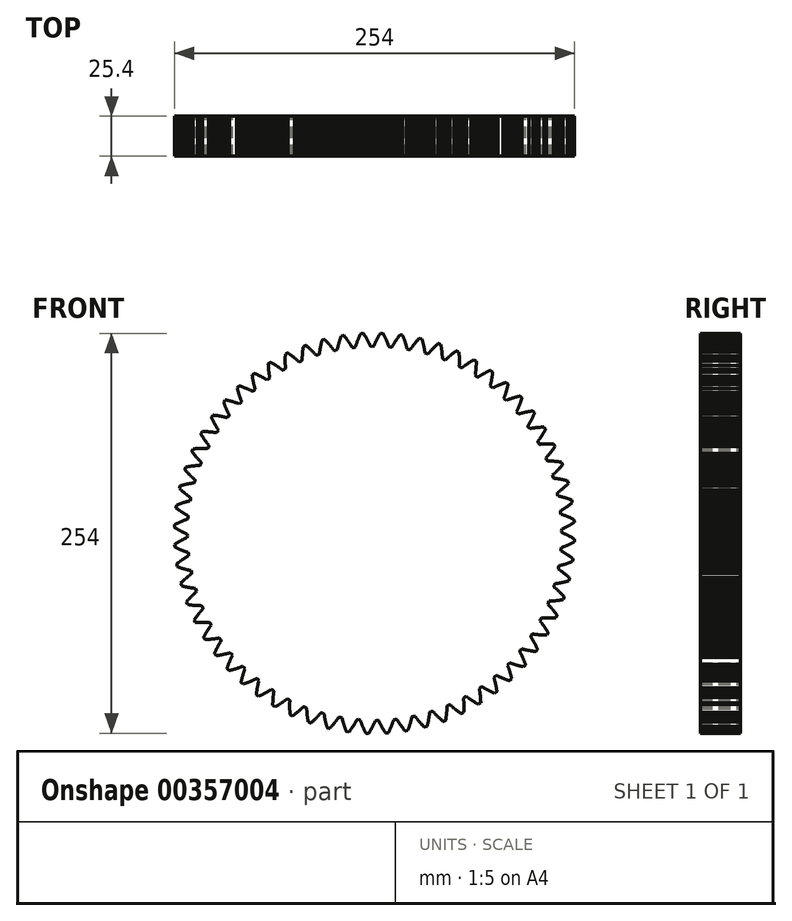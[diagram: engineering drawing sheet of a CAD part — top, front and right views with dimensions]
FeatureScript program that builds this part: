
annotation { "Feature Type Name" : "Feature", "Feature Type Description" : "" }
export const myFeature = defineFeature(function(context is Context, id is Id, definition is map)
    precondition{}
    {
        {
            var Q0;
            Q0=qCreatedBy(makeId("Front.planeOp"),FACE);
            var sketch = newSketch(context, id + "F0", { "sketchPlane" : qUnion([Q0])});
            skLineSegment(sketch, "E0", {"start": v(118.77, 2.66) * mm, "end": v(119, 3.75) * mm});
            skLineSegment(sketch, "E1", {"start": v(119, 3.75) * mm, "end": v(119.22, 3.85) * mm});
            skLineSegment(sketch, "E2", {"start": v(119.22, 3.85) * mm, "end": v(119.46, 3.96) * mm});
            skLineSegment(sketch, "E3", {"start": v(119.46, 3.96) * mm, "end": v(119.7, 4.07) * mm});
            skLineSegment(sketch, "E4", {"start": v(119.7, 4.07) * mm, "end": v(119.93, 4.18) * mm});
            skLineSegment(sketch, "E5", {"start": v(119.93, 4.18) * mm, "end": v(120.17, 4.3) * mm});
            skLineSegment(sketch, "E6", {"start": v(120.17, 4.3) * mm, "end": v(120.41, 4.4) * mm});
            skLineSegment(sketch, "E7", {"start": v(120.41, 4.4) * mm, "end": v(120.65, 4.53) * mm});
            skLineSegment(sketch, "E8", {"start": v(120.65, 4.53) * mm, "end": v(120.9, 4.65) * mm});
            skLineSegment(sketch, "E9", {"start": v(120.9, 4.65) * mm, "end": v(121.15, 4.78) * mm});
            skLineSegment(sketch, "E10", {"start": v(121.15, 4.78) * mm, "end": v(121.4, 4.9) * mm});
            skLineSegment(sketch, "E11", {"start": v(121.4, 4.9) * mm, "end": v(121.65, 5.03) * mm});
            skLineSegment(sketch, "E12", {"start": v(121.65, 5.03) * mm, "end": v(121.91, 5.17) * mm});
            skLineSegment(sketch, "E13", {"start": v(121.91, 5.17) * mm, "end": v(122.17, 5.3) * mm});
            skLineSegment(sketch, "E14", {"start": v(122.17, 5.3) * mm, "end": v(122.43, 5.44) * mm});
            skLineSegment(sketch, "E15", {"start": v(122.43, 5.44) * mm, "end": v(122.69, 5.59) * mm});
            skLineSegment(sketch, "E16", {"start": v(122.69, 5.59) * mm, "end": v(122.96, 5.73) * mm});
            skLineSegment(sketch, "E17", {"start": v(122.96, 5.73) * mm, "end": v(123.22, 5.88) * mm});
            skLineSegment(sketch, "E18", {"start": v(123.22, 5.88) * mm, "end": v(123.49, 6.03) * mm});
            skLineSegment(sketch, "E19", {"start": v(123.49, 6.03) * mm, "end": v(123.76, 6.19) * mm});
            skLineSegment(sketch, "E20", {"start": v(123.76, 6.19) * mm, "end": v(124.03, 6.34) * mm});
            skLineSegment(sketch, "E21", {"start": v(124.03, 6.34) * mm, "end": v(124.3, 6.5) * mm});
            skLineSegment(sketch, "E22", {"start": v(124.3, 6.5) * mm, "end": v(124.58, 6.67) * mm});
            skLineSegment(sketch, "E23", {"start": v(124.58, 6.67) * mm, "end": v(124.86, 6.84) * mm});
            skLineSegment(sketch, "E24", {"start": v(124.86, 6.84) * mm, "end": v(125.14, 7) * mm});
            skLineSegment(sketch, "E25", {"start": v(125.14, 7) * mm, "end": v(125.42, 7.18) * mm});
            skLineSegment(sketch, "E26", {"start": v(125.42, 7.18) * mm, "end": v(125.7, 7.36) * mm});
            skLineSegment(sketch, "E27", {"start": v(125.7, 7.36) * mm, "end": v(125.99, 7.54) * mm});
            skLineSegment(sketch, "E28", {"start": v(125.99, 7.54) * mm, "end": v(126.27, 7.72) * mm});
            skLineSegment(sketch, "E29", {"start": v(126.27, 7.72) * mm, "end": v(126.56, 7.9) * mm});
            skLineSegment(sketch, "E30", {"start": v(126.56, 7.9) * mm, "end": v(126.85, 8.1) * mm});
            skLineSegment(sketch, "E31", {"start": v(126.85, 8.1) * mm, "end": v(126.86, 8.27) * mm});
            skLineSegment(sketch, "E32", {"start": v(126.86, 8.27) * mm, "end": v(126.77, 9.72) * mm});
            skLineSegment(sketch, "E33", {"start": v(126.77, 9.72) * mm, "end": v(126.74, 9.9) * mm});
            skLineSegment(sketch, "E34", {"start": v(126.74, 9.9) * mm, "end": v(126.43, 10.05) * mm});
            skLineSegment(sketch, "E35", {"start": v(126.43, 10.05) * mm, "end": v(126.12, 10.2) * mm});
            skLineSegment(sketch, "E36", {"start": v(126.12, 10.2) * mm, "end": v(125.81, 10.34) * mm});
            skLineSegment(sketch, "E37", {"start": v(125.81, 10.34) * mm, "end": v(125.5, 10.49) * mm});
            skLineSegment(sketch, "E38", {"start": v(125.5, 10.49) * mm, "end": v(125.2, 10.63) * mm});
            skLineSegment(sketch, "E39", {"start": v(125.2, 10.63) * mm, "end": v(124.9, 10.76) * mm});
            skLineSegment(sketch, "E40", {"start": v(124.9, 10.76) * mm, "end": v(124.6, 10.9) * mm});
            skLineSegment(sketch, "E41", {"start": v(124.6, 10.9) * mm, "end": v(124.3, 11.03) * mm});
            skLineSegment(sketch, "E42", {"start": v(124.3, 11.03) * mm, "end": v(124.02, 11.16) * mm});
            skLineSegment(sketch, "E43", {"start": v(124.02, 11.16) * mm, "end": v(123.72, 11.28) * mm});
            skLineSegment(sketch, "E44", {"start": v(123.72, 11.28) * mm, "end": v(123.43, 11.4) * mm});
            skLineSegment(sketch, "E45", {"start": v(123.43, 11.4) * mm, "end": v(123.15, 11.53) * mm});
            skLineSegment(sketch, "E46", {"start": v(123.15, 11.53) * mm, "end": v(122.86, 11.64) * mm});
            skLineSegment(sketch, "E47", {"start": v(122.86, 11.64) * mm, "end": v(122.58, 11.76) * mm});
            skLineSegment(sketch, "E48", {"start": v(122.58, 11.76) * mm, "end": v(122.3, 11.87) * mm});
            skLineSegment(sketch, "E49", {"start": v(122.3, 11.87) * mm, "end": v(122.02, 11.98) * mm});
            skLineSegment(sketch, "E50", {"start": v(122.02, 11.98) * mm, "end": v(121.75, 12.09) * mm});
            skLineSegment(sketch, "E51", {"start": v(121.75, 12.09) * mm, "end": v(121.47, 12.19) * mm});
            skLineSegment(sketch, "E52", {"start": v(121.47, 12.19) * mm, "end": v(121.2, 12.29) * mm});
            skLineSegment(sketch, "E53", {"start": v(121.2, 12.29) * mm, "end": v(120.94, 12.39) * mm});
            skLineSegment(sketch, "E54", {"start": v(120.94, 12.39) * mm, "end": v(120.67, 12.48) * mm});
            skLineSegment(sketch, "E55", {"start": v(120.67, 12.48) * mm, "end": v(120.4, 12.58) * mm});
            skLineSegment(sketch, "E56", {"start": v(120.4, 12.58) * mm, "end": v(120.15, 12.67) * mm});
            skLineSegment(sketch, "E57", {"start": v(120.15, 12.67) * mm, "end": v(119.9, 12.75) * mm});
            skLineSegment(sketch, "E58", {"start": v(119.9, 12.75) * mm, "end": v(119.64, 12.84) * mm});
            skLineSegment(sketch, "E59", {"start": v(119.64, 12.84) * mm, "end": v(119.39, 12.92) * mm});
            skLineSegment(sketch, "E60", {"start": v(119.39, 12.92) * mm, "end": v(119.13, 13) * mm});
            skLineSegment(sketch, "E61", {"start": v(119.13, 13) * mm, "end": v(118.89, 13.08) * mm});
            skLineSegment(sketch, "E62", {"start": v(118.89, 13.08) * mm, "end": v(118.64, 13.16) * mm});
            skLineSegment(sketch, "E63", {"start": v(118.64, 13.16) * mm, "end": v(118.4, 13.23) * mm});
            skLineSegment(sketch, "E64", {"start": v(118.4, 13.23) * mm, "end": v(118.05, 14.3) * mm});
            skLineSegment(sketch, "E65", {"start": v(118.05, 14.3) * mm, "end": v(118.16, 15.4) * mm});
            skLineSegment(sketch, "E66", {"start": v(118.16, 15.4) * mm, "end": v(118.38, 15.52) * mm});
            skLineSegment(sketch, "E67", {"start": v(118.38, 15.52) * mm, "end": v(118.6, 15.65) * mm});
            skLineSegment(sketch, "E68", {"start": v(118.6, 15.65) * mm, "end": v(118.83, 15.78) * mm});
            skLineSegment(sketch, "E69", {"start": v(118.83, 15.78) * mm, "end": v(119.05, 15.92) * mm});
            skLineSegment(sketch, "E70", {"start": v(119.05, 15.92) * mm, "end": v(119.28, 16.05) * mm});
            skLineSegment(sketch, "E71", {"start": v(119.28, 16.05) * mm, "end": v(119.5, 16.2) * mm});
            skLineSegment(sketch, "E72", {"start": v(119.5, 16.2) * mm, "end": v(119.74, 16.34) * mm});
            skLineSegment(sketch, "E73", {"start": v(119.74, 16.34) * mm, "end": v(119.97, 16.48) * mm});
            skLineSegment(sketch, "E74", {"start": v(119.97, 16.48) * mm, "end": v(120.2, 16.63) * mm});
            skLineSegment(sketch, "E75", {"start": v(120.2, 16.63) * mm, "end": v(120.44, 16.78) * mm});
            skLineSegment(sketch, "E76", {"start": v(120.44, 16.78) * mm, "end": v(120.68, 16.94) * mm});
            skLineSegment(sketch, "E77", {"start": v(120.68, 16.94) * mm, "end": v(120.93, 17.1) * mm});
            skLineSegment(sketch, "E78", {"start": v(120.93, 17.1) * mm, "end": v(121.17, 17.26) * mm});
            skLineSegment(sketch, "E79", {"start": v(121.17, 17.26) * mm, "end": v(121.41, 17.42) * mm});
            skLineSegment(sketch, "E80", {"start": v(121.41, 17.42) * mm, "end": v(121.66, 17.59) * mm});
            skLineSegment(sketch, "E81", {"start": v(121.66, 17.59) * mm, "end": v(121.9, 17.76) * mm});
            skLineSegment(sketch, "E82", {"start": v(121.9, 17.76) * mm, "end": v(122.16, 17.93) * mm});
            skLineSegment(sketch, "E83", {"start": v(122.16, 17.93) * mm, "end": v(122.41, 18.11) * mm});
            skLineSegment(sketch, "E84", {"start": v(122.41, 18.11) * mm, "end": v(122.67, 18.3) * mm});
            skLineSegment(sketch, "E85", {"start": v(122.67, 18.3) * mm, "end": v(122.92, 18.47) * mm});
            skLineSegment(sketch, "E86", {"start": v(122.92, 18.47) * mm, "end": v(123.18, 18.66) * mm});
            skLineSegment(sketch, "E87", {"start": v(123.18, 18.66) * mm, "end": v(123.44, 18.85) * mm});
            skLineSegment(sketch, "E88", {"start": v(123.44, 18.85) * mm, "end": v(123.7, 19.05) * mm});
            skLineSegment(sketch, "E89", {"start": v(123.7, 19.05) * mm, "end": v(123.96, 19.24) * mm});
            skLineSegment(sketch, "E90", {"start": v(123.96, 19.24) * mm, "end": v(124.22, 19.44) * mm});
            skLineSegment(sketch, "E91", {"start": v(124.22, 19.44) * mm, "end": v(124.48, 19.65) * mm});
            skLineSegment(sketch, "E92", {"start": v(124.48, 19.65) * mm, "end": v(124.75, 19.85) * mm});
            skLineSegment(sketch, "E93", {"start": v(124.75, 19.85) * mm, "end": v(125.02, 20.06) * mm});
            skLineSegment(sketch, "E94", {"start": v(125.02, 20.06) * mm, "end": v(125.29, 20.28) * mm});
            skLineSegment(sketch, "E95", {"start": v(125.29, 20.28) * mm, "end": v(125.56, 20.5) * mm});
            skLineSegment(sketch, "E96", {"start": v(125.56, 20.5) * mm, "end": v(125.54, 20.67) * mm});
            skLineSegment(sketch, "E97", {"start": v(125.54, 20.67) * mm, "end": v(125.31, 22.1) * mm});
            skLineSegment(sketch, "E98", {"start": v(125.31, 22.1) * mm, "end": v(125.27, 22.27) * mm});
            skLineSegment(sketch, "E99", {"start": v(125.27, 22.27) * mm, "end": v(124.95, 22.4) * mm});
            skLineSegment(sketch, "E100", {"start": v(124.95, 22.4) * mm, "end": v(124.62, 22.51) * mm});
            skLineSegment(sketch, "E101", {"start": v(124.62, 22.51) * mm, "end": v(124.3, 22.63) * mm});
            skLineSegment(sketch, "E102", {"start": v(124.3, 22.63) * mm, "end": v(123.99, 22.74) * mm});
            skLineSegment(sketch, "E103", {"start": v(123.99, 22.74) * mm, "end": v(123.67, 22.85) * mm});
            skLineSegment(sketch, "E104", {"start": v(123.67, 22.85) * mm, "end": v(123.35, 22.96) * mm});
            skLineSegment(sketch, "E105", {"start": v(123.35, 22.96) * mm, "end": v(123.05, 23.06) * mm});
            skLineSegment(sketch, "E106", {"start": v(123.05, 23.06) * mm, "end": v(122.74, 23.17) * mm});
            skLineSegment(sketch, "E107", {"start": v(122.74, 23.17) * mm, "end": v(122.43, 23.27) * mm});
            skLineSegment(sketch, "E108", {"start": v(122.43, 23.27) * mm, "end": v(122.13, 23.36) * mm});
            skLineSegment(sketch, "E109", {"start": v(122.13, 23.36) * mm, "end": v(121.83, 23.46) * mm});
            skLineSegment(sketch, "E110", {"start": v(121.83, 23.46) * mm, "end": v(121.53, 23.55) * mm});
            skLineSegment(sketch, "E111", {"start": v(121.53, 23.55) * mm, "end": v(121.24, 23.64) * mm});
            skLineSegment(sketch, "E112", {"start": v(121.24, 23.64) * mm, "end": v(120.94, 23.72) * mm});
            skLineSegment(sketch, "E113", {"start": v(120.94, 23.72) * mm, "end": v(120.65, 23.8) * mm});
            skLineSegment(sketch, "E114", {"start": v(120.65, 23.8) * mm, "end": v(120.37, 23.89) * mm});
            skLineSegment(sketch, "E115", {"start": v(120.37, 23.89) * mm, "end": v(120.08, 23.96) * mm});
            skLineSegment(sketch, "E116", {"start": v(120.08, 23.96) * mm, "end": v(119.8, 24.04) * mm});
            skLineSegment(sketch, "E117", {"start": v(119.8, 24.04) * mm, "end": v(119.52, 24.12) * mm});
            skLineSegment(sketch, "E118", {"start": v(119.52, 24.12) * mm, "end": v(119.25, 24.19) * mm});
            skLineSegment(sketch, "E119", {"start": v(119.25, 24.19) * mm, "end": v(118.97, 24.26) * mm});
            skLineSegment(sketch, "E120", {"start": v(118.97, 24.26) * mm, "end": v(118.7, 24.32) * mm});
            skLineSegment(sketch, "E121", {"start": v(118.7, 24.32) * mm, "end": v(118.44, 24.39) * mm});
            skLineSegment(sketch, "E122", {"start": v(118.44, 24.39) * mm, "end": v(118.17, 24.45) * mm});
            skLineSegment(sketch, "E123", {"start": v(118.17, 24.45) * mm, "end": v(117.91, 24.51) * mm});
            skLineSegment(sketch, "E124", {"start": v(117.91, 24.51) * mm, "end": v(117.65, 24.57) * mm});
            skLineSegment(sketch, "E125", {"start": v(117.65, 24.57) * mm, "end": v(117.4, 24.63) * mm});
            skLineSegment(sketch, "E126", {"start": v(117.4, 24.63) * mm, "end": v(117.14, 24.68) * mm});
            skLineSegment(sketch, "E127", {"start": v(117.14, 24.68) * mm, "end": v(116.9, 24.73) * mm});
            skLineSegment(sketch, "E128", {"start": v(116.9, 24.73) * mm, "end": v(116.64, 24.78) * mm});
            skLineSegment(sketch, "E129", {"start": v(116.64, 24.78) * mm, "end": v(116.19, 25.8) * mm});
            skLineSegment(sketch, "E130", {"start": v(116.19, 25.8) * mm, "end": v(116.2, 26.91) * mm});
            skLineSegment(sketch, "E131", {"start": v(116.2, 26.91) * mm, "end": v(116.4, 27.06) * mm});
            skLineSegment(sketch, "E132", {"start": v(116.4, 27.06) * mm, "end": v(116.6, 27.2) * mm});
            skLineSegment(sketch, "E133", {"start": v(116.6, 27.2) * mm, "end": v(116.81, 27.36) * mm});
            skLineSegment(sketch, "E134", {"start": v(116.81, 27.36) * mm, "end": v(117.02, 27.52) * mm});
            skLineSegment(sketch, "E135", {"start": v(117.02, 27.52) * mm, "end": v(117.24, 27.67) * mm});
            skLineSegment(sketch, "E136", {"start": v(117.24, 27.67) * mm, "end": v(117.45, 27.84) * mm});
            skLineSegment(sketch, "E137", {"start": v(117.45, 27.84) * mm, "end": v(117.67, 28) * mm});
            skLineSegment(sketch, "E138", {"start": v(117.67, 28) * mm, "end": v(117.89, 28.17) * mm});
            skLineSegment(sketch, "E139", {"start": v(117.89, 28.17) * mm, "end": v(118.1, 28.34) * mm});
            skLineSegment(sketch, "E140", {"start": v(118.1, 28.34) * mm, "end": v(118.33, 28.51) * mm});
            skLineSegment(sketch, "E141", {"start": v(118.33, 28.51) * mm, "end": v(118.55, 28.7) * mm});
            skLineSegment(sketch, "E142", {"start": v(118.55, 28.7) * mm, "end": v(118.78, 28.87) * mm});
            skLineSegment(sketch, "E143", {"start": v(118.78, 28.87) * mm, "end": v(119, 29.06) * mm});
            skLineSegment(sketch, "E144", {"start": v(119, 29.06) * mm, "end": v(119.23, 29.24) * mm});
            skLineSegment(sketch, "E145", {"start": v(119.23, 29.24) * mm, "end": v(119.46, 29.44) * mm});
            skLineSegment(sketch, "E146", {"start": v(119.46, 29.44) * mm, "end": v(119.69, 29.63) * mm});
            skLineSegment(sketch, "E147", {"start": v(119.69, 29.63) * mm, "end": v(119.92, 29.83) * mm});
            skLineSegment(sketch, "E148", {"start": v(119.92, 29.83) * mm, "end": v(120.16, 30.03) * mm});
            skLineSegment(sketch, "E149", {"start": v(120.16, 30.03) * mm, "end": v(120.39, 30.23) * mm});
            skLineSegment(sketch, "E150", {"start": v(120.39, 30.23) * mm, "end": v(120.63, 30.44) * mm});
            skLineSegment(sketch, "E151", {"start": v(120.63, 30.44) * mm, "end": v(120.86, 30.65) * mm});
            skLineSegment(sketch, "E152", {"start": v(120.86, 30.65) * mm, "end": v(121.1, 30.87) * mm});
            skLineSegment(sketch, "E153", {"start": v(121.1, 30.87) * mm, "end": v(121.34, 31.08) * mm});
            skLineSegment(sketch, "E154", {"start": v(121.34, 31.08) * mm, "end": v(121.58, 31.3) * mm});
            skLineSegment(sketch, "E155", {"start": v(121.58, 31.3) * mm, "end": v(121.83, 31.53) * mm});
            skLineSegment(sketch, "E156", {"start": v(121.83, 31.53) * mm, "end": v(122.07, 31.76) * mm});
            skLineSegment(sketch, "E157", {"start": v(122.07, 31.76) * mm, "end": v(122.31, 32) * mm});
            skLineSegment(sketch, "E158", {"start": v(122.31, 32) * mm, "end": v(122.56, 32.23) * mm});
            skLineSegment(sketch, "E159", {"start": v(122.56, 32.23) * mm, "end": v(122.8, 32.47) * mm});
            skLineSegment(sketch, "E160", {"start": v(122.8, 32.47) * mm, "end": v(123.05, 32.71) * mm});
            skLineSegment(sketch, "E161", {"start": v(123.05, 32.71) * mm, "end": v(123.02, 32.88) * mm});
            skLineSegment(sketch, "E162", {"start": v(123.02, 32.88) * mm, "end": v(122.65, 34.28) * mm});
            skLineSegment(sketch, "E163", {"start": v(122.65, 34.28) * mm, "end": v(122.6, 34.45) * mm});
            skLineSegment(sketch, "E164", {"start": v(122.6, 34.45) * mm, "end": v(122.26, 34.54) * mm});
            skLineSegment(sketch, "E165", {"start": v(122.26, 34.54) * mm, "end": v(121.93, 34.63) * mm});
            skLineSegment(sketch, "E166", {"start": v(121.93, 34.63) * mm, "end": v(121.6, 34.71) * mm});
            skLineSegment(sketch, "E167", {"start": v(121.6, 34.71) * mm, "end": v(121.27, 34.8) * mm});
            skLineSegment(sketch, "E168", {"start": v(121.27, 34.8) * mm, "end": v(120.94, 34.87) * mm});
            skLineSegment(sketch, "E169", {"start": v(120.94, 34.87) * mm, "end": v(120.62, 34.95) * mm});
            skLineSegment(sketch, "E170", {"start": v(120.62, 34.95) * mm, "end": v(120.3, 35.02) * mm});
            skLineSegment(sketch, "E171", {"start": v(120.3, 35.02) * mm, "end": v(119.98, 35.1) * mm});
            skLineSegment(sketch, "E172", {"start": v(119.98, 35.1) * mm, "end": v(119.67, 35.16) * mm});
            skLineSegment(sketch, "E173", {"start": v(119.67, 35.16) * mm, "end": v(119.36, 35.22) * mm});
            skLineSegment(sketch, "E174", {"start": v(119.36, 35.22) * mm, "end": v(119.05, 35.29) * mm});
            skLineSegment(sketch, "E175", {"start": v(119.05, 35.29) * mm, "end": v(118.75, 35.35) * mm});
            skLineSegment(sketch, "E176", {"start": v(118.75, 35.35) * mm, "end": v(118.45, 35.41) * mm});
            skLineSegment(sketch, "E177", {"start": v(118.45, 35.41) * mm, "end": v(118.15, 35.47) * mm});
            skLineSegment(sketch, "E178", {"start": v(118.15, 35.47) * mm, "end": v(117.85, 35.52) * mm});
            skLineSegment(sketch, "E179", {"start": v(117.85, 35.52) * mm, "end": v(117.56, 35.58) * mm});
            skLineSegment(sketch, "E180", {"start": v(117.56, 35.58) * mm, "end": v(117.26, 35.63) * mm});
            skLineSegment(sketch, "E181", {"start": v(117.26, 35.63) * mm, "end": v(116.98, 35.67) * mm});
            skLineSegment(sketch, "E182", {"start": v(116.98, 35.67) * mm, "end": v(116.7, 35.72) * mm});
            skLineSegment(sketch, "E183", {"start": v(116.7, 35.72) * mm, "end": v(116.41, 35.76) * mm});
            skLineSegment(sketch, "E184", {"start": v(116.41, 35.76) * mm, "end": v(116.13, 35.8) * mm});
            skLineSegment(sketch, "E185", {"start": v(116.13, 35.8) * mm, "end": v(115.86, 35.85) * mm});
            skLineSegment(sketch, "E186", {"start": v(115.86, 35.85) * mm, "end": v(115.58, 35.88) * mm});
            skLineSegment(sketch, "E187", {"start": v(115.58, 35.88) * mm, "end": v(115.32, 35.92) * mm});
            skLineSegment(sketch, "E188", {"start": v(115.32, 35.92) * mm, "end": v(115.05, 35.96) * mm});
            skLineSegment(sketch, "E189", {"start": v(115.05, 35.96) * mm, "end": v(114.79, 35.99) * mm});
            skLineSegment(sketch, "E190", {"start": v(114.79, 35.99) * mm, "end": v(114.52, 36.02) * mm});
            skLineSegment(sketch, "E191", {"start": v(114.52, 36.02) * mm, "end": v(114.27, 36.05) * mm});
            skLineSegment(sketch, "E192", {"start": v(114.27, 36.05) * mm, "end": v(114.01, 36.08) * mm});
            skLineSegment(sketch, "E193", {"start": v(114.01, 36.08) * mm, "end": v(113.76, 36.1) * mm});
            skLineSegment(sketch, "E194", {"start": v(113.76, 36.1) * mm, "end": v(113.2, 37.07) * mm});
            skLineSegment(sketch, "E195", {"start": v(113.2, 37.07) * mm, "end": v(113.1, 38.18) * mm});
            skLineSegment(sketch, "E196", {"start": v(113.1, 38.18) * mm, "end": v(113.3, 38.34) * mm});
            skLineSegment(sketch, "E197", {"start": v(113.3, 38.34) * mm, "end": v(113.48, 38.51) * mm});
            skLineSegment(sketch, "E198", {"start": v(113.48, 38.51) * mm, "end": v(113.68, 38.68) * mm});
            skLineSegment(sketch, "E199", {"start": v(113.68, 38.68) * mm, "end": v(113.87, 38.86) * mm});
            skLineSegment(sketch, "E200", {"start": v(113.87, 38.86) * mm, "end": v(114.07, 39.04) * mm});
            skLineSegment(sketch, "E201", {"start": v(114.07, 39.04) * mm, "end": v(114.27, 39.22) * mm});
            skLineSegment(sketch, "E202", {"start": v(114.27, 39.22) * mm, "end": v(114.47, 39.4) * mm});
            skLineSegment(sketch, "E203", {"start": v(114.47, 39.4) * mm, "end": v(114.67, 39.6) * mm});
            skLineSegment(sketch, "E204", {"start": v(114.67, 39.6) * mm, "end": v(114.87, 39.78) * mm});
            skLineSegment(sketch, "E205", {"start": v(114.87, 39.78) * mm, "end": v(115.07, 39.98) * mm});
            skLineSegment(sketch, "E206", {"start": v(115.07, 39.98) * mm, "end": v(115.28, 40.18) * mm});
            skLineSegment(sketch, "E207", {"start": v(115.28, 40.18) * mm, "end": v(115.48, 40.38) * mm});
            skLineSegment(sketch, "E208", {"start": v(115.48, 40.38) * mm, "end": v(115.69, 40.59) * mm});
            skLineSegment(sketch, "E209", {"start": v(115.69, 40.59) * mm, "end": v(115.9, 40.8) * mm});
            skLineSegment(sketch, "E210", {"start": v(115.9, 40.8) * mm, "end": v(116.1, 41) * mm});
            skLineSegment(sketch, "E211", {"start": v(116.1, 41) * mm, "end": v(116.32, 41.22) * mm});
            skLineSegment(sketch, "E212", {"start": v(116.32, 41.22) * mm, "end": v(116.53, 41.44) * mm});
            skLineSegment(sketch, "E213", {"start": v(116.53, 41.44) * mm, "end": v(116.74, 41.67) * mm});
            skLineSegment(sketch, "E214", {"start": v(116.74, 41.67) * mm, "end": v(116.95, 41.9) * mm});
            skLineSegment(sketch, "E215", {"start": v(116.95, 41.9) * mm, "end": v(117.17, 42.12) * mm});
            skLineSegment(sketch, "E216", {"start": v(117.17, 42.12) * mm, "end": v(117.39, 42.35) * mm});
            skLineSegment(sketch, "E217", {"start": v(117.39, 42.35) * mm, "end": v(117.6, 42.6) * mm});
            skLineSegment(sketch, "E218", {"start": v(117.6, 42.6) * mm, "end": v(117.82, 42.83) * mm});
            skLineSegment(sketch, "E219", {"start": v(117.82, 42.83) * mm, "end": v(118.04, 43.08) * mm});
            skLineSegment(sketch, "E220", {"start": v(118.04, 43.08) * mm, "end": v(118.26, 43.32) * mm});
            skLineSegment(sketch, "E221", {"start": v(118.26, 43.32) * mm, "end": v(118.48, 43.58) * mm});
            skLineSegment(sketch, "E222", {"start": v(118.48, 43.58) * mm, "end": v(118.7, 43.83) * mm});
            skLineSegment(sketch, "E223", {"start": v(118.7, 43.83) * mm, "end": v(118.92, 44.1) * mm});
            skLineSegment(sketch, "E224", {"start": v(118.92, 44.1) * mm, "end": v(119.14, 44.35) * mm});
            skLineSegment(sketch, "E225", {"start": v(119.14, 44.35) * mm, "end": v(119.36, 44.62) * mm});
            skLineSegment(sketch, "E226", {"start": v(119.36, 44.62) * mm, "end": v(119.31, 44.79) * mm});
            skLineSegment(sketch, "E227", {"start": v(119.31, 44.79) * mm, "end": v(118.8, 46.15) * mm});
            skLineSegment(sketch, "E228", {"start": v(118.8, 46.15) * mm, "end": v(118.73, 46.3) * mm});
            skLineSegment(sketch, "E229", {"start": v(118.73, 46.3) * mm, "end": v(118.4, 46.36) * mm});
            skLineSegment(sketch, "E230", {"start": v(118.4, 46.36) * mm, "end": v(118.05, 46.42) * mm});
            skLineSegment(sketch, "E231", {"start": v(118.05, 46.42) * mm, "end": v(117.72, 46.47) * mm});
            skLineSegment(sketch, "E232", {"start": v(117.72, 46.47) * mm, "end": v(117.38, 46.51) * mm});
            skLineSegment(sketch, "E233", {"start": v(117.38, 46.51) * mm, "end": v(117.05, 46.56) * mm});
            skLineSegment(sketch, "E234", {"start": v(117.05, 46.56) * mm, "end": v(116.72, 46.6) * mm});
            skLineSegment(sketch, "E235", {"start": v(116.72, 46.6) * mm, "end": v(116.4, 46.65) * mm});
            skLineSegment(sketch, "E236", {"start": v(116.4, 46.65) * mm, "end": v(116.08, 46.69) * mm});
            skLineSegment(sketch, "E237", {"start": v(116.08, 46.69) * mm, "end": v(115.76, 46.73) * mm});
            skLineSegment(sketch, "E238", {"start": v(115.76, 46.73) * mm, "end": v(115.44, 46.76) * mm});
            skLineSegment(sketch, "E239", {"start": v(115.44, 46.76) * mm, "end": v(115.13, 46.8) * mm});
            skLineSegment(sketch, "E240", {"start": v(115.13, 46.8) * mm, "end": v(114.82, 46.83) * mm});
            skLineSegment(sketch, "E241", {"start": v(114.82, 46.83) * mm, "end": v(114.51, 46.85) * mm});
            skLineSegment(sketch, "E242", {"start": v(114.51, 46.85) * mm, "end": v(114.2, 46.88) * mm});
            skLineSegment(sketch, "E243", {"start": v(114.2, 46.88) * mm, "end": v(113.9, 46.9) * mm});
            skLineSegment(sketch, "E244", {"start": v(113.9, 46.9) * mm, "end": v(113.61, 46.93) * mm});
            skLineSegment(sketch, "E245", {"start": v(113.61, 46.93) * mm, "end": v(113.32, 46.95) * mm});
            skLineSegment(sketch, "E246", {"start": v(113.32, 46.95) * mm, "end": v(113.03, 46.97) * mm});
            skLineSegment(sketch, "E247", {"start": v(113.03, 46.97) * mm, "end": v(112.74, 47) * mm});
            skLineSegment(sketch, "E248", {"start": v(112.74, 47) * mm, "end": v(112.45, 47) * mm});
            skLineSegment(sketch, "E249", {"start": v(112.45, 47) * mm, "end": v(112.17, 47.02) * mm});
            skLineSegment(sketch, "E250", {"start": v(112.17, 47.02) * mm, "end": v(111.9, 47.04) * mm});
            skLineSegment(sketch, "E251", {"start": v(111.9, 47.04) * mm, "end": v(111.62, 47.05) * mm});
            skLineSegment(sketch, "E252", {"start": v(111.62, 47.05) * mm, "end": v(111.35, 47.06) * mm});
            skLineSegment(sketch, "E253", {"start": v(111.35, 47.06) * mm, "end": v(111.08, 47.06) * mm});
            skLineSegment(sketch, "E254", {"start": v(111.08, 47.06) * mm, "end": v(110.81, 47.07) * mm});
            skLineSegment(sketch, "E255", {"start": v(110.81, 47.07) * mm, "end": v(110.55, 47.08) * mm});
            skLineSegment(sketch, "E256", {"start": v(110.55, 47.08) * mm, "end": v(110.3, 47.08) * mm});
            skLineSegment(sketch, "E257", {"start": v(110.3, 47.08) * mm, "end": v(110.04, 47.08) * mm});
            skLineSegment(sketch, "E258", {"start": v(110.04, 47.08) * mm, "end": v(109.78, 47.08) * mm});
            skLineSegment(sketch, "E259", {"start": v(109.78, 47.08) * mm, "end": v(109.14, 48) * mm});
            skLineSegment(sketch, "E260", {"start": v(109.14, 48) * mm, "end": v(108.92, 49.08) * mm});
            skLineSegment(sketch, "E261", {"start": v(108.92, 49.08) * mm, "end": v(109.1, 49.27) * mm});
            skLineSegment(sketch, "E262", {"start": v(109.1, 49.27) * mm, "end": v(109.27, 49.45) * mm});
            skLineSegment(sketch, "E263", {"start": v(109.27, 49.45) * mm, "end": v(109.45, 49.64) * mm});
            skLineSegment(sketch, "E264", {"start": v(109.45, 49.64) * mm, "end": v(109.62, 49.84) * mm});
            skLineSegment(sketch, "E265", {"start": v(109.62, 49.84) * mm, "end": v(109.8, 50.04) * mm});
            skLineSegment(sketch, "E266", {"start": v(109.8, 50.04) * mm, "end": v(109.98, 50.24) * mm});
            skLineSegment(sketch, "E267", {"start": v(109.98, 50.24) * mm, "end": v(110.16, 50.44) * mm});
            skLineSegment(sketch, "E268", {"start": v(110.16, 50.44) * mm, "end": v(110.34, 50.65) * mm});
            skLineSegment(sketch, "E269", {"start": v(110.34, 50.65) * mm, "end": v(110.53, 50.86) * mm});
            skLineSegment(sketch, "E270", {"start": v(110.53, 50.86) * mm, "end": v(110.7, 51.07) * mm});
            skLineSegment(sketch, "E271", {"start": v(110.7, 51.07) * mm, "end": v(110.9, 51.3) * mm});
            skLineSegment(sketch, "E272", {"start": v(110.9, 51.3) * mm, "end": v(111.08, 51.51) * mm});
            skLineSegment(sketch, "E273", {"start": v(111.08, 51.51) * mm, "end": v(111.26, 51.74) * mm});
            skLineSegment(sketch, "E274", {"start": v(111.26, 51.74) * mm, "end": v(111.45, 51.96) * mm});
            skLineSegment(sketch, "E275", {"start": v(111.45, 51.96) * mm, "end": v(111.64, 52.2) * mm});
            skLineSegment(sketch, "E276", {"start": v(111.64, 52.2) * mm, "end": v(111.82, 52.43) * mm});
            skLineSegment(sketch, "E277", {"start": v(111.82, 52.43) * mm, "end": v(112.01, 52.67) * mm});
            skLineSegment(sketch, "E278", {"start": v(112.01, 52.67) * mm, "end": v(112.2, 52.91) * mm});
            skLineSegment(sketch, "E279", {"start": v(112.2, 52.91) * mm, "end": v(112.4, 53.16) * mm});
            skLineSegment(sketch, "E280", {"start": v(112.4, 53.16) * mm, "end": v(112.59, 53.4) * mm});
            skLineSegment(sketch, "E281", {"start": v(112.59, 53.4) * mm, "end": v(112.78, 53.66) * mm});
            skLineSegment(sketch, "E282", {"start": v(112.78, 53.66) * mm, "end": v(112.97, 53.92) * mm});
            skLineSegment(sketch, "E283", {"start": v(112.97, 53.92) * mm, "end": v(113.16, 54.18) * mm});
            skLineSegment(sketch, "E284", {"start": v(113.16, 54.18) * mm, "end": v(113.36, 54.44) * mm});
            skLineSegment(sketch, "E285", {"start": v(113.36, 54.44) * mm, "end": v(113.55, 54.71) * mm});
            skLineSegment(sketch, "E286", {"start": v(113.55, 54.71) * mm, "end": v(113.74, 54.98) * mm});
            skLineSegment(sketch, "E287", {"start": v(113.74, 54.98) * mm, "end": v(113.94, 55.26) * mm});
            skLineSegment(sketch, "E288", {"start": v(113.94, 55.26) * mm, "end": v(114.13, 55.54) * mm});
            skLineSegment(sketch, "E289", {"start": v(114.13, 55.54) * mm, "end": v(114.33, 55.82) * mm});
            skLineSegment(sketch, "E290", {"start": v(114.33, 55.82) * mm, "end": v(114.52, 56.1) * mm});
            skLineSegment(sketch, "E291", {"start": v(114.52, 56.1) * mm, "end": v(114.46, 56.27) * mm});
            skLineSegment(sketch, "E292", {"start": v(114.46, 56.27) * mm, "end": v(113.82, 57.57) * mm});
            skLineSegment(sketch, "E293", {"start": v(113.82, 57.57) * mm, "end": v(113.73, 57.73) * mm});
            skLineSegment(sketch, "E294", {"start": v(113.73, 57.73) * mm, "end": v(113.38, 57.75) * mm});
            skLineSegment(sketch, "E295", {"start": v(113.38, 57.75) * mm, "end": v(113.04, 57.77) * mm});
            skLineSegment(sketch, "E296", {"start": v(113.04, 57.77) * mm, "end": v(112.7, 57.79) * mm});
            skLineSegment(sketch, "E297", {"start": v(112.7, 57.79) * mm, "end": v(112.36, 57.8) * mm});
            skLineSegment(sketch, "E298", {"start": v(112.36, 57.8) * mm, "end": v(112.03, 57.82) * mm});
            skLineSegment(sketch, "E299", {"start": v(112.03, 57.82) * mm, "end": v(111.7, 57.83) * mm});
            skLineSegment(sketch, "E300", {"start": v(111.7, 57.83) * mm, "end": v(111.37, 57.84) * mm});
            skLineSegment(sketch, "E301", {"start": v(111.37, 57.84) * mm, "end": v(111.05, 57.85) * mm});
            skLineSegment(sketch, "E302", {"start": v(111.05, 57.85) * mm, "end": v(110.73, 57.85) * mm});
            skLineSegment(sketch, "E303", {"start": v(110.73, 57.85) * mm, "end": v(110.4, 57.86) * mm});
            skLineSegment(sketch, "E304", {"start": v(110.4, 57.86) * mm, "end": v(110.1, 57.86) * mm});
            skLineSegment(sketch, "E305", {"start": v(110.1, 57.86) * mm, "end": v(109.79, 57.86) * mm});
            skLineSegment(sketch, "E306", {"start": v(109.79, 57.86) * mm, "end": v(109.48, 57.86) * mm});
            skLineSegment(sketch, "E307", {"start": v(109.48, 57.86) * mm, "end": v(109.17, 57.86) * mm});
            skLineSegment(sketch, "E308", {"start": v(109.17, 57.86) * mm, "end": v(108.87, 57.85) * mm});
            skLineSegment(sketch, "E309", {"start": v(108.87, 57.85) * mm, "end": v(108.57, 57.85) * mm});
            skLineSegment(sketch, "E310", {"start": v(108.57, 57.85) * mm, "end": v(108.28, 57.84) * mm});
            skLineSegment(sketch, "E311", {"start": v(108.28, 57.84) * mm, "end": v(107.99, 57.83) * mm});
            skLineSegment(sketch, "E312", {"start": v(107.99, 57.83) * mm, "end": v(107.7, 57.82) * mm});
            skLineSegment(sketch, "E313", {"start": v(107.7, 57.82) * mm, "end": v(107.41, 57.8) * mm});
            skLineSegment(sketch, "E314", {"start": v(107.41, 57.8) * mm, "end": v(107.13, 57.8) * mm});
            skLineSegment(sketch, "E315", {"start": v(107.13, 57.8) * mm, "end": v(106.85, 57.78) * mm});
            skLineSegment(sketch, "E316", {"start": v(106.85, 57.78) * mm, "end": v(106.58, 57.76) * mm});
            skLineSegment(sketch, "E317", {"start": v(106.58, 57.76) * mm, "end": v(106.3, 57.75) * mm});
            skLineSegment(sketch, "E318", {"start": v(106.3, 57.75) * mm, "end": v(106.04, 57.73) * mm});
            skLineSegment(sketch, "E319", {"start": v(106.04, 57.73) * mm, "end": v(105.77, 57.71) * mm});
            skLineSegment(sketch, "E320", {"start": v(105.77, 57.71) * mm, "end": v(105.51, 57.69) * mm});
            skLineSegment(sketch, "E321", {"start": v(105.51, 57.69) * mm, "end": v(105.26, 57.67) * mm});
            skLineSegment(sketch, "E322", {"start": v(105.26, 57.67) * mm, "end": v(105, 57.64) * mm});
            skLineSegment(sketch, "E323", {"start": v(105, 57.64) * mm, "end": v(104.75, 57.62) * mm});
            skLineSegment(sketch, "E324", {"start": v(104.75, 57.62) * mm, "end": v(104.02, 58.46) * mm});
            skLineSegment(sketch, "E325", {"start": v(104.02, 58.46) * mm, "end": v(103.7, 59.53) * mm});
            skLineSegment(sketch, "E326", {"start": v(103.7, 59.53) * mm, "end": v(103.85, 59.73) * mm});
            skLineSegment(sketch, "E327", {"start": v(103.85, 59.73) * mm, "end": v(104, 59.93) * mm});
            skLineSegment(sketch, "E328", {"start": v(104, 59.93) * mm, "end": v(104.16, 60.14) * mm});
            skLineSegment(sketch, "E329", {"start": v(104.16, 60.14) * mm, "end": v(104.32, 60.35) * mm});
            skLineSegment(sketch, "E330", {"start": v(104.32, 60.35) * mm, "end": v(104.48, 60.56) * mm});
            skLineSegment(sketch, "E331", {"start": v(104.48, 60.56) * mm, "end": v(104.63, 60.78) * mm});
            skLineSegment(sketch, "E332", {"start": v(104.63, 60.78) * mm, "end": v(104.8, 61) * mm});
            skLineSegment(sketch, "E333", {"start": v(104.8, 61) * mm, "end": v(104.96, 61.22) * mm});
            skLineSegment(sketch, "E334", {"start": v(104.96, 61.22) * mm, "end": v(105.12, 61.45) * mm});
            skLineSegment(sketch, "E335", {"start": v(105.12, 61.45) * mm, "end": v(105.28, 61.68) * mm});
            skLineSegment(sketch, "E336", {"start": v(105.28, 61.68) * mm, "end": v(105.44, 61.92) * mm});
            skLineSegment(sketch, "E337", {"start": v(105.44, 61.92) * mm, "end": v(105.6, 62.16) * mm});
            skLineSegment(sketch, "E338", {"start": v(105.6, 62.16) * mm, "end": v(105.76, 62.4) * mm});
            skLineSegment(sketch, "E339", {"start": v(105.76, 62.4) * mm, "end": v(105.93, 62.64) * mm});
            skLineSegment(sketch, "E340", {"start": v(105.93, 62.64) * mm, "end": v(106.1, 62.9) * mm});
            skLineSegment(sketch, "E341", {"start": v(106.1, 62.9) * mm, "end": v(106.26, 63.14) * mm});
            skLineSegment(sketch, "E342", {"start": v(106.26, 63.14) * mm, "end": v(106.42, 63.4) * mm});
            skLineSegment(sketch, "E343", {"start": v(106.42, 63.4) * mm, "end": v(106.59, 63.66) * mm});
            skLineSegment(sketch, "E344", {"start": v(106.59, 63.66) * mm, "end": v(106.75, 63.93) * mm});
            skLineSegment(sketch, "E345", {"start": v(106.75, 63.93) * mm, "end": v(106.92, 64.2) * mm});
            skLineSegment(sketch, "E346", {"start": v(106.92, 64.2) * mm, "end": v(107.08, 64.46) * mm});
            skLineSegment(sketch, "E347", {"start": v(107.08, 64.46) * mm, "end": v(107.25, 64.74) * mm});
            skLineSegment(sketch, "E348", {"start": v(107.25, 64.74) * mm, "end": v(107.42, 65.02) * mm});
            skLineSegment(sketch, "E349", {"start": v(107.42, 65.02) * mm, "end": v(107.58, 65.3) * mm});
            skLineSegment(sketch, "E350", {"start": v(107.58, 65.3) * mm, "end": v(107.75, 65.58) * mm});
            skLineSegment(sketch, "E351", {"start": v(107.75, 65.58) * mm, "end": v(107.91, 65.87) * mm});
            skLineSegment(sketch, "E352", {"start": v(107.91, 65.87) * mm, "end": v(108.08, 66.17) * mm});
            skLineSegment(sketch, "E353", {"start": v(108.08, 66.17) * mm, "end": v(108.25, 66.46) * mm});
            skLineSegment(sketch, "E354", {"start": v(108.25, 66.46) * mm, "end": v(108.41, 66.77) * mm});
            skLineSegment(sketch, "E355", {"start": v(108.41, 66.77) * mm, "end": v(108.58, 67.07) * mm});
            skLineSegment(sketch, "E356", {"start": v(108.58, 67.07) * mm, "end": v(108.5, 67.23) * mm});
            skLineSegment(sketch, "E357", {"start": v(108.5, 67.23) * mm, "end": v(107.74, 68.46) * mm});
            skLineSegment(sketch, "E358", {"start": v(107.74, 68.46) * mm, "end": v(107.64, 68.6) * mm});
            skLineSegment(sketch, "E359", {"start": v(107.64, 68.6) * mm, "end": v(107.29, 68.6) * mm});
            skLineSegment(sketch, "E360", {"start": v(107.29, 68.6) * mm, "end": v(106.94, 68.58) * mm});
            skLineSegment(sketch, "E361", {"start": v(106.94, 68.58) * mm, "end": v(106.6, 68.56) * mm});
            skLineSegment(sketch, "E362", {"start": v(106.6, 68.56) * mm, "end": v(106.27, 68.54) * mm});
            skLineSegment(sketch, "E363", {"start": v(106.27, 68.54) * mm, "end": v(105.93, 68.52) * mm});
            skLineSegment(sketch, "E364", {"start": v(105.93, 68.52) * mm, "end": v(105.6, 68.5) * mm});
            skLineSegment(sketch, "E365", {"start": v(105.6, 68.5) * mm, "end": v(105.28, 68.48) * mm});
            skLineSegment(sketch, "E366", {"start": v(105.28, 68.48) * mm, "end": v(104.95, 68.46) * mm});
            skLineSegment(sketch, "E367", {"start": v(104.95, 68.46) * mm, "end": v(104.63, 68.43) * mm});
            skLineSegment(sketch, "E368", {"start": v(104.63, 68.43) * mm, "end": v(104.32, 68.4) * mm});
            skLineSegment(sketch, "E369", {"start": v(104.32, 68.4) * mm, "end": v(104, 68.38) * mm});
            skLineSegment(sketch, "E370", {"start": v(104, 68.38) * mm, "end": v(103.7, 68.35) * mm});
            skLineSegment(sketch, "E371", {"start": v(103.7, 68.35) * mm, "end": v(103.39, 68.32) * mm});
            skLineSegment(sketch, "E372", {"start": v(103.39, 68.32) * mm, "end": v(103.09, 68.28) * mm});
            skLineSegment(sketch, "E373", {"start": v(103.09, 68.28) * mm, "end": v(102.79, 68.25) * mm});
            skLineSegment(sketch, "E374", {"start": v(102.79, 68.25) * mm, "end": v(102.49, 68.21) * mm});
            skLineSegment(sketch, "E375", {"start": v(102.49, 68.21) * mm, "end": v(102.2, 68.18) * mm});
            skLineSegment(sketch, "E376", {"start": v(102.2, 68.18) * mm, "end": v(101.9, 68.14) * mm});
            skLineSegment(sketch, "E377", {"start": v(101.9, 68.14) * mm, "end": v(101.62, 68.1) * mm});
            skLineSegment(sketch, "E378", {"start": v(101.62, 68.1) * mm, "end": v(101.34, 68.06) * mm});
            skLineSegment(sketch, "E379", {"start": v(101.34, 68.06) * mm, "end": v(101.06, 68.02) * mm});
            skLineSegment(sketch, "E380", {"start": v(101.06, 68.02) * mm, "end": v(100.78, 67.98) * mm});
            skLineSegment(sketch, "E381", {"start": v(100.78, 67.98) * mm, "end": v(100.51, 67.94) * mm});
            skLineSegment(sketch, "E382", {"start": v(100.51, 67.94) * mm, "end": v(100.24, 67.9) * mm});
            skLineSegment(sketch, "E383", {"start": v(100.24, 67.9) * mm, "end": v(99.98, 67.85) * mm});
            skLineSegment(sketch, "E384", {"start": v(99.98, 67.85) * mm, "end": v(99.72, 67.8) * mm});
            skLineSegment(sketch, "E385", {"start": v(99.72, 67.8) * mm, "end": v(99.46, 67.76) * mm});
            skLineSegment(sketch, "E386", {"start": v(99.46, 67.76) * mm, "end": v(99.2, 67.71) * mm});
            skLineSegment(sketch, "E387", {"start": v(99.2, 67.71) * mm, "end": v(98.95, 67.66) * mm});
            skLineSegment(sketch, "E388", {"start": v(98.95, 67.66) * mm, "end": v(98.7, 67.62) * mm});
            skLineSegment(sketch, "E389", {"start": v(98.7, 67.62) * mm, "end": v(97.9, 68.38) * mm});
            skLineSegment(sketch, "E390", {"start": v(97.9, 68.38) * mm, "end": v(97.47, 69.41) * mm});
            skLineSegment(sketch, "E391", {"start": v(97.47, 69.41) * mm, "end": v(97.6, 69.63) * mm});
            skLineSegment(sketch, "E392", {"start": v(97.6, 69.63) * mm, "end": v(97.74, 69.84) * mm});
            skLineSegment(sketch, "E393", {"start": v(97.74, 69.84) * mm, "end": v(97.88, 70.06) * mm});
            skLineSegment(sketch, "E394", {"start": v(97.88, 70.06) * mm, "end": v(98.01, 70.29) * mm});
            skLineSegment(sketch, "E395", {"start": v(98.01, 70.29) * mm, "end": v(98.15, 70.52) * mm});
            skLineSegment(sketch, "E396", {"start": v(98.15, 70.52) * mm, "end": v(98.28, 70.75) * mm});
            skLineSegment(sketch, "E397", {"start": v(98.28, 70.75) * mm, "end": v(98.42, 70.98) * mm});
            skLineSegment(sketch, "E398", {"start": v(98.42, 70.98) * mm, "end": v(98.56, 71.22) * mm});
            skLineSegment(sketch, "E399", {"start": v(98.56, 71.22) * mm, "end": v(98.7, 71.46) * mm});
            skLineSegment(sketch, "E400", {"start": v(98.7, 71.46) * mm, "end": v(98.83, 71.7) * mm});
            skLineSegment(sketch, "E401", {"start": v(98.83, 71.7) * mm, "end": v(98.97, 71.96) * mm});
            skLineSegment(sketch, "E402", {"start": v(98.97, 71.96) * mm, "end": v(99.1, 72.21) * mm});
            skLineSegment(sketch, "E403", {"start": v(99.1, 72.21) * mm, "end": v(99.25, 72.47) * mm});
            skLineSegment(sketch, "E404", {"start": v(99.25, 72.47) * mm, "end": v(99.39, 72.73) * mm});
            skLineSegment(sketch, "E405", {"start": v(99.39, 72.73) * mm, "end": v(99.52, 73) * mm});
            skLineSegment(sketch, "E406", {"start": v(99.52, 73) * mm, "end": v(99.66, 73.26) * mm});
            skLineSegment(sketch, "E407", {"start": v(99.66, 73.26) * mm, "end": v(99.8, 73.53) * mm});
            skLineSegment(sketch, "E408", {"start": v(99.8, 73.53) * mm, "end": v(99.94, 73.8) * mm});
            skLineSegment(sketch, "E409", {"start": v(99.94, 73.8) * mm, "end": v(100.08, 74.09) * mm});
            skLineSegment(sketch, "E410", {"start": v(100.08, 74.09) * mm, "end": v(100.22, 74.37) * mm});
            skLineSegment(sketch, "E411", {"start": v(100.22, 74.37) * mm, "end": v(100.36, 74.65) * mm});
            skLineSegment(sketch, "E412", {"start": v(100.36, 74.65) * mm, "end": v(100.5, 74.94) * mm});
            skLineSegment(sketch, "E413", {"start": v(100.5, 74.94) * mm, "end": v(100.63, 75.24) * mm});
            skLineSegment(sketch, "E414", {"start": v(100.63, 75.24) * mm, "end": v(100.77, 75.53) * mm});
            skLineSegment(sketch, "E415", {"start": v(100.77, 75.53) * mm, "end": v(100.9, 75.83) * mm});
            skLineSegment(sketch, "E416", {"start": v(100.9, 75.83) * mm, "end": v(101.05, 76.14) * mm});
            skLineSegment(sketch, "E417", {"start": v(101.05, 76.14) * mm, "end": v(101.18, 76.45) * mm});
            skLineSegment(sketch, "E418", {"start": v(101.18, 76.45) * mm, "end": v(101.32, 76.76) * mm});
            skLineSegment(sketch, "E419", {"start": v(101.32, 76.76) * mm, "end": v(101.46, 77.08) * mm});
            skLineSegment(sketch, "E420", {"start": v(101.46, 77.08) * mm, "end": v(101.6, 77.4) * mm});
            skLineSegment(sketch, "E421", {"start": v(101.6, 77.4) * mm, "end": v(101.5, 77.54) * mm});
            skLineSegment(sketch, "E422", {"start": v(101.5, 77.54) * mm, "end": v(100.62, 78.7) * mm});
            skLineSegment(sketch, "E423", {"start": v(100.62, 78.7) * mm, "end": v(100.5, 78.83) * mm});
            skLineSegment(sketch, "E424", {"start": v(100.5, 78.83) * mm, "end": v(100.16, 78.78) * mm});
            skLineSegment(sketch, "E425", {"start": v(100.16, 78.78) * mm, "end": v(99.82, 78.73) * mm});
            skLineSegment(sketch, "E426", {"start": v(99.82, 78.73) * mm, "end": v(99.48, 78.68) * mm});
            skLineSegment(sketch, "E427", {"start": v(99.48, 78.68) * mm, "end": v(99.14, 78.63) * mm});
            skLineSegment(sketch, "E428", {"start": v(99.14, 78.63) * mm, "end": v(98.82, 78.58) * mm});
            skLineSegment(sketch, "E429", {"start": v(98.82, 78.58) * mm, "end": v(98.49, 78.53) * mm});
            skLineSegment(sketch, "E430", {"start": v(98.49, 78.53) * mm, "end": v(98.16, 78.48) * mm});
            skLineSegment(sketch, "E431", {"start": v(98.16, 78.48) * mm, "end": v(97.85, 78.42) * mm});
            skLineSegment(sketch, "E432", {"start": v(97.85, 78.42) * mm, "end": v(97.53, 78.36) * mm});
            skLineSegment(sketch, "E433", {"start": v(97.53, 78.36) * mm, "end": v(97.22, 78.3) * mm});
            skLineSegment(sketch, "E434", {"start": v(97.22, 78.3) * mm, "end": v(96.9, 78.25) * mm});
            skLineSegment(sketch, "E435", {"start": v(96.9, 78.25) * mm, "end": v(96.6, 78.19) * mm});
            skLineSegment(sketch, "E436", {"start": v(96.6, 78.19) * mm, "end": v(96.3, 78.13) * mm});
            skLineSegment(sketch, "E437", {"start": v(96.3, 78.13) * mm, "end": v(96, 78.06) * mm});
            skLineSegment(sketch, "E438", {"start": v(96, 78.06) * mm, "end": v(95.7, 78) * mm});
            skLineSegment(sketch, "E439", {"start": v(95.7, 78) * mm, "end": v(95.42, 77.94) * mm});
            skLineSegment(sketch, "E440", {"start": v(95.42, 77.94) * mm, "end": v(95.13, 77.87) * mm});
            skLineSegment(sketch, "E441", {"start": v(95.13, 77.87) * mm, "end": v(94.84, 77.8) * mm});
            skLineSegment(sketch, "E442", {"start": v(94.84, 77.8) * mm, "end": v(94.56, 77.74) * mm});
            skLineSegment(sketch, "E443", {"start": v(94.56, 77.74) * mm, "end": v(94.29, 77.67) * mm});
            skLineSegment(sketch, "E444", {"start": v(94.29, 77.67) * mm, "end": v(94.01, 77.6) * mm});
            skLineSegment(sketch, "E445", {"start": v(94.01, 77.6) * mm, "end": v(93.74, 77.54) * mm});
            skLineSegment(sketch, "E446", {"start": v(93.74, 77.54) * mm, "end": v(93.48, 77.47) * mm});
            skLineSegment(sketch, "E447", {"start": v(93.48, 77.47) * mm, "end": v(93.21, 77.4) * mm});
            skLineSegment(sketch, "E448", {"start": v(93.21, 77.4) * mm, "end": v(92.95, 77.33) * mm});
            skLineSegment(sketch, "E449", {"start": v(92.95, 77.33) * mm, "end": v(92.7, 77.26) * mm});
            skLineSegment(sketch, "E450", {"start": v(92.7, 77.26) * mm, "end": v(92.45, 77.19) * mm});
            skLineSegment(sketch, "E451", {"start": v(92.45, 77.19) * mm, "end": v(92.2, 77.12) * mm});
            skLineSegment(sketch, "E452", {"start": v(92.2, 77.12) * mm, "end": v(91.95, 77.04) * mm});
            skLineSegment(sketch, "E453", {"start": v(91.95, 77.04) * mm, "end": v(91.71, 76.97) * mm});
            skLineSegment(sketch, "E454", {"start": v(91.71, 76.97) * mm, "end": v(90.83, 77.65) * mm});
            skLineSegment(sketch, "E455", {"start": v(90.83, 77.65) * mm, "end": v(90.3, 78.64) * mm});
            skLineSegment(sketch, "E456", {"start": v(90.3, 78.64) * mm, "end": v(90.42, 78.86) * mm});
            skLineSegment(sketch, "E457", {"start": v(90.42, 78.86) * mm, "end": v(90.53, 79.1) * mm});
            skLineSegment(sketch, "E458", {"start": v(90.53, 79.1) * mm, "end": v(90.65, 79.33) * mm});
            skLineSegment(sketch, "E459", {"start": v(90.65, 79.33) * mm, "end": v(90.76, 79.56) * mm});
            skLineSegment(sketch, "E460", {"start": v(90.76, 79.56) * mm, "end": v(90.87, 79.8) * mm});
            skLineSegment(sketch, "E461", {"start": v(90.87, 79.8) * mm, "end": v(90.98, 80.05) * mm});
            skLineSegment(sketch, "E462", {"start": v(90.98, 80.05) * mm, "end": v(91.1, 80.3) * mm});
            skLineSegment(sketch, "E463", {"start": v(91.1, 80.3) * mm, "end": v(91.21, 80.55) * mm});
            skLineSegment(sketch, "E464", {"start": v(91.21, 80.55) * mm, "end": v(91.32, 80.8) * mm});
            skLineSegment(sketch, "E465", {"start": v(91.32, 80.8) * mm, "end": v(91.44, 81.06) * mm});
            skLineSegment(sketch, "E466", {"start": v(91.44, 81.06) * mm, "end": v(91.55, 81.32) * mm});
            skLineSegment(sketch, "E467", {"start": v(91.55, 81.32) * mm, "end": v(91.66, 81.58) * mm});
            skLineSegment(sketch, "E468", {"start": v(91.66, 81.58) * mm, "end": v(91.77, 81.85) * mm});
            skLineSegment(sketch, "E469", {"start": v(91.77, 81.85) * mm, "end": v(91.89, 82.13) * mm});
            skLineSegment(sketch, "E470", {"start": v(91.89, 82.13) * mm, "end": v(92, 82.4) * mm});
            skLineSegment(sketch, "E471", {"start": v(92, 82.4) * mm, "end": v(92.11, 82.68) * mm});
            skLineSegment(sketch, "E472", {"start": v(92.11, 82.68) * mm, "end": v(92.22, 82.97) * mm});
            skLineSegment(sketch, "E473", {"start": v(92.22, 82.97) * mm, "end": v(92.33, 83.25) * mm});
            skLineSegment(sketch, "E474", {"start": v(92.33, 83.25) * mm, "end": v(92.44, 83.54) * mm});
            skLineSegment(sketch, "E475", {"start": v(92.44, 83.54) * mm, "end": v(92.55, 83.84) * mm});
            skLineSegment(sketch, "E476", {"start": v(92.55, 83.84) * mm, "end": v(92.66, 84.14) * mm});
            skLineSegment(sketch, "E477", {"start": v(92.66, 84.14) * mm, "end": v(92.77, 84.44) * mm});
            skLineSegment(sketch, "E478", {"start": v(92.77, 84.44) * mm, "end": v(92.88, 84.74) * mm});
            skLineSegment(sketch, "E479", {"start": v(92.88, 84.74) * mm, "end": v(93, 85.05) * mm});
            skLineSegment(sketch, "E480", {"start": v(93, 85.05) * mm, "end": v(93.1, 85.36) * mm});
            skLineSegment(sketch, "E481", {"start": v(93.1, 85.36) * mm, "end": v(93.2, 85.68) * mm});
            skLineSegment(sketch, "E482", {"start": v(93.2, 85.68) * mm, "end": v(93.31, 86) * mm});
            skLineSegment(sketch, "E483", {"start": v(93.31, 86) * mm, "end": v(93.42, 86.32) * mm});
            skLineSegment(sketch, "E484", {"start": v(93.42, 86.32) * mm, "end": v(93.52, 86.65) * mm});
            skLineSegment(sketch, "E485", {"start": v(93.52, 86.65) * mm, "end": v(93.62, 86.98) * mm});
            skLineSegment(sketch, "E486", {"start": v(93.62, 86.98) * mm, "end": v(93.51, 87.12) * mm});
            skLineSegment(sketch, "E487", {"start": v(93.51, 87.12) * mm, "end": v(92.53, 88.18) * mm});
            skLineSegment(sketch, "E488", {"start": v(92.53, 88.18) * mm, "end": v(92.4, 88.3) * mm});
            skLineSegment(sketch, "E489", {"start": v(92.4, 88.3) * mm, "end": v(92.06, 88.22) * mm});
            skLineSegment(sketch, "E490", {"start": v(92.06, 88.22) * mm, "end": v(91.73, 88.14) * mm});
            skLineSegment(sketch, "E491", {"start": v(91.73, 88.14) * mm, "end": v(91.4, 88.06) * mm});
            skLineSegment(sketch, "E492", {"start": v(91.4, 88.06) * mm, "end": v(91.07, 87.98) * mm});
            skLineSegment(sketch, "E493", {"start": v(91.07, 87.98) * mm, "end": v(90.75, 87.9) * mm});
            skLineSegment(sketch, "E494", {"start": v(90.75, 87.9) * mm, "end": v(90.43, 87.81) * mm});
            skLineSegment(sketch, "E495", {"start": v(90.43, 87.81) * mm, "end": v(90.1, 87.72) * mm});
            skLineSegment(sketch, "E496", {"start": v(90.1, 87.72) * mm, "end": v(89.8, 87.64) * mm});
            skLineSegment(sketch, "E497", {"start": v(89.8, 87.64) * mm, "end": v(89.49, 87.55) * mm});
            skLineSegment(sketch, "E498", {"start": v(89.49, 87.55) * mm, "end": v(89.18, 87.46) * mm});
            skLineSegment(sketch, "E499", {"start": v(89.18, 87.46) * mm, "end": v(88.88, 87.37) * mm});
            skLineSegment(sketch, "E500", {"start": v(88.88, 87.37) * mm, "end": v(88.58, 87.28) * mm});
            skLineSegment(sketch, "E501", {"start": v(88.58, 87.28) * mm, "end": v(88.3, 87.2) * mm});
            skLineSegment(sketch, "E502", {"start": v(88.3, 87.2) * mm, "end": v(88, 87.1) * mm});
            skLineSegment(sketch, "E503", {"start": v(88, 87.1) * mm, "end": v(87.71, 87.01) * mm});
            skLineSegment(sketch, "E504", {"start": v(87.71, 87.01) * mm, "end": v(87.43, 86.92) * mm});
            skLineSegment(sketch, "E505", {"start": v(87.43, 86.92) * mm, "end": v(87.15, 86.83) * mm});
            skLineSegment(sketch, "E506", {"start": v(87.15, 86.83) * mm, "end": v(86.87, 86.73) * mm});
            skLineSegment(sketch, "E507", {"start": v(86.87, 86.73) * mm, "end": v(86.6, 86.64) * mm});
            skLineSegment(sketch, "E508", {"start": v(86.6, 86.64) * mm, "end": v(86.33, 86.55) * mm});
            skLineSegment(sketch, "E509", {"start": v(86.33, 86.55) * mm, "end": v(86.06, 86.45) * mm});
            skLineSegment(sketch, "E510", {"start": v(86.06, 86.45) * mm, "end": v(85.8, 86.36) * mm});
            skLineSegment(sketch, "E511", {"start": v(85.8, 86.36) * mm, "end": v(85.54, 86.26) * mm});
            skLineSegment(sketch, "E512", {"start": v(85.54, 86.26) * mm, "end": v(85.29, 86.17) * mm});
            skLineSegment(sketch, "E513", {"start": v(85.29, 86.17) * mm, "end": v(85.04, 86.07) * mm});
            skLineSegment(sketch, "E514", {"start": v(85.04, 86.07) * mm, "end": v(84.79, 85.98) * mm});
            skLineSegment(sketch, "E515", {"start": v(84.79, 85.98) * mm, "end": v(84.54, 85.88) * mm});
            skLineSegment(sketch, "E516", {"start": v(84.54, 85.88) * mm, "end": v(84.3, 85.79) * mm});
            skLineSegment(sketch, "E517", {"start": v(84.3, 85.79) * mm, "end": v(84.07, 85.7) * mm});
            skLineSegment(sketch, "E518", {"start": v(84.07, 85.7) * mm, "end": v(83.83, 85.6) * mm});
            skLineSegment(sketch, "E519", {"start": v(83.83, 85.6) * mm, "end": v(82.89, 86.19) * mm});
            skLineSegment(sketch, "E520", {"start": v(82.89, 86.19) * mm, "end": v(82.27, 87.11) * mm});
            skLineSegment(sketch, "E521", {"start": v(82.27, 87.11) * mm, "end": v(82.36, 87.35) * mm});
            skLineSegment(sketch, "E522", {"start": v(82.36, 87.35) * mm, "end": v(82.45, 87.6) * mm});
            skLineSegment(sketch, "E523", {"start": v(82.45, 87.6) * mm, "end": v(82.54, 87.83) * mm});
            skLineSegment(sketch, "E524", {"start": v(82.54, 87.83) * mm, "end": v(82.63, 88.08) * mm});
            skLineSegment(sketch, "E525", {"start": v(82.63, 88.08) * mm, "end": v(82.72, 88.33) * mm});
            skLineSegment(sketch, "E526", {"start": v(82.72, 88.33) * mm, "end": v(82.8, 88.58) * mm});
            skLineSegment(sketch, "E527", {"start": v(82.8, 88.58) * mm, "end": v(82.9, 88.84) * mm});
            skLineSegment(sketch, "E528", {"start": v(82.9, 88.84) * mm, "end": v(82.99, 89.1) * mm});
            skLineSegment(sketch, "E529", {"start": v(82.99, 89.1) * mm, "end": v(83.07, 89.37) * mm});
            skLineSegment(sketch, "E530", {"start": v(83.07, 89.37) * mm, "end": v(83.16, 89.63) * mm});
            skLineSegment(sketch, "E531", {"start": v(83.16, 89.63) * mm, "end": v(83.25, 89.9) * mm});
            skLineSegment(sketch, "E532", {"start": v(83.25, 89.9) * mm, "end": v(83.33, 90.18) * mm});
            skLineSegment(sketch, "E533", {"start": v(83.33, 90.18) * mm, "end": v(83.42, 90.46) * mm});
            skLineSegment(sketch, "E534", {"start": v(83.42, 90.46) * mm, "end": v(83.5, 90.74) * mm});
            skLineSegment(sketch, "E535", {"start": v(83.5, 90.74) * mm, "end": v(83.59, 91.03) * mm});
            skLineSegment(sketch, "E536", {"start": v(83.59, 91.03) * mm, "end": v(83.67, 91.32) * mm});
            skLineSegment(sketch, "E537", {"start": v(83.67, 91.32) * mm, "end": v(83.76, 91.61) * mm});
            skLineSegment(sketch, "E538", {"start": v(83.76, 91.61) * mm, "end": v(83.84, 91.9) * mm});
            skLineSegment(sketch, "E539", {"start": v(83.84, 91.9) * mm, "end": v(83.92, 92.2) * mm});
            skLineSegment(sketch, "E540", {"start": v(83.92, 92.2) * mm, "end": v(84, 92.51) * mm});
            skLineSegment(sketch, "E541", {"start": v(84, 92.51) * mm, "end": v(84.08, 92.82) * mm});
            skLineSegment(sketch, "E542", {"start": v(84.08, 92.82) * mm, "end": v(84.16, 93.13) * mm});
            skLineSegment(sketch, "E543", {"start": v(84.16, 93.13) * mm, "end": v(84.24, 93.45) * mm});
            skLineSegment(sketch, "E544", {"start": v(84.24, 93.45) * mm, "end": v(84.31, 93.76) * mm});
            skLineSegment(sketch, "E545", {"start": v(84.31, 93.76) * mm, "end": v(84.39, 94.09) * mm});
            skLineSegment(sketch, "E546", {"start": v(84.39, 94.09) * mm, "end": v(84.47, 94.4) * mm});
            skLineSegment(sketch, "E547", {"start": v(84.47, 94.4) * mm, "end": v(84.54, 94.74) * mm});
            skLineSegment(sketch, "E548", {"start": v(84.54, 94.74) * mm, "end": v(84.61, 95.07) * mm});
            skLineSegment(sketch, "E549", {"start": v(84.61, 95.07) * mm, "end": v(84.69, 95.4) * mm});
            skLineSegment(sketch, "E550", {"start": v(84.69, 95.4) * mm, "end": v(84.76, 95.75) * mm});
            skLineSegment(sketch, "E551", {"start": v(84.76, 95.75) * mm, "end": v(84.63, 95.88) * mm});
            skLineSegment(sketch, "E552", {"start": v(84.63, 95.88) * mm, "end": v(83.55, 96.83) * mm});
            skLineSegment(sketch, "E553", {"start": v(83.55, 96.83) * mm, "end": v(83.4, 96.94) * mm});
            skLineSegment(sketch, "E554", {"start": v(83.4, 96.94) * mm, "end": v(83.08, 96.83) * mm});
            skLineSegment(sketch, "E555", {"start": v(83.08, 96.83) * mm, "end": v(82.75, 96.71) * mm});
            skLineSegment(sketch, "E556", {"start": v(82.75, 96.71) * mm, "end": v(82.43, 96.6) * mm});
            skLineSegment(sketch, "E557", {"start": v(82.43, 96.6) * mm, "end": v(82.11, 96.49) * mm});
            skLineSegment(sketch, "E558", {"start": v(82.11, 96.49) * mm, "end": v(81.8, 96.37) * mm});
            skLineSegment(sketch, "E559", {"start": v(81.8, 96.37) * mm, "end": v(81.5, 96.26) * mm});
            skLineSegment(sketch, "E560", {"start": v(81.5, 96.26) * mm, "end": v(81.19, 96.14) * mm});
            skLineSegment(sketch, "E561", {"start": v(81.19, 96.14) * mm, "end": v(80.88, 96.02) * mm});
            skLineSegment(sketch, "E562", {"start": v(80.88, 96.02) * mm, "end": v(80.59, 95.9) * mm});
            skLineSegment(sketch, "E563", {"start": v(80.59, 95.9) * mm, "end": v(80.29, 95.79) * mm});
            skLineSegment(sketch, "E564", {"start": v(80.29, 95.79) * mm, "end": v(80, 95.67) * mm});
            skLineSegment(sketch, "E565", {"start": v(80, 95.67) * mm, "end": v(79.7, 95.55) * mm});
            skLineSegment(sketch, "E566", {"start": v(79.7, 95.55) * mm, "end": v(79.42, 95.43) * mm});
            skLineSegment(sketch, "E567", {"start": v(79.42, 95.43) * mm, "end": v(79.14, 95.31) * mm});
            skLineSegment(sketch, "E568", {"start": v(79.14, 95.31) * mm, "end": v(78.87, 95.2) * mm});
            skLineSegment(sketch, "E569", {"start": v(78.87, 95.2) * mm, "end": v(78.6, 95.07) * mm});
            skLineSegment(sketch, "E570", {"start": v(78.6, 95.07) * mm, "end": v(78.32, 94.96) * mm});
            skLineSegment(sketch, "E571", {"start": v(78.32, 94.96) * mm, "end": v(78.06, 94.84) * mm});
            skLineSegment(sketch, "E572", {"start": v(78.06, 94.84) * mm, "end": v(77.8, 94.72) * mm});
            skLineSegment(sketch, "E573", {"start": v(77.8, 94.72) * mm, "end": v(77.54, 94.6) * mm});
            skLineSegment(sketch, "E574", {"start": v(77.54, 94.6) * mm, "end": v(77.28, 94.48) * mm});
            skLineSegment(sketch, "E575", {"start": v(77.28, 94.48) * mm, "end": v(77.03, 94.36) * mm});
            skLineSegment(sketch, "E576", {"start": v(77.03, 94.36) * mm, "end": v(76.78, 94.24) * mm});
            skLineSegment(sketch, "E577", {"start": v(76.78, 94.24) * mm, "end": v(76.54, 94.12) * mm});
            skLineSegment(sketch, "E578", {"start": v(76.54, 94.12) * mm, "end": v(76.3, 94) * mm});
            skLineSegment(sketch, "E579", {"start": v(76.3, 94) * mm, "end": v(76.06, 93.88) * mm});
            skLineSegment(sketch, "E580", {"start": v(76.06, 93.88) * mm, "end": v(75.83, 93.76) * mm});
            skLineSegment(sketch, "E581", {"start": v(75.83, 93.76) * mm, "end": v(75.6, 93.64) * mm});
            skLineSegment(sketch, "E582", {"start": v(75.6, 93.64) * mm, "end": v(75.37, 93.52) * mm});
            skLineSegment(sketch, "E583", {"start": v(75.37, 93.52) * mm, "end": v(75.15, 93.4) * mm});
            skLineSegment(sketch, "E584", {"start": v(75.15, 93.4) * mm, "end": v(74.15, 93.9) * mm});
            skLineSegment(sketch, "E585", {"start": v(74.15, 93.9) * mm, "end": v(73.45, 94.77) * mm});
            skLineSegment(sketch, "E586", {"start": v(73.45, 94.77) * mm, "end": v(73.51, 95) * mm});
            skLineSegment(sketch, "E587", {"start": v(73.51, 95) * mm, "end": v(73.58, 95.26) * mm});
            skLineSegment(sketch, "E588", {"start": v(73.58, 95.26) * mm, "end": v(73.64, 95.5) * mm});
            skLineSegment(sketch, "E589", {"start": v(73.64, 95.5) * mm, "end": v(73.7, 95.76) * mm});
            skLineSegment(sketch, "E590", {"start": v(73.7, 95.76) * mm, "end": v(73.77, 96.02) * mm});
            skLineSegment(sketch, "E591", {"start": v(73.77, 96.02) * mm, "end": v(73.83, 96.28) * mm});
            skLineSegment(sketch, "E592", {"start": v(73.83, 96.28) * mm, "end": v(73.9, 96.54) * mm});
            skLineSegment(sketch, "E593", {"start": v(73.9, 96.54) * mm, "end": v(73.96, 96.81) * mm});
            skLineSegment(sketch, "E594", {"start": v(73.96, 96.81) * mm, "end": v(74.02, 97.08) * mm});
            skLineSegment(sketch, "E595", {"start": v(74.02, 97.08) * mm, "end": v(74.08, 97.36) * mm});
            skLineSegment(sketch, "E596", {"start": v(74.08, 97.36) * mm, "end": v(74.14, 97.64) * mm});
            skLineSegment(sketch, "E597", {"start": v(74.14, 97.64) * mm, "end": v(74.2, 97.92) * mm});
            skLineSegment(sketch, "E598", {"start": v(74.2, 97.92) * mm, "end": v(74.26, 98.2) * mm});
            skLineSegment(sketch, "E599", {"start": v(74.26, 98.2) * mm, "end": v(74.32, 98.5) * mm});
            skLineSegment(sketch, "E600", {"start": v(74.32, 98.5) * mm, "end": v(74.37, 98.79) * mm});
            skLineSegment(sketch, "E601", {"start": v(74.37, 98.79) * mm, "end": v(74.43, 99.08) * mm});
            skLineSegment(sketch, "E602", {"start": v(74.43, 99.08) * mm, "end": v(74.48, 99.38) * mm});
            skLineSegment(sketch, "E603", {"start": v(74.48, 99.38) * mm, "end": v(74.53, 99.69) * mm});
            skLineSegment(sketch, "E604", {"start": v(74.53, 99.69) * mm, "end": v(74.59, 100) * mm});
            skLineSegment(sketch, "E605", {"start": v(74.59, 100) * mm, "end": v(74.64, 100.3) * mm});
            skLineSegment(sketch, "E606", {"start": v(74.64, 100.3) * mm, "end": v(74.69, 100.62) * mm});
            skLineSegment(sketch, "E607", {"start": v(74.69, 100.62) * mm, "end": v(74.73, 100.94) * mm});
            skLineSegment(sketch, "E608", {"start": v(74.73, 100.94) * mm, "end": v(74.78, 101.26) * mm});
            skLineSegment(sketch, "E609", {"start": v(74.78, 101.26) * mm, "end": v(74.83, 101.58) * mm});
            skLineSegment(sketch, "E610", {"start": v(74.83, 101.58) * mm, "end": v(74.87, 101.9) * mm});
            skLineSegment(sketch, "E611", {"start": v(74.87, 101.9) * mm, "end": v(74.91, 102.24) * mm});
            skLineSegment(sketch, "E612", {"start": v(74.91, 102.24) * mm, "end": v(74.96, 102.58) * mm});
            skLineSegment(sketch, "E613", {"start": v(74.96, 102.58) * mm, "end": v(75, 102.91) * mm});
            skLineSegment(sketch, "E614", {"start": v(75, 102.91) * mm, "end": v(75.04, 103.26) * mm});
            skLineSegment(sketch, "E615", {"start": v(75.04, 103.26) * mm, "end": v(75.07, 103.6) * mm});
            skLineSegment(sketch, "E616", {"start": v(75.07, 103.6) * mm, "end": v(74.94, 103.72) * mm});
            skLineSegment(sketch, "E617", {"start": v(74.94, 103.72) * mm, "end": v(73.76, 104.56) * mm});
            skLineSegment(sketch, "E618", {"start": v(73.76, 104.56) * mm, "end": v(73.61, 104.66) * mm});
            skLineSegment(sketch, "E619", {"start": v(73.61, 104.66) * mm, "end": v(73.3, 104.5) * mm});
            skLineSegment(sketch, "E620", {"start": v(73.3, 104.5) * mm, "end": v(72.98, 104.37) * mm});
            skLineSegment(sketch, "E621", {"start": v(72.98, 104.37) * mm, "end": v(72.68, 104.22) * mm});
            skLineSegment(sketch, "E622", {"start": v(72.68, 104.22) * mm, "end": v(72.37, 104.08) * mm});
            skLineSegment(sketch, "E623", {"start": v(72.37, 104.08) * mm, "end": v(72.07, 103.93) * mm});
            skLineSegment(sketch, "E624", {"start": v(72.07, 103.93) * mm, "end": v(71.77, 103.78) * mm});
            skLineSegment(sketch, "E625", {"start": v(71.77, 103.78) * mm, "end": v(71.48, 103.64) * mm});
            skLineSegment(sketch, "E626", {"start": v(71.48, 103.64) * mm, "end": v(71.19, 103.5) * mm});
            skLineSegment(sketch, "E627", {"start": v(71.19, 103.5) * mm, "end": v(70.9, 103.35) * mm});
            skLineSegment(sketch, "E628", {"start": v(70.9, 103.35) * mm, "end": v(70.62, 103.2) * mm});
            skLineSegment(sketch, "E629", {"start": v(70.62, 103.2) * mm, "end": v(70.34, 103.06) * mm});
            skLineSegment(sketch, "E630", {"start": v(70.34, 103.06) * mm, "end": v(70.07, 102.9) * mm});
            skLineSegment(sketch, "E631", {"start": v(70.07, 102.9) * mm, "end": v(69.8, 102.76) * mm});
            skLineSegment(sketch, "E632", {"start": v(69.8, 102.76) * mm, "end": v(69.53, 102.62) * mm});
            skLineSegment(sketch, "E633", {"start": v(69.53, 102.62) * mm, "end": v(69.27, 102.47) * mm});
            skLineSegment(sketch, "E634", {"start": v(69.27, 102.47) * mm, "end": v(69, 102.33) * mm});
            skLineSegment(sketch, "E635", {"start": v(69, 102.33) * mm, "end": v(68.75, 102.18) * mm});
            skLineSegment(sketch, "E636", {"start": v(68.75, 102.18) * mm, "end": v(68.5, 102.04) * mm});
            skLineSegment(sketch, "E637", {"start": v(68.5, 102.04) * mm, "end": v(68.25, 101.9) * mm});
            skLineSegment(sketch, "E638", {"start": v(68.25, 101.9) * mm, "end": v(68, 101.75) * mm});
            skLineSegment(sketch, "E639", {"start": v(68, 101.75) * mm, "end": v(67.76, 101.6) * mm});
            skLineSegment(sketch, "E640", {"start": v(67.76, 101.6) * mm, "end": v(67.52, 101.46) * mm});
            skLineSegment(sketch, "E641", {"start": v(67.52, 101.46) * mm, "end": v(67.28, 101.32) * mm});
            skLineSegment(sketch, "E642", {"start": v(67.28, 101.32) * mm, "end": v(67.05, 101.17) * mm});
            skLineSegment(sketch, "E643", {"start": v(67.05, 101.17) * mm, "end": v(66.83, 101.03) * mm});
            skLineSegment(sketch, "E644", {"start": v(66.83, 101.03) * mm, "end": v(66.6, 100.89) * mm});
            skLineSegment(sketch, "E645", {"start": v(66.6, 100.89) * mm, "end": v(66.38, 100.75) * mm});
            skLineSegment(sketch, "E646", {"start": v(66.38, 100.75) * mm, "end": v(66.16, 100.6) * mm});
            skLineSegment(sketch, "E647", {"start": v(66.16, 100.6) * mm, "end": v(65.95, 100.47) * mm});
            skLineSegment(sketch, "E648", {"start": v(65.95, 100.47) * mm, "end": v(65.74, 100.33) * mm});
            skLineSegment(sketch, "E649", {"start": v(65.74, 100.33) * mm, "end": v(64.7, 100.72) * mm});
            skLineSegment(sketch, "E650", {"start": v(64.7, 100.72) * mm, "end": v(63.91, 101.51) * mm});
            skLineSegment(sketch, "E651", {"start": v(63.91, 101.51) * mm, "end": v(63.95, 101.76) * mm});
            skLineSegment(sketch, "E652", {"start": v(63.95, 101.76) * mm, "end": v(64, 102.01) * mm});
            skLineSegment(sketch, "E653", {"start": v(64, 102.01) * mm, "end": v(64.04, 102.27) * mm});
            skLineSegment(sketch, "E654", {"start": v(64.04, 102.27) * mm, "end": v(64.08, 102.53) * mm});
            skLineSegment(sketch, "E655", {"start": v(64.08, 102.53) * mm, "end": v(64.11, 102.8) * mm});
            skLineSegment(sketch, "E656", {"start": v(64.11, 102.8) * mm, "end": v(64.15, 103.06) * mm});
            skLineSegment(sketch, "E657", {"start": v(64.15, 103.06) * mm, "end": v(64.19, 103.33) * mm});
            skLineSegment(sketch, "E658", {"start": v(64.19, 103.33) * mm, "end": v(64.22, 103.6) * mm});
            skLineSegment(sketch, "E659", {"start": v(64.22, 103.6) * mm, "end": v(64.26, 103.88) * mm});
            skLineSegment(sketch, "E660", {"start": v(64.26, 103.88) * mm, "end": v(64.3, 104.16) * mm});
            skLineSegment(sketch, "E661", {"start": v(64.3, 104.16) * mm, "end": v(64.32, 104.44) * mm});
            skLineSegment(sketch, "E662", {"start": v(64.32, 104.44) * mm, "end": v(64.35, 104.73) * mm});
            skLineSegment(sketch, "E663", {"start": v(64.35, 104.73) * mm, "end": v(64.38, 105.02) * mm});
            skLineSegment(sketch, "E664", {"start": v(64.38, 105.02) * mm, "end": v(64.41, 105.31) * mm});
            skLineSegment(sketch, "E665", {"start": v(64.41, 105.31) * mm, "end": v(64.44, 105.6) * mm});
            skLineSegment(sketch, "E666", {"start": v(64.44, 105.6) * mm, "end": v(64.46, 105.9) * mm});
            skLineSegment(sketch, "E667", {"start": v(64.46, 105.9) * mm, "end": v(64.49, 106.21) * mm});
            skLineSegment(sketch, "E668", {"start": v(64.49, 106.21) * mm, "end": v(64.51, 106.52) * mm});
            skLineSegment(sketch, "E669", {"start": v(64.51, 106.52) * mm, "end": v(64.53, 106.83) * mm});
            skLineSegment(sketch, "E670", {"start": v(64.53, 106.83) * mm, "end": v(64.55, 107.14) * mm});
            skLineSegment(sketch, "E671", {"start": v(64.55, 107.14) * mm, "end": v(64.57, 107.46) * mm});
            skLineSegment(sketch, "E672", {"start": v(64.57, 107.46) * mm, "end": v(64.59, 107.78) * mm});
            skLineSegment(sketch, "E673", {"start": v(64.59, 107.78) * mm, "end": v(64.6, 108.1) * mm});
            skLineSegment(sketch, "E674", {"start": v(64.6, 108.1) * mm, "end": v(64.62, 108.43) * mm});
            skLineSegment(sketch, "E675", {"start": v(64.62, 108.43) * mm, "end": v(64.63, 108.76) * mm});
            skLineSegment(sketch, "E676", {"start": v(64.63, 108.76) * mm, "end": v(64.64, 109.1) * mm});
            skLineSegment(sketch, "E677", {"start": v(64.64, 109.1) * mm, "end": v(64.65, 109.43) * mm});
            skLineSegment(sketch, "E678", {"start": v(64.65, 109.43) * mm, "end": v(64.66, 109.77) * mm});
            skLineSegment(sketch, "E679", {"start": v(64.66, 109.77) * mm, "end": v(64.66, 110.12) * mm});
            skLineSegment(sketch, "E680", {"start": v(64.66, 110.12) * mm, "end": v(64.67, 110.46) * mm});
            skLineSegment(sketch, "E681", {"start": v(64.67, 110.46) * mm, "end": v(64.52, 110.57) * mm});
            skLineSegment(sketch, "E682", {"start": v(64.52, 110.57) * mm, "end": v(63.27, 111.3) * mm});
            skLineSegment(sketch, "E683", {"start": v(63.27, 111.3) * mm, "end": v(63.1, 111.37) * mm});
            skLineSegment(sketch, "E684", {"start": v(63.1, 111.37) * mm, "end": v(62.8, 111.2) * mm});
            skLineSegment(sketch, "E685", {"start": v(62.8, 111.2) * mm, "end": v(62.51, 111.02) * mm});
            skLineSegment(sketch, "E686", {"start": v(62.51, 111.02) * mm, "end": v(62.22, 110.85) * mm});
            skLineSegment(sketch, "E687", {"start": v(62.22, 110.85) * mm, "end": v(61.93, 110.67) * mm});
            skLineSegment(sketch, "E688", {"start": v(61.93, 110.67) * mm, "end": v(61.64, 110.5) * mm});
            skLineSegment(sketch, "E689", {"start": v(61.64, 110.5) * mm, "end": v(61.36, 110.33) * mm});
            skLineSegment(sketch, "E690", {"start": v(61.36, 110.33) * mm, "end": v(61.09, 110.15) * mm});
            skLineSegment(sketch, "E691", {"start": v(61.09, 110.15) * mm, "end": v(60.81, 109.98) * mm});
            skLineSegment(sketch, "E692", {"start": v(60.81, 109.98) * mm, "end": v(60.54, 109.8) * mm});
            skLineSegment(sketch, "E693", {"start": v(60.54, 109.8) * mm, "end": v(60.28, 109.63) * mm});
            skLineSegment(sketch, "E694", {"start": v(60.28, 109.63) * mm, "end": v(60.01, 109.46) * mm});
            skLineSegment(sketch, "E695", {"start": v(60.01, 109.46) * mm, "end": v(59.75, 109.29) * mm});
            skLineSegment(sketch, "E696", {"start": v(59.75, 109.29) * mm, "end": v(59.5, 109.11) * mm});
            skLineSegment(sketch, "E697", {"start": v(59.5, 109.11) * mm, "end": v(59.24, 108.94) * mm});
            skLineSegment(sketch, "E698", {"start": v(59.24, 108.94) * mm, "end": v(59, 108.77) * mm});
            skLineSegment(sketch, "E699", {"start": v(59, 108.77) * mm, "end": v(58.75, 108.6) * mm});
            skLineSegment(sketch, "E700", {"start": v(58.75, 108.6) * mm, "end": v(58.51, 108.43) * mm});
            skLineSegment(sketch, "E701", {"start": v(58.51, 108.43) * mm, "end": v(58.27, 108.26) * mm});
            skLineSegment(sketch, "E702", {"start": v(58.27, 108.26) * mm, "end": v(58.04, 108.1) * mm});
            skLineSegment(sketch, "E703", {"start": v(58.04, 108.1) * mm, "end": v(57.8, 107.93) * mm});
            skLineSegment(sketch, "E704", {"start": v(57.8, 107.93) * mm, "end": v(57.58, 107.76) * mm});
            skLineSegment(sketch, "E705", {"start": v(57.58, 107.76) * mm, "end": v(57.36, 107.6) * mm});
            skLineSegment(sketch, "E706", {"start": v(57.36, 107.6) * mm, "end": v(57.14, 107.43) * mm});
            skLineSegment(sketch, "E707", {"start": v(57.14, 107.43) * mm, "end": v(56.92, 107.26) * mm});
            skLineSegment(sketch, "E708", {"start": v(56.92, 107.26) * mm, "end": v(56.71, 107.1) * mm});
            skLineSegment(sketch, "E709", {"start": v(56.71, 107.1) * mm, "end": v(56.5, 106.94) * mm});
            skLineSegment(sketch, "E710", {"start": v(56.5, 106.94) * mm, "end": v(56.3, 106.77) * mm});
            skLineSegment(sketch, "E711", {"start": v(56.3, 106.77) * mm, "end": v(56.1, 106.61) * mm});
            skLineSegment(sketch, "E712", {"start": v(56.1, 106.61) * mm, "end": v(55.9, 106.45) * mm});
            skLineSegment(sketch, "E713", {"start": v(55.9, 106.45) * mm, "end": v(55.7, 106.3) * mm});
            skLineSegment(sketch, "E714", {"start": v(55.7, 106.3) * mm, "end": v(54.62, 106.58) * mm});
            skLineSegment(sketch, "E715", {"start": v(54.62, 106.58) * mm, "end": v(53.76, 107.3) * mm});
            skLineSegment(sketch, "E716", {"start": v(53.76, 107.3) * mm, "end": v(53.78, 107.55) * mm});
            skLineSegment(sketch, "E717", {"start": v(53.78, 107.55) * mm, "end": v(53.8, 107.8) * mm});
            skLineSegment(sketch, "E718", {"start": v(53.8, 107.8) * mm, "end": v(53.81, 108.06) * mm});
            skLineSegment(sketch, "E719", {"start": v(53.81, 108.06) * mm, "end": v(53.83, 108.32) * mm});
            skLineSegment(sketch, "E720", {"start": v(53.83, 108.32) * mm, "end": v(53.84, 108.59) * mm});
            skLineSegment(sketch, "E721", {"start": v(53.84, 108.59) * mm, "end": v(53.85, 108.85) * mm});
            skLineSegment(sketch, "E722", {"start": v(53.85, 108.85) * mm, "end": v(53.86, 109.13) * mm});
            skLineSegment(sketch, "E723", {"start": v(53.86, 109.13) * mm, "end": v(53.87, 109.4) * mm});
            skLineSegment(sketch, "E724", {"start": v(53.87, 109.4) * mm, "end": v(53.87, 109.68) * mm});
            skLineSegment(sketch, "E725", {"start": v(53.87, 109.68) * mm, "end": v(53.88, 109.96) * mm});
            skLineSegment(sketch, "E726", {"start": v(53.88, 109.96) * mm, "end": v(53.89, 110.25) * mm});
            skLineSegment(sketch, "E727", {"start": v(53.89, 110.25) * mm, "end": v(53.89, 110.54) * mm});
            skLineSegment(sketch, "E728", {"start": v(53.89, 110.54) * mm, "end": v(53.89, 110.83) * mm});
            skLineSegment(sketch, "E729", {"start": v(53.89, 110.83) * mm, "end": v(53.89, 111.12) * mm});
            skLineSegment(sketch, "E730", {"start": v(53.89, 111.12) * mm, "end": v(53.89, 111.42) * mm});
            skLineSegment(sketch, "E731", {"start": v(53.89, 111.42) * mm, "end": v(53.88, 111.72) * mm});
            skLineSegment(sketch, "E732", {"start": v(53.88, 111.72) * mm, "end": v(53.88, 112.03) * mm});
            skLineSegment(sketch, "E733", {"start": v(53.88, 112.03) * mm, "end": v(53.87, 112.33) * mm});
            skLineSegment(sketch, "E734", {"start": v(53.87, 112.33) * mm, "end": v(53.86, 112.65) * mm});
            skLineSegment(sketch, "E735", {"start": v(53.86, 112.65) * mm, "end": v(53.85, 112.96) * mm});
            skLineSegment(sketch, "E736", {"start": v(53.85, 112.96) * mm, "end": v(53.84, 113.28) * mm});
            skLineSegment(sketch, "E737", {"start": v(53.84, 113.28) * mm, "end": v(53.82, 113.6) * mm});
            skLineSegment(sketch, "E738", {"start": v(53.82, 113.6) * mm, "end": v(53.8, 113.92) * mm});
            skLineSegment(sketch, "E739", {"start": v(53.8, 113.92) * mm, "end": v(53.79, 114.25) * mm});
            skLineSegment(sketch, "E740", {"start": v(53.79, 114.25) * mm, "end": v(53.77, 114.58) * mm});
            skLineSegment(sketch, "E741", {"start": v(53.77, 114.58) * mm, "end": v(53.74, 114.91) * mm});
            skLineSegment(sketch, "E742", {"start": v(53.74, 114.91) * mm, "end": v(53.72, 115.25) * mm});
            skLineSegment(sketch, "E743", {"start": v(53.72, 115.25) * mm, "end": v(53.7, 115.59) * mm});
            skLineSegment(sketch, "E744", {"start": v(53.7, 115.59) * mm, "end": v(53.66, 115.93) * mm});
            skLineSegment(sketch, "E745", {"start": v(53.66, 115.93) * mm, "end": v(53.63, 116.28) * mm});
            skLineSegment(sketch, "E746", {"start": v(53.63, 116.28) * mm, "end": v(53.48, 116.36) * mm});
            skLineSegment(sketch, "E747", {"start": v(53.48, 116.36) * mm, "end": v(52.16, 116.96) * mm});
            skLineSegment(sketch, "E748", {"start": v(52.16, 116.96) * mm, "end": v(52, 117.02) * mm});
            skLineSegment(sketch, "E749", {"start": v(52, 117.02) * mm, "end": v(51.71, 116.82) * mm});
            skLineSegment(sketch, "E750", {"start": v(51.71, 116.82) * mm, "end": v(51.44, 116.62) * mm});
            skLineSegment(sketch, "E751", {"start": v(51.44, 116.62) * mm, "end": v(51.16, 116.42) * mm});
            skLineSegment(sketch, "E752", {"start": v(51.16, 116.42) * mm, "end": v(50.9, 116.22) * mm});
            skLineSegment(sketch, "E753", {"start": v(50.9, 116.22) * mm, "end": v(50.63, 116.01) * mm});
            skLineSegment(sketch, "E754", {"start": v(50.63, 116.01) * mm, "end": v(50.36, 115.82) * mm});
            skLineSegment(sketch, "E755", {"start": v(50.36, 115.82) * mm, "end": v(50.1, 115.61) * mm});
            skLineSegment(sketch, "E756", {"start": v(50.1, 115.61) * mm, "end": v(49.85, 115.41) * mm});
            skLineSegment(sketch, "E757", {"start": v(49.85, 115.41) * mm, "end": v(49.6, 115.22) * mm});
            skLineSegment(sketch, "E758", {"start": v(49.6, 115.22) * mm, "end": v(49.35, 115.02) * mm});
            skLineSegment(sketch, "E759", {"start": v(49.35, 115.02) * mm, "end": v(49.1, 114.82) * mm});
            skLineSegment(sketch, "E760", {"start": v(49.1, 114.82) * mm, "end": v(48.86, 114.62) * mm});
            skLineSegment(sketch, "E761", {"start": v(48.86, 114.62) * mm, "end": v(48.62, 114.43) * mm});
            skLineSegment(sketch, "E762", {"start": v(48.62, 114.43) * mm, "end": v(48.39, 114.23) * mm});
            skLineSegment(sketch, "E763", {"start": v(48.39, 114.23) * mm, "end": v(48.16, 114.04) * mm});
            skLineSegment(sketch, "E764", {"start": v(48.16, 114.04) * mm, "end": v(47.93, 113.84) * mm});
            skLineSegment(sketch, "E765", {"start": v(47.93, 113.84) * mm, "end": v(47.7, 113.65) * mm});
            skLineSegment(sketch, "E766", {"start": v(47.7, 113.65) * mm, "end": v(47.49, 113.46) * mm});
            skLineSegment(sketch, "E767", {"start": v(47.49, 113.46) * mm, "end": v(47.27, 113.27) * mm});
            skLineSegment(sketch, "E768", {"start": v(47.27, 113.27) * mm, "end": v(47.06, 113.08) * mm});
            skLineSegment(sketch, "E769", {"start": v(47.06, 113.08) * mm, "end": v(46.85, 112.9) * mm});
            skLineSegment(sketch, "E770", {"start": v(46.85, 112.9) * mm, "end": v(46.65, 112.7) * mm});
            skLineSegment(sketch, "E771", {"start": v(46.65, 112.7) * mm, "end": v(46.44, 112.52) * mm});
            skLineSegment(sketch, "E772", {"start": v(46.44, 112.52) * mm, "end": v(46.24, 112.33) * mm});
            skLineSegment(sketch, "E773", {"start": v(46.24, 112.33) * mm, "end": v(46.05, 112.15) * mm});
            skLineSegment(sketch, "E774", {"start": v(46.05, 112.15) * mm, "end": v(45.86, 111.97) * mm});
            skLineSegment(sketch, "E775", {"start": v(45.86, 111.97) * mm, "end": v(45.67, 111.78) * mm});
            skLineSegment(sketch, "E776", {"start": v(45.67, 111.78) * mm, "end": v(45.48, 111.6) * mm});
            skLineSegment(sketch, "E777", {"start": v(45.48, 111.6) * mm, "end": v(45.3, 111.42) * mm});
            skLineSegment(sketch, "E778", {"start": v(45.3, 111.42) * mm, "end": v(45.12, 111.25) * mm});
            skLineSegment(sketch, "E779", {"start": v(45.12, 111.25) * mm, "end": v(44.02, 111.43) * mm});
            skLineSegment(sketch, "E780", {"start": v(44.02, 111.43) * mm, "end": v(43.1, 112.05) * mm});
            skLineSegment(sketch, "E781", {"start": v(43.1, 112.05) * mm, "end": v(43.09, 112.3) * mm});
            skLineSegment(sketch, "E782", {"start": v(43.09, 112.3) * mm, "end": v(43.08, 112.56) * mm});
            skLineSegment(sketch, "E783", {"start": v(43.08, 112.56) * mm, "end": v(43.07, 112.82) * mm});
            skLineSegment(sketch, "E784", {"start": v(43.07, 112.82) * mm, "end": v(43.06, 113.08) * mm});
            skLineSegment(sketch, "E785", {"start": v(43.06, 113.08) * mm, "end": v(43.04, 113.34) * mm});
            skLineSegment(sketch, "E786", {"start": v(43.04, 113.34) * mm, "end": v(43.03, 113.61) * mm});
            skLineSegment(sketch, "E787", {"start": v(43.03, 113.61) * mm, "end": v(43.01, 113.89) * mm});
            skLineSegment(sketch, "E788", {"start": v(43.01, 113.89) * mm, "end": v(43, 114.16) * mm});
            skLineSegment(sketch, "E789", {"start": v(43, 114.16) * mm, "end": v(42.97, 114.44) * mm});
            skLineSegment(sketch, "E790", {"start": v(42.97, 114.44) * mm, "end": v(42.95, 114.72) * mm});
            skLineSegment(sketch, "E791", {"start": v(42.95, 114.72) * mm, "end": v(42.93, 115) * mm});
            skLineSegment(sketch, "E792", {"start": v(42.93, 115) * mm, "end": v(42.9, 115.3) * mm});
            skLineSegment(sketch, "E793", {"start": v(42.9, 115.3) * mm, "end": v(42.87, 115.58) * mm});
            skLineSegment(sketch, "E794", {"start": v(42.87, 115.58) * mm, "end": v(42.85, 115.87) * mm});
            skLineSegment(sketch, "E795", {"start": v(42.85, 115.87) * mm, "end": v(42.81, 116.17) * mm});
            skLineSegment(sketch, "E796", {"start": v(42.81, 116.17) * mm, "end": v(42.78, 116.47) * mm});
            skLineSegment(sketch, "E797", {"start": v(42.78, 116.47) * mm, "end": v(42.74, 116.77) * mm});
            skLineSegment(sketch, "E798", {"start": v(42.74, 116.77) * mm, "end": v(42.7, 117.08) * mm});
            skLineSegment(sketch, "E799", {"start": v(42.7, 117.08) * mm, "end": v(42.67, 117.39) * mm});
            skLineSegment(sketch, "E800", {"start": v(42.67, 117.39) * mm, "end": v(42.63, 117.7) * mm});
            skLineSegment(sketch, "E801", {"start": v(42.63, 117.7) * mm, "end": v(42.58, 118.02) * mm});
            skLineSegment(sketch, "E802", {"start": v(42.58, 118.02) * mm, "end": v(42.54, 118.33) * mm});
            skLineSegment(sketch, "E803", {"start": v(42.54, 118.33) * mm, "end": v(42.49, 118.65) * mm});
            skLineSegment(sketch, "E804", {"start": v(42.49, 118.65) * mm, "end": v(42.44, 118.98) * mm});
            skLineSegment(sketch, "E805", {"start": v(42.44, 118.98) * mm, "end": v(42.39, 119.3) * mm});
            skLineSegment(sketch, "E806", {"start": v(42.39, 119.3) * mm, "end": v(42.33, 119.63) * mm});
            skLineSegment(sketch, "E807", {"start": v(42.33, 119.63) * mm, "end": v(42.27, 119.96) * mm});
            skLineSegment(sketch, "E808", {"start": v(42.27, 119.96) * mm, "end": v(42.21, 120.3) * mm});
            skLineSegment(sketch, "E809", {"start": v(42.21, 120.3) * mm, "end": v(42.15, 120.64) * mm});
            skLineSegment(sketch, "E810", {"start": v(42.15, 120.64) * mm, "end": v(42.09, 120.98) * mm});
            skLineSegment(sketch, "E811", {"start": v(42.09, 120.98) * mm, "end": v(41.92, 121.05) * mm});
            skLineSegment(sketch, "E812", {"start": v(41.92, 121.05) * mm, "end": v(40.56, 121.52) * mm});
            skLineSegment(sketch, "E813", {"start": v(40.56, 121.52) * mm, "end": v(40.38, 121.56) * mm});
            skLineSegment(sketch, "E814", {"start": v(40.38, 121.56) * mm, "end": v(40.12, 121.33) * mm});
            skLineSegment(sketch, "E815", {"start": v(40.12, 121.33) * mm, "end": v(39.87, 121.1) * mm});
            skLineSegment(sketch, "E816", {"start": v(39.87, 121.1) * mm, "end": v(39.61, 120.88) * mm});
            skLineSegment(sketch, "E817", {"start": v(39.61, 120.88) * mm, "end": v(39.36, 120.65) * mm});
            skLineSegment(sketch, "E818", {"start": v(39.36, 120.65) * mm, "end": v(39.12, 120.42) * mm});
            skLineSegment(sketch, "E819", {"start": v(39.12, 120.42) * mm, "end": v(38.88, 120.2) * mm});
            skLineSegment(sketch, "E820", {"start": v(38.88, 120.2) * mm, "end": v(38.64, 119.97) * mm});
            skLineSegment(sketch, "E821", {"start": v(38.64, 119.97) * mm, "end": v(38.4, 119.75) * mm});
            skLineSegment(sketch, "E822", {"start": v(38.4, 119.75) * mm, "end": v(38.17, 119.53) * mm});
            skLineSegment(sketch, "E823", {"start": v(38.17, 119.53) * mm, "end": v(37.94, 119.3) * mm});
            skLineSegment(sketch, "E824", {"start": v(37.94, 119.3) * mm, "end": v(37.72, 119.09) * mm});
            skLineSegment(sketch, "E825", {"start": v(37.72, 119.09) * mm, "end": v(37.5, 118.87) * mm});
            skLineSegment(sketch, "E826", {"start": v(37.5, 118.87) * mm, "end": v(37.28, 118.65) * mm});
            skLineSegment(sketch, "E827", {"start": v(37.28, 118.65) * mm, "end": v(37.07, 118.43) * mm});
            skLineSegment(sketch, "E828", {"start": v(37.07, 118.43) * mm, "end": v(36.86, 118.21) * mm});
            skLineSegment(sketch, "E829", {"start": v(36.86, 118.21) * mm, "end": v(36.65, 118) * mm});
            skLineSegment(sketch, "E830", {"start": v(36.65, 118) * mm, "end": v(36.45, 117.79) * mm});
            skLineSegment(sketch, "E831", {"start": v(36.45, 117.79) * mm, "end": v(36.25, 117.57) * mm});
            skLineSegment(sketch, "E832", {"start": v(36.25, 117.57) * mm, "end": v(36.05, 117.36) * mm});
            skLineSegment(sketch, "E833", {"start": v(36.05, 117.36) * mm, "end": v(35.86, 117.15) * mm});
            skLineSegment(sketch, "E834", {"start": v(35.86, 117.15) * mm, "end": v(35.67, 116.94) * mm});
            skLineSegment(sketch, "E835", {"start": v(35.67, 116.94) * mm, "end": v(35.48, 116.74) * mm});
            skLineSegment(sketch, "E836", {"start": v(35.48, 116.74) * mm, "end": v(35.3, 116.53) * mm});
            skLineSegment(sketch, "E837", {"start": v(35.3, 116.53) * mm, "end": v(35.12, 116.33) * mm});
            skLineSegment(sketch, "E838", {"start": v(35.12, 116.33) * mm, "end": v(34.94, 116.13) * mm});
            skLineSegment(sketch, "E839", {"start": v(34.94, 116.13) * mm, "end": v(34.77, 115.92) * mm});
            skLineSegment(sketch, "E840", {"start": v(34.77, 115.92) * mm, "end": v(34.6, 115.72) * mm});
            skLineSegment(sketch, "E841", {"start": v(34.6, 115.72) * mm, "end": v(34.43, 115.53) * mm});
            skLineSegment(sketch, "E842", {"start": v(34.43, 115.53) * mm, "end": v(34.27, 115.33) * mm});
            skLineSegment(sketch, "E843", {"start": v(34.27, 115.33) * mm, "end": v(34.1, 115.14) * mm});
            skLineSegment(sketch, "E844", {"start": v(34.1, 115.14) * mm, "end": v(33, 115.21) * mm});
            skLineSegment(sketch, "E845", {"start": v(33, 115.21) * mm, "end": v(32.01, 115.74) * mm});
            skLineSegment(sketch, "E846", {"start": v(32.01, 115.74) * mm, "end": v(31.98, 116) * mm});
            skLineSegment(sketch, "E847", {"start": v(31.98, 116) * mm, "end": v(31.95, 116.24) * mm});
            skLineSegment(sketch, "E848", {"start": v(31.95, 116.24) * mm, "end": v(31.91, 116.5) * mm});
            skLineSegment(sketch, "E849", {"start": v(31.91, 116.5) * mm, "end": v(31.87, 116.76) * mm});
            skLineSegment(sketch, "E850", {"start": v(31.87, 116.76) * mm, "end": v(31.83, 117.02) * mm});
            skLineSegment(sketch, "E851", {"start": v(31.83, 117.02) * mm, "end": v(31.8, 117.29) * mm});
            skLineSegment(sketch, "E852", {"start": v(31.8, 117.29) * mm, "end": v(31.75, 117.56) * mm});
            skLineSegment(sketch, "E853", {"start": v(31.75, 117.56) * mm, "end": v(31.7, 117.83) * mm});
            skLineSegment(sketch, "E854", {"start": v(31.7, 117.83) * mm, "end": v(31.66, 118.1) * mm});
            skLineSegment(sketch, "E855", {"start": v(31.66, 118.1) * mm, "end": v(31.6, 118.38) * mm});
            skLineSegment(sketch, "E856", {"start": v(31.6, 118.38) * mm, "end": v(31.56, 118.66) * mm});
            skLineSegment(sketch, "E857", {"start": v(31.56, 118.66) * mm, "end": v(31.5, 118.95) * mm});
            skLineSegment(sketch, "E858", {"start": v(31.5, 118.95) * mm, "end": v(31.45, 119.23) * mm});
            skLineSegment(sketch, "E859", {"start": v(31.45, 119.23) * mm, "end": v(31.39, 119.52) * mm});
            skLineSegment(sketch, "E860", {"start": v(31.39, 119.52) * mm, "end": v(31.33, 119.81) * mm});
            skLineSegment(sketch, "E861", {"start": v(31.33, 119.81) * mm, "end": v(31.27, 120.1) * mm});
            skLineSegment(sketch, "E862", {"start": v(31.27, 120.1) * mm, "end": v(31.2, 120.4) * mm});
            skLineSegment(sketch, "E863", {"start": v(31.2, 120.4) * mm, "end": v(31.13, 120.7) * mm});
            skLineSegment(sketch, "E864", {"start": v(31.13, 120.7) * mm, "end": v(31.06, 121) * mm});
            skLineSegment(sketch, "E865", {"start": v(31.06, 121) * mm, "end": v(31, 121.32) * mm});
            skLineSegment(sketch, "E866", {"start": v(31, 121.32) * mm, "end": v(30.92, 121.62) * mm});
            skLineSegment(sketch, "E867", {"start": v(30.92, 121.62) * mm, "end": v(30.84, 121.94) * mm});
            skLineSegment(sketch, "E868", {"start": v(30.84, 121.94) * mm, "end": v(30.76, 122.25) * mm});
            skLineSegment(sketch, "E869", {"start": v(30.76, 122.25) * mm, "end": v(30.68, 122.57) * mm});
            skLineSegment(sketch, "E870", {"start": v(30.68, 122.57) * mm, "end": v(30.6, 122.89) * mm});
            skLineSegment(sketch, "E871", {"start": v(30.6, 122.89) * mm, "end": v(30.51, 123.21) * mm});
            skLineSegment(sketch, "E872", {"start": v(30.51, 123.21) * mm, "end": v(30.42, 123.54) * mm});
            skLineSegment(sketch, "E873", {"start": v(30.42, 123.54) * mm, "end": v(30.33, 123.86) * mm});
            skLineSegment(sketch, "E874", {"start": v(30.33, 123.86) * mm, "end": v(30.23, 124.2) * mm});
            skLineSegment(sketch, "E875", {"start": v(30.23, 124.2) * mm, "end": v(30.13, 124.53) * mm});
            skLineSegment(sketch, "E876", {"start": v(30.13, 124.53) * mm, "end": v(29.97, 124.58) * mm});
            skLineSegment(sketch, "E877", {"start": v(29.97, 124.58) * mm, "end": v(28.56, 124.91) * mm});
            skLineSegment(sketch, "E878", {"start": v(28.56, 124.91) * mm, "end": v(28.38, 124.94) * mm});
            skLineSegment(sketch, "E879", {"start": v(28.38, 124.94) * mm, "end": v(28.15, 124.69) * mm});
            skLineSegment(sketch, "E880", {"start": v(28.15, 124.69) * mm, "end": v(27.91, 124.44) * mm});
            skLineSegment(sketch, "E881", {"start": v(27.91, 124.44) * mm, "end": v(27.68, 124.18) * mm});
            skLineSegment(sketch, "E882", {"start": v(27.68, 124.18) * mm, "end": v(27.46, 123.93) * mm});
            skLineSegment(sketch, "E883", {"start": v(27.46, 123.93) * mm, "end": v(27.24, 123.68) * mm});
            skLineSegment(sketch, "E884", {"start": v(27.24, 123.68) * mm, "end": v(27.02, 123.44) * mm});
            skLineSegment(sketch, "E885", {"start": v(27.02, 123.44) * mm, "end": v(26.8, 123.19) * mm});
            skLineSegment(sketch, "E886", {"start": v(26.8, 123.19) * mm, "end": v(26.59, 122.94) * mm});
            skLineSegment(sketch, "E887", {"start": v(26.59, 122.94) * mm, "end": v(26.38, 122.7) * mm});
            skLineSegment(sketch, "E888", {"start": v(26.38, 122.7) * mm, "end": v(26.18, 122.46) * mm});
            skLineSegment(sketch, "E889", {"start": v(26.18, 122.46) * mm, "end": v(25.97, 122.21) * mm});
            skLineSegment(sketch, "E890", {"start": v(25.97, 122.21) * mm, "end": v(25.78, 121.97) * mm});
            skLineSegment(sketch, "E891", {"start": v(25.78, 121.97) * mm, "end": v(25.58, 121.74) * mm});
            skLineSegment(sketch, "E892", {"start": v(25.58, 121.74) * mm, "end": v(25.4, 121.5) * mm});
            skLineSegment(sketch, "E893", {"start": v(25.4, 121.5) * mm, "end": v(25.2, 121.26) * mm});
            skLineSegment(sketch, "E894", {"start": v(25.2, 121.26) * mm, "end": v(25.02, 121.03) * mm});
            skLineSegment(sketch, "E895", {"start": v(25.02, 121.03) * mm, "end": v(24.84, 120.8) * mm});
            skLineSegment(sketch, "E896", {"start": v(24.84, 120.8) * mm, "end": v(24.66, 120.57) * mm});
            skLineSegment(sketch, "E897", {"start": v(24.66, 120.57) * mm, "end": v(24.48, 120.34) * mm});
            skLineSegment(sketch, "E898", {"start": v(24.48, 120.34) * mm, "end": v(24.31, 120.1) * mm});
            skLineSegment(sketch, "E899", {"start": v(24.31, 120.1) * mm, "end": v(24.14, 119.88) * mm});
            skLineSegment(sketch, "E900", {"start": v(24.14, 119.88) * mm, "end": v(23.98, 119.66) * mm});
            skLineSegment(sketch, "E901", {"start": v(23.98, 119.66) * mm, "end": v(23.81, 119.44) * mm});
            skLineSegment(sketch, "E902", {"start": v(23.81, 119.44) * mm, "end": v(23.66, 119.22) * mm});
            skLineSegment(sketch, "E903", {"start": v(23.66, 119.22) * mm, "end": v(23.5, 119) * mm});
            skLineSegment(sketch, "E904", {"start": v(23.5, 119) * mm, "end": v(23.35, 118.78) * mm});
            skLineSegment(sketch, "E905", {"start": v(23.35, 118.78) * mm, "end": v(23.2, 118.57) * mm});
            skLineSegment(sketch, "E906", {"start": v(23.2, 118.57) * mm, "end": v(23.05, 118.35) * mm});
            skLineSegment(sketch, "E907", {"start": v(23.05, 118.35) * mm, "end": v(22.9, 118.14) * mm});
            skLineSegment(sketch, "E908", {"start": v(22.9, 118.14) * mm, "end": v(22.77, 117.93) * mm});
            skLineSegment(sketch, "E909", {"start": v(22.77, 117.93) * mm, "end": v(21.65, 117.9) * mm});
            skLineSegment(sketch, "E910", {"start": v(21.65, 117.9) * mm, "end": v(20.62, 118.33) * mm});
            skLineSegment(sketch, "E911", {"start": v(20.62, 118.33) * mm, "end": v(20.57, 118.57) * mm});
            skLineSegment(sketch, "E912", {"start": v(20.57, 118.57) * mm, "end": v(20.5, 118.82) * mm});
            skLineSegment(sketch, "E913", {"start": v(20.5, 118.82) * mm, "end": v(20.45, 119.07) * mm});
            skLineSegment(sketch, "E914", {"start": v(20.45, 119.07) * mm, "end": v(20.38, 119.33) * mm});
            skLineSegment(sketch, "E915", {"start": v(20.38, 119.33) * mm, "end": v(20.32, 119.59) * mm});
            skLineSegment(sketch, "E916", {"start": v(20.32, 119.59) * mm, "end": v(20.25, 119.85) * mm});
            skLineSegment(sketch, "E917", {"start": v(20.25, 119.85) * mm, "end": v(20.18, 120.1) * mm});
            skLineSegment(sketch, "E918", {"start": v(20.18, 120.1) * mm, "end": v(20.11, 120.38) * mm});
            skLineSegment(sketch, "E919", {"start": v(20.11, 120.38) * mm, "end": v(20.04, 120.65) * mm});
            skLineSegment(sketch, "E920", {"start": v(20.04, 120.65) * mm, "end": v(19.96, 120.92) * mm});
            skLineSegment(sketch, "E921", {"start": v(19.96, 120.92) * mm, "end": v(19.88, 121.19) * mm});
            skLineSegment(sketch, "E922", {"start": v(19.88, 121.19) * mm, "end": v(19.8, 121.47) * mm});
            skLineSegment(sketch, "E923", {"start": v(19.8, 121.47) * mm, "end": v(19.72, 121.75) * mm});
            skLineSegment(sketch, "E924", {"start": v(19.72, 121.75) * mm, "end": v(19.63, 122.03) * mm});
            skLineSegment(sketch, "E925", {"start": v(19.63, 122.03) * mm, "end": v(19.54, 122.31) * mm});
            skLineSegment(sketch, "E926", {"start": v(19.54, 122.31) * mm, "end": v(19.45, 122.6) * mm});
            skLineSegment(sketch, "E927", {"start": v(19.45, 122.6) * mm, "end": v(19.36, 122.89) * mm});
            skLineSegment(sketch, "E928", {"start": v(19.36, 122.89) * mm, "end": v(19.26, 123.18) * mm});
            skLineSegment(sketch, "E929", {"start": v(19.26, 123.18) * mm, "end": v(19.16, 123.48) * mm});
            skLineSegment(sketch, "E930", {"start": v(19.16, 123.48) * mm, "end": v(19.06, 123.78) * mm});
            skLineSegment(sketch, "E931", {"start": v(19.06, 123.78) * mm, "end": v(18.96, 124.07) * mm});
            skLineSegment(sketch, "E932", {"start": v(18.96, 124.07) * mm, "end": v(18.85, 124.38) * mm});
            skLineSegment(sketch, "E933", {"start": v(18.85, 124.38) * mm, "end": v(18.74, 124.68) * mm});
            skLineSegment(sketch, "E934", {"start": v(18.74, 124.68) * mm, "end": v(18.63, 125) * mm});
            skLineSegment(sketch, "E935", {"start": v(18.63, 125) * mm, "end": v(18.51, 125.3) * mm});
            skLineSegment(sketch, "E936", {"start": v(18.51, 125.3) * mm, "end": v(18.4, 125.61) * mm});
            skLineSegment(sketch, "E937", {"start": v(18.4, 125.61) * mm, "end": v(18.27, 125.93) * mm});
            skLineSegment(sketch, "E938", {"start": v(18.27, 125.93) * mm, "end": v(18.15, 126.24) * mm});
            skLineSegment(sketch, "E939", {"start": v(18.15, 126.24) * mm, "end": v(18.02, 126.57) * mm});
            skLineSegment(sketch, "E940", {"start": v(18.02, 126.57) * mm, "end": v(17.9, 126.89) * mm});
            skLineSegment(sketch, "E941", {"start": v(17.9, 126.89) * mm, "end": v(17.72, 126.92) * mm});
            skLineSegment(sketch, "E942", {"start": v(17.72, 126.92) * mm, "end": v(16.28, 127.12) * mm});
            skLineSegment(sketch, "E943", {"start": v(16.28, 127.12) * mm, "end": v(16.1, 127.13) * mm});
            skLineSegment(sketch, "E944", {"start": v(16.1, 127.13) * mm, "end": v(15.9, 126.85) * mm});
            skLineSegment(sketch, "E945", {"start": v(15.9, 126.85) * mm, "end": v(15.69, 126.58) * mm});
            skLineSegment(sketch, "E946", {"start": v(15.69, 126.58) * mm, "end": v(15.49, 126.3) * mm});
            skLineSegment(sketch, "E947", {"start": v(15.49, 126.3) * mm, "end": v(15.29, 126.03) * mm});
            skLineSegment(sketch, "E948", {"start": v(15.29, 126.03) * mm, "end": v(15.09, 125.76) * mm});
            skLineSegment(sketch, "E949", {"start": v(15.09, 125.76) * mm, "end": v(14.9, 125.5) * mm});
            skLineSegment(sketch, "E950", {"start": v(14.9, 125.5) * mm, "end": v(14.7, 125.23) * mm});
            skLineSegment(sketch, "E951", {"start": v(14.7, 125.23) * mm, "end": v(14.52, 124.96) * mm});
            skLineSegment(sketch, "E952", {"start": v(14.52, 124.96) * mm, "end": v(14.34, 124.7) * mm});
            skLineSegment(sketch, "E953", {"start": v(14.34, 124.7) * mm, "end": v(14.16, 124.44) * mm});
            skLineSegment(sketch, "E954", {"start": v(14.16, 124.44) * mm, "end": v(13.98, 124.18) * mm});
            skLineSegment(sketch, "E955", {"start": v(13.98, 124.18) * mm, "end": v(13.8, 123.92) * mm});
            skLineSegment(sketch, "E956", {"start": v(13.8, 123.92) * mm, "end": v(13.63, 123.66) * mm});
            skLineSegment(sketch, "E957", {"start": v(13.63, 123.66) * mm, "end": v(13.47, 123.4) * mm});
            skLineSegment(sketch, "E958", {"start": v(13.47, 123.4) * mm, "end": v(13.3, 123.15) * mm});
            skLineSegment(sketch, "E959", {"start": v(13.3, 123.15) * mm, "end": v(13.14, 122.9) * mm});
            skLineSegment(sketch, "E960", {"start": v(13.14, 122.9) * mm, "end": v(12.98, 122.65) * mm});
            skLineSegment(sketch, "E961", {"start": v(12.98, 122.65) * mm, "end": v(12.83, 122.4) * mm});
            skLineSegment(sketch, "E962", {"start": v(12.83, 122.4) * mm, "end": v(12.68, 122.16) * mm});
            skLineSegment(sketch, "E963", {"start": v(12.68, 122.16) * mm, "end": v(12.53, 121.92) * mm});
            skLineSegment(sketch, "E964", {"start": v(12.53, 121.92) * mm, "end": v(12.38, 121.68) * mm});
            skLineSegment(sketch, "E965", {"start": v(12.38, 121.68) * mm, "end": v(12.24, 121.44) * mm});
            skLineSegment(sketch, "E966", {"start": v(12.24, 121.44) * mm, "end": v(12.1, 121.2) * mm});
            skLineSegment(sketch, "E967", {"start": v(12.1, 121.2) * mm, "end": v(11.97, 120.97) * mm});
            skLineSegment(sketch, "E968", {"start": v(11.97, 120.97) * mm, "end": v(11.83, 120.73) * mm});
            skLineSegment(sketch, "E969", {"start": v(11.83, 120.73) * mm, "end": v(11.7, 120.5) * mm});
            skLineSegment(sketch, "E970", {"start": v(11.7, 120.5) * mm, "end": v(11.57, 120.27) * mm});
            skLineSegment(sketch, "E971", {"start": v(11.57, 120.27) * mm, "end": v(11.45, 120.05) * mm});
            skLineSegment(sketch, "E972", {"start": v(11.45, 120.05) * mm, "end": v(11.32, 119.82) * mm});
            skLineSegment(sketch, "E973", {"start": v(11.32, 119.82) * mm, "end": v(11.2, 119.6) * mm});
            skLineSegment(sketch, "E974", {"start": v(11.2, 119.6) * mm, "end": v(10.1, 119.46) * mm});
            skLineSegment(sketch, "E975", {"start": v(10.1, 119.46) * mm, "end": v(9.03, 119.78) * mm});
            skLineSegment(sketch, "E976", {"start": v(9.03, 119.78) * mm, "end": v(8.95, 120.02) * mm});
            skLineSegment(sketch, "E977", {"start": v(8.95, 120.02) * mm, "end": v(8.87, 120.27) * mm});
            skLineSegment(sketch, "E978", {"start": v(8.87, 120.27) * mm, "end": v(8.79, 120.5) * mm});
            skLineSegment(sketch, "E979", {"start": v(8.79, 120.5) * mm, "end": v(8.7, 120.76) * mm});
            skLineSegment(sketch, "E980", {"start": v(8.7, 120.76) * mm, "end": v(8.6, 121) * mm});
            skLineSegment(sketch, "E981", {"start": v(8.6, 121) * mm, "end": v(8.52, 121.26) * mm});
            skLineSegment(sketch, "E982", {"start": v(8.52, 121.26) * mm, "end": v(8.42, 121.51) * mm});
            skLineSegment(sketch, "E983", {"start": v(8.42, 121.51) * mm, "end": v(8.32, 121.77) * mm});
            skLineSegment(sketch, "E984", {"start": v(8.32, 121.77) * mm, "end": v(8.22, 122.03) * mm});
            skLineSegment(sketch, "E985", {"start": v(8.22, 122.03) * mm, "end": v(8.12, 122.3) * mm});
            skLineSegment(sketch, "E986", {"start": v(8.12, 122.3) * mm, "end": v(8.02, 122.56) * mm});
            skLineSegment(sketch, "E987", {"start": v(8.02, 122.56) * mm, "end": v(7.9, 122.83) * mm});
            skLineSegment(sketch, "E988", {"start": v(7.9, 122.83) * mm, "end": v(7.8, 123.1) * mm});
            skLineSegment(sketch, "E989", {"start": v(7.8, 123.1) * mm, "end": v(7.69, 123.37) * mm});
            skLineSegment(sketch, "E990", {"start": v(7.69, 123.37) * mm, "end": v(7.57, 123.64) * mm});
            skLineSegment(sketch, "E991", {"start": v(7.57, 123.64) * mm, "end": v(7.45, 123.92) * mm});
            skLineSegment(sketch, "E992", {"start": v(7.45, 123.92) * mm, "end": v(7.33, 124.2) * mm});
            skLineSegment(sketch, "E993", {"start": v(7.33, 124.2) * mm, "end": v(7.2, 124.48) * mm});
            skLineSegment(sketch, "E994", {"start": v(7.2, 124.48) * mm, "end": v(7.08, 124.77) * mm});
            skLineSegment(sketch, "E995", {"start": v(7.08, 124.77) * mm, "end": v(6.95, 125.05) * mm});
            skLineSegment(sketch, "E996", {"start": v(6.95, 125.05) * mm, "end": v(6.81, 125.34) * mm});
            skLineSegment(sketch, "E997", {"start": v(6.81, 125.34) * mm, "end": v(6.68, 125.63) * mm});
            skLineSegment(sketch, "E998", {"start": v(6.68, 125.63) * mm, "end": v(6.54, 125.93) * mm});
            skLineSegment(sketch, "E999", {"start": v(6.54, 125.93) * mm, "end": v(6.4, 126.22) * mm});
            skLineSegment(sketch, "E1000", {"start": v(6.4, 126.22) * mm, "end": v(6.25, 126.52) * mm});
            skLineSegment(sketch, "E1001", {"start": v(6.25, 126.52) * mm, "end": v(6.1, 126.82) * mm});
            skLineSegment(sketch, "E1002", {"start": v(6.1, 126.82) * mm, "end": v(5.95, 127.12) * mm});
            skLineSegment(sketch, "E1003", {"start": v(5.95, 127.12) * mm, "end": v(5.8, 127.42) * mm});
            skLineSegment(sketch, "E1004", {"start": v(5.8, 127.42) * mm, "end": v(5.64, 127.73) * mm});
            skLineSegment(sketch, "E1005", {"start": v(5.64, 127.73) * mm, "end": v(5.48, 128.03) * mm});
            skLineSegment(sketch, "E1006", {"start": v(5.48, 128.03) * mm, "end": v(5.3, 128.05) * mm});
            skLineSegment(sketch, "E1007", {"start": v(5.3, 128.05) * mm, "end": v(3.85, 128.1) * mm});
            skLineSegment(sketch, "E1008", {"start": v(3.85, 128.1) * mm, "end": v(3.68, 128.1) * mm});
            skLineSegment(sketch, "E1009", {"start": v(3.68, 128.1) * mm, "end": v(3.5, 127.8) * mm});
            skLineSegment(sketch, "E1010", {"start": v(3.5, 127.8) * mm, "end": v(3.32, 127.51) * mm});
            skLineSegment(sketch, "E1011", {"start": v(3.32, 127.51) * mm, "end": v(3.14, 127.22) * mm});
            skLineSegment(sketch, "E1012", {"start": v(3.14, 127.22) * mm, "end": v(2.97, 126.93) * mm});
            skLineSegment(sketch, "E1013", {"start": v(2.97, 126.93) * mm, "end": v(2.8, 126.64) * mm});
            skLineSegment(sketch, "E1014", {"start": v(2.8, 126.64) * mm, "end": v(2.63, 126.36) * mm});
            skLineSegment(sketch, "E1015", {"start": v(2.63, 126.36) * mm, "end": v(2.47, 126.07) * mm});
            skLineSegment(sketch, "E1016", {"start": v(2.47, 126.07) * mm, "end": v(2.3, 125.79) * mm});
            skLineSegment(sketch, "E1017", {"start": v(2.3, 125.79) * mm, "end": v(2.15, 125.5) * mm});
            skLineSegment(sketch, "E1018", {"start": v(2.15, 125.5) * mm, "end": v(2, 125.23) * mm});
            skLineSegment(sketch, "E1019", {"start": v(2, 125.23) * mm, "end": v(1.85, 124.96) * mm});
            skLineSegment(sketch, "E1020", {"start": v(1.85, 124.96) * mm, "end": v(1.7, 124.68) * mm});
            skLineSegment(sketch, "E1021", {"start": v(1.7, 124.68) * mm, "end": v(1.56, 124.4) * mm});
            skLineSegment(sketch, "E1022", {"start": v(1.56, 124.4) * mm, "end": v(1.41, 124.14) * mm});
            skLineSegment(sketch, "E1023", {"start": v(1.41, 124.14) * mm, "end": v(1.28, 123.87) * mm});
            skLineSegment(sketch, "E1024", {"start": v(1.28, 123.87) * mm, "end": v(1.14, 123.6) * mm});
            skLineSegment(sketch, "E1025", {"start": v(1.14, 123.6) * mm, "end": v(1, 123.34) * mm});
            skLineSegment(sketch, "E1026", {"start": v(1, 123.34) * mm, "end": v(0.88, 123.08) * mm});
            skLineSegment(sketch, "E1027", {"start": v(0.88, 123.08) * mm, "end": v(0.75, 122.82) * mm});
            skLineSegment(sketch, "E1028", {"start": v(0.75, 122.82) * mm, "end": v(0.63, 122.56) * mm});
            skLineSegment(sketch, "E1029", {"start": v(0.63, 122.56) * mm, "end": v(0.5, 122.31) * mm});
            skLineSegment(sketch, "E1030", {"start": v(0.5, 122.31) * mm, "end": v(0.39, 122.06) * mm});
            skLineSegment(sketch, "E1031", {"start": v(0.39, 122.06) * mm, "end": v(0.27, 121.8) * mm});
            skLineSegment(sketch, "E1032", {"start": v(0.27, 121.8) * mm, "end": v(0.16, 121.56) * mm});
            skLineSegment(sketch, "E1033", {"start": v(0.16, 121.56) * mm, "end": v(0.05, 121.32) * mm});
            skLineSegment(sketch, "E1034", {"start": v(0.05, 121.32) * mm, "end": v(-0.06, 121.07) * mm});
            skLineSegment(sketch, "E1035", {"start": v(-0.06, 121.07) * mm, "end": v(-0.16, 120.83) * mm});
            skLineSegment(sketch, "E1036", {"start": v(-0.16, 120.83) * mm, "end": v(-0.27, 120.6) * mm});
            skLineSegment(sketch, "E1037", {"start": v(-0.27, 120.6) * mm, "end": v(-0.37, 120.36) * mm});
            skLineSegment(sketch, "E1038", {"start": v(-0.37, 120.36) * mm, "end": v(-0.46, 120.13) * mm});
            skLineSegment(sketch, "E1039", {"start": v(-0.46, 120.13) * mm, "end": v(-1.55, 119.88) * mm});
            skLineSegment(sketch, "E1040", {"start": v(-1.55, 119.88) * mm, "end": v(-2.64, 120.1) * mm});
            skLineSegment(sketch, "E1041", {"start": v(-2.64, 120.1) * mm, "end": v(-2.75, 120.33) * mm});
            skLineSegment(sketch, "E1042", {"start": v(-2.75, 120.33) * mm, "end": v(-2.85, 120.56) * mm});
            skLineSegment(sketch, "E1043", {"start": v(-2.85, 120.56) * mm, "end": v(-2.96, 120.8) * mm});
            skLineSegment(sketch, "E1044", {"start": v(-2.96, 120.8) * mm, "end": v(-3.07, 121.03) * mm});
            skLineSegment(sketch, "E1045", {"start": v(-3.07, 121.03) * mm, "end": v(-3.18, 121.27) * mm});
            skLineSegment(sketch, "E1046", {"start": v(-3.18, 121.27) * mm, "end": v(-3.3, 121.52) * mm});
            skLineSegment(sketch, "E1047", {"start": v(-3.3, 121.52) * mm, "end": v(-3.42, 121.76) * mm});
            skLineSegment(sketch, "E1048", {"start": v(-3.42, 121.76) * mm, "end": v(-3.54, 122) * mm});
            skLineSegment(sketch, "E1049", {"start": v(-3.54, 122) * mm, "end": v(-3.67, 122.26) * mm});
            skLineSegment(sketch, "E1050", {"start": v(-3.67, 122.26) * mm, "end": v(-3.8, 122.5) * mm});
            skLineSegment(sketch, "E1051", {"start": v(-3.8, 122.5) * mm, "end": v(-3.93, 122.76) * mm});
            skLineSegment(sketch, "E1052", {"start": v(-3.93, 122.76) * mm, "end": v(-4.06, 123.02) * mm});
            skLineSegment(sketch, "E1053", {"start": v(-4.06, 123.02) * mm, "end": v(-4.2, 123.27) * mm});
            skLineSegment(sketch, "E1054", {"start": v(-4.2, 123.27) * mm, "end": v(-4.34, 123.53) * mm});
            skLineSegment(sketch, "E1055", {"start": v(-4.34, 123.53) * mm, "end": v(-4.48, 123.8) * mm});
            skLineSegment(sketch, "E1056", {"start": v(-4.48, 123.8) * mm, "end": v(-4.62, 124.06) * mm});
            skLineSegment(sketch, "E1057", {"start": v(-4.62, 124.06) * mm, "end": v(-4.77, 124.33) * mm});
            skLineSegment(sketch, "E1058", {"start": v(-4.77, 124.33) * mm, "end": v(-4.92, 124.6) * mm});
            skLineSegment(sketch, "E1059", {"start": v(-4.92, 124.6) * mm, "end": v(-5.08, 124.87) * mm});
            skLineSegment(sketch, "E1060", {"start": v(-5.08, 124.87) * mm, "end": v(-5.24, 125.14) * mm});
            skLineSegment(sketch, "E1061", {"start": v(-5.24, 125.14) * mm, "end": v(-5.4, 125.41) * mm});
            skLineSegment(sketch, "E1062", {"start": v(-5.4, 125.41) * mm, "end": v(-5.56, 125.69) * mm});
            skLineSegment(sketch, "E1063", {"start": v(-5.56, 125.69) * mm, "end": v(-5.73, 125.96) * mm});
            skLineSegment(sketch, "E1064", {"start": v(-5.73, 125.96) * mm, "end": v(-5.9, 126.24) * mm});
            skLineSegment(sketch, "E1065", {"start": v(-5.9, 126.24) * mm, "end": v(-6.07, 126.53) * mm});
            skLineSegment(sketch, "E1066", {"start": v(-6.07, 126.53) * mm, "end": v(-6.25, 126.8) * mm});
            skLineSegment(sketch, "E1067", {"start": v(-6.25, 126.8) * mm, "end": v(-6.43, 127.1) * mm});
            skLineSegment(sketch, "E1068", {"start": v(-6.43, 127.1) * mm, "end": v(-6.61, 127.38) * mm});
            skLineSegment(sketch, "E1069", {"start": v(-6.61, 127.38) * mm, "end": v(-6.8, 127.67) * mm});
            skLineSegment(sketch, "E1070", {"start": v(-6.8, 127.67) * mm, "end": v(-6.99, 127.96) * mm});
            skLineSegment(sketch, "E1071", {"start": v(-6.99, 127.96) * mm, "end": v(-7.17, 127.96) * mm});
            skLineSegment(sketch, "E1072", {"start": v(-7.17, 127.96) * mm, "end": v(-8.61, 127.87) * mm});
            skLineSegment(sketch, "E1073", {"start": v(-8.61, 127.87) * mm, "end": v(-8.79, 127.85) * mm});
            skLineSegment(sketch, "E1074", {"start": v(-8.79, 127.85) * mm, "end": v(-8.94, 127.54) * mm});
            skLineSegment(sketch, "E1075", {"start": v(-8.94, 127.54) * mm, "end": v(-9.09, 127.23) * mm});
            skLineSegment(sketch, "E1076", {"start": v(-9.09, 127.23) * mm, "end": v(-9.24, 126.92) * mm});
            skLineSegment(sketch, "E1077", {"start": v(-9.24, 126.92) * mm, "end": v(-9.38, 126.61) * mm});
            skLineSegment(sketch, "E1078", {"start": v(-9.38, 126.61) * mm, "end": v(-9.52, 126.31) * mm});
            skLineSegment(sketch, "E1079", {"start": v(-9.52, 126.31) * mm, "end": v(-9.66, 126) * mm});
            skLineSegment(sketch, "E1080", {"start": v(-9.66, 126) * mm, "end": v(-9.8, 125.71) * mm});
            skLineSegment(sketch, "E1081", {"start": v(-9.8, 125.71) * mm, "end": v(-9.92, 125.42) * mm});
            skLineSegment(sketch, "E1082", {"start": v(-9.92, 125.42) * mm, "end": v(-10.05, 125.12) * mm});
            skLineSegment(sketch, "E1083", {"start": v(-10.05, 125.12) * mm, "end": v(-10.18, 124.83) * mm});
            skLineSegment(sketch, "E1084", {"start": v(-10.18, 124.83) * mm, "end": v(-10.3, 124.54) * mm});
            skLineSegment(sketch, "E1085", {"start": v(-10.3, 124.54) * mm, "end": v(-10.42, 124.25) * mm});
            skLineSegment(sketch, "E1086", {"start": v(-10.42, 124.25) * mm, "end": v(-10.54, 123.97) * mm});
            skLineSegment(sketch, "E1087", {"start": v(-10.54, 123.97) * mm, "end": v(-10.65, 123.68) * mm});
            skLineSegment(sketch, "E1088", {"start": v(-10.65, 123.68) * mm, "end": v(-10.76, 123.4) * mm});
            skLineSegment(sketch, "E1089", {"start": v(-10.76, 123.4) * mm, "end": v(-10.87, 123.13) * mm});
            skLineSegment(sketch, "E1090", {"start": v(-10.87, 123.13) * mm, "end": v(-10.98, 122.85) * mm});
            skLineSegment(sketch, "E1091", {"start": v(-10.98, 122.85) * mm, "end": v(-11.08, 122.58) * mm});
            skLineSegment(sketch, "E1092", {"start": v(-11.08, 122.58) * mm, "end": v(-11.18, 122.3) * mm});
            skLineSegment(sketch, "E1093", {"start": v(-11.18, 122.3) * mm, "end": v(-11.28, 122.04) * mm});
            skLineSegment(sketch, "E1094", {"start": v(-11.28, 122.04) * mm, "end": v(-11.38, 121.78) * mm});
            skLineSegment(sketch, "E1095", {"start": v(-11.38, 121.78) * mm, "end": v(-11.47, 121.51) * mm});
            skLineSegment(sketch, "E1096", {"start": v(-11.47, 121.51) * mm, "end": v(-11.56, 121.25) * mm});
            skLineSegment(sketch, "E1097", {"start": v(-11.56, 121.25) * mm, "end": v(-11.65, 121) * mm});
            skLineSegment(sketch, "E1098", {"start": v(-11.65, 121) * mm, "end": v(-11.73, 120.74) * mm});
            skLineSegment(sketch, "E1099", {"start": v(-11.73, 120.74) * mm, "end": v(-11.82, 120.5) * mm});
            skLineSegment(sketch, "E1100", {"start": v(-11.82, 120.5) * mm, "end": v(-11.9, 120.24) * mm});
            skLineSegment(sketch, "E1101", {"start": v(-11.9, 120.24) * mm, "end": v(-11.98, 120) * mm});
            skLineSegment(sketch, "E1102", {"start": v(-11.98, 120) * mm, "end": v(-12.05, 119.75) * mm});
            skLineSegment(sketch, "E1103", {"start": v(-12.05, 119.75) * mm, "end": v(-12.13, 119.5) * mm});
            skLineSegment(sketch, "E1104", {"start": v(-12.13, 119.5) * mm, "end": v(-13.18, 119.15) * mm});
            skLineSegment(sketch, "E1105", {"start": v(-13.18, 119.15) * mm, "end": v(-14.3, 119.27) * mm});
            skLineSegment(sketch, "E1106", {"start": v(-14.3, 119.27) * mm, "end": v(-14.42, 119.48) * mm});
            skLineSegment(sketch, "E1107", {"start": v(-14.42, 119.48) * mm, "end": v(-14.55, 119.7) * mm});
            skLineSegment(sketch, "E1108", {"start": v(-14.55, 119.7) * mm, "end": v(-14.68, 119.93) * mm});
            skLineSegment(sketch, "E1109", {"start": v(-14.68, 119.93) * mm, "end": v(-14.81, 120.16) * mm});
            skLineSegment(sketch, "E1110", {"start": v(-14.81, 120.16) * mm, "end": v(-14.95, 120.38) * mm});
            skLineSegment(sketch, "E1111", {"start": v(-14.95, 120.38) * mm, "end": v(-15.09, 120.61) * mm});
            skLineSegment(sketch, "E1112", {"start": v(-15.09, 120.61) * mm, "end": v(-15.23, 120.85) * mm});
            skLineSegment(sketch, "E1113", {"start": v(-15.23, 120.85) * mm, "end": v(-15.38, 121.08) * mm});
            skLineSegment(sketch, "E1114", {"start": v(-15.38, 121.08) * mm, "end": v(-15.52, 121.31) * mm});
            skLineSegment(sketch, "E1115", {"start": v(-15.52, 121.31) * mm, "end": v(-15.68, 121.55) * mm});
            skLineSegment(sketch, "E1116", {"start": v(-15.68, 121.55) * mm, "end": v(-15.83, 121.79) * mm});
            skLineSegment(sketch, "E1117", {"start": v(-15.83, 121.79) * mm, "end": v(-16, 122.03) * mm});
            skLineSegment(sketch, "E1118", {"start": v(-16, 122.03) * mm, "end": v(-16.15, 122.27) * mm});
            skLineSegment(sketch, "E1119", {"start": v(-16.15, 122.27) * mm, "end": v(-16.31, 122.52) * mm});
            skLineSegment(sketch, "E1120", {"start": v(-16.31, 122.52) * mm, "end": v(-16.48, 122.77) * mm});
            skLineSegment(sketch, "E1121", {"start": v(-16.48, 122.77) * mm, "end": v(-16.65, 123.02) * mm});
            skLineSegment(sketch, "E1122", {"start": v(-16.65, 123.02) * mm, "end": v(-16.83, 123.27) * mm});
            skLineSegment(sketch, "E1123", {"start": v(-16.83, 123.27) * mm, "end": v(-17, 123.52) * mm});
            skLineSegment(sketch, "E1124", {"start": v(-17, 123.52) * mm, "end": v(-17.18, 123.77) * mm});
            skLineSegment(sketch, "E1125", {"start": v(-17.18, 123.77) * mm, "end": v(-17.37, 124.03) * mm});
            skLineSegment(sketch, "E1126", {"start": v(-17.37, 124.03) * mm, "end": v(-17.56, 124.28) * mm});
            skLineSegment(sketch, "E1127", {"start": v(-17.56, 124.28) * mm, "end": v(-17.75, 124.54) * mm});
            skLineSegment(sketch, "E1128", {"start": v(-17.75, 124.54) * mm, "end": v(-17.94, 124.8) * mm});
            skLineSegment(sketch, "E1129", {"start": v(-17.94, 124.8) * mm, "end": v(-18.14, 125.06) * mm});
            skLineSegment(sketch, "E1130", {"start": v(-18.14, 125.06) * mm, "end": v(-18.34, 125.33) * mm});
            skLineSegment(sketch, "E1131", {"start": v(-18.34, 125.33) * mm, "end": v(-18.54, 125.59) * mm});
            skLineSegment(sketch, "E1132", {"start": v(-18.54, 125.59) * mm, "end": v(-18.75, 125.86) * mm});
            skLineSegment(sketch, "E1133", {"start": v(-18.75, 125.86) * mm, "end": v(-18.96, 126.12) * mm});
            skLineSegment(sketch, "E1134", {"start": v(-18.96, 126.12) * mm, "end": v(-19.17, 126.4) * mm});
            skLineSegment(sketch, "E1135", {"start": v(-19.17, 126.4) * mm, "end": v(-19.39, 126.66) * mm});
            skLineSegment(sketch, "E1136", {"start": v(-19.39, 126.66) * mm, "end": v(-19.57, 126.65) * mm});
            skLineSegment(sketch, "E1137", {"start": v(-19.57, 126.65) * mm, "end": v(-21, 126.42) * mm});
            skLineSegment(sketch, "E1138", {"start": v(-21, 126.42) * mm, "end": v(-21.17, 126.38) * mm});
            skLineSegment(sketch, "E1139", {"start": v(-21.17, 126.38) * mm, "end": v(-21.29, 126.05) * mm});
            skLineSegment(sketch, "E1140", {"start": v(-21.29, 126.05) * mm, "end": v(-21.4, 125.73) * mm});
            skLineSegment(sketch, "E1141", {"start": v(-21.4, 125.73) * mm, "end": v(-21.52, 125.4) * mm});
            skLineSegment(sketch, "E1142", {"start": v(-21.52, 125.4) * mm, "end": v(-21.64, 125.1) * mm});
            skLineSegment(sketch, "E1143", {"start": v(-21.64, 125.1) * mm, "end": v(-21.75, 124.77) * mm});
            skLineSegment(sketch, "E1144", {"start": v(-21.75, 124.77) * mm, "end": v(-21.85, 124.46) * mm});
            skLineSegment(sketch, "E1145", {"start": v(-21.85, 124.46) * mm, "end": v(-21.96, 124.15) * mm});
            skLineSegment(sketch, "E1146", {"start": v(-21.96, 124.15) * mm, "end": v(-22.06, 123.84) * mm});
            skLineSegment(sketch, "E1147", {"start": v(-22.06, 123.84) * mm, "end": v(-22.16, 123.54) * mm});
            skLineSegment(sketch, "E1148", {"start": v(-22.16, 123.54) * mm, "end": v(-22.26, 123.23) * mm});
            skLineSegment(sketch, "E1149", {"start": v(-22.26, 123.23) * mm, "end": v(-22.35, 122.94) * mm});
            skLineSegment(sketch, "E1150", {"start": v(-22.35, 122.94) * mm, "end": v(-22.44, 122.64) * mm});
            skLineSegment(sketch, "E1151", {"start": v(-22.44, 122.64) * mm, "end": v(-22.53, 122.34) * mm});
            skLineSegment(sketch, "E1152", {"start": v(-22.53, 122.34) * mm, "end": v(-22.61, 122.05) * mm});
            skLineSegment(sketch, "E1153", {"start": v(-22.61, 122.05) * mm, "end": v(-22.7, 121.76) * mm});
            skLineSegment(sketch, "E1154", {"start": v(-22.7, 121.76) * mm, "end": v(-22.78, 121.47) * mm});
            skLineSegment(sketch, "E1155", {"start": v(-22.78, 121.47) * mm, "end": v(-22.86, 121.19) * mm});
            skLineSegment(sketch, "E1156", {"start": v(-22.86, 121.19) * mm, "end": v(-22.93, 120.9) * mm});
            skLineSegment(sketch, "E1157", {"start": v(-22.93, 120.9) * mm, "end": v(-23, 120.63) * mm});
            skLineSegment(sketch, "E1158", {"start": v(-23, 120.63) * mm, "end": v(-23.08, 120.35) * mm});
            skLineSegment(sketch, "E1159", {"start": v(-23.08, 120.35) * mm, "end": v(-23.15, 120.08) * mm});
            skLineSegment(sketch, "E1160", {"start": v(-23.15, 120.08) * mm, "end": v(-23.22, 119.81) * mm});
            skLineSegment(sketch, "E1161", {"start": v(-23.22, 119.81) * mm, "end": v(-23.28, 119.54) * mm});
            skLineSegment(sketch, "E1162", {"start": v(-23.28, 119.54) * mm, "end": v(-23.34, 119.28) * mm});
            skLineSegment(sketch, "E1163", {"start": v(-23.34, 119.28) * mm, "end": v(-23.4, 119.02) * mm});
            skLineSegment(sketch, "E1164", {"start": v(-23.4, 119.02) * mm, "end": v(-23.46, 118.76) * mm});
            skLineSegment(sketch, "E1165", {"start": v(-23.46, 118.76) * mm, "end": v(-23.52, 118.5) * mm});
            skLineSegment(sketch, "E1166", {"start": v(-23.52, 118.5) * mm, "end": v(-23.57, 118.25) * mm});
            skLineSegment(sketch, "E1167", {"start": v(-23.57, 118.25) * mm, "end": v(-23.62, 118) * mm});
            skLineSegment(sketch, "E1168", {"start": v(-23.62, 118) * mm, "end": v(-23.67, 117.75) * mm});
            skLineSegment(sketch, "E1169", {"start": v(-23.67, 117.75) * mm, "end": v(-24.7, 117.3) * mm});
            skLineSegment(sketch, "E1170", {"start": v(-24.7, 117.3) * mm, "end": v(-25.8, 117.3) * mm});
            skLineSegment(sketch, "E1171", {"start": v(-25.8, 117.3) * mm, "end": v(-25.95, 117.5) * mm});
            skLineSegment(sketch, "E1172", {"start": v(-25.95, 117.5) * mm, "end": v(-26.1, 117.71) * mm});
            skLineSegment(sketch, "E1173", {"start": v(-26.1, 117.71) * mm, "end": v(-26.25, 117.92) * mm});
            skLineSegment(sketch, "E1174", {"start": v(-26.25, 117.92) * mm, "end": v(-26.4, 118.13) * mm});
            skLineSegment(sketch, "E1175", {"start": v(-26.4, 118.13) * mm, "end": v(-26.57, 118.34) * mm});
            skLineSegment(sketch, "E1176", {"start": v(-26.57, 118.34) * mm, "end": v(-26.73, 118.56) * mm});
            skLineSegment(sketch, "E1177", {"start": v(-26.73, 118.56) * mm, "end": v(-26.9, 118.78) * mm});
            skLineSegment(sketch, "E1178", {"start": v(-26.9, 118.78) * mm, "end": v(-27.06, 119) * mm});
            skLineSegment(sketch, "E1179", {"start": v(-27.06, 119) * mm, "end": v(-27.23, 119.21) * mm});
            skLineSegment(sketch, "E1180", {"start": v(-27.23, 119.21) * mm, "end": v(-27.4, 119.43) * mm});
            skLineSegment(sketch, "E1181", {"start": v(-27.4, 119.43) * mm, "end": v(-27.59, 119.66) * mm});
            skLineSegment(sketch, "E1182", {"start": v(-27.59, 119.66) * mm, "end": v(-27.77, 119.88) * mm});
            skLineSegment(sketch, "E1183", {"start": v(-27.77, 119.88) * mm, "end": v(-27.95, 120.1) * mm});
            skLineSegment(sketch, "E1184", {"start": v(-27.95, 120.1) * mm, "end": v(-28.14, 120.33) * mm});
            skLineSegment(sketch, "E1185", {"start": v(-28.14, 120.33) * mm, "end": v(-28.33, 120.57) * mm});
            skLineSegment(sketch, "E1186", {"start": v(-28.33, 120.57) * mm, "end": v(-28.52, 120.8) * mm});
            skLineSegment(sketch, "E1187", {"start": v(-28.52, 120.8) * mm, "end": v(-28.72, 121.03) * mm});
            skLineSegment(sketch, "E1188", {"start": v(-28.72, 121.03) * mm, "end": v(-28.92, 121.26) * mm});
            skLineSegment(sketch, "E1189", {"start": v(-28.92, 121.26) * mm, "end": v(-29.13, 121.5) * mm});
            skLineSegment(sketch, "E1190", {"start": v(-29.13, 121.5) * mm, "end": v(-29.33, 121.73) * mm});
            skLineSegment(sketch, "E1191", {"start": v(-29.33, 121.73) * mm, "end": v(-29.54, 121.97) * mm});
            skLineSegment(sketch, "E1192", {"start": v(-29.54, 121.97) * mm, "end": v(-29.76, 122.2) * mm});
            skLineSegment(sketch, "E1193", {"start": v(-29.76, 122.2) * mm, "end": v(-29.98, 122.45) * mm});
            skLineSegment(sketch, "E1194", {"start": v(-29.98, 122.45) * mm, "end": v(-30.2, 122.69) * mm});
            skLineSegment(sketch, "E1195", {"start": v(-30.2, 122.69) * mm, "end": v(-30.42, 122.93) * mm});
            skLineSegment(sketch, "E1196", {"start": v(-30.42, 122.93) * mm, "end": v(-30.65, 123.18) * mm});
            skLineSegment(sketch, "E1197", {"start": v(-30.65, 123.18) * mm, "end": v(-30.88, 123.42) * mm});
            skLineSegment(sketch, "E1198", {"start": v(-30.88, 123.42) * mm, "end": v(-31.12, 123.66) * mm});
            skLineSegment(sketch, "E1199", {"start": v(-31.12, 123.66) * mm, "end": v(-31.36, 123.91) * mm});
            skLineSegment(sketch, "E1200", {"start": v(-31.36, 123.91) * mm, "end": v(-31.6, 124.16) * mm});
            skLineSegment(sketch, "E1201", {"start": v(-31.6, 124.16) * mm, "end": v(-31.78, 124.13) * mm});
            skLineSegment(sketch, "E1202", {"start": v(-31.78, 124.13) * mm, "end": v(-33.18, 123.76) * mm});
            skLineSegment(sketch, "E1203", {"start": v(-33.18, 123.76) * mm, "end": v(-33.34, 123.7) * mm});
            skLineSegment(sketch, "E1204", {"start": v(-33.34, 123.7) * mm, "end": v(-33.43, 123.36) * mm});
            skLineSegment(sketch, "E1205", {"start": v(-33.43, 123.36) * mm, "end": v(-33.52, 123.03) * mm});
            skLineSegment(sketch, "E1206", {"start": v(-33.52, 123.03) * mm, "end": v(-33.6, 122.7) * mm});
            skLineSegment(sketch, "E1207", {"start": v(-33.6, 122.7) * mm, "end": v(-33.68, 122.37) * mm});
            skLineSegment(sketch, "E1208", {"start": v(-33.68, 122.37) * mm, "end": v(-33.76, 122.05) * mm});
            skLineSegment(sketch, "E1209", {"start": v(-33.76, 122.05) * mm, "end": v(-33.84, 121.72) * mm});
            skLineSegment(sketch, "E1210", {"start": v(-33.84, 121.72) * mm, "end": v(-33.91, 121.4) * mm});
            skLineSegment(sketch, "E1211", {"start": v(-33.91, 121.4) * mm, "end": v(-33.98, 121.1) * mm});
            skLineSegment(sketch, "E1212", {"start": v(-33.98, 121.1) * mm, "end": v(-34.05, 120.78) * mm});
            skLineSegment(sketch, "E1213", {"start": v(-34.05, 120.78) * mm, "end": v(-34.12, 120.47) * mm});
            skLineSegment(sketch, "E1214", {"start": v(-34.12, 120.47) * mm, "end": v(-34.18, 120.16) * mm});
            skLineSegment(sketch, "E1215", {"start": v(-34.18, 120.16) * mm, "end": v(-34.24, 119.85) * mm});
            skLineSegment(sketch, "E1216", {"start": v(-34.24, 119.85) * mm, "end": v(-34.3, 119.55) * mm});
            skLineSegment(sketch, "E1217", {"start": v(-34.3, 119.55) * mm, "end": v(-34.36, 119.25) * mm});
            skLineSegment(sketch, "E1218", {"start": v(-34.36, 119.25) * mm, "end": v(-34.42, 118.96) * mm});
            skLineSegment(sketch, "E1219", {"start": v(-34.42, 118.96) * mm, "end": v(-34.47, 118.66) * mm});
            skLineSegment(sketch, "E1220", {"start": v(-34.47, 118.66) * mm, "end": v(-34.52, 118.37) * mm});
            skLineSegment(sketch, "E1221", {"start": v(-34.52, 118.37) * mm, "end": v(-34.57, 118.08) * mm});
            skLineSegment(sketch, "E1222", {"start": v(-34.57, 118.08) * mm, "end": v(-34.61, 117.8) * mm});
            skLineSegment(sketch, "E1223", {"start": v(-34.61, 117.8) * mm, "end": v(-34.66, 117.52) * mm});
            skLineSegment(sketch, "E1224", {"start": v(-34.66, 117.52) * mm, "end": v(-34.7, 117.24) * mm});
            skLineSegment(sketch, "E1225", {"start": v(-34.7, 117.24) * mm, "end": v(-34.74, 116.96) * mm});
            skLineSegment(sketch, "E1226", {"start": v(-34.74, 116.96) * mm, "end": v(-34.78, 116.7) * mm});
            skLineSegment(sketch, "E1227", {"start": v(-34.78, 116.7) * mm, "end": v(-34.81, 116.42) * mm});
            skLineSegment(sketch, "E1228", {"start": v(-34.81, 116.42) * mm, "end": v(-34.85, 116.15) * mm});
            skLineSegment(sketch, "E1229", {"start": v(-34.85, 116.15) * mm, "end": v(-34.88, 115.9) * mm});
            skLineSegment(sketch, "E1230", {"start": v(-34.88, 115.9) * mm, "end": v(-34.91, 115.63) * mm});
            skLineSegment(sketch, "E1231", {"start": v(-34.91, 115.63) * mm, "end": v(-34.94, 115.37) * mm});
            skLineSegment(sketch, "E1232", {"start": v(-34.94, 115.37) * mm, "end": v(-34.97, 115.12) * mm});
            skLineSegment(sketch, "E1233", {"start": v(-34.97, 115.12) * mm, "end": v(-35, 114.87) * mm});
            skLineSegment(sketch, "E1234", {"start": v(-35, 114.87) * mm, "end": v(-35.96, 114.31) * mm});
            skLineSegment(sketch, "E1235", {"start": v(-35.96, 114.31) * mm, "end": v(-37.07, 114.2) * mm});
            skLineSegment(sketch, "E1236", {"start": v(-37.07, 114.2) * mm, "end": v(-37.24, 114.4) * mm});
            skLineSegment(sketch, "E1237", {"start": v(-37.24, 114.4) * mm, "end": v(-37.4, 114.59) * mm});
            skLineSegment(sketch, "E1238", {"start": v(-37.4, 114.59) * mm, "end": v(-37.58, 114.78) * mm});
            skLineSegment(sketch, "E1239", {"start": v(-37.58, 114.78) * mm, "end": v(-37.75, 114.98) * mm});
            skLineSegment(sketch, "E1240", {"start": v(-37.75, 114.98) * mm, "end": v(-37.93, 115.17) * mm});
            skLineSegment(sketch, "E1241", {"start": v(-37.93, 115.17) * mm, "end": v(-38.11, 115.37) * mm});
            skLineSegment(sketch, "E1242", {"start": v(-38.11, 115.37) * mm, "end": v(-38.3, 115.57) * mm});
            skLineSegment(sketch, "E1243", {"start": v(-38.3, 115.57) * mm, "end": v(-38.49, 115.77) * mm});
            skLineSegment(sketch, "E1244", {"start": v(-38.49, 115.77) * mm, "end": v(-38.68, 115.98) * mm});
            skLineSegment(sketch, "E1245", {"start": v(-38.68, 115.98) * mm, "end": v(-38.87, 116.18) * mm});
            skLineSegment(sketch, "E1246", {"start": v(-38.87, 116.18) * mm, "end": v(-39.07, 116.38) * mm});
            skLineSegment(sketch, "E1247", {"start": v(-39.07, 116.38) * mm, "end": v(-39.27, 116.59) * mm});
            skLineSegment(sketch, "E1248", {"start": v(-39.27, 116.59) * mm, "end": v(-39.48, 116.8) * mm});
            skLineSegment(sketch, "E1249", {"start": v(-39.48, 116.8) * mm, "end": v(-39.69, 117) * mm});
            skLineSegment(sketch, "E1250", {"start": v(-39.69, 117) * mm, "end": v(-39.9, 117.21) * mm});
            skLineSegment(sketch, "E1251", {"start": v(-39.9, 117.21) * mm, "end": v(-40.12, 117.42) * mm});
            skLineSegment(sketch, "E1252", {"start": v(-40.12, 117.42) * mm, "end": v(-40.34, 117.64) * mm});
            skLineSegment(sketch, "E1253", {"start": v(-40.34, 117.64) * mm, "end": v(-40.56, 117.85) * mm});
            skLineSegment(sketch, "E1254", {"start": v(-40.56, 117.85) * mm, "end": v(-40.79, 118.06) * mm});
            skLineSegment(sketch, "E1255", {"start": v(-40.79, 118.06) * mm, "end": v(-41.01, 118.28) * mm});
            skLineSegment(sketch, "E1256", {"start": v(-41.01, 118.28) * mm, "end": v(-41.25, 118.5) * mm});
            skLineSegment(sketch, "E1257", {"start": v(-41.25, 118.5) * mm, "end": v(-41.49, 118.7) * mm});
            skLineSegment(sketch, "E1258", {"start": v(-41.49, 118.7) * mm, "end": v(-41.73, 118.92) * mm});
            skLineSegment(sketch, "E1259", {"start": v(-41.73, 118.92) * mm, "end": v(-41.97, 119.14) * mm});
            skLineSegment(sketch, "E1260", {"start": v(-41.97, 119.14) * mm, "end": v(-42.22, 119.36) * mm});
            skLineSegment(sketch, "E1261", {"start": v(-42.22, 119.36) * mm, "end": v(-42.47, 119.58) * mm});
            skLineSegment(sketch, "E1262", {"start": v(-42.47, 119.58) * mm, "end": v(-42.72, 119.8) * mm});
            skLineSegment(sketch, "E1263", {"start": v(-42.72, 119.8) * mm, "end": v(-42.98, 120.02) * mm});
            skLineSegment(sketch, "E1264", {"start": v(-42.98, 120.02) * mm, "end": v(-43.25, 120.25) * mm});
            skLineSegment(sketch, "E1265", {"start": v(-43.25, 120.25) * mm, "end": v(-43.51, 120.47) * mm});
            skLineSegment(sketch, "E1266", {"start": v(-43.51, 120.47) * mm, "end": v(-43.68, 120.42) * mm});
            skLineSegment(sketch, "E1267", {"start": v(-43.68, 120.42) * mm, "end": v(-45.04, 119.91) * mm});
            skLineSegment(sketch, "E1268", {"start": v(-45.04, 119.91) * mm, "end": v(-45.2, 119.84) * mm});
            skLineSegment(sketch, "E1269", {"start": v(-45.2, 119.84) * mm, "end": v(-45.26, 119.5) * mm});
            skLineSegment(sketch, "E1270", {"start": v(-45.26, 119.5) * mm, "end": v(-45.3, 119.16) * mm});
            skLineSegment(sketch, "E1271", {"start": v(-45.3, 119.16) * mm, "end": v(-45.36, 118.82) * mm});
            skLineSegment(sketch, "E1272", {"start": v(-45.36, 118.82) * mm, "end": v(-45.4, 118.49) * mm});
            skLineSegment(sketch, "E1273", {"start": v(-45.4, 118.49) * mm, "end": v(-45.46, 118.16) * mm});
            skLineSegment(sketch, "E1274", {"start": v(-45.46, 118.16) * mm, "end": v(-45.5, 117.83) * mm});
            skLineSegment(sketch, "E1275", {"start": v(-45.5, 117.83) * mm, "end": v(-45.54, 117.5) * mm});
            skLineSegment(sketch, "E1276", {"start": v(-45.54, 117.5) * mm, "end": v(-45.58, 117.18) * mm});
            skLineSegment(sketch, "E1277", {"start": v(-45.58, 117.18) * mm, "end": v(-45.62, 116.86) * mm});
            skLineSegment(sketch, "E1278", {"start": v(-45.62, 116.86) * mm, "end": v(-45.65, 116.55) * mm});
            skLineSegment(sketch, "E1279", {"start": v(-45.65, 116.55) * mm, "end": v(-45.69, 116.24) * mm});
            skLineSegment(sketch, "E1280", {"start": v(-45.69, 116.24) * mm, "end": v(-45.72, 115.92) * mm});
            skLineSegment(sketch, "E1281", {"start": v(-45.72, 115.92) * mm, "end": v(-45.75, 115.62) * mm});
            skLineSegment(sketch, "E1282", {"start": v(-45.75, 115.62) * mm, "end": v(-45.78, 115.31) * mm});
            skLineSegment(sketch, "E1283", {"start": v(-45.78, 115.31) * mm, "end": v(-45.8, 115.02) * mm});
            skLineSegment(sketch, "E1284", {"start": v(-45.8, 115.02) * mm, "end": v(-45.82, 114.72) * mm});
            skLineSegment(sketch, "E1285", {"start": v(-45.82, 114.72) * mm, "end": v(-45.85, 114.42) * mm});
            skLineSegment(sketch, "E1286", {"start": v(-45.85, 114.42) * mm, "end": v(-45.87, 114.13) * mm});
            skLineSegment(sketch, "E1287", {"start": v(-45.87, 114.13) * mm, "end": v(-45.88, 113.84) * mm});
            skLineSegment(sketch, "E1288", {"start": v(-45.88, 113.84) * mm, "end": v(-45.9, 113.56) * mm});
            skLineSegment(sketch, "E1289", {"start": v(-45.9, 113.56) * mm, "end": v(-45.92, 113.28) * mm});
            skLineSegment(sketch, "E1290", {"start": v(-45.92, 113.28) * mm, "end": v(-45.93, 113) * mm});
            skLineSegment(sketch, "E1291", {"start": v(-45.93, 113) * mm, "end": v(-45.94, 112.73) * mm});
            skLineSegment(sketch, "E1292", {"start": v(-45.94, 112.73) * mm, "end": v(-45.95, 112.45) * mm});
            skLineSegment(sketch, "E1293", {"start": v(-45.95, 112.45) * mm, "end": v(-45.96, 112.19) * mm});
            skLineSegment(sketch, "E1294", {"start": v(-45.96, 112.19) * mm, "end": v(-45.96, 111.92) * mm});
            skLineSegment(sketch, "E1295", {"start": v(-45.96, 111.92) * mm, "end": v(-45.97, 111.66) * mm});
            skLineSegment(sketch, "E1296", {"start": v(-45.97, 111.66) * mm, "end": v(-45.97, 111.4) * mm});
            skLineSegment(sketch, "E1297", {"start": v(-45.97, 111.4) * mm, "end": v(-45.97, 111.14) * mm});
            skLineSegment(sketch, "E1298", {"start": v(-45.97, 111.14) * mm, "end": v(-45.98, 110.89) * mm});
            skLineSegment(sketch, "E1299", {"start": v(-45.98, 110.89) * mm, "end": v(-46.88, 110.24) * mm});
            skLineSegment(sketch, "E1300", {"start": v(-46.88, 110.24) * mm, "end": v(-47.98, 110.03) * mm});
            skLineSegment(sketch, "E1301", {"start": v(-47.98, 110.03) * mm, "end": v(-48.16, 110.2) * mm});
            skLineSegment(sketch, "E1302", {"start": v(-48.16, 110.2) * mm, "end": v(-48.35, 110.38) * mm});
            skLineSegment(sketch, "E1303", {"start": v(-48.35, 110.38) * mm, "end": v(-48.54, 110.55) * mm});
            skLineSegment(sketch, "E1304", {"start": v(-48.54, 110.55) * mm, "end": v(-48.73, 110.73) * mm});
            skLineSegment(sketch, "E1305", {"start": v(-48.73, 110.73) * mm, "end": v(-48.93, 110.9) * mm});
            skLineSegment(sketch, "E1306", {"start": v(-48.93, 110.9) * mm, "end": v(-49.13, 111.09) * mm});
            skLineSegment(sketch, "E1307", {"start": v(-49.13, 111.09) * mm, "end": v(-49.33, 111.27) * mm});
            skLineSegment(sketch, "E1308", {"start": v(-49.33, 111.27) * mm, "end": v(-49.54, 111.45) * mm});
            skLineSegment(sketch, "E1309", {"start": v(-49.54, 111.45) * mm, "end": v(-49.75, 111.63) * mm});
            skLineSegment(sketch, "E1310", {"start": v(-49.75, 111.63) * mm, "end": v(-49.97, 111.81) * mm});
            skLineSegment(sketch, "E1311", {"start": v(-49.97, 111.81) * mm, "end": v(-50.18, 112) * mm});
            skLineSegment(sketch, "E1312", {"start": v(-50.18, 112) * mm, "end": v(-50.4, 112.18) * mm});
            skLineSegment(sketch, "E1313", {"start": v(-50.4, 112.18) * mm, "end": v(-50.63, 112.37) * mm});
            skLineSegment(sketch, "E1314", {"start": v(-50.63, 112.37) * mm, "end": v(-50.86, 112.56) * mm});
            skLineSegment(sketch, "E1315", {"start": v(-50.86, 112.56) * mm, "end": v(-51.09, 112.74) * mm});
            skLineSegment(sketch, "E1316", {"start": v(-51.09, 112.74) * mm, "end": v(-51.32, 112.93) * mm});
            skLineSegment(sketch, "E1317", {"start": v(-51.32, 112.93) * mm, "end": v(-51.56, 113.12) * mm});
            skLineSegment(sketch, "E1318", {"start": v(-51.56, 113.12) * mm, "end": v(-51.8, 113.31) * mm});
            skLineSegment(sketch, "E1319", {"start": v(-51.8, 113.31) * mm, "end": v(-52.05, 113.5) * mm});
            skLineSegment(sketch, "E1320", {"start": v(-52.05, 113.5) * mm, "end": v(-52.3, 113.7) * mm});
            skLineSegment(sketch, "E1321", {"start": v(-52.3, 113.7) * mm, "end": v(-52.55, 113.88) * mm});
            skLineSegment(sketch, "E1322", {"start": v(-52.55, 113.88) * mm, "end": v(-52.81, 114.07) * mm});
            skLineSegment(sketch, "E1323", {"start": v(-52.81, 114.07) * mm, "end": v(-53.07, 114.27) * mm});
            skLineSegment(sketch, "E1324", {"start": v(-53.07, 114.27) * mm, "end": v(-53.34, 114.46) * mm});
            skLineSegment(sketch, "E1325", {"start": v(-53.34, 114.46) * mm, "end": v(-53.6, 114.65) * mm});
            skLineSegment(sketch, "E1326", {"start": v(-53.6, 114.65) * mm, "end": v(-53.88, 114.85) * mm});
            skLineSegment(sketch, "E1327", {"start": v(-53.88, 114.85) * mm, "end": v(-54.15, 115.04) * mm});
            skLineSegment(sketch, "E1328", {"start": v(-54.15, 115.04) * mm, "end": v(-54.43, 115.24) * mm});
            skLineSegment(sketch, "E1329", {"start": v(-54.43, 115.24) * mm, "end": v(-54.72, 115.43) * mm});
            skLineSegment(sketch, "E1330", {"start": v(-54.72, 115.43) * mm, "end": v(-55, 115.63) * mm});
            skLineSegment(sketch, "E1331", {"start": v(-55, 115.63) * mm, "end": v(-55.17, 115.56) * mm});
            skLineSegment(sketch, "E1332", {"start": v(-55.17, 115.56) * mm, "end": v(-56.47, 114.93) * mm});
            skLineSegment(sketch, "E1333", {"start": v(-56.47, 114.93) * mm, "end": v(-56.62, 114.84) * mm});
            skLineSegment(sketch, "E1334", {"start": v(-56.62, 114.84) * mm, "end": v(-56.64, 114.5) * mm});
            skLineSegment(sketch, "E1335", {"start": v(-56.64, 114.5) * mm, "end": v(-56.66, 114.15) * mm});
            skLineSegment(sketch, "E1336", {"start": v(-56.66, 114.15) * mm, "end": v(-56.68, 113.8) * mm});
            skLineSegment(sketch, "E1337", {"start": v(-56.68, 113.8) * mm, "end": v(-56.7, 113.47) * mm});
            skLineSegment(sketch, "E1338", {"start": v(-56.7, 113.47) * mm, "end": v(-56.7, 113.14) * mm});
            skLineSegment(sketch, "E1339", {"start": v(-56.7, 113.14) * mm, "end": v(-56.72, 112.8) * mm});
            skLineSegment(sketch, "E1340", {"start": v(-56.72, 112.8) * mm, "end": v(-56.73, 112.48) * mm});
            skLineSegment(sketch, "E1341", {"start": v(-56.73, 112.48) * mm, "end": v(-56.74, 112.16) * mm});
            skLineSegment(sketch, "E1342", {"start": v(-56.74, 112.16) * mm, "end": v(-56.75, 111.83) * mm});
            skLineSegment(sketch, "E1343", {"start": v(-56.75, 111.83) * mm, "end": v(-56.75, 111.52) * mm});
            skLineSegment(sketch, "E1344", {"start": v(-56.75, 111.52) * mm, "end": v(-56.75, 111.2) * mm});
            skLineSegment(sketch, "E1345", {"start": v(-56.75, 111.2) * mm, "end": v(-56.75, 110.9) * mm});
            skLineSegment(sketch, "E1346", {"start": v(-56.75, 110.9) * mm, "end": v(-56.75, 110.58) * mm});
            skLineSegment(sketch, "E1347", {"start": v(-56.75, 110.58) * mm, "end": v(-56.75, 110.28) * mm});
            skLineSegment(sketch, "E1348", {"start": v(-56.75, 110.28) * mm, "end": v(-56.75, 109.98) * mm});
            skLineSegment(sketch, "E1349", {"start": v(-56.75, 109.98) * mm, "end": v(-56.74, 109.68) * mm});
            skLineSegment(sketch, "E1350", {"start": v(-56.74, 109.68) * mm, "end": v(-56.73, 109.38) * mm});
            skLineSegment(sketch, "E1351", {"start": v(-56.73, 109.38) * mm, "end": v(-56.72, 109.1) * mm});
            skLineSegment(sketch, "E1352", {"start": v(-56.72, 109.1) * mm, "end": v(-56.71, 108.8) * mm});
            skLineSegment(sketch, "E1353", {"start": v(-56.71, 108.8) * mm, "end": v(-56.7, 108.52) * mm});
            skLineSegment(sketch, "E1354", {"start": v(-56.7, 108.52) * mm, "end": v(-56.69, 108.24) * mm});
            skLineSegment(sketch, "E1355", {"start": v(-56.69, 108.24) * mm, "end": v(-56.67, 107.96) * mm});
            skLineSegment(sketch, "E1356", {"start": v(-56.67, 107.96) * mm, "end": v(-56.66, 107.68) * mm});
            skLineSegment(sketch, "E1357", {"start": v(-56.66, 107.68) * mm, "end": v(-56.64, 107.41) * mm});
            skLineSegment(sketch, "E1358", {"start": v(-56.64, 107.41) * mm, "end": v(-56.62, 107.15) * mm});
            skLineSegment(sketch, "E1359", {"start": v(-56.62, 107.15) * mm, "end": v(-56.6, 106.88) * mm});
            skLineSegment(sketch, "E1360", {"start": v(-56.6, 106.88) * mm, "end": v(-56.58, 106.62) * mm});
            skLineSegment(sketch, "E1361", {"start": v(-56.58, 106.62) * mm, "end": v(-56.56, 106.36) * mm});
            skLineSegment(sketch, "E1362", {"start": v(-56.56, 106.36) * mm, "end": v(-56.54, 106.1) * mm});
            skLineSegment(sketch, "E1363", {"start": v(-56.54, 106.1) * mm, "end": v(-56.51, 105.85) * mm});
            skLineSegment(sketch, "E1364", {"start": v(-56.51, 105.85) * mm, "end": v(-57.35, 105.12) * mm});
            skLineSegment(sketch, "E1365", {"start": v(-57.35, 105.12) * mm, "end": v(-58.42, 104.8) * mm});
            skLineSegment(sketch, "E1366", {"start": v(-58.42, 104.8) * mm, "end": v(-58.62, 104.96) * mm});
            skLineSegment(sketch, "E1367", {"start": v(-58.62, 104.96) * mm, "end": v(-58.83, 105.11) * mm});
            skLineSegment(sketch, "E1368", {"start": v(-58.83, 105.11) * mm, "end": v(-59.03, 105.27) * mm});
            skLineSegment(sketch, "E1369", {"start": v(-59.03, 105.27) * mm, "end": v(-59.24, 105.42) * mm});
            skLineSegment(sketch, "E1370", {"start": v(-59.24, 105.42) * mm, "end": v(-59.46, 105.58) * mm});
            skLineSegment(sketch, "E1371", {"start": v(-59.46, 105.58) * mm, "end": v(-59.67, 105.74) * mm});
            skLineSegment(sketch, "E1372", {"start": v(-59.67, 105.74) * mm, "end": v(-59.9, 105.9) * mm});
            skLineSegment(sketch, "E1373", {"start": v(-59.9, 105.9) * mm, "end": v(-60.12, 106.06) * mm});
            skLineSegment(sketch, "E1374", {"start": v(-60.12, 106.06) * mm, "end": v(-60.34, 106.22) * mm});
            skLineSegment(sketch, "E1375", {"start": v(-60.34, 106.22) * mm, "end": v(-60.58, 106.38) * mm});
            skLineSegment(sketch, "E1376", {"start": v(-60.58, 106.38) * mm, "end": v(-60.81, 106.54) * mm});
            skLineSegment(sketch, "E1377", {"start": v(-60.81, 106.54) * mm, "end": v(-61.05, 106.7) * mm});
            skLineSegment(sketch, "E1378", {"start": v(-61.05, 106.7) * mm, "end": v(-61.3, 106.87) * mm});
            skLineSegment(sketch, "E1379", {"start": v(-61.3, 106.87) * mm, "end": v(-61.54, 107.03) * mm});
            skLineSegment(sketch, "E1380", {"start": v(-61.54, 107.03) * mm, "end": v(-61.79, 107.2) * mm});
            skLineSegment(sketch, "E1381", {"start": v(-61.79, 107.2) * mm, "end": v(-62.04, 107.36) * mm});
            skLineSegment(sketch, "E1382", {"start": v(-62.04, 107.36) * mm, "end": v(-62.3, 107.53) * mm});
            skLineSegment(sketch, "E1383", {"start": v(-62.3, 107.53) * mm, "end": v(-62.55, 107.7) * mm});
            skLineSegment(sketch, "E1384", {"start": v(-62.55, 107.7) * mm, "end": v(-62.82, 107.86) * mm});
            skLineSegment(sketch, "E1385", {"start": v(-62.82, 107.86) * mm, "end": v(-63.09, 108.02) * mm});
            skLineSegment(sketch, "E1386", {"start": v(-63.09, 108.02) * mm, "end": v(-63.36, 108.19) * mm});
            skLineSegment(sketch, "E1387", {"start": v(-63.36, 108.19) * mm, "end": v(-63.63, 108.35) * mm});
            skLineSegment(sketch, "E1388", {"start": v(-63.63, 108.35) * mm, "end": v(-63.9, 108.52) * mm});
            skLineSegment(sketch, "E1389", {"start": v(-63.9, 108.52) * mm, "end": v(-64.2, 108.69) * mm});
            skLineSegment(sketch, "E1390", {"start": v(-64.2, 108.69) * mm, "end": v(-64.48, 108.85) * mm});
            skLineSegment(sketch, "E1391", {"start": v(-64.48, 108.85) * mm, "end": v(-64.77, 109.02) * mm});
            skLineSegment(sketch, "E1392", {"start": v(-64.77, 109.02) * mm, "end": v(-65.06, 109.19) * mm});
            skLineSegment(sketch, "E1393", {"start": v(-65.06, 109.19) * mm, "end": v(-65.36, 109.35) * mm});
            skLineSegment(sketch, "E1394", {"start": v(-65.36, 109.35) * mm, "end": v(-65.66, 109.52) * mm});
            skLineSegment(sketch, "E1395", {"start": v(-65.66, 109.52) * mm, "end": v(-65.96, 109.69) * mm});
            skLineSegment(sketch, "E1396", {"start": v(-65.96, 109.69) * mm, "end": v(-66.12, 109.6) * mm});
            skLineSegment(sketch, "E1397", {"start": v(-66.12, 109.6) * mm, "end": v(-67.35, 108.84) * mm});
            skLineSegment(sketch, "E1398", {"start": v(-67.35, 108.84) * mm, "end": v(-67.5, 108.74) * mm});
            skLineSegment(sketch, "E1399", {"start": v(-67.5, 108.74) * mm, "end": v(-67.48, 108.4) * mm});
            skLineSegment(sketch, "E1400", {"start": v(-67.48, 108.4) * mm, "end": v(-67.47, 108.05) * mm});
            skLineSegment(sketch, "E1401", {"start": v(-67.47, 108.05) * mm, "end": v(-67.45, 107.71) * mm});
            skLineSegment(sketch, "E1402", {"start": v(-67.45, 107.71) * mm, "end": v(-67.44, 107.37) * mm});
            skLineSegment(sketch, "E1403", {"start": v(-67.44, 107.37) * mm, "end": v(-67.42, 107.04) * mm});
            skLineSegment(sketch, "E1404", {"start": v(-67.42, 107.04) * mm, "end": v(-67.4, 106.7) * mm});
            skLineSegment(sketch, "E1405", {"start": v(-67.4, 106.7) * mm, "end": v(-67.37, 106.38) * mm});
            skLineSegment(sketch, "E1406", {"start": v(-67.37, 106.38) * mm, "end": v(-67.35, 106.06) * mm});
            skLineSegment(sketch, "E1407", {"start": v(-67.35, 106.06) * mm, "end": v(-67.32, 105.74) * mm});
            skLineSegment(sketch, "E1408", {"start": v(-67.32, 105.74) * mm, "end": v(-67.3, 105.42) * mm});
            skLineSegment(sketch, "E1409", {"start": v(-67.3, 105.42) * mm, "end": v(-67.27, 105.1) * mm});
            skLineSegment(sketch, "E1410", {"start": v(-67.27, 105.1) * mm, "end": v(-67.24, 104.8) * mm});
            skLineSegment(sketch, "E1411", {"start": v(-67.24, 104.8) * mm, "end": v(-67.2, 104.5) * mm});
            skLineSegment(sketch, "E1412", {"start": v(-67.2, 104.5) * mm, "end": v(-67.18, 104.2) * mm});
            skLineSegment(sketch, "E1413", {"start": v(-67.18, 104.2) * mm, "end": v(-67.14, 103.9) * mm});
            skLineSegment(sketch, "E1414", {"start": v(-67.14, 103.9) * mm, "end": v(-67.1, 103.6) * mm});
            skLineSegment(sketch, "E1415", {"start": v(-67.1, 103.6) * mm, "end": v(-67.07, 103.3) * mm});
            skLineSegment(sketch, "E1416", {"start": v(-67.07, 103.3) * mm, "end": v(-67.03, 103.01) * mm});
            skLineSegment(sketch, "E1417", {"start": v(-67.03, 103.01) * mm, "end": v(-67, 102.73) * mm});
            skLineSegment(sketch, "E1418", {"start": v(-67, 102.73) * mm, "end": v(-66.96, 102.44) * mm});
            skLineSegment(sketch, "E1419", {"start": v(-66.96, 102.44) * mm, "end": v(-66.92, 102.17) * mm});
            skLineSegment(sketch, "E1420", {"start": v(-66.92, 102.17) * mm, "end": v(-66.87, 101.89) * mm});
            skLineSegment(sketch, "E1421", {"start": v(-66.87, 101.89) * mm, "end": v(-66.83, 101.62) * mm});
            skLineSegment(sketch, "E1422", {"start": v(-66.83, 101.62) * mm, "end": v(-66.79, 101.35) * mm});
            skLineSegment(sketch, "E1423", {"start": v(-66.79, 101.35) * mm, "end": v(-66.74, 101.08) * mm});
            skLineSegment(sketch, "E1424", {"start": v(-66.74, 101.08) * mm, "end": v(-66.7, 100.82) * mm});
            skLineSegment(sketch, "E1425", {"start": v(-66.7, 100.82) * mm, "end": v(-66.65, 100.56) * mm});
            skLineSegment(sketch, "E1426", {"start": v(-66.65, 100.56) * mm, "end": v(-66.6, 100.31) * mm});
            skLineSegment(sketch, "E1427", {"start": v(-66.6, 100.31) * mm, "end": v(-66.56, 100.06) * mm});
            skLineSegment(sketch, "E1428", {"start": v(-66.56, 100.06) * mm, "end": v(-66.5, 99.81) * mm});
            skLineSegment(sketch, "E1429", {"start": v(-66.5, 99.81) * mm, "end": v(-67.27, 99) * mm});
            skLineSegment(sketch, "E1430", {"start": v(-67.27, 99) * mm, "end": v(-68.3, 98.58) * mm});
            skLineSegment(sketch, "E1431", {"start": v(-68.3, 98.58) * mm, "end": v(-68.52, 98.71) * mm});
            skLineSegment(sketch, "E1432", {"start": v(-68.52, 98.71) * mm, "end": v(-68.74, 98.84) * mm});
            skLineSegment(sketch, "E1433", {"start": v(-68.74, 98.84) * mm, "end": v(-68.96, 98.98) * mm});
            skLineSegment(sketch, "E1434", {"start": v(-68.96, 98.98) * mm, "end": v(-69.18, 99.12) * mm});
            skLineSegment(sketch, "E1435", {"start": v(-69.18, 99.12) * mm, "end": v(-69.4, 99.25) * mm});
            skLineSegment(sketch, "E1436", {"start": v(-69.4, 99.25) * mm, "end": v(-69.64, 99.4) * mm});
            skLineSegment(sketch, "E1437", {"start": v(-69.64, 99.4) * mm, "end": v(-69.88, 99.53) * mm});
            skLineSegment(sketch, "E1438", {"start": v(-69.88, 99.53) * mm, "end": v(-70.12, 99.66) * mm});
            skLineSegment(sketch, "E1439", {"start": v(-70.12, 99.66) * mm, "end": v(-70.36, 99.8) * mm});
            skLineSegment(sketch, "E1440", {"start": v(-70.36, 99.8) * mm, "end": v(-70.6, 99.94) * mm});
            skLineSegment(sketch, "E1441", {"start": v(-70.6, 99.94) * mm, "end": v(-70.85, 100.08) * mm});
            skLineSegment(sketch, "E1442", {"start": v(-70.85, 100.08) * mm, "end": v(-71.1, 100.22) * mm});
            skLineSegment(sketch, "E1443", {"start": v(-71.1, 100.22) * mm, "end": v(-71.36, 100.35) * mm});
            skLineSegment(sketch, "E1444", {"start": v(-71.36, 100.35) * mm, "end": v(-71.62, 100.5) * mm});
            skLineSegment(sketch, "E1445", {"start": v(-71.62, 100.5) * mm, "end": v(-71.89, 100.63) * mm});
            skLineSegment(sketch, "E1446", {"start": v(-71.89, 100.63) * mm, "end": v(-72.15, 100.77) * mm});
            skLineSegment(sketch, "E1447", {"start": v(-72.15, 100.77) * mm, "end": v(-72.43, 100.9) * mm});
            skLineSegment(sketch, "E1448", {"start": v(-72.43, 100.9) * mm, "end": v(-72.7, 101.05) * mm});
            skLineSegment(sketch, "E1449", {"start": v(-72.7, 101.05) * mm, "end": v(-72.98, 101.18) * mm});
            skLineSegment(sketch, "E1450", {"start": v(-72.98, 101.18) * mm, "end": v(-73.26, 101.32) * mm});
            skLineSegment(sketch, "E1451", {"start": v(-73.26, 101.32) * mm, "end": v(-73.55, 101.46) * mm});
            skLineSegment(sketch, "E1452", {"start": v(-73.55, 101.46) * mm, "end": v(-73.84, 101.6) * mm});
            skLineSegment(sketch, "E1453", {"start": v(-73.84, 101.6) * mm, "end": v(-74.13, 101.74) * mm});
            skLineSegment(sketch, "E1454", {"start": v(-74.13, 101.74) * mm, "end": v(-74.43, 101.88) * mm});
            skLineSegment(sketch, "E1455", {"start": v(-74.43, 101.88) * mm, "end": v(-74.73, 102.01) * mm});
            skLineSegment(sketch, "E1456", {"start": v(-74.73, 102.01) * mm, "end": v(-75.03, 102.15) * mm});
            skLineSegment(sketch, "E1457", {"start": v(-75.03, 102.15) * mm, "end": v(-75.34, 102.29) * mm});
            skLineSegment(sketch, "E1458", {"start": v(-75.34, 102.29) * mm, "end": v(-75.65, 102.43) * mm});
            skLineSegment(sketch, "E1459", {"start": v(-75.65, 102.43) * mm, "end": v(-75.97, 102.56) * mm});
            skLineSegment(sketch, "E1460", {"start": v(-75.97, 102.56) * mm, "end": v(-76.29, 102.7) * mm});
            skLineSegment(sketch, "E1461", {"start": v(-76.29, 102.7) * mm, "end": v(-76.44, 102.6) * mm});
            skLineSegment(sketch, "E1462", {"start": v(-76.44, 102.6) * mm, "end": v(-77.59, 101.73) * mm});
            skLineSegment(sketch, "E1463", {"start": v(-77.59, 101.73) * mm, "end": v(-77.72, 101.6) * mm});
            skLineSegment(sketch, "E1464", {"start": v(-77.72, 101.6) * mm, "end": v(-77.67, 101.26) * mm});
            skLineSegment(sketch, "E1465", {"start": v(-77.67, 101.26) * mm, "end": v(-77.63, 100.92) * mm});
            skLineSegment(sketch, "E1466", {"start": v(-77.63, 100.92) * mm, "end": v(-77.58, 100.59) * mm});
            skLineSegment(sketch, "E1467", {"start": v(-77.58, 100.59) * mm, "end": v(-77.53, 100.25) * mm});
            skLineSegment(sketch, "E1468", {"start": v(-77.53, 100.25) * mm, "end": v(-77.48, 99.92) * mm});
            skLineSegment(sketch, "E1469", {"start": v(-77.48, 99.92) * mm, "end": v(-77.42, 99.6) * mm});
            skLineSegment(sketch, "E1470", {"start": v(-77.42, 99.6) * mm, "end": v(-77.37, 99.27) * mm});
            skLineSegment(sketch, "E1471", {"start": v(-77.37, 99.27) * mm, "end": v(-77.31, 98.95) * mm});
            skLineSegment(sketch, "E1472", {"start": v(-77.31, 98.95) * mm, "end": v(-77.26, 98.64) * mm});
            skLineSegment(sketch, "E1473", {"start": v(-77.26, 98.64) * mm, "end": v(-77.2, 98.32) * mm});
            skLineSegment(sketch, "E1474", {"start": v(-77.2, 98.32) * mm, "end": v(-77.14, 98.01) * mm});
            skLineSegment(sketch, "E1475", {"start": v(-77.14, 98.01) * mm, "end": v(-77.08, 97.7) * mm});
            skLineSegment(sketch, "E1476", {"start": v(-77.08, 97.7) * mm, "end": v(-77.02, 97.4) * mm});
            skLineSegment(sketch, "E1477", {"start": v(-77.02, 97.4) * mm, "end": v(-76.96, 97.1) * mm});
            skLineSegment(sketch, "E1478", {"start": v(-76.96, 97.1) * mm, "end": v(-76.9, 96.81) * mm});
            skLineSegment(sketch, "E1479", {"start": v(-76.9, 96.81) * mm, "end": v(-76.83, 96.52) * mm});
            skLineSegment(sketch, "E1480", {"start": v(-76.83, 96.52) * mm, "end": v(-76.77, 96.24) * mm});
            skLineSegment(sketch, "E1481", {"start": v(-76.77, 96.24) * mm, "end": v(-76.7, 95.95) * mm});
            skLineSegment(sketch, "E1482", {"start": v(-76.7, 95.95) * mm, "end": v(-76.63, 95.67) * mm});
            skLineSegment(sketch, "E1483", {"start": v(-76.63, 95.67) * mm, "end": v(-76.57, 95.4) * mm});
            skLineSegment(sketch, "E1484", {"start": v(-76.57, 95.4) * mm, "end": v(-76.5, 95.12) * mm});
            skLineSegment(sketch, "E1485", {"start": v(-76.5, 95.12) * mm, "end": v(-76.43, 94.85) * mm});
            skLineSegment(sketch, "E1486", {"start": v(-76.43, 94.85) * mm, "end": v(-76.36, 94.58) * mm});
            skLineSegment(sketch, "E1487", {"start": v(-76.36, 94.58) * mm, "end": v(-76.3, 94.32) * mm});
            skLineSegment(sketch, "E1488", {"start": v(-76.3, 94.32) * mm, "end": v(-76.22, 94.06) * mm});
            skLineSegment(sketch, "E1489", {"start": v(-76.22, 94.06) * mm, "end": v(-76.15, 93.8) * mm});
            skLineSegment(sketch, "E1490", {"start": v(-76.15, 93.8) * mm, "end": v(-76.08, 93.55) * mm});
            skLineSegment(sketch, "E1491", {"start": v(-76.08, 93.55) * mm, "end": v(-76, 93.3) * mm});
            skLineSegment(sketch, "E1492", {"start": v(-76, 93.3) * mm, "end": v(-75.94, 93.06) * mm});
            skLineSegment(sketch, "E1493", {"start": v(-75.94, 93.06) * mm, "end": v(-75.86, 92.82) * mm});
            skLineSegment(sketch, "E1494", {"start": v(-75.86, 92.82) * mm, "end": v(-76.55, 91.93) * mm});
            skLineSegment(sketch, "E1495", {"start": v(-76.55, 91.93) * mm, "end": v(-77.53, 91.41) * mm});
            skLineSegment(sketch, "E1496", {"start": v(-77.53, 91.41) * mm, "end": v(-77.76, 91.52) * mm});
            skLineSegment(sketch, "E1497", {"start": v(-77.76, 91.52) * mm, "end": v(-77.99, 91.64) * mm});
            skLineSegment(sketch, "E1498", {"start": v(-77.99, 91.64) * mm, "end": v(-78.22, 91.75) * mm});
            skLineSegment(sketch, "E1499", {"start": v(-78.22, 91.75) * mm, "end": v(-78.46, 91.86) * mm});
            skLineSegment(sketch, "E1500", {"start": v(-78.46, 91.86) * mm, "end": v(-78.7, 91.98) * mm});
            skLineSegment(sketch, "E1501", {"start": v(-78.7, 91.98) * mm, "end": v(-78.94, 92.09) * mm});
            skLineSegment(sketch, "E1502", {"start": v(-78.94, 92.09) * mm, "end": v(-79.19, 92.2) * mm});
            skLineSegment(sketch, "E1503", {"start": v(-79.19, 92.2) * mm, "end": v(-79.44, 92.32) * mm});
            skLineSegment(sketch, "E1504", {"start": v(-79.44, 92.32) * mm, "end": v(-79.7, 92.43) * mm});
            skLineSegment(sketch, "E1505", {"start": v(-79.7, 92.43) * mm, "end": v(-79.95, 92.54) * mm});
            skLineSegment(sketch, "E1506", {"start": v(-79.95, 92.54) * mm, "end": v(-80.21, 92.65) * mm});
            skLineSegment(sketch, "E1507", {"start": v(-80.21, 92.65) * mm, "end": v(-80.48, 92.77) * mm});
            skLineSegment(sketch, "E1508", {"start": v(-80.48, 92.77) * mm, "end": v(-80.75, 92.88) * mm});
            skLineSegment(sketch, "E1509", {"start": v(-80.75, 92.88) * mm, "end": v(-81.02, 93) * mm});
            skLineSegment(sketch, "E1510", {"start": v(-81.02, 93) * mm, "end": v(-81.3, 93.1) * mm});
            skLineSegment(sketch, "E1511", {"start": v(-81.3, 93.1) * mm, "end": v(-81.58, 93.22) * mm});
            skLineSegment(sketch, "E1512", {"start": v(-81.58, 93.22) * mm, "end": v(-81.86, 93.33) * mm});
            skLineSegment(sketch, "E1513", {"start": v(-81.86, 93.33) * mm, "end": v(-82.15, 93.44) * mm});
            skLineSegment(sketch, "E1514", {"start": v(-82.15, 93.44) * mm, "end": v(-82.44, 93.55) * mm});
            skLineSegment(sketch, "E1515", {"start": v(-82.44, 93.55) * mm, "end": v(-82.73, 93.66) * mm});
            skLineSegment(sketch, "E1516", {"start": v(-82.73, 93.66) * mm, "end": v(-83.03, 93.77) * mm});
            skLineSegment(sketch, "E1517", {"start": v(-83.03, 93.77) * mm, "end": v(-83.33, 93.88) * mm});
            skLineSegment(sketch, "E1518", {"start": v(-83.33, 93.88) * mm, "end": v(-83.64, 93.99) * mm});
            skLineSegment(sketch, "E1519", {"start": v(-83.64, 93.99) * mm, "end": v(-83.95, 94.1) * mm});
            skLineSegment(sketch, "E1520", {"start": v(-83.95, 94.1) * mm, "end": v(-84.26, 94.2) * mm});
            skLineSegment(sketch, "E1521", {"start": v(-84.26, 94.2) * mm, "end": v(-84.58, 94.31) * mm});
            skLineSegment(sketch, "E1522", {"start": v(-84.58, 94.31) * mm, "end": v(-84.9, 94.42) * mm});
            skLineSegment(sketch, "E1523", {"start": v(-84.9, 94.42) * mm, "end": v(-85.22, 94.52) * mm});
            skLineSegment(sketch, "E1524", {"start": v(-85.22, 94.52) * mm, "end": v(-85.55, 94.63) * mm});
            skLineSegment(sketch, "E1525", {"start": v(-85.55, 94.63) * mm, "end": v(-85.88, 94.73) * mm});
            skLineSegment(sketch, "E1526", {"start": v(-85.88, 94.73) * mm, "end": v(-86.02, 94.62) * mm});
            skLineSegment(sketch, "E1527", {"start": v(-86.02, 94.62) * mm, "end": v(-87.08, 93.63) * mm});
            skLineSegment(sketch, "E1528", {"start": v(-87.08, 93.63) * mm, "end": v(-87.2, 93.5) * mm});
            skLineSegment(sketch, "E1529", {"start": v(-87.2, 93.5) * mm, "end": v(-87.12, 93.17) * mm});
            skLineSegment(sketch, "E1530", {"start": v(-87.12, 93.17) * mm, "end": v(-87.04, 92.83) * mm});
            skLineSegment(sketch, "E1531", {"start": v(-87.04, 92.83) * mm, "end": v(-86.95, 92.5) * mm});
            skLineSegment(sketch, "E1532", {"start": v(-86.95, 92.5) * mm, "end": v(-86.87, 92.17) * mm});
            skLineSegment(sketch, "E1533", {"start": v(-86.87, 92.17) * mm, "end": v(-86.79, 91.85) * mm});
            skLineSegment(sketch, "E1534", {"start": v(-86.79, 91.85) * mm, "end": v(-86.7, 91.53) * mm});
            skLineSegment(sketch, "E1535", {"start": v(-86.7, 91.53) * mm, "end": v(-86.62, 91.21) * mm});
            skLineSegment(sketch, "E1536", {"start": v(-86.62, 91.21) * mm, "end": v(-86.53, 90.9) * mm});
            skLineSegment(sketch, "E1537", {"start": v(-86.53, 90.9) * mm, "end": v(-86.44, 90.6) * mm});
            skLineSegment(sketch, "E1538", {"start": v(-86.44, 90.6) * mm, "end": v(-86.36, 90.29) * mm});
            skLineSegment(sketch, "E1539", {"start": v(-86.36, 90.29) * mm, "end": v(-86.27, 89.99) * mm});
            skLineSegment(sketch, "E1540", {"start": v(-86.27, 89.99) * mm, "end": v(-86.18, 89.69) * mm});
            skLineSegment(sketch, "E1541", {"start": v(-86.18, 89.69) * mm, "end": v(-86.09, 89.4) * mm});
            skLineSegment(sketch, "E1542", {"start": v(-86.09, 89.4) * mm, "end": v(-86, 89.1) * mm});
            skLineSegment(sketch, "E1543", {"start": v(-86, 89.1) * mm, "end": v(-85.9, 88.82) * mm});
            skLineSegment(sketch, "E1544", {"start": v(-85.9, 88.82) * mm, "end": v(-85.81, 88.53) * mm});
            skLineSegment(sketch, "E1545", {"start": v(-85.81, 88.53) * mm, "end": v(-85.72, 88.25) * mm});
            skLineSegment(sketch, "E1546", {"start": v(-85.72, 88.25) * mm, "end": v(-85.63, 87.98) * mm});
            skLineSegment(sketch, "E1547", {"start": v(-85.63, 87.98) * mm, "end": v(-85.53, 87.7) * mm});
            skLineSegment(sketch, "E1548", {"start": v(-85.53, 87.7) * mm, "end": v(-85.44, 87.43) * mm});
            skLineSegment(sketch, "E1549", {"start": v(-85.44, 87.43) * mm, "end": v(-85.35, 87.17) * mm});
            skLineSegment(sketch, "E1550", {"start": v(-85.35, 87.17) * mm, "end": v(-85.25, 86.9) * mm});
            skLineSegment(sketch, "E1551", {"start": v(-85.25, 86.9) * mm, "end": v(-85.16, 86.65) * mm});
            skLineSegment(sketch, "E1552", {"start": v(-85.16, 86.65) * mm, "end": v(-85.06, 86.4) * mm});
            skLineSegment(sketch, "E1553", {"start": v(-85.06, 86.4) * mm, "end": v(-84.97, 86.14) * mm});
            skLineSegment(sketch, "E1554", {"start": v(-84.97, 86.14) * mm, "end": v(-84.87, 85.9) * mm});
            skLineSegment(sketch, "E1555", {"start": v(-84.87, 85.9) * mm, "end": v(-84.78, 85.65) * mm});
            skLineSegment(sketch, "E1556", {"start": v(-84.78, 85.65) * mm, "end": v(-84.68, 85.4) * mm});
            skLineSegment(sketch, "E1557", {"start": v(-84.68, 85.4) * mm, "end": v(-84.58, 85.17) * mm});
            skLineSegment(sketch, "E1558", {"start": v(-84.58, 85.17) * mm, "end": v(-84.49, 84.94) * mm});
            skLineSegment(sketch, "E1559", {"start": v(-84.49, 84.94) * mm, "end": v(-85.08, 84) * mm});
            skLineSegment(sketch, "E1560", {"start": v(-85.08, 84) * mm, "end": v(-86, 83.38) * mm});
            skLineSegment(sketch, "E1561", {"start": v(-86, 83.38) * mm, "end": v(-86.24, 83.47) * mm});
            skLineSegment(sketch, "E1562", {"start": v(-86.24, 83.47) * mm, "end": v(-86.48, 83.56) * mm});
            skLineSegment(sketch, "E1563", {"start": v(-86.48, 83.56) * mm, "end": v(-86.73, 83.65) * mm});
            skLineSegment(sketch, "E1564", {"start": v(-86.73, 83.65) * mm, "end": v(-86.97, 83.74) * mm});
            skLineSegment(sketch, "E1565", {"start": v(-86.97, 83.74) * mm, "end": v(-87.22, 83.82) * mm});
            skLineSegment(sketch, "E1566", {"start": v(-87.22, 83.82) * mm, "end": v(-87.48, 83.92) * mm});
            skLineSegment(sketch, "E1567", {"start": v(-87.48, 83.92) * mm, "end": v(-87.73, 84) * mm});
            skLineSegment(sketch, "E1568", {"start": v(-87.73, 84) * mm, "end": v(-88, 84.1) * mm});
            skLineSegment(sketch, "E1569", {"start": v(-88, 84.1) * mm, "end": v(-88.26, 84.18) * mm});
            skLineSegment(sketch, "E1570", {"start": v(-88.26, 84.18) * mm, "end": v(-88.53, 84.27) * mm});
            skLineSegment(sketch, "E1571", {"start": v(-88.53, 84.27) * mm, "end": v(-88.8, 84.35) * mm});
            skLineSegment(sketch, "E1572", {"start": v(-88.8, 84.35) * mm, "end": v(-89.07, 84.44) * mm});
            skLineSegment(sketch, "E1573", {"start": v(-89.07, 84.44) * mm, "end": v(-89.35, 84.52) * mm});
            skLineSegment(sketch, "E1574", {"start": v(-89.35, 84.52) * mm, "end": v(-89.64, 84.6) * mm});
            skLineSegment(sketch, "E1575", {"start": v(-89.64, 84.6) * mm, "end": v(-89.92, 84.7) * mm});
            skLineSegment(sketch, "E1576", {"start": v(-89.92, 84.7) * mm, "end": v(-90.21, 84.78) * mm});
            skLineSegment(sketch, "E1577", {"start": v(-90.21, 84.78) * mm, "end": v(-90.5, 84.86) * mm});
            skLineSegment(sketch, "E1578", {"start": v(-90.5, 84.86) * mm, "end": v(-90.8, 84.94) * mm});
            skLineSegment(sketch, "E1579", {"start": v(-90.8, 84.94) * mm, "end": v(-91.1, 85.03) * mm});
            skLineSegment(sketch, "E1580", {"start": v(-91.1, 85.03) * mm, "end": v(-91.4, 85.1) * mm});
            skLineSegment(sketch, "E1581", {"start": v(-91.4, 85.1) * mm, "end": v(-91.71, 85.19) * mm});
            skLineSegment(sketch, "E1582", {"start": v(-91.71, 85.19) * mm, "end": v(-92.02, 85.27) * mm});
            skLineSegment(sketch, "E1583", {"start": v(-92.02, 85.27) * mm, "end": v(-92.34, 85.34) * mm});
            skLineSegment(sketch, "E1584", {"start": v(-92.34, 85.34) * mm, "end": v(-92.66, 85.42) * mm});
            skLineSegment(sketch, "E1585", {"start": v(-92.66, 85.42) * mm, "end": v(-92.98, 85.5) * mm});
            skLineSegment(sketch, "E1586", {"start": v(-92.98, 85.5) * mm, "end": v(-93.3, 85.57) * mm});
            skLineSegment(sketch, "E1587", {"start": v(-93.3, 85.57) * mm, "end": v(-93.63, 85.65) * mm});
            skLineSegment(sketch, "E1588", {"start": v(-93.63, 85.65) * mm, "end": v(-93.97, 85.72) * mm});
            skLineSegment(sketch, "E1589", {"start": v(-93.97, 85.72) * mm, "end": v(-94.3, 85.8) * mm});
            skLineSegment(sketch, "E1590", {"start": v(-94.3, 85.8) * mm, "end": v(-94.64, 85.86) * mm});
            skLineSegment(sketch, "E1591", {"start": v(-94.64, 85.86) * mm, "end": v(-94.77, 85.74) * mm});
            skLineSegment(sketch, "E1592", {"start": v(-94.77, 85.74) * mm, "end": v(-95.73, 84.65) * mm});
            skLineSegment(sketch, "E1593", {"start": v(-95.73, 84.65) * mm, "end": v(-95.83, 84.51) * mm});
            skLineSegment(sketch, "E1594", {"start": v(-95.83, 84.51) * mm, "end": v(-95.72, 84.18) * mm});
            skLineSegment(sketch, "E1595", {"start": v(-95.72, 84.18) * mm, "end": v(-95.6, 83.86) * mm});
            skLineSegment(sketch, "E1596", {"start": v(-95.6, 83.86) * mm, "end": v(-95.5, 83.54) * mm});
            skLineSegment(sketch, "E1597", {"start": v(-95.5, 83.54) * mm, "end": v(-95.38, 83.22) * mm});
            skLineSegment(sketch, "E1598", {"start": v(-95.38, 83.22) * mm, "end": v(-95.26, 82.9) * mm});
            skLineSegment(sketch, "E1599", {"start": v(-95.26, 82.9) * mm, "end": v(-95.15, 82.6) * mm});
            skLineSegment(sketch, "E1600", {"start": v(-95.15, 82.6) * mm, "end": v(-95.03, 82.3) * mm});
            skLineSegment(sketch, "E1601", {"start": v(-95.03, 82.3) * mm, "end": v(-94.92, 81.99) * mm});
            skLineSegment(sketch, "E1602", {"start": v(-94.92, 81.99) * mm, "end": v(-94.8, 81.7) * mm});
            skLineSegment(sketch, "E1603", {"start": v(-94.8, 81.7) * mm, "end": v(-94.68, 81.4) * mm});
            skLineSegment(sketch, "E1604", {"start": v(-94.68, 81.4) * mm, "end": v(-94.56, 81.1) * mm});
            skLineSegment(sketch, "E1605", {"start": v(-94.56, 81.1) * mm, "end": v(-94.45, 80.81) * mm});
            skLineSegment(sketch, "E1606", {"start": v(-94.45, 80.81) * mm, "end": v(-94.33, 80.53) * mm});
            skLineSegment(sketch, "E1607", {"start": v(-94.33, 80.53) * mm, "end": v(-94.2, 80.25) * mm});
            skLineSegment(sketch, "E1608", {"start": v(-94.2, 80.25) * mm, "end": v(-94.09, 79.97) * mm});
            skLineSegment(sketch, "E1609", {"start": v(-94.09, 79.97) * mm, "end": v(-93.97, 79.7) * mm});
            skLineSegment(sketch, "E1610", {"start": v(-93.97, 79.7) * mm, "end": v(-93.85, 79.43) * mm});
            skLineSegment(sketch, "E1611", {"start": v(-93.85, 79.43) * mm, "end": v(-93.73, 79.16) * mm});
            skLineSegment(sketch, "E1612", {"start": v(-93.73, 79.16) * mm, "end": v(-93.61, 78.9) * mm});
            skLineSegment(sketch, "E1613", {"start": v(-93.61, 78.9) * mm, "end": v(-93.5, 78.64) * mm});
            skLineSegment(sketch, "E1614", {"start": v(-93.5, 78.64) * mm, "end": v(-93.37, 78.39) * mm});
            skLineSegment(sketch, "E1615", {"start": v(-93.37, 78.39) * mm, "end": v(-93.25, 78.14) * mm});
            skLineSegment(sketch, "E1616", {"start": v(-93.25, 78.14) * mm, "end": v(-93.13, 77.9) * mm});
            skLineSegment(sketch, "E1617", {"start": v(-93.13, 77.9) * mm, "end": v(-93.01, 77.64) * mm});
            skLineSegment(sketch, "E1618", {"start": v(-93.01, 77.64) * mm, "end": v(-92.9, 77.4) * mm});
            skLineSegment(sketch, "E1619", {"start": v(-92.9, 77.4) * mm, "end": v(-92.77, 77.17) * mm});
            skLineSegment(sketch, "E1620", {"start": v(-92.77, 77.17) * mm, "end": v(-92.65, 76.93) * mm});
            skLineSegment(sketch, "E1621", {"start": v(-92.65, 76.93) * mm, "end": v(-92.54, 76.7) * mm});
            skLineSegment(sketch, "E1622", {"start": v(-92.54, 76.7) * mm, "end": v(-92.42, 76.48) * mm});
            skLineSegment(sketch, "E1623", {"start": v(-92.42, 76.48) * mm, "end": v(-92.3, 76.25) * mm});
            skLineSegment(sketch, "E1624", {"start": v(-92.3, 76.25) * mm, "end": v(-92.8, 75.26) * mm});
            skLineSegment(sketch, "E1625", {"start": v(-92.8, 75.26) * mm, "end": v(-93.66, 74.55) * mm});
            skLineSegment(sketch, "E1626", {"start": v(-93.66, 74.55) * mm, "end": v(-93.9, 74.62) * mm});
            skLineSegment(sketch, "E1627", {"start": v(-93.9, 74.62) * mm, "end": v(-94.15, 74.68) * mm});
            skLineSegment(sketch, "E1628", {"start": v(-94.15, 74.68) * mm, "end": v(-94.4, 74.75) * mm});
            skLineSegment(sketch, "E1629", {"start": v(-94.4, 74.75) * mm, "end": v(-94.65, 74.81) * mm});
            skLineSegment(sketch, "E1630", {"start": v(-94.65, 74.81) * mm, "end": v(-94.91, 74.88) * mm});
            skLineSegment(sketch, "E1631", {"start": v(-94.91, 74.88) * mm, "end": v(-95.17, 74.94) * mm});
            skLineSegment(sketch, "E1632", {"start": v(-95.17, 74.94) * mm, "end": v(-95.44, 75) * mm});
            skLineSegment(sketch, "E1633", {"start": v(-95.44, 75) * mm, "end": v(-95.7, 75.07) * mm});
            skLineSegment(sketch, "E1634", {"start": v(-95.7, 75.07) * mm, "end": v(-95.98, 75.13) * mm});
            skLineSegment(sketch, "E1635", {"start": v(-95.98, 75.13) * mm, "end": v(-96.25, 75.19) * mm});
            skLineSegment(sketch, "E1636", {"start": v(-96.25, 75.19) * mm, "end": v(-96.53, 75.25) * mm});
            skLineSegment(sketch, "E1637", {"start": v(-96.53, 75.25) * mm, "end": v(-96.81, 75.3) * mm});
            skLineSegment(sketch, "E1638", {"start": v(-96.81, 75.3) * mm, "end": v(-97.1, 75.36) * mm});
            skLineSegment(sketch, "E1639", {"start": v(-97.1, 75.36) * mm, "end": v(-97.39, 75.42) * mm});
            skLineSegment(sketch, "E1640", {"start": v(-97.39, 75.42) * mm, "end": v(-97.68, 75.48) * mm});
            skLineSegment(sketch, "E1641", {"start": v(-97.68, 75.48) * mm, "end": v(-97.98, 75.53) * mm});
            skLineSegment(sketch, "E1642", {"start": v(-97.98, 75.53) * mm, "end": v(-98.28, 75.59) * mm});
            skLineSegment(sketch, "E1643", {"start": v(-98.28, 75.59) * mm, "end": v(-98.58, 75.64) * mm});
            skLineSegment(sketch, "E1644", {"start": v(-98.58, 75.64) * mm, "end": v(-98.89, 75.7) * mm});
            skLineSegment(sketch, "E1645", {"start": v(-98.89, 75.7) * mm, "end": v(-99.2, 75.74) * mm});
            skLineSegment(sketch, "E1646", {"start": v(-99.2, 75.74) * mm, "end": v(-99.51, 75.8) * mm});
            skLineSegment(sketch, "E1647", {"start": v(-99.51, 75.8) * mm, "end": v(-99.83, 75.84) * mm});
            skLineSegment(sketch, "E1648", {"start": v(-99.83, 75.84) * mm, "end": v(-100.15, 75.89) * mm});
            skLineSegment(sketch, "E1649", {"start": v(-100.15, 75.89) * mm, "end": v(-100.47, 75.93) * mm});
            skLineSegment(sketch, "E1650", {"start": v(-100.47, 75.93) * mm, "end": v(-100.8, 75.98) * mm});
            skLineSegment(sketch, "E1651", {"start": v(-100.8, 75.98) * mm, "end": v(-101.13, 76.02) * mm});
            skLineSegment(sketch, "E1652", {"start": v(-101.13, 76.02) * mm, "end": v(-101.47, 76.06) * mm});
            skLineSegment(sketch, "E1653", {"start": v(-101.47, 76.06) * mm, "end": v(-101.8, 76.1) * mm});
            skLineSegment(sketch, "E1654", {"start": v(-101.8, 76.1) * mm, "end": v(-102.15, 76.14) * mm});
            skLineSegment(sketch, "E1655", {"start": v(-102.15, 76.14) * mm, "end": v(-102.5, 76.18) * mm});
            skLineSegment(sketch, "E1656", {"start": v(-102.5, 76.18) * mm, "end": v(-102.6, 76.04) * mm});
            skLineSegment(sketch, "E1657", {"start": v(-102.6, 76.04) * mm, "end": v(-103.46, 74.87) * mm});
            skLineSegment(sketch, "E1658", {"start": v(-103.46, 74.87) * mm, "end": v(-103.55, 74.72) * mm});
            skLineSegment(sketch, "E1659", {"start": v(-103.55, 74.72) * mm, "end": v(-103.4, 74.4) * mm});
            skLineSegment(sketch, "E1660", {"start": v(-103.4, 74.4) * mm, "end": v(-103.26, 74.1) * mm});
            skLineSegment(sketch, "E1661", {"start": v(-103.26, 74.1) * mm, "end": v(-103.11, 73.78) * mm});
            skLineSegment(sketch, "E1662", {"start": v(-103.11, 73.78) * mm, "end": v(-102.97, 73.48) * mm});
            skLineSegment(sketch, "E1663", {"start": v(-102.97, 73.48) * mm, "end": v(-102.82, 73.18) * mm});
            skLineSegment(sketch, "E1664", {"start": v(-102.82, 73.18) * mm, "end": v(-102.68, 72.88) * mm});
            skLineSegment(sketch, "E1665", {"start": v(-102.68, 72.88) * mm, "end": v(-102.53, 72.59) * mm});
            skLineSegment(sketch, "E1666", {"start": v(-102.53, 72.59) * mm, "end": v(-102.39, 72.3) * mm});
            skLineSegment(sketch, "E1667", {"start": v(-102.39, 72.3) * mm, "end": v(-102.24, 72.01) * mm});
            skLineSegment(sketch, "E1668", {"start": v(-102.24, 72.01) * mm, "end": v(-102.1, 71.73) * mm});
            skLineSegment(sketch, "E1669", {"start": v(-102.1, 71.73) * mm, "end": v(-101.95, 71.45) * mm});
            skLineSegment(sketch, "E1670", {"start": v(-101.95, 71.45) * mm, "end": v(-101.8, 71.17) * mm});
            skLineSegment(sketch, "E1671", {"start": v(-101.8, 71.17) * mm, "end": v(-101.66, 70.9) * mm});
            skLineSegment(sketch, "E1672", {"start": v(-101.66, 70.9) * mm, "end": v(-101.51, 70.64) * mm});
            skLineSegment(sketch, "E1673", {"start": v(-101.51, 70.64) * mm, "end": v(-101.37, 70.37) * mm});
            skLineSegment(sketch, "E1674", {"start": v(-101.37, 70.37) * mm, "end": v(-101.22, 70.11) * mm});
            skLineSegment(sketch, "E1675", {"start": v(-101.22, 70.11) * mm, "end": v(-101.07, 69.85) * mm});
            skLineSegment(sketch, "E1676", {"start": v(-101.07, 69.85) * mm, "end": v(-100.93, 69.6) * mm});
            skLineSegment(sketch, "E1677", {"start": v(-100.93, 69.6) * mm, "end": v(-100.79, 69.35) * mm});
            skLineSegment(sketch, "E1678", {"start": v(-100.79, 69.35) * mm, "end": v(-100.64, 69.1) * mm});
            skLineSegment(sketch, "E1679", {"start": v(-100.64, 69.1) * mm, "end": v(-100.5, 68.87) * mm});
            skLineSegment(sketch, "E1680", {"start": v(-100.5, 68.87) * mm, "end": v(-100.35, 68.63) * mm});
            skLineSegment(sketch, "E1681", {"start": v(-100.35, 68.63) * mm, "end": v(-100.2, 68.4) * mm});
            skLineSegment(sketch, "E1682", {"start": v(-100.2, 68.4) * mm, "end": v(-100.07, 68.16) * mm});
            skLineSegment(sketch, "E1683", {"start": v(-100.07, 68.16) * mm, "end": v(-99.92, 67.93) * mm});
            skLineSegment(sketch, "E1684", {"start": v(-99.92, 67.93) * mm, "end": v(-99.78, 67.7) * mm});
            skLineSegment(sketch, "E1685", {"start": v(-99.78, 67.7) * mm, "end": v(-99.64, 67.49) * mm});
            skLineSegment(sketch, "E1686", {"start": v(-99.64, 67.49) * mm, "end": v(-99.5, 67.27) * mm});
            skLineSegment(sketch, "E1687", {"start": v(-99.5, 67.27) * mm, "end": v(-99.36, 67.06) * mm});
            skLineSegment(sketch, "E1688", {"start": v(-99.36, 67.06) * mm, "end": v(-99.22, 66.84) * mm});
            skLineSegment(sketch, "E1689", {"start": v(-99.22, 66.84) * mm, "end": v(-99.61, 65.8) * mm});
            skLineSegment(sketch, "E1690", {"start": v(-99.61, 65.8) * mm, "end": v(-100.4, 65.02) * mm});
            skLineSegment(sketch, "E1691", {"start": v(-100.4, 65.02) * mm, "end": v(-100.66, 65.06) * mm});
            skLineSegment(sketch, "E1692", {"start": v(-100.66, 65.06) * mm, "end": v(-100.9, 65.1) * mm});
            skLineSegment(sketch, "E1693", {"start": v(-100.9, 65.1) * mm, "end": v(-101.16, 65.14) * mm});
            skLineSegment(sketch, "E1694", {"start": v(-101.16, 65.14) * mm, "end": v(-101.42, 65.18) * mm});
            skLineSegment(sketch, "E1695", {"start": v(-101.42, 65.18) * mm, "end": v(-101.69, 65.22) * mm});
            skLineSegment(sketch, "E1696", {"start": v(-101.69, 65.22) * mm, "end": v(-101.95, 65.26) * mm});
            skLineSegment(sketch, "E1697", {"start": v(-101.95, 65.26) * mm, "end": v(-102.22, 65.3) * mm});
            skLineSegment(sketch, "E1698", {"start": v(-102.22, 65.3) * mm, "end": v(-102.5, 65.33) * mm});
            skLineSegment(sketch, "E1699", {"start": v(-102.5, 65.33) * mm, "end": v(-102.77, 65.36) * mm});
            skLineSegment(sketch, "E1700", {"start": v(-102.77, 65.36) * mm, "end": v(-103.05, 65.4) * mm});
            skLineSegment(sketch, "E1701", {"start": v(-103.05, 65.4) * mm, "end": v(-103.33, 65.43) * mm});
            skLineSegment(sketch, "E1702", {"start": v(-103.33, 65.43) * mm, "end": v(-103.62, 65.46) * mm});
            skLineSegment(sketch, "E1703", {"start": v(-103.62, 65.46) * mm, "end": v(-103.91, 65.49) * mm});
            skLineSegment(sketch, "E1704", {"start": v(-103.91, 65.49) * mm, "end": v(-104.2, 65.52) * mm});
            skLineSegment(sketch, "E1705", {"start": v(-104.2, 65.52) * mm, "end": v(-104.5, 65.54) * mm});
            skLineSegment(sketch, "E1706", {"start": v(-104.5, 65.54) * mm, "end": v(-104.8, 65.57) * mm});
            skLineSegment(sketch, "E1707", {"start": v(-104.8, 65.57) * mm, "end": v(-105.1, 65.6) * mm});
            skLineSegment(sketch, "E1708", {"start": v(-105.1, 65.6) * mm, "end": v(-105.41, 65.62) * mm});
            skLineSegment(sketch, "E1709", {"start": v(-105.41, 65.62) * mm, "end": v(-105.72, 65.64) * mm});
            skLineSegment(sketch, "E1710", {"start": v(-105.72, 65.64) * mm, "end": v(-106.04, 65.66) * mm});
            skLineSegment(sketch, "E1711", {"start": v(-106.04, 65.66) * mm, "end": v(-106.35, 65.68) * mm});
            skLineSegment(sketch, "E1712", {"start": v(-106.35, 65.68) * mm, "end": v(-106.67, 65.7) * mm});
            skLineSegment(sketch, "E1713", {"start": v(-106.67, 65.7) * mm, "end": v(-107, 65.71) * mm});
            skLineSegment(sketch, "E1714", {"start": v(-107, 65.71) * mm, "end": v(-107.32, 65.72) * mm});
            skLineSegment(sketch, "E1715", {"start": v(-107.32, 65.72) * mm, "end": v(-107.66, 65.74) * mm});
            skLineSegment(sketch, "E1716", {"start": v(-107.66, 65.74) * mm, "end": v(-107.99, 65.75) * mm});
            skLineSegment(sketch, "E1717", {"start": v(-107.99, 65.75) * mm, "end": v(-108.33, 65.76) * mm});
            skLineSegment(sketch, "E1718", {"start": v(-108.33, 65.76) * mm, "end": v(-108.67, 65.76) * mm});
            skLineSegment(sketch, "E1719", {"start": v(-108.67, 65.76) * mm, "end": v(-109.01, 65.77) * mm});
            skLineSegment(sketch, "E1720", {"start": v(-109.01, 65.77) * mm, "end": v(-109.36, 65.77) * mm});
            skLineSegment(sketch, "E1721", {"start": v(-109.36, 65.77) * mm, "end": v(-109.46, 65.62) * mm});
            skLineSegment(sketch, "E1722", {"start": v(-109.46, 65.62) * mm, "end": v(-110.19, 64.37) * mm});
            skLineSegment(sketch, "E1723", {"start": v(-110.19, 64.37) * mm, "end": v(-110.26, 64.21) * mm});
            skLineSegment(sketch, "E1724", {"start": v(-110.26, 64.21) * mm, "end": v(-110.09, 63.91) * mm});
            skLineSegment(sketch, "E1725", {"start": v(-110.09, 63.91) * mm, "end": v(-109.91, 63.62) * mm});
            skLineSegment(sketch, "E1726", {"start": v(-109.91, 63.62) * mm, "end": v(-109.74, 63.32) * mm});
            skLineSegment(sketch, "E1727", {"start": v(-109.74, 63.32) * mm, "end": v(-109.57, 63.04) * mm});
            skLineSegment(sketch, "E1728", {"start": v(-109.57, 63.04) * mm, "end": v(-109.4, 62.75) * mm});
            skLineSegment(sketch, "E1729", {"start": v(-109.4, 62.75) * mm, "end": v(-109.22, 62.47) * mm});
            skLineSegment(sketch, "E1730", {"start": v(-109.22, 62.47) * mm, "end": v(-109.05, 62.2) * mm});
            skLineSegment(sketch, "E1731", {"start": v(-109.05, 62.2) * mm, "end": v(-108.87, 61.92) * mm});
            skLineSegment(sketch, "E1732", {"start": v(-108.87, 61.92) * mm, "end": v(-108.7, 61.65) * mm});
            skLineSegment(sketch, "E1733", {"start": v(-108.7, 61.65) * mm, "end": v(-108.53, 61.38) * mm});
            skLineSegment(sketch, "E1734", {"start": v(-108.53, 61.38) * mm, "end": v(-108.35, 61.12) * mm});
            skLineSegment(sketch, "E1735", {"start": v(-108.35, 61.12) * mm, "end": v(-108.18, 60.86) * mm});
            skLineSegment(sketch, "E1736", {"start": v(-108.18, 60.86) * mm, "end": v(-108, 60.6) * mm});
            skLineSegment(sketch, "E1737", {"start": v(-108, 60.6) * mm, "end": v(-107.84, 60.35) * mm});
            skLineSegment(sketch, "E1738", {"start": v(-107.84, 60.35) * mm, "end": v(-107.67, 60.1) * mm});
            skLineSegment(sketch, "E1739", {"start": v(-107.67, 60.1) * mm, "end": v(-107.5, 59.86) * mm});
            skLineSegment(sketch, "E1740", {"start": v(-107.5, 59.86) * mm, "end": v(-107.33, 59.62) * mm});
            skLineSegment(sketch, "E1741", {"start": v(-107.33, 59.62) * mm, "end": v(-107.16, 59.38) * mm});
            skLineSegment(sketch, "E1742", {"start": v(-107.16, 59.38) * mm, "end": v(-106.99, 59.15) * mm});
            skLineSegment(sketch, "E1743", {"start": v(-106.99, 59.15) * mm, "end": v(-106.82, 58.91) * mm});
            skLineSegment(sketch, "E1744", {"start": v(-106.82, 58.91) * mm, "end": v(-106.65, 58.69) * mm});
            skLineSegment(sketch, "E1745", {"start": v(-106.65, 58.69) * mm, "end": v(-106.49, 58.46) * mm});
            skLineSegment(sketch, "E1746", {"start": v(-106.49, 58.46) * mm, "end": v(-106.32, 58.24) * mm});
            skLineSegment(sketch, "E1747", {"start": v(-106.32, 58.24) * mm, "end": v(-106.16, 58.03) * mm});
            skLineSegment(sketch, "E1748", {"start": v(-106.16, 58.03) * mm, "end": v(-106, 57.82) * mm});
            skLineSegment(sketch, "E1749", {"start": v(-106, 57.82) * mm, "end": v(-105.83, 57.6) * mm});
            skLineSegment(sketch, "E1750", {"start": v(-105.83, 57.6) * mm, "end": v(-105.67, 57.4) * mm});
            skLineSegment(sketch, "E1751", {"start": v(-105.67, 57.4) * mm, "end": v(-105.5, 57.2) * mm});
            skLineSegment(sketch, "E1752", {"start": v(-105.5, 57.2) * mm, "end": v(-105.34, 57) * mm});
            skLineSegment(sketch, "E1753", {"start": v(-105.34, 57) * mm, "end": v(-105.18, 56.8) * mm});
            skLineSegment(sketch, "E1754", {"start": v(-105.18, 56.8) * mm, "end": v(-105.48, 55.73) * mm});
            skLineSegment(sketch, "E1755", {"start": v(-105.48, 55.73) * mm, "end": v(-106.19, 54.87) * mm});
            skLineSegment(sketch, "E1756", {"start": v(-106.19, 54.87) * mm, "end": v(-106.44, 54.89) * mm});
            skLineSegment(sketch, "E1757", {"start": v(-106.44, 54.89) * mm, "end": v(-106.7, 54.9) * mm});
            skLineSegment(sketch, "E1758", {"start": v(-106.7, 54.9) * mm, "end": v(-106.95, 54.92) * mm});
            skLineSegment(sketch, "E1759", {"start": v(-106.95, 54.92) * mm, "end": v(-107.21, 54.93) * mm});
            skLineSegment(sketch, "E1760", {"start": v(-107.21, 54.93) * mm, "end": v(-107.48, 54.94) * mm});
            skLineSegment(sketch, "E1761", {"start": v(-107.48, 54.94) * mm, "end": v(-107.75, 54.95) * mm});
            skLineSegment(sketch, "E1762", {"start": v(-107.75, 54.95) * mm, "end": v(-108.02, 54.96) * mm});
            skLineSegment(sketch, "E1763", {"start": v(-108.02, 54.96) * mm, "end": v(-108.3, 54.97) * mm});
            skLineSegment(sketch, "E1764", {"start": v(-108.3, 54.97) * mm, "end": v(-108.57, 54.98) * mm});
            skLineSegment(sketch, "E1765", {"start": v(-108.57, 54.98) * mm, "end": v(-108.86, 54.99) * mm});
            skLineSegment(sketch, "E1766", {"start": v(-108.86, 54.99) * mm, "end": v(-109.14, 55) * mm});
            skLineSegment(sketch, "E1767", {"start": v(-109.14, 55) * mm, "end": v(-109.43, 55) * mm});
            skLineSegment(sketch, "E1768", {"start": v(-109.43, 55) * mm, "end": v(-109.72, 55) * mm});
            skLineSegment(sketch, "E1769", {"start": v(-109.72, 55) * mm, "end": v(-110.02, 55) * mm});
            skLineSegment(sketch, "E1770", {"start": v(-110.02, 55) * mm, "end": v(-110.31, 55) * mm});
            skLineSegment(sketch, "E1771", {"start": v(-110.31, 55) * mm, "end": v(-110.61, 54.99) * mm});
            skLineSegment(sketch, "E1772", {"start": v(-110.61, 54.99) * mm, "end": v(-110.92, 54.98) * mm});
            skLineSegment(sketch, "E1773", {"start": v(-110.92, 54.98) * mm, "end": v(-111.23, 54.97) * mm});
            skLineSegment(sketch, "E1774", {"start": v(-111.23, 54.97) * mm, "end": v(-111.54, 54.97) * mm});
            skLineSegment(sketch, "E1775", {"start": v(-111.54, 54.97) * mm, "end": v(-111.85, 54.96) * mm});
            skLineSegment(sketch, "E1776", {"start": v(-111.85, 54.96) * mm, "end": v(-112.17, 54.94) * mm});
            skLineSegment(sketch, "E1777", {"start": v(-112.17, 54.94) * mm, "end": v(-112.5, 54.93) * mm});
            skLineSegment(sketch, "E1778", {"start": v(-112.5, 54.93) * mm, "end": v(-112.81, 54.91) * mm});
            skLineSegment(sketch, "E1779", {"start": v(-112.81, 54.91) * mm, "end": v(-113.14, 54.9) * mm});
            skLineSegment(sketch, "E1780", {"start": v(-113.14, 54.9) * mm, "end": v(-113.47, 54.87) * mm});
            skLineSegment(sketch, "E1781", {"start": v(-113.47, 54.87) * mm, "end": v(-113.8, 54.85) * mm});
            skLineSegment(sketch, "E1782", {"start": v(-113.8, 54.85) * mm, "end": v(-114.14, 54.83) * mm});
            skLineSegment(sketch, "E1783", {"start": v(-114.14, 54.83) * mm, "end": v(-114.48, 54.8) * mm});
            skLineSegment(sketch, "E1784", {"start": v(-114.48, 54.8) * mm, "end": v(-114.82, 54.77) * mm});
            skLineSegment(sketch, "E1785", {"start": v(-114.82, 54.77) * mm, "end": v(-115.17, 54.74) * mm});
            skLineSegment(sketch, "E1786", {"start": v(-115.17, 54.74) * mm, "end": v(-115.26, 54.58) * mm});
            skLineSegment(sketch, "E1787", {"start": v(-115.26, 54.58) * mm, "end": v(-115.86, 53.27) * mm});
            skLineSegment(sketch, "E1788", {"start": v(-115.86, 53.27) * mm, "end": v(-115.92, 53.1) * mm});
            skLineSegment(sketch, "E1789", {"start": v(-115.92, 53.1) * mm, "end": v(-115.72, 52.82) * mm});
            skLineSegment(sketch, "E1790", {"start": v(-115.72, 52.82) * mm, "end": v(-115.51, 52.54) * mm});
            skLineSegment(sketch, "E1791", {"start": v(-115.51, 52.54) * mm, "end": v(-115.31, 52.27) * mm});
            skLineSegment(sketch, "E1792", {"start": v(-115.31, 52.27) * mm, "end": v(-115.1, 52) * mm});
            skLineSegment(sketch, "E1793", {"start": v(-115.1, 52) * mm, "end": v(-114.9, 51.73) * mm});
            skLineSegment(sketch, "E1794", {"start": v(-114.9, 51.73) * mm, "end": v(-114.7, 51.47) * mm});
            skLineSegment(sketch, "E1795", {"start": v(-114.7, 51.47) * mm, "end": v(-114.5, 51.2) * mm});
            skLineSegment(sketch, "E1796", {"start": v(-114.5, 51.2) * mm, "end": v(-114.3, 50.95) * mm});
            skLineSegment(sketch, "E1797", {"start": v(-114.3, 50.95) * mm, "end": v(-114.1, 50.7) * mm});
            skLineSegment(sketch, "E1798", {"start": v(-114.1, 50.7) * mm, "end": v(-113.91, 50.45) * mm});
            skLineSegment(sketch, "E1799", {"start": v(-113.91, 50.45) * mm, "end": v(-113.71, 50.2) * mm});
            skLineSegment(sketch, "E1800", {"start": v(-113.71, 50.2) * mm, "end": v(-113.52, 49.97) * mm});
            skLineSegment(sketch, "E1801", {"start": v(-113.52, 49.97) * mm, "end": v(-113.32, 49.73) * mm});
            skLineSegment(sketch, "E1802", {"start": v(-113.32, 49.73) * mm, "end": v(-113.13, 49.5) * mm});
            skLineSegment(sketch, "E1803", {"start": v(-113.13, 49.5) * mm, "end": v(-112.93, 49.26) * mm});
            skLineSegment(sketch, "E1804", {"start": v(-112.93, 49.26) * mm, "end": v(-112.74, 49.04) * mm});
            skLineSegment(sketch, "E1805", {"start": v(-112.74, 49.04) * mm, "end": v(-112.55, 48.82) * mm});
            skLineSegment(sketch, "E1806", {"start": v(-112.55, 48.82) * mm, "end": v(-112.35, 48.6) * mm});
            skLineSegment(sketch, "E1807", {"start": v(-112.35, 48.6) * mm, "end": v(-112.16, 48.38) * mm});
            skLineSegment(sketch, "E1808", {"start": v(-112.16, 48.38) * mm, "end": v(-111.97, 48.17) * mm});
            skLineSegment(sketch, "E1809", {"start": v(-111.97, 48.17) * mm, "end": v(-111.78, 47.96) * mm});
            skLineSegment(sketch, "E1810", {"start": v(-111.78, 47.96) * mm, "end": v(-111.6, 47.75) * mm});
            skLineSegment(sketch, "E1811", {"start": v(-111.6, 47.75) * mm, "end": v(-111.41, 47.55) * mm});
            skLineSegment(sketch, "E1812", {"start": v(-111.41, 47.55) * mm, "end": v(-111.22, 47.35) * mm});
            skLineSegment(sketch, "E1813", {"start": v(-111.22, 47.35) * mm, "end": v(-111.04, 47.15) * mm});
            skLineSegment(sketch, "E1814", {"start": v(-111.04, 47.15) * mm, "end": v(-110.86, 46.96) * mm});
            skLineSegment(sketch, "E1815", {"start": v(-110.86, 46.96) * mm, "end": v(-110.68, 46.77) * mm});
            skLineSegment(sketch, "E1816", {"start": v(-110.68, 46.77) * mm, "end": v(-110.5, 46.59) * mm});
            skLineSegment(sketch, "E1817", {"start": v(-110.5, 46.59) * mm, "end": v(-110.32, 46.4) * mm});
            skLineSegment(sketch, "E1818", {"start": v(-110.32, 46.4) * mm, "end": v(-110.14, 46.23) * mm});
            skLineSegment(sketch, "E1819", {"start": v(-110.14, 46.23) * mm, "end": v(-110.32, 45.13) * mm});
            skLineSegment(sketch, "E1820", {"start": v(-110.32, 45.13) * mm, "end": v(-110.95, 44.2) * mm});
            skLineSegment(sketch, "E1821", {"start": v(-110.95, 44.2) * mm, "end": v(-111.2, 44.2) * mm});
            skLineSegment(sketch, "E1822", {"start": v(-111.2, 44.2) * mm, "end": v(-111.45, 44.18) * mm});
            skLineSegment(sketch, "E1823", {"start": v(-111.45, 44.18) * mm, "end": v(-111.71, 44.17) * mm});
            skLineSegment(sketch, "E1824", {"start": v(-111.71, 44.17) * mm, "end": v(-111.97, 44.16) * mm});
            skLineSegment(sketch, "E1825", {"start": v(-111.97, 44.16) * mm, "end": v(-112.24, 44.15) * mm});
            skLineSegment(sketch, "E1826", {"start": v(-112.24, 44.15) * mm, "end": v(-112.5, 44.13) * mm});
            skLineSegment(sketch, "E1827", {"start": v(-112.5, 44.13) * mm, "end": v(-112.78, 44.12) * mm});
            skLineSegment(sketch, "E1828", {"start": v(-112.78, 44.12) * mm, "end": v(-113.05, 44.1) * mm});
            skLineSegment(sketch, "E1829", {"start": v(-113.05, 44.1) * mm, "end": v(-113.33, 44.08) * mm});
            skLineSegment(sketch, "E1830", {"start": v(-113.33, 44.08) * mm, "end": v(-113.61, 44.06) * mm});
            skLineSegment(sketch, "E1831", {"start": v(-113.61, 44.06) * mm, "end": v(-113.9, 44.03) * mm});
            skLineSegment(sketch, "E1832", {"start": v(-113.9, 44.03) * mm, "end": v(-114.18, 44) * mm});
            skLineSegment(sketch, "E1833", {"start": v(-114.18, 44) * mm, "end": v(-114.47, 43.98) * mm});
            skLineSegment(sketch, "E1834", {"start": v(-114.47, 43.98) * mm, "end": v(-114.77, 43.95) * mm});
            skLineSegment(sketch, "E1835", {"start": v(-114.77, 43.95) * mm, "end": v(-115.06, 43.92) * mm});
            skLineSegment(sketch, "E1836", {"start": v(-115.06, 43.92) * mm, "end": v(-115.36, 43.89) * mm});
            skLineSegment(sketch, "E1837", {"start": v(-115.36, 43.89) * mm, "end": v(-115.67, 43.85) * mm});
            skLineSegment(sketch, "E1838", {"start": v(-115.67, 43.85) * mm, "end": v(-115.97, 43.81) * mm});
            skLineSegment(sketch, "E1839", {"start": v(-115.97, 43.81) * mm, "end": v(-116.28, 43.77) * mm});
            skLineSegment(sketch, "E1840", {"start": v(-116.28, 43.77) * mm, "end": v(-116.6, 43.73) * mm});
            skLineSegment(sketch, "E1841", {"start": v(-116.6, 43.73) * mm, "end": v(-116.9, 43.69) * mm});
            skLineSegment(sketch, "E1842", {"start": v(-116.9, 43.69) * mm, "end": v(-117.22, 43.64) * mm});
            skLineSegment(sketch, "E1843", {"start": v(-117.22, 43.64) * mm, "end": v(-117.55, 43.6) * mm});
            skLineSegment(sketch, "E1844", {"start": v(-117.55, 43.6) * mm, "end": v(-117.87, 43.54) * mm});
            skLineSegment(sketch, "E1845", {"start": v(-117.87, 43.54) * mm, "end": v(-118.2, 43.5) * mm});
            skLineSegment(sketch, "E1846", {"start": v(-118.2, 43.5) * mm, "end": v(-118.53, 43.44) * mm});
            skLineSegment(sketch, "E1847", {"start": v(-118.53, 43.44) * mm, "end": v(-118.86, 43.38) * mm});
            skLineSegment(sketch, "E1848", {"start": v(-118.86, 43.38) * mm, "end": v(-119.2, 43.32) * mm});
            skLineSegment(sketch, "E1849", {"start": v(-119.2, 43.32) * mm, "end": v(-119.53, 43.26) * mm});
            skLineSegment(sketch, "E1850", {"start": v(-119.53, 43.26) * mm, "end": v(-119.87, 43.2) * mm});
            skLineSegment(sketch, "E1851", {"start": v(-119.87, 43.2) * mm, "end": v(-119.94, 43.03) * mm});
            skLineSegment(sketch, "E1852", {"start": v(-119.94, 43.03) * mm, "end": v(-120.41, 41.66) * mm});
            skLineSegment(sketch, "E1853", {"start": v(-120.41, 41.66) * mm, "end": v(-120.46, 41.49) * mm});
            skLineSegment(sketch, "E1854", {"start": v(-120.46, 41.49) * mm, "end": v(-120.23, 41.23) * mm});
            skLineSegment(sketch, "E1855", {"start": v(-120.23, 41.23) * mm, "end": v(-120, 40.97) * mm});
            skLineSegment(sketch, "E1856", {"start": v(-120, 40.97) * mm, "end": v(-119.77, 40.72) * mm});
            skLineSegment(sketch, "E1857", {"start": v(-119.77, 40.72) * mm, "end": v(-119.54, 40.47) * mm});
            skLineSegment(sketch, "E1858", {"start": v(-119.54, 40.47) * mm, "end": v(-119.32, 40.22) * mm});
            skLineSegment(sketch, "E1859", {"start": v(-119.32, 40.22) * mm, "end": v(-119.1, 39.98) * mm});
            skLineSegment(sketch, "E1860", {"start": v(-119.1, 39.98) * mm, "end": v(-118.87, 39.74) * mm});
            skLineSegment(sketch, "E1861", {"start": v(-118.87, 39.74) * mm, "end": v(-118.64, 39.5) * mm});
            skLineSegment(sketch, "E1862", {"start": v(-118.64, 39.5) * mm, "end": v(-118.42, 39.28) * mm});
            skLineSegment(sketch, "E1863", {"start": v(-118.42, 39.28) * mm, "end": v(-118.2, 39.05) * mm});
            skLineSegment(sketch, "E1864", {"start": v(-118.2, 39.05) * mm, "end": v(-117.98, 38.83) * mm});
            skLineSegment(sketch, "E1865", {"start": v(-117.98, 38.83) * mm, "end": v(-117.76, 38.6) * mm});
            skLineSegment(sketch, "E1866", {"start": v(-117.76, 38.6) * mm, "end": v(-117.54, 38.39) * mm});
            skLineSegment(sketch, "E1867", {"start": v(-117.54, 38.39) * mm, "end": v(-117.32, 38.17) * mm});
            skLineSegment(sketch, "E1868", {"start": v(-117.32, 38.17) * mm, "end": v(-117.1, 37.96) * mm});
            skLineSegment(sketch, "E1869", {"start": v(-117.1, 37.96) * mm, "end": v(-116.9, 37.76) * mm});
            skLineSegment(sketch, "E1870", {"start": v(-116.9, 37.76) * mm, "end": v(-116.68, 37.55) * mm});
            skLineSegment(sketch, "E1871", {"start": v(-116.68, 37.55) * mm, "end": v(-116.47, 37.35) * mm});
            skLineSegment(sketch, "E1872", {"start": v(-116.47, 37.35) * mm, "end": v(-116.26, 37.16) * mm});
            skLineSegment(sketch, "E1873", {"start": v(-116.26, 37.16) * mm, "end": v(-116.05, 36.96) * mm});
            skLineSegment(sketch, "E1874", {"start": v(-116.05, 36.96) * mm, "end": v(-115.84, 36.77) * mm});
            skLineSegment(sketch, "E1875", {"start": v(-115.84, 36.77) * mm, "end": v(-115.63, 36.59) * mm});
            skLineSegment(sketch, "E1876", {"start": v(-115.63, 36.59) * mm, "end": v(-115.43, 36.4) * mm});
            skLineSegment(sketch, "E1877", {"start": v(-115.43, 36.4) * mm, "end": v(-115.22, 36.22) * mm});
            skLineSegment(sketch, "E1878", {"start": v(-115.22, 36.22) * mm, "end": v(-115.02, 36.05) * mm});
            skLineSegment(sketch, "E1879", {"start": v(-115.02, 36.05) * mm, "end": v(-114.82, 35.87) * mm});
            skLineSegment(sketch, "E1880", {"start": v(-114.82, 35.87) * mm, "end": v(-114.62, 35.7) * mm});
            skLineSegment(sketch, "E1881", {"start": v(-114.62, 35.7) * mm, "end": v(-114.42, 35.54) * mm});
            skLineSegment(sketch, "E1882", {"start": v(-114.42, 35.54) * mm, "end": v(-114.22, 35.37) * mm});
            skLineSegment(sketch, "E1883", {"start": v(-114.22, 35.37) * mm, "end": v(-114.03, 35.21) * mm});
            skLineSegment(sketch, "E1884", {"start": v(-114.03, 35.21) * mm, "end": v(-114.1, 34.1) * mm});
            skLineSegment(sketch, "E1885", {"start": v(-114.1, 34.1) * mm, "end": v(-114.63, 33.12) * mm});
            skLineSegment(sketch, "E1886", {"start": v(-114.63, 33.12) * mm, "end": v(-114.89, 33.09) * mm});
            skLineSegment(sketch, "E1887", {"start": v(-114.89, 33.09) * mm, "end": v(-115.14, 33.05) * mm});
            skLineSegment(sketch, "E1888", {"start": v(-115.14, 33.05) * mm, "end": v(-115.4, 33.02) * mm});
            skLineSegment(sketch, "E1889", {"start": v(-115.4, 33.02) * mm, "end": v(-115.66, 32.98) * mm});
            skLineSegment(sketch, "E1890", {"start": v(-115.66, 32.98) * mm, "end": v(-115.92, 32.94) * mm});
            skLineSegment(sketch, "E1891", {"start": v(-115.92, 32.94) * mm, "end": v(-116.18, 32.9) * mm});
            skLineSegment(sketch, "E1892", {"start": v(-116.18, 32.9) * mm, "end": v(-116.45, 32.86) * mm});
            skLineSegment(sketch, "E1893", {"start": v(-116.45, 32.86) * mm, "end": v(-116.72, 32.81) * mm});
            skLineSegment(sketch, "E1894", {"start": v(-116.72, 32.81) * mm, "end": v(-117, 32.76) * mm});
            skLineSegment(sketch, "E1895", {"start": v(-117, 32.76) * mm, "end": v(-117.28, 32.71) * mm});
            skLineSegment(sketch, "E1896", {"start": v(-117.28, 32.71) * mm, "end": v(-117.56, 32.66) * mm});
            skLineSegment(sketch, "E1897", {"start": v(-117.56, 32.66) * mm, "end": v(-117.84, 32.6) * mm});
            skLineSegment(sketch, "E1898", {"start": v(-117.84, 32.6) * mm, "end": v(-118.12, 32.55) * mm});
            skLineSegment(sketch, "E1899", {"start": v(-118.12, 32.55) * mm, "end": v(-118.41, 32.5) * mm});
            skLineSegment(sketch, "E1900", {"start": v(-118.41, 32.5) * mm, "end": v(-118.7, 32.44) * mm});
            skLineSegment(sketch, "E1901", {"start": v(-118.7, 32.44) * mm, "end": v(-119, 32.37) * mm});
            skLineSegment(sketch, "E1902", {"start": v(-119, 32.37) * mm, "end": v(-119.3, 32.3) * mm});
            skLineSegment(sketch, "E1903", {"start": v(-119.3, 32.3) * mm, "end": v(-119.6, 32.24) * mm});
            skLineSegment(sketch, "E1904", {"start": v(-119.6, 32.24) * mm, "end": v(-119.9, 32.17) * mm});
            skLineSegment(sketch, "E1905", {"start": v(-119.9, 32.17) * mm, "end": v(-120.2, 32.1) * mm});
            skLineSegment(sketch, "E1906", {"start": v(-120.2, 32.1) * mm, "end": v(-120.52, 32.02) * mm});
            skLineSegment(sketch, "E1907", {"start": v(-120.52, 32.02) * mm, "end": v(-120.83, 31.95) * mm});
            skLineSegment(sketch, "E1908", {"start": v(-120.83, 31.95) * mm, "end": v(-121.14, 31.87) * mm});
            skLineSegment(sketch, "E1909", {"start": v(-121.14, 31.87) * mm, "end": v(-121.46, 31.79) * mm});
            skLineSegment(sketch, "E1910", {"start": v(-121.46, 31.79) * mm, "end": v(-121.78, 31.7) * mm});
            skLineSegment(sketch, "E1911", {"start": v(-121.78, 31.7) * mm, "end": v(-122.1, 31.62) * mm});
            skLineSegment(sketch, "E1912", {"start": v(-122.1, 31.62) * mm, "end": v(-122.43, 31.53) * mm});
            skLineSegment(sketch, "E1913", {"start": v(-122.43, 31.53) * mm, "end": v(-122.76, 31.43) * mm});
            skLineSegment(sketch, "E1914", {"start": v(-122.76, 31.43) * mm, "end": v(-123.09, 31.34) * mm});
            skLineSegment(sketch, "E1915", {"start": v(-123.09, 31.34) * mm, "end": v(-123.42, 31.24) * mm});
            skLineSegment(sketch, "E1916", {"start": v(-123.42, 31.24) * mm, "end": v(-123.47, 31.07) * mm});
            skLineSegment(sketch, "E1917", {"start": v(-123.47, 31.07) * mm, "end": v(-123.8, 29.66) * mm});
            skLineSegment(sketch, "E1918", {"start": v(-123.8, 29.66) * mm, "end": v(-123.84, 29.49) * mm});
            skLineSegment(sketch, "E1919", {"start": v(-123.84, 29.49) * mm, "end": v(-123.58, 29.25) * mm});
            skLineSegment(sketch, "E1920", {"start": v(-123.58, 29.25) * mm, "end": v(-123.33, 29.02) * mm});
            skLineSegment(sketch, "E1921", {"start": v(-123.33, 29.02) * mm, "end": v(-123.08, 28.79) * mm});
            skLineSegment(sketch, "E1922", {"start": v(-123.08, 28.79) * mm, "end": v(-122.83, 28.56) * mm});
            skLineSegment(sketch, "E1923", {"start": v(-122.83, 28.56) * mm, "end": v(-122.58, 28.34) * mm});
            skLineSegment(sketch, "E1924", {"start": v(-122.58, 28.34) * mm, "end": v(-122.33, 28.12) * mm});
            skLineSegment(sketch, "E1925", {"start": v(-122.33, 28.12) * mm, "end": v(-122.08, 27.9) * mm});
            skLineSegment(sketch, "E1926", {"start": v(-122.08, 27.9) * mm, "end": v(-121.84, 27.7) * mm});
            skLineSegment(sketch, "E1927", {"start": v(-121.84, 27.7) * mm, "end": v(-121.6, 27.49) * mm});
            skLineSegment(sketch, "E1928", {"start": v(-121.6, 27.49) * mm, "end": v(-121.35, 27.28) * mm});
            skLineSegment(sketch, "E1929", {"start": v(-121.35, 27.28) * mm, "end": v(-121.1, 27.08) * mm});
            skLineSegment(sketch, "E1930", {"start": v(-121.1, 27.08) * mm, "end": v(-120.87, 26.88) * mm});
            skLineSegment(sketch, "E1931", {"start": v(-120.87, 26.88) * mm, "end": v(-120.63, 26.69) * mm});
            skLineSegment(sketch, "E1932", {"start": v(-120.63, 26.69) * mm, "end": v(-120.4, 26.5) * mm});
            skLineSegment(sketch, "E1933", {"start": v(-120.4, 26.5) * mm, "end": v(-120.16, 26.3) * mm});
            skLineSegment(sketch, "E1934", {"start": v(-120.16, 26.3) * mm, "end": v(-119.92, 26.12) * mm});
            skLineSegment(sketch, "E1935", {"start": v(-119.92, 26.12) * mm, "end": v(-119.69, 25.94) * mm});
            skLineSegment(sketch, "E1936", {"start": v(-119.69, 25.94) * mm, "end": v(-119.46, 25.76) * mm});
            skLineSegment(sketch, "E1937", {"start": v(-119.46, 25.76) * mm, "end": v(-119.23, 25.59) * mm});
            skLineSegment(sketch, "E1938", {"start": v(-119.23, 25.59) * mm, "end": v(-119, 25.42) * mm});
            skLineSegment(sketch, "E1939", {"start": v(-119, 25.42) * mm, "end": v(-118.78, 25.25) * mm});
            skLineSegment(sketch, "E1940", {"start": v(-118.78, 25.25) * mm, "end": v(-118.55, 25.08) * mm});
            skLineSegment(sketch, "E1941", {"start": v(-118.55, 25.08) * mm, "end": v(-118.33, 24.92) * mm});
            skLineSegment(sketch, "E1942", {"start": v(-118.33, 24.92) * mm, "end": v(-118.1, 24.76) * mm});
            skLineSegment(sketch, "E1943", {"start": v(-118.1, 24.76) * mm, "end": v(-117.89, 24.6) * mm});
            skLineSegment(sketch, "E1944", {"start": v(-117.89, 24.6) * mm, "end": v(-117.67, 24.45) * mm});
            skLineSegment(sketch, "E1945", {"start": v(-117.67, 24.45) * mm, "end": v(-117.46, 24.3) * mm});
            skLineSegment(sketch, "E1946", {"start": v(-117.46, 24.3) * mm, "end": v(-117.24, 24.16) * mm});
            skLineSegment(sketch, "E1947", {"start": v(-117.24, 24.16) * mm, "end": v(-117.03, 24.01) * mm});
            skLineSegment(sketch, "E1948", {"start": v(-117.03, 24.01) * mm, "end": v(-116.82, 23.87) * mm});
            skLineSegment(sketch, "E1949", {"start": v(-116.82, 23.87) * mm, "end": v(-116.8, 22.76) * mm});
            skLineSegment(sketch, "E1950", {"start": v(-116.8, 22.76) * mm, "end": v(-117.22, 21.73) * mm});
            skLineSegment(sketch, "E1951", {"start": v(-117.22, 21.73) * mm, "end": v(-117.47, 21.67) * mm});
            skLineSegment(sketch, "E1952", {"start": v(-117.47, 21.67) * mm, "end": v(-117.72, 21.61) * mm});
            skLineSegment(sketch, "E1953", {"start": v(-117.72, 21.61) * mm, "end": v(-117.97, 21.55) * mm});
            skLineSegment(sketch, "E1954", {"start": v(-117.97, 21.55) * mm, "end": v(-118.22, 21.5) * mm});
            skLineSegment(sketch, "E1955", {"start": v(-118.22, 21.5) * mm, "end": v(-118.48, 21.43) * mm});
            skLineSegment(sketch, "E1956", {"start": v(-118.48, 21.43) * mm, "end": v(-118.74, 21.36) * mm});
            skLineSegment(sketch, "E1957", {"start": v(-118.74, 21.36) * mm, "end": v(-119, 21.29) * mm});
            skLineSegment(sketch, "E1958", {"start": v(-119, 21.29) * mm, "end": v(-119.27, 21.22) * mm});
            skLineSegment(sketch, "E1959", {"start": v(-119.27, 21.22) * mm, "end": v(-119.54, 21.14) * mm});
            skLineSegment(sketch, "E1960", {"start": v(-119.54, 21.14) * mm, "end": v(-119.8, 21.07) * mm});
            skLineSegment(sketch, "E1961", {"start": v(-119.8, 21.07) * mm, "end": v(-120.08, 20.99) * mm});
            skLineSegment(sketch, "E1962", {"start": v(-120.08, 20.99) * mm, "end": v(-120.36, 20.9) * mm});
            skLineSegment(sketch, "E1963", {"start": v(-120.36, 20.9) * mm, "end": v(-120.64, 20.82) * mm});
            skLineSegment(sketch, "E1964", {"start": v(-120.64, 20.82) * mm, "end": v(-120.92, 20.74) * mm});
            skLineSegment(sketch, "E1965", {"start": v(-120.92, 20.74) * mm, "end": v(-121.2, 20.65) * mm});
            skLineSegment(sketch, "E1966", {"start": v(-121.2, 20.65) * mm, "end": v(-121.5, 20.56) * mm});
            skLineSegment(sketch, "E1967", {"start": v(-121.5, 20.56) * mm, "end": v(-121.78, 20.46) * mm});
            skLineSegment(sketch, "E1968", {"start": v(-121.78, 20.46) * mm, "end": v(-122.08, 20.37) * mm});
            skLineSegment(sketch, "E1969", {"start": v(-122.08, 20.37) * mm, "end": v(-122.37, 20.27) * mm});
            skLineSegment(sketch, "E1970", {"start": v(-122.37, 20.27) * mm, "end": v(-122.67, 20.17) * mm});
            skLineSegment(sketch, "E1971", {"start": v(-122.67, 20.17) * mm, "end": v(-122.97, 20.06) * mm});
            skLineSegment(sketch, "E1972", {"start": v(-122.97, 20.06) * mm, "end": v(-123.27, 19.96) * mm});
            skLineSegment(sketch, "E1973", {"start": v(-123.27, 19.96) * mm, "end": v(-123.58, 19.85) * mm});
            skLineSegment(sketch, "E1974", {"start": v(-123.58, 19.85) * mm, "end": v(-123.88, 19.73) * mm});
            skLineSegment(sketch, "E1975", {"start": v(-123.88, 19.73) * mm, "end": v(-124.2, 19.62) * mm});
            skLineSegment(sketch, "E1976", {"start": v(-124.2, 19.62) * mm, "end": v(-124.5, 19.5) * mm});
            skLineSegment(sketch, "E1977", {"start": v(-124.5, 19.5) * mm, "end": v(-124.82, 19.38) * mm});
            skLineSegment(sketch, "E1978", {"start": v(-124.82, 19.38) * mm, "end": v(-125.14, 19.26) * mm});
            skLineSegment(sketch, "E1979", {"start": v(-125.14, 19.26) * mm, "end": v(-125.46, 19.13) * mm});
            skLineSegment(sketch, "E1980", {"start": v(-125.46, 19.13) * mm, "end": v(-125.78, 19) * mm});
            skLineSegment(sketch, "E1981", {"start": v(-125.78, 19) * mm, "end": v(-125.82, 18.82) * mm});
            skLineSegment(sketch, "E1982", {"start": v(-125.82, 18.82) * mm, "end": v(-126.01, 17.4) * mm});
            skLineSegment(sketch, "E1983", {"start": v(-126.01, 17.4) * mm, "end": v(-126.02, 17.21) * mm});
            skLineSegment(sketch, "E1984", {"start": v(-126.02, 17.21) * mm, "end": v(-125.74, 17) * mm});
            skLineSegment(sketch, "E1985", {"start": v(-125.74, 17) * mm, "end": v(-125.47, 16.8) * mm});
            skLineSegment(sketch, "E1986", {"start": v(-125.47, 16.8) * mm, "end": v(-125.2, 16.6) * mm});
            skLineSegment(sketch, "E1987", {"start": v(-125.2, 16.6) * mm, "end": v(-124.93, 16.4) * mm});
            skLineSegment(sketch, "E1988", {"start": v(-124.93, 16.4) * mm, "end": v(-124.66, 16.2) * mm});
            skLineSegment(sketch, "E1989", {"start": v(-124.66, 16.2) * mm, "end": v(-124.39, 16) * mm});
            skLineSegment(sketch, "E1990", {"start": v(-124.39, 16) * mm, "end": v(-124.12, 15.81) * mm});
            skLineSegment(sketch, "E1991", {"start": v(-124.12, 15.81) * mm, "end": v(-123.86, 15.63) * mm});
            skLineSegment(sketch, "E1992", {"start": v(-123.86, 15.63) * mm, "end": v(-123.6, 15.44) * mm});
            skLineSegment(sketch, "E1993", {"start": v(-123.6, 15.44) * mm, "end": v(-123.33, 15.26) * mm});
            skLineSegment(sketch, "E1994", {"start": v(-123.33, 15.26) * mm, "end": v(-123.07, 15.08) * mm});
            skLineSegment(sketch, "E1995", {"start": v(-123.07, 15.08) * mm, "end": v(-122.81, 14.91) * mm});
            skLineSegment(sketch, "E1996", {"start": v(-122.81, 14.91) * mm, "end": v(-122.56, 14.74) * mm});
            skLineSegment(sketch, "E1997", {"start": v(-122.56, 14.74) * mm, "end": v(-122.3, 14.57) * mm});
            skLineSegment(sketch, "E1998", {"start": v(-122.3, 14.57) * mm, "end": v(-122.05, 14.4) * mm});
            skLineSegment(sketch, "E1999", {"start": v(-122.05, 14.4) * mm, "end": v(-121.8, 14.25) * mm});
            skLineSegment(sketch, "E2000", {"start": v(-121.8, 14.25) * mm, "end": v(-121.55, 14.1) * mm});
            skLineSegment(sketch, "E2001", {"start": v(-121.55, 14.1) * mm, "end": v(-121.3, 13.94) * mm});
            skLineSegment(sketch, "E2002", {"start": v(-121.3, 13.94) * mm, "end": v(-121.06, 13.78) * mm});
            skLineSegment(sketch, "E2003", {"start": v(-121.06, 13.78) * mm, "end": v(-120.81, 13.63) * mm});
            skLineSegment(sketch, "E2004", {"start": v(-120.81, 13.63) * mm, "end": v(-120.57, 13.49) * mm});
            skLineSegment(sketch, "E2005", {"start": v(-120.57, 13.49) * mm, "end": v(-120.33, 13.35) * mm});
            skLineSegment(sketch, "E2006", {"start": v(-120.33, 13.35) * mm, "end": v(-120.1, 13.2) * mm});
            skLineSegment(sketch, "E2007", {"start": v(-120.1, 13.2) * mm, "end": v(-119.86, 13.07) * mm});
            skLineSegment(sketch, "E2008", {"start": v(-119.86, 13.07) * mm, "end": v(-119.63, 12.94) * mm});
            skLineSegment(sketch, "E2009", {"start": v(-119.63, 12.94) * mm, "end": v(-119.4, 12.8) * mm});
            skLineSegment(sketch, "E2010", {"start": v(-119.4, 12.8) * mm, "end": v(-119.17, 12.68) * mm});
            skLineSegment(sketch, "E2011", {"start": v(-119.17, 12.68) * mm, "end": v(-118.94, 12.55) * mm});
            skLineSegment(sketch, "E2012", {"start": v(-118.94, 12.55) * mm, "end": v(-118.71, 12.43) * mm});
            skLineSegment(sketch, "E2013", {"start": v(-118.71, 12.43) * mm, "end": v(-118.5, 12.31) * mm});
            skLineSegment(sketch, "E2014", {"start": v(-118.5, 12.31) * mm, "end": v(-118.35, 11.2) * mm});
            skLineSegment(sketch, "E2015", {"start": v(-118.35, 11.2) * mm, "end": v(-118.68, 10.14) * mm});
            skLineSegment(sketch, "E2016", {"start": v(-118.68, 10.14) * mm, "end": v(-118.92, 10.06) * mm});
            skLineSegment(sketch, "E2017", {"start": v(-118.92, 10.06) * mm, "end": v(-119.16, 9.98) * mm});
            skLineSegment(sketch, "E2018", {"start": v(-119.16, 9.98) * mm, "end": v(-119.4, 9.9) * mm});
            skLineSegment(sketch, "E2019", {"start": v(-119.4, 9.9) * mm, "end": v(-119.65, 9.8) * mm});
            skLineSegment(sketch, "E2020", {"start": v(-119.65, 9.8) * mm, "end": v(-119.9, 9.71) * mm});
            skLineSegment(sketch, "E2021", {"start": v(-119.9, 9.71) * mm, "end": v(-120.15, 9.62) * mm});
            skLineSegment(sketch, "E2022", {"start": v(-120.15, 9.62) * mm, "end": v(-120.4, 9.53) * mm});
            skLineSegment(sketch, "E2023", {"start": v(-120.4, 9.53) * mm, "end": v(-120.67, 9.43) * mm});
            skLineSegment(sketch, "E2024", {"start": v(-120.67, 9.43) * mm, "end": v(-120.93, 9.33) * mm});
            skLineSegment(sketch, "E2025", {"start": v(-120.93, 9.33) * mm, "end": v(-121.19, 9.23) * mm});
            skLineSegment(sketch, "E2026", {"start": v(-121.19, 9.23) * mm, "end": v(-121.45, 9.12) * mm});
            skLineSegment(sketch, "E2027", {"start": v(-121.45, 9.12) * mm, "end": v(-121.72, 9.01) * mm});
            skLineSegment(sketch, "E2028", {"start": v(-121.72, 9.01) * mm, "end": v(-122, 8.9) * mm});
            skLineSegment(sketch, "E2029", {"start": v(-122, 8.9) * mm, "end": v(-122.26, 8.8) * mm});
            skLineSegment(sketch, "E2030", {"start": v(-122.26, 8.8) * mm, "end": v(-122.54, 8.67) * mm});
            skLineSegment(sketch, "E2031", {"start": v(-122.54, 8.67) * mm, "end": v(-122.81, 8.56) * mm});
            skLineSegment(sketch, "E2032", {"start": v(-122.81, 8.56) * mm, "end": v(-123.1, 8.43) * mm});
            skLineSegment(sketch, "E2033", {"start": v(-123.1, 8.43) * mm, "end": v(-123.38, 8.3) * mm});
            skLineSegment(sketch, "E2034", {"start": v(-123.38, 8.3) * mm, "end": v(-123.66, 8.18) * mm});
            skLineSegment(sketch, "E2035", {"start": v(-123.66, 8.18) * mm, "end": v(-123.95, 8.05) * mm});
            skLineSegment(sketch, "E2036", {"start": v(-123.95, 8.05) * mm, "end": v(-124.23, 7.92) * mm});
            skLineSegment(sketch, "E2037", {"start": v(-124.23, 7.92) * mm, "end": v(-124.53, 7.78) * mm});
            skLineSegment(sketch, "E2038", {"start": v(-124.53, 7.78) * mm, "end": v(-124.82, 7.64) * mm});
            skLineSegment(sketch, "E2039", {"start": v(-124.82, 7.64) * mm, "end": v(-125.11, 7.5) * mm});
            skLineSegment(sketch, "E2040", {"start": v(-125.11, 7.5) * mm, "end": v(-125.4, 7.36) * mm});
            skLineSegment(sketch, "E2041", {"start": v(-125.4, 7.36) * mm, "end": v(-125.7, 7.2) * mm});
            skLineSegment(sketch, "E2042", {"start": v(-125.7, 7.2) * mm, "end": v(-126.01, 7.06) * mm});
            skLineSegment(sketch, "E2043", {"start": v(-126.01, 7.06) * mm, "end": v(-126.31, 6.9) * mm});
            skLineSegment(sketch, "E2044", {"start": v(-126.31, 6.9) * mm, "end": v(-126.62, 6.74) * mm});
            skLineSegment(sketch, "E2045", {"start": v(-126.62, 6.74) * mm, "end": v(-126.93, 6.58) * mm});
            skLineSegment(sketch, "E2046", {"start": v(-126.93, 6.58) * mm, "end": v(-126.95, 6.4) * mm});
            skLineSegment(sketch, "E2047", {"start": v(-126.95, 6.4) * mm, "end": v(-127, 4.96) * mm});
            skLineSegment(sketch, "E2048", {"start": v(-127, 4.96) * mm, "end": v(-127, 4.78) * mm});
            skLineSegment(sketch, "E2049", {"start": v(-127, 4.78) * mm, "end": v(-126.7, 4.6) * mm});
            skLineSegment(sketch, "E2050", {"start": v(-126.7, 4.6) * mm, "end": v(-126.4, 4.42) * mm});
            skLineSegment(sketch, "E2051", {"start": v(-126.4, 4.42) * mm, "end": v(-126.11, 4.25) * mm});
            skLineSegment(sketch, "E2052", {"start": v(-126.11, 4.25) * mm, "end": v(-125.82, 4.07) * mm});
            skLineSegment(sketch, "E2053", {"start": v(-125.82, 4.07) * mm, "end": v(-125.53, 3.9) * mm});
            skLineSegment(sketch, "E2054", {"start": v(-125.53, 3.9) * mm, "end": v(-125.25, 3.74) * mm});
            skLineSegment(sketch, "E2055", {"start": v(-125.25, 3.74) * mm, "end": v(-124.96, 3.57) * mm});
            skLineSegment(sketch, "E2056", {"start": v(-124.96, 3.57) * mm, "end": v(-124.68, 3.41) * mm});
            skLineSegment(sketch, "E2057", {"start": v(-124.68, 3.41) * mm, "end": v(-124.4, 3.26) * mm});
            skLineSegment(sketch, "E2058", {"start": v(-124.4, 3.26) * mm, "end": v(-124.12, 3.1) * mm});
            skLineSegment(sketch, "E2059", {"start": v(-124.12, 3.1) * mm, "end": v(-123.85, 2.95) * mm});
            skLineSegment(sketch, "E2060", {"start": v(-123.85, 2.95) * mm, "end": v(-123.57, 2.8) * mm});
            skLineSegment(sketch, "E2061", {"start": v(-123.57, 2.8) * mm, "end": v(-123.3, 2.66) * mm});
            skLineSegment(sketch, "E2062", {"start": v(-123.3, 2.66) * mm, "end": v(-123.03, 2.52) * mm});
            skLineSegment(sketch, "E2063", {"start": v(-123.03, 2.52) * mm, "end": v(-122.76, 2.38) * mm});
            skLineSegment(sketch, "E2064", {"start": v(-122.76, 2.38) * mm, "end": v(-122.5, 2.25) * mm});
            skLineSegment(sketch, "E2065", {"start": v(-122.5, 2.25) * mm, "end": v(-122.24, 2.11) * mm});
            skLineSegment(sketch, "E2066", {"start": v(-122.24, 2.11) * mm, "end": v(-121.97, 1.98) * mm});
            skLineSegment(sketch, "E2067", {"start": v(-121.97, 1.98) * mm, "end": v(-121.72, 1.86) * mm});
            skLineSegment(sketch, "E2068", {"start": v(-121.72, 1.86) * mm, "end": v(-121.46, 1.73) * mm});
            skLineSegment(sketch, "E2069", {"start": v(-121.46, 1.73) * mm, "end": v(-121.2, 1.61) * mm});
            skLineSegment(sketch, "E2070", {"start": v(-121.2, 1.61) * mm, "end": v(-120.95, 1.5) * mm});
            skLineSegment(sketch, "E2071", {"start": v(-120.95, 1.5) * mm, "end": v(-120.7, 1.38) * mm});
            skLineSegment(sketch, "E2072", {"start": v(-120.7, 1.38) * mm, "end": v(-120.45, 1.27) * mm});
            skLineSegment(sketch, "E2073", {"start": v(-120.45, 1.27) * mm, "end": v(-120.2, 1.15) * mm});
            skLineSegment(sketch, "E2074", {"start": v(-120.2, 1.15) * mm, "end": v(-119.97, 1.05) * mm});
            skLineSegment(sketch, "E2075", {"start": v(-119.97, 1.05) * mm, "end": v(-119.73, 0.94) * mm});
            skLineSegment(sketch, "E2076", {"start": v(-119.73, 0.94) * mm, "end": v(-119.49, 0.84) * mm});
            skLineSegment(sketch, "E2077", {"start": v(-119.49, 0.84) * mm, "end": v(-119.25, 0.74) * mm});
            skLineSegment(sketch, "E2078", {"start": v(-119.25, 0.74) * mm, "end": v(-119.02, 0.64) * mm});
            skLineSegment(sketch, "E2079", {"start": v(-119.02, 0.64) * mm, "end": v(-118.77, -0.44) * mm});
            skLineSegment(sketch, "E2080", {"start": v(-118.77, -0.44) * mm, "end": v(-119, -1.54) * mm});
            skLineSegment(sketch, "E2081", {"start": v(-119, -1.54) * mm, "end": v(-119.22, -1.64) * mm});
            skLineSegment(sketch, "E2082", {"start": v(-119.22, -1.64) * mm, "end": v(-119.45, -1.75) * mm});
            skLineSegment(sketch, "E2083", {"start": v(-119.45, -1.75) * mm, "end": v(-119.69, -1.85) * mm});
            skLineSegment(sketch, "E2084", {"start": v(-119.69, -1.85) * mm, "end": v(-119.93, -1.97) * mm});
            skLineSegment(sketch, "E2085", {"start": v(-119.93, -1.97) * mm, "end": v(-120.17, -2.08) * mm});
            skLineSegment(sketch, "E2086", {"start": v(-120.17, -2.08) * mm, "end": v(-120.4, -2.2) * mm});
            skLineSegment(sketch, "E2087", {"start": v(-120.4, -2.2) * mm, "end": v(-120.65, -2.31) * mm});
            skLineSegment(sketch, "E2088", {"start": v(-120.65, -2.31) * mm, "end": v(-120.9, -2.44) * mm});
            skLineSegment(sketch, "E2089", {"start": v(-120.9, -2.44) * mm, "end": v(-121.15, -2.56) * mm});
            skLineSegment(sketch, "E2090", {"start": v(-121.15, -2.56) * mm, "end": v(-121.4, -2.7) * mm});
            skLineSegment(sketch, "E2091", {"start": v(-121.4, -2.7) * mm, "end": v(-121.65, -2.82) * mm});
            skLineSegment(sketch, "E2092", {"start": v(-121.65, -2.82) * mm, "end": v(-121.9, -2.95) * mm});
            skLineSegment(sketch, "E2093", {"start": v(-121.9, -2.95) * mm, "end": v(-122.17, -3.1) * mm});
            skLineSegment(sketch, "E2094", {"start": v(-122.17, -3.1) * mm, "end": v(-122.43, -3.23) * mm});
            skLineSegment(sketch, "E2095", {"start": v(-122.43, -3.23) * mm, "end": v(-122.69, -3.37) * mm});
            skLineSegment(sketch, "E2096", {"start": v(-122.69, -3.37) * mm, "end": v(-122.95, -3.52) * mm});
            skLineSegment(sketch, "E2097", {"start": v(-122.95, -3.52) * mm, "end": v(-123.22, -3.67) * mm});
            skLineSegment(sketch, "E2098", {"start": v(-123.22, -3.67) * mm, "end": v(-123.49, -3.82) * mm});
            skLineSegment(sketch, "E2099", {"start": v(-123.49, -3.82) * mm, "end": v(-123.76, -3.97) * mm});
            skLineSegment(sketch, "E2100", {"start": v(-123.76, -3.97) * mm, "end": v(-124.03, -4.13) * mm});
            skLineSegment(sketch, "E2101", {"start": v(-124.03, -4.13) * mm, "end": v(-124.3, -4.3) * mm});
            skLineSegment(sketch, "E2102", {"start": v(-124.3, -4.3) * mm, "end": v(-124.58, -4.45) * mm});
            skLineSegment(sketch, "E2103", {"start": v(-124.58, -4.45) * mm, "end": v(-124.86, -4.62) * mm});
            skLineSegment(sketch, "E2104", {"start": v(-124.86, -4.62) * mm, "end": v(-125.14, -4.8) * mm});
            skLineSegment(sketch, "E2105", {"start": v(-125.14, -4.8) * mm, "end": v(-125.42, -4.97) * mm});
            skLineSegment(sketch, "E2106", {"start": v(-125.42, -4.97) * mm, "end": v(-125.7, -5.14) * mm});
            skLineSegment(sketch, "E2107", {"start": v(-125.7, -5.14) * mm, "end": v(-125.99, -5.32) * mm});
            skLineSegment(sketch, "E2108", {"start": v(-125.99, -5.32) * mm, "end": v(-126.27, -5.5) * mm});
            skLineSegment(sketch, "E2109", {"start": v(-126.27, -5.5) * mm, "end": v(-126.56, -5.7) * mm});
            skLineSegment(sketch, "E2110", {"start": v(-126.56, -5.7) * mm, "end": v(-126.85, -5.88) * mm});
            skLineSegment(sketch, "E2111", {"start": v(-126.85, -5.88) * mm, "end": v(-126.86, -6.06) * mm});
            skLineSegment(sketch, "E2112", {"start": v(-126.86, -6.06) * mm, "end": v(-126.77, -7.5) * mm});
            skLineSegment(sketch, "E2113", {"start": v(-126.77, -7.5) * mm, "end": v(-126.74, -7.68) * mm});
            skLineSegment(sketch, "E2114", {"start": v(-126.74, -7.68) * mm, "end": v(-126.43, -7.83) * mm});
            skLineSegment(sketch, "E2115", {"start": v(-126.43, -7.83) * mm, "end": v(-126.12, -7.98) * mm});
            skLineSegment(sketch, "E2116", {"start": v(-126.12, -7.98) * mm, "end": v(-125.81, -8.13) * mm});
            skLineSegment(sketch, "E2117", {"start": v(-125.81, -8.13) * mm, "end": v(-125.5, -8.27) * mm});
            skLineSegment(sketch, "E2118", {"start": v(-125.5, -8.27) * mm, "end": v(-125.2, -8.41) * mm});
            skLineSegment(sketch, "E2119", {"start": v(-125.2, -8.41) * mm, "end": v(-124.9, -8.55) * mm});
            skLineSegment(sketch, "E2120", {"start": v(-124.9, -8.55) * mm, "end": v(-124.6, -8.69) * mm});
            skLineSegment(sketch, "E2121", {"start": v(-124.6, -8.69) * mm, "end": v(-124.3, -8.82) * mm});
            skLineSegment(sketch, "E2122", {"start": v(-124.3, -8.82) * mm, "end": v(-124.01, -8.95) * mm});
            skLineSegment(sketch, "E2123", {"start": v(-124.01, -8.95) * mm, "end": v(-123.72, -9.07) * mm});
            skLineSegment(sketch, "E2124", {"start": v(-123.72, -9.07) * mm, "end": v(-123.43, -9.2) * mm});
            skLineSegment(sketch, "E2125", {"start": v(-123.43, -9.2) * mm, "end": v(-123.15, -9.31) * mm});
            skLineSegment(sketch, "E2126", {"start": v(-123.15, -9.31) * mm, "end": v(-122.86, -9.43) * mm});
            skLineSegment(sketch, "E2127", {"start": v(-122.86, -9.43) * mm, "end": v(-122.58, -9.55) * mm});
            skLineSegment(sketch, "E2128", {"start": v(-122.58, -9.55) * mm, "end": v(-122.3, -9.66) * mm});
            skLineSegment(sketch, "E2129", {"start": v(-122.3, -9.66) * mm, "end": v(-122.02, -9.77) * mm});
            skLineSegment(sketch, "E2130", {"start": v(-122.02, -9.77) * mm, "end": v(-121.75, -9.87) * mm});
            skLineSegment(sketch, "E2131", {"start": v(-121.75, -9.87) * mm, "end": v(-121.47, -9.98) * mm});
            skLineSegment(sketch, "E2132", {"start": v(-121.47, -9.98) * mm, "end": v(-121.2, -10.08) * mm});
            skLineSegment(sketch, "E2133", {"start": v(-121.2, -10.08) * mm, "end": v(-120.93, -10.17) * mm});
            skLineSegment(sketch, "E2134", {"start": v(-120.93, -10.17) * mm, "end": v(-120.67, -10.27) * mm});
            skLineSegment(sketch, "E2135", {"start": v(-120.67, -10.27) * mm, "end": v(-120.4, -10.36) * mm});
            skLineSegment(sketch, "E2136", {"start": v(-120.4, -10.36) * mm, "end": v(-120.15, -10.45) * mm});
            skLineSegment(sketch, "E2137", {"start": v(-120.15, -10.45) * mm, "end": v(-119.9, -10.54) * mm});
            skLineSegment(sketch, "E2138", {"start": v(-119.9, -10.54) * mm, "end": v(-119.64, -10.63) * mm});
            skLineSegment(sketch, "E2139", {"start": v(-119.64, -10.63) * mm, "end": v(-119.38, -10.71) * mm});
            skLineSegment(sketch, "E2140", {"start": v(-119.38, -10.71) * mm, "end": v(-119.13, -10.8) * mm});
            skLineSegment(sketch, "E2141", {"start": v(-119.13, -10.8) * mm, "end": v(-118.89, -10.87) * mm});
            skLineSegment(sketch, "E2142", {"start": v(-118.89, -10.87) * mm, "end": v(-118.64, -10.95) * mm});
            skLineSegment(sketch, "E2143", {"start": v(-118.64, -10.95) * mm, "end": v(-118.4, -11.02) * mm});
            skLineSegment(sketch, "E2144", {"start": v(-118.4, -11.02) * mm, "end": v(-118.05, -12.08) * mm});
            skLineSegment(sketch, "E2145", {"start": v(-118.05, -12.08) * mm, "end": v(-118.16, -13.19) * mm});
            skLineSegment(sketch, "E2146", {"start": v(-118.16, -13.19) * mm, "end": v(-118.38, -13.31) * mm});
            skLineSegment(sketch, "E2147", {"start": v(-118.38, -13.31) * mm, "end": v(-118.6, -13.44) * mm});
            skLineSegment(sketch, "E2148", {"start": v(-118.6, -13.44) * mm, "end": v(-118.82, -13.57) * mm});
            skLineSegment(sketch, "E2149", {"start": v(-118.82, -13.57) * mm, "end": v(-119.05, -13.7) * mm});
            skLineSegment(sketch, "E2150", {"start": v(-119.05, -13.7) * mm, "end": v(-119.28, -13.84) * mm});
            skLineSegment(sketch, "E2151", {"start": v(-119.28, -13.84) * mm, "end": v(-119.5, -13.98) * mm});
            skLineSegment(sketch, "E2152", {"start": v(-119.5, -13.98) * mm, "end": v(-119.74, -14.12) * mm});
            skLineSegment(sketch, "E2153", {"start": v(-119.74, -14.12) * mm, "end": v(-119.97, -14.27) * mm});
            skLineSegment(sketch, "E2154", {"start": v(-119.97, -14.27) * mm, "end": v(-120.2, -14.42) * mm});
            skLineSegment(sketch, "E2155", {"start": v(-120.2, -14.42) * mm, "end": v(-120.44, -14.57) * mm});
            skLineSegment(sketch, "E2156", {"start": v(-120.44, -14.57) * mm, "end": v(-120.68, -14.73) * mm});
            skLineSegment(sketch, "E2157", {"start": v(-120.68, -14.73) * mm, "end": v(-120.92, -14.88) * mm});
            skLineSegment(sketch, "E2158", {"start": v(-120.92, -14.88) * mm, "end": v(-121.17, -15.05) * mm});
            skLineSegment(sketch, "E2159", {"start": v(-121.17, -15.05) * mm, "end": v(-121.41, -15.2) * mm});
            skLineSegment(sketch, "E2160", {"start": v(-121.41, -15.2) * mm, "end": v(-121.66, -15.38) * mm});
            skLineSegment(sketch, "E2161", {"start": v(-121.66, -15.38) * mm, "end": v(-121.9, -15.55) * mm});
            skLineSegment(sketch, "E2162", {"start": v(-121.9, -15.55) * mm, "end": v(-122.16, -15.72) * mm});
            skLineSegment(sketch, "E2163", {"start": v(-122.16, -15.72) * mm, "end": v(-122.4, -15.9) * mm});
            skLineSegment(sketch, "E2164", {"start": v(-122.4, -15.9) * mm, "end": v(-122.66, -16.08) * mm});
            skLineSegment(sketch, "E2165", {"start": v(-122.66, -16.08) * mm, "end": v(-122.92, -16.26) * mm});
            skLineSegment(sketch, "E2166", {"start": v(-122.92, -16.26) * mm, "end": v(-123.18, -16.45) * mm});
            skLineSegment(sketch, "E2167", {"start": v(-123.18, -16.45) * mm, "end": v(-123.43, -16.64) * mm});
            skLineSegment(sketch, "E2168", {"start": v(-123.43, -16.64) * mm, "end": v(-123.7, -16.83) * mm});
            skLineSegment(sketch, "E2169", {"start": v(-123.7, -16.83) * mm, "end": v(-123.96, -17.03) * mm});
            skLineSegment(sketch, "E2170", {"start": v(-123.96, -17.03) * mm, "end": v(-124.22, -17.23) * mm});
            skLineSegment(sketch, "E2171", {"start": v(-124.22, -17.23) * mm, "end": v(-124.48, -17.43) * mm});
            skLineSegment(sketch, "E2172", {"start": v(-124.48, -17.43) * mm, "end": v(-124.75, -17.64) * mm});
            skLineSegment(sketch, "E2173", {"start": v(-124.75, -17.64) * mm, "end": v(-125.02, -17.85) * mm});
            skLineSegment(sketch, "E2174", {"start": v(-125.02, -17.85) * mm, "end": v(-125.29, -18.07) * mm});
            skLineSegment(sketch, "E2175", {"start": v(-125.29, -18.07) * mm, "end": v(-125.56, -18.28) * mm});
            skLineSegment(sketch, "E2176", {"start": v(-125.56, -18.28) * mm, "end": v(-125.54, -18.46) * mm});
            skLineSegment(sketch, "E2177", {"start": v(-125.54, -18.46) * mm, "end": v(-125.31, -19.89) * mm});
            skLineSegment(sketch, "E2178", {"start": v(-125.31, -19.89) * mm, "end": v(-125.27, -20.06) * mm});
            skLineSegment(sketch, "E2179", {"start": v(-125.27, -20.06) * mm, "end": v(-124.94, -20.18) * mm});
            skLineSegment(sketch, "E2180", {"start": v(-124.94, -20.18) * mm, "end": v(-124.62, -20.3) * mm});
            skLineSegment(sketch, "E2181", {"start": v(-124.62, -20.3) * mm, "end": v(-124.3, -20.42) * mm});
            skLineSegment(sketch, "E2182", {"start": v(-124.3, -20.42) * mm, "end": v(-123.98, -20.53) * mm});
            skLineSegment(sketch, "E2183", {"start": v(-123.98, -20.53) * mm, "end": v(-123.67, -20.64) * mm});
            skLineSegment(sketch, "E2184", {"start": v(-123.67, -20.64) * mm, "end": v(-123.35, -20.75) * mm});
            skLineSegment(sketch, "E2185", {"start": v(-123.35, -20.75) * mm, "end": v(-123.04, -20.85) * mm});
            skLineSegment(sketch, "E2186", {"start": v(-123.04, -20.85) * mm, "end": v(-122.74, -20.95) * mm});
            skLineSegment(sketch, "E2187", {"start": v(-122.74, -20.95) * mm, "end": v(-122.43, -21.05) * mm});
            skLineSegment(sketch, "E2188", {"start": v(-122.43, -21.05) * mm, "end": v(-122.13, -21.15) * mm});
            skLineSegment(sketch, "E2189", {"start": v(-122.13, -21.15) * mm, "end": v(-121.83, -21.24) * mm});
            skLineSegment(sketch, "E2190", {"start": v(-121.83, -21.24) * mm, "end": v(-121.53, -21.33) * mm});
            skLineSegment(sketch, "E2191", {"start": v(-121.53, -21.33) * mm, "end": v(-121.24, -21.42) * mm});
            skLineSegment(sketch, "E2192", {"start": v(-121.24, -21.42) * mm, "end": v(-120.94, -21.5) * mm});
            skLineSegment(sketch, "E2193", {"start": v(-120.94, -21.5) * mm, "end": v(-120.65, -21.6) * mm});
            skLineSegment(sketch, "E2194", {"start": v(-120.65, -21.6) * mm, "end": v(-120.37, -21.67) * mm});
            skLineSegment(sketch, "E2195", {"start": v(-120.37, -21.67) * mm, "end": v(-120.08, -21.75) * mm});
            skLineSegment(sketch, "E2196", {"start": v(-120.08, -21.75) * mm, "end": v(-119.8, -21.83) * mm});
            skLineSegment(sketch, "E2197", {"start": v(-119.8, -21.83) * mm, "end": v(-119.52, -21.9) * mm});
            skLineSegment(sketch, "E2198", {"start": v(-119.52, -21.9) * mm, "end": v(-119.25, -21.97) * mm});
            skLineSegment(sketch, "E2199", {"start": v(-119.25, -21.97) * mm, "end": v(-118.97, -22.04) * mm});
            skLineSegment(sketch, "E2200", {"start": v(-118.97, -22.04) * mm, "end": v(-118.7, -22.11) * mm});
            skLineSegment(sketch, "E2201", {"start": v(-118.7, -22.11) * mm, "end": v(-118.44, -22.17) * mm});
            skLineSegment(sketch, "E2202", {"start": v(-118.44, -22.17) * mm, "end": v(-118.17, -22.24) * mm});
            skLineSegment(sketch, "E2203", {"start": v(-118.17, -22.24) * mm, "end": v(-117.9, -22.3) * mm});
            skLineSegment(sketch, "E2204", {"start": v(-117.9, -22.3) * mm, "end": v(-117.65, -22.36) * mm});
            skLineSegment(sketch, "E2205", {"start": v(-117.65, -22.36) * mm, "end": v(-117.4, -22.41) * mm});
            skLineSegment(sketch, "E2206", {"start": v(-117.4, -22.41) * mm, "end": v(-117.14, -22.47) * mm});
            skLineSegment(sketch, "E2207", {"start": v(-117.14, -22.47) * mm, "end": v(-116.9, -22.52) * mm});
            skLineSegment(sketch, "E2208", {"start": v(-116.9, -22.52) * mm, "end": v(-116.64, -22.57) * mm});
            skLineSegment(sketch, "E2209", {"start": v(-116.64, -22.57) * mm, "end": v(-116.19, -23.59) * mm});
            skLineSegment(sketch, "E2210", {"start": v(-116.19, -23.59) * mm, "end": v(-116.2, -24.7) * mm});
            skLineSegment(sketch, "E2211", {"start": v(-116.2, -24.7) * mm, "end": v(-116.4, -24.85) * mm});
            skLineSegment(sketch, "E2212", {"start": v(-116.4, -24.85) * mm, "end": v(-116.6, -25) * mm});
            skLineSegment(sketch, "E2213", {"start": v(-116.6, -25) * mm, "end": v(-116.81, -25.15) * mm});
            skLineSegment(sketch, "E2214", {"start": v(-116.81, -25.15) * mm, "end": v(-117.02, -25.3) * mm});
            skLineSegment(sketch, "E2215", {"start": v(-117.02, -25.3) * mm, "end": v(-117.24, -25.46) * mm});
            skLineSegment(sketch, "E2216", {"start": v(-117.24, -25.46) * mm, "end": v(-117.45, -25.62) * mm});
            skLineSegment(sketch, "E2217", {"start": v(-117.45, -25.62) * mm, "end": v(-117.67, -25.79) * mm});
            skLineSegment(sketch, "E2218", {"start": v(-117.67, -25.79) * mm, "end": v(-117.89, -25.96) * mm});
            skLineSegment(sketch, "E2219", {"start": v(-117.89, -25.96) * mm, "end": v(-118.1, -26.13) * mm});
            skLineSegment(sketch, "E2220", {"start": v(-118.1, -26.13) * mm, "end": v(-118.33, -26.3) * mm});
            skLineSegment(sketch, "E2221", {"start": v(-118.33, -26.3) * mm, "end": v(-118.55, -26.48) * mm});
            skLineSegment(sketch, "E2222", {"start": v(-118.55, -26.48) * mm, "end": v(-118.77, -26.66) * mm});
            skLineSegment(sketch, "E2223", {"start": v(-118.77, -26.66) * mm, "end": v(-119, -26.84) * mm});
            skLineSegment(sketch, "E2224", {"start": v(-119, -26.84) * mm, "end": v(-119.23, -27.03) * mm});
            skLineSegment(sketch, "E2225", {"start": v(-119.23, -27.03) * mm, "end": v(-119.46, -27.22) * mm});
            skLineSegment(sketch, "E2226", {"start": v(-119.46, -27.22) * mm, "end": v(-119.69, -27.42) * mm});
            skLineSegment(sketch, "E2227", {"start": v(-119.69, -27.42) * mm, "end": v(-119.92, -27.61) * mm});
            skLineSegment(sketch, "E2228", {"start": v(-119.92, -27.61) * mm, "end": v(-120.15, -27.81) * mm});
            skLineSegment(sketch, "E2229", {"start": v(-120.15, -27.81) * mm, "end": v(-120.39, -28.02) * mm});
            skLineSegment(sketch, "E2230", {"start": v(-120.39, -28.02) * mm, "end": v(-120.62, -28.23) * mm});
            skLineSegment(sketch, "E2231", {"start": v(-120.62, -28.23) * mm, "end": v(-120.86, -28.44) * mm});
            skLineSegment(sketch, "E2232", {"start": v(-120.86, -28.44) * mm, "end": v(-121.1, -28.65) * mm});
            skLineSegment(sketch, "E2233", {"start": v(-121.1, -28.65) * mm, "end": v(-121.34, -28.87) * mm});
            skLineSegment(sketch, "E2234", {"start": v(-121.34, -28.87) * mm, "end": v(-121.58, -29.1) * mm});
            skLineSegment(sketch, "E2235", {"start": v(-121.58, -29.1) * mm, "end": v(-121.82, -29.32) * mm});
            skLineSegment(sketch, "E2236", {"start": v(-121.82, -29.32) * mm, "end": v(-122.07, -29.55) * mm});
            skLineSegment(sketch, "E2237", {"start": v(-122.07, -29.55) * mm, "end": v(-122.31, -29.78) * mm});
            skLineSegment(sketch, "E2238", {"start": v(-122.31, -29.78) * mm, "end": v(-122.56, -30.02) * mm});
            skLineSegment(sketch, "E2239", {"start": v(-122.56, -30.02) * mm, "end": v(-122.8, -30.25) * mm});
            skLineSegment(sketch, "E2240", {"start": v(-122.8, -30.25) * mm, "end": v(-123.05, -30.5) * mm});
            skLineSegment(sketch, "E2241", {"start": v(-123.05, -30.5) * mm, "end": v(-123.02, -30.67) * mm});
            skLineSegment(sketch, "E2242", {"start": v(-123.02, -30.67) * mm, "end": v(-122.65, -32.07) * mm});
            skLineSegment(sketch, "E2243", {"start": v(-122.65, -32.07) * mm, "end": v(-122.6, -32.24) * mm});
            skLineSegment(sketch, "E2244", {"start": v(-122.6, -32.24) * mm, "end": v(-122.26, -32.33) * mm});
            skLineSegment(sketch, "E2245", {"start": v(-122.26, -32.33) * mm, "end": v(-121.92, -32.41) * mm});
            skLineSegment(sketch, "E2246", {"start": v(-121.92, -32.41) * mm, "end": v(-121.6, -32.5) * mm});
            skLineSegment(sketch, "E2247", {"start": v(-121.6, -32.5) * mm, "end": v(-121.27, -32.58) * mm});
            skLineSegment(sketch, "E2248", {"start": v(-121.27, -32.58) * mm, "end": v(-120.94, -32.66) * mm});
            skLineSegment(sketch, "E2249", {"start": v(-120.94, -32.66) * mm, "end": v(-120.62, -32.73) * mm});
            skLineSegment(sketch, "E2250", {"start": v(-120.62, -32.73) * mm, "end": v(-120.3, -32.8) * mm});
            skLineSegment(sketch, "E2251", {"start": v(-120.3, -32.8) * mm, "end": v(-119.98, -32.88) * mm});
            skLineSegment(sketch, "E2252", {"start": v(-119.98, -32.88) * mm, "end": v(-119.67, -32.95) * mm});
            skLineSegment(sketch, "E2253", {"start": v(-119.67, -32.95) * mm, "end": v(-119.36, -33.01) * mm});
            skLineSegment(sketch, "E2254", {"start": v(-119.36, -33.01) * mm, "end": v(-119.05, -33.08) * mm});
            skLineSegment(sketch, "E2255", {"start": v(-119.05, -33.08) * mm, "end": v(-118.75, -33.14) * mm});
            skLineSegment(sketch, "E2256", {"start": v(-118.75, -33.14) * mm, "end": v(-118.44, -33.2) * mm});
            skLineSegment(sketch, "E2257", {"start": v(-118.44, -33.2) * mm, "end": v(-118.14, -33.26) * mm});
            skLineSegment(sketch, "E2258", {"start": v(-118.14, -33.26) * mm, "end": v(-117.85, -33.3) * mm});
            skLineSegment(sketch, "E2259", {"start": v(-117.85, -33.3) * mm, "end": v(-117.55, -33.36) * mm});
            skLineSegment(sketch, "E2260", {"start": v(-117.55, -33.36) * mm, "end": v(-117.26, -33.41) * mm});
            skLineSegment(sketch, "E2261", {"start": v(-117.26, -33.41) * mm, "end": v(-116.98, -33.46) * mm});
            skLineSegment(sketch, "E2262", {"start": v(-116.98, -33.46) * mm, "end": v(-116.7, -33.5) * mm});
            skLineSegment(sketch, "E2263", {"start": v(-116.7, -33.5) * mm, "end": v(-116.41, -33.55) * mm});
            skLineSegment(sketch, "E2264", {"start": v(-116.41, -33.55) * mm, "end": v(-116.13, -33.6) * mm});
            skLineSegment(sketch, "E2265", {"start": v(-116.13, -33.6) * mm, "end": v(-115.86, -33.63) * mm});
            skLineSegment(sketch, "E2266", {"start": v(-115.86, -33.63) * mm, "end": v(-115.58, -33.67) * mm});
            skLineSegment(sketch, "E2267", {"start": v(-115.58, -33.67) * mm, "end": v(-115.31, -33.7) * mm});
            skLineSegment(sketch, "E2268", {"start": v(-115.31, -33.7) * mm, "end": v(-115.05, -33.74) * mm});
            skLineSegment(sketch, "E2269", {"start": v(-115.05, -33.74) * mm, "end": v(-114.78, -33.77) * mm});
            skLineSegment(sketch, "E2270", {"start": v(-114.78, -33.77) * mm, "end": v(-114.52, -33.8) * mm});
            skLineSegment(sketch, "E2271", {"start": v(-114.52, -33.8) * mm, "end": v(-114.27, -33.83) * mm});
            skLineSegment(sketch, "E2272", {"start": v(-114.27, -33.83) * mm, "end": v(-114.01, -33.86) * mm});
            skLineSegment(sketch, "E2273", {"start": v(-114.01, -33.86) * mm, "end": v(-113.76, -33.89) * mm});
            skLineSegment(sketch, "E2274", {"start": v(-113.76, -33.89) * mm, "end": v(-113.2, -34.85) * mm});
            skLineSegment(sketch, "E2275", {"start": v(-113.2, -34.85) * mm, "end": v(-113.1, -35.96) * mm});
            skLineSegment(sketch, "E2276", {"start": v(-113.1, -35.96) * mm, "end": v(-113.3, -36.13) * mm});
            skLineSegment(sketch, "E2277", {"start": v(-113.3, -36.13) * mm, "end": v(-113.48, -36.3) * mm});
            skLineSegment(sketch, "E2278", {"start": v(-113.48, -36.3) * mm, "end": v(-113.68, -36.47) * mm});
            skLineSegment(sketch, "E2279", {"start": v(-113.68, -36.47) * mm, "end": v(-113.87, -36.65) * mm});
            skLineSegment(sketch, "E2280", {"start": v(-113.87, -36.65) * mm, "end": v(-114.07, -36.83) * mm});
            skLineSegment(sketch, "E2281", {"start": v(-114.07, -36.83) * mm, "end": v(-114.27, -37) * mm});
            skLineSegment(sketch, "E2282", {"start": v(-114.27, -37) * mm, "end": v(-114.47, -37.2) * mm});
            skLineSegment(sketch, "E2283", {"start": v(-114.47, -37.2) * mm, "end": v(-114.67, -37.38) * mm});
            skLineSegment(sketch, "E2284", {"start": v(-114.67, -37.38) * mm, "end": v(-114.87, -37.57) * mm});
            skLineSegment(sketch, "E2285", {"start": v(-114.87, -37.57) * mm, "end": v(-115.07, -37.77) * mm});
            skLineSegment(sketch, "E2286", {"start": v(-115.07, -37.77) * mm, "end": v(-115.28, -37.97) * mm});
            skLineSegment(sketch, "E2287", {"start": v(-115.28, -37.97) * mm, "end": v(-115.48, -38.17) * mm});
            skLineSegment(sketch, "E2288", {"start": v(-115.48, -38.17) * mm, "end": v(-115.69, -38.37) * mm});
            skLineSegment(sketch, "E2289", {"start": v(-115.69, -38.37) * mm, "end": v(-115.9, -38.58) * mm});
            skLineSegment(sketch, "E2290", {"start": v(-115.9, -38.58) * mm, "end": v(-116.1, -38.8) * mm});
            skLineSegment(sketch, "E2291", {"start": v(-116.1, -38.8) * mm, "end": v(-116.32, -39.01) * mm});
            skLineSegment(sketch, "E2292", {"start": v(-116.32, -39.01) * mm, "end": v(-116.53, -39.23) * mm});
            skLineSegment(sketch, "E2293", {"start": v(-116.53, -39.23) * mm, "end": v(-116.74, -39.45) * mm});
            skLineSegment(sketch, "E2294", {"start": v(-116.74, -39.45) * mm, "end": v(-116.95, -39.68) * mm});
            skLineSegment(sketch, "E2295", {"start": v(-116.95, -39.68) * mm, "end": v(-117.17, -39.9) * mm});
            skLineSegment(sketch, "E2296", {"start": v(-117.17, -39.9) * mm, "end": v(-117.38, -40.14) * mm});
            skLineSegment(sketch, "E2297", {"start": v(-117.38, -40.14) * mm, "end": v(-117.6, -40.38) * mm});
            skLineSegment(sketch, "E2298", {"start": v(-117.6, -40.38) * mm, "end": v(-117.82, -40.62) * mm});
            skLineSegment(sketch, "E2299", {"start": v(-117.82, -40.62) * mm, "end": v(-118.04, -40.86) * mm});
            skLineSegment(sketch, "E2300", {"start": v(-118.04, -40.86) * mm, "end": v(-118.26, -41.11) * mm});
            skLineSegment(sketch, "E2301", {"start": v(-118.26, -41.11) * mm, "end": v(-118.48, -41.36) * mm});
            skLineSegment(sketch, "E2302", {"start": v(-118.48, -41.36) * mm, "end": v(-118.7, -41.62) * mm});
            skLineSegment(sketch, "E2303", {"start": v(-118.7, -41.62) * mm, "end": v(-118.92, -41.88) * mm});
            skLineSegment(sketch, "E2304", {"start": v(-118.92, -41.88) * mm, "end": v(-119.14, -42.14) * mm});
            skLineSegment(sketch, "E2305", {"start": v(-119.14, -42.14) * mm, "end": v(-119.36, -42.4) * mm});
            skLineSegment(sketch, "E2306", {"start": v(-119.36, -42.4) * mm, "end": v(-119.31, -42.58) * mm});
            skLineSegment(sketch, "E2307", {"start": v(-119.31, -42.58) * mm, "end": v(-118.8, -43.93) * mm});
            skLineSegment(sketch, "E2308", {"start": v(-118.8, -43.93) * mm, "end": v(-118.73, -44.1) * mm});
            skLineSegment(sketch, "E2309", {"start": v(-118.73, -44.1) * mm, "end": v(-118.4, -44.15) * mm});
            skLineSegment(sketch, "E2310", {"start": v(-118.4, -44.15) * mm, "end": v(-118.05, -44.2) * mm});
            skLineSegment(sketch, "E2311", {"start": v(-118.05, -44.2) * mm, "end": v(-117.71, -44.25) * mm});
            skLineSegment(sketch, "E2312", {"start": v(-117.71, -44.25) * mm, "end": v(-117.38, -44.3) * mm});
            skLineSegment(sketch, "E2313", {"start": v(-117.38, -44.3) * mm, "end": v(-117.05, -44.35) * mm});
            skLineSegment(sketch, "E2314", {"start": v(-117.05, -44.35) * mm, "end": v(-116.72, -44.4) * mm});
            skLineSegment(sketch, "E2315", {"start": v(-116.72, -44.4) * mm, "end": v(-116.4, -44.44) * mm});
            skLineSegment(sketch, "E2316", {"start": v(-116.4, -44.44) * mm, "end": v(-116.07, -44.48) * mm});
            skLineSegment(sketch, "E2317", {"start": v(-116.07, -44.48) * mm, "end": v(-115.76, -44.51) * mm});
            skLineSegment(sketch, "E2318", {"start": v(-115.76, -44.51) * mm, "end": v(-115.44, -44.55) * mm});
            skLineSegment(sketch, "E2319", {"start": v(-115.44, -44.55) * mm, "end": v(-115.13, -44.58) * mm});
            skLineSegment(sketch, "E2320", {"start": v(-115.13, -44.58) * mm, "end": v(-114.82, -44.61) * mm});
            skLineSegment(sketch, "E2321", {"start": v(-114.82, -44.61) * mm, "end": v(-114.51, -44.64) * mm});
            skLineSegment(sketch, "E2322", {"start": v(-114.51, -44.64) * mm, "end": v(-114.2, -44.67) * mm});
            skLineSegment(sketch, "E2323", {"start": v(-114.2, -44.67) * mm, "end": v(-113.9, -44.7) * mm});
            skLineSegment(sketch, "E2324", {"start": v(-113.9, -44.7) * mm, "end": v(-113.61, -44.72) * mm});
            skLineSegment(sketch, "E2325", {"start": v(-113.61, -44.72) * mm, "end": v(-113.32, -44.74) * mm});
            skLineSegment(sketch, "E2326", {"start": v(-113.32, -44.74) * mm, "end": v(-113.02, -44.76) * mm});
            skLineSegment(sketch, "E2327", {"start": v(-113.02, -44.76) * mm, "end": v(-112.74, -44.78) * mm});
            skLineSegment(sketch, "E2328", {"start": v(-112.74, -44.78) * mm, "end": v(-112.45, -44.8) * mm});
            skLineSegment(sketch, "E2329", {"start": v(-112.45, -44.8) * mm, "end": v(-112.17, -44.8) * mm});
            skLineSegment(sketch, "E2330", {"start": v(-112.17, -44.8) * mm, "end": v(-111.9, -44.82) * mm});
            skLineSegment(sketch, "E2331", {"start": v(-111.9, -44.82) * mm, "end": v(-111.62, -44.83) * mm});
            skLineSegment(sketch, "E2332", {"start": v(-111.62, -44.83) * mm, "end": v(-111.35, -44.84) * mm});
            skLineSegment(sketch, "E2333", {"start": v(-111.35, -44.84) * mm, "end": v(-111.08, -44.85) * mm});
            skLineSegment(sketch, "E2334", {"start": v(-111.08, -44.85) * mm, "end": v(-110.81, -44.86) * mm});
            skLineSegment(sketch, "E2335", {"start": v(-110.81, -44.86) * mm, "end": v(-110.55, -44.86) * mm});
            skLineSegment(sketch, "E2336", {"start": v(-110.55, -44.86) * mm, "end": v(-110.3, -44.87) * mm});
            skLineSegment(sketch, "E2337", {"start": v(-110.3, -44.87) * mm, "end": v(-110.04, -44.87) * mm});
            skLineSegment(sketch, "E2338", {"start": v(-110.04, -44.87) * mm, "end": v(-109.78, -44.87) * mm});
            skLineSegment(sketch, "E2339", {"start": v(-109.78, -44.87) * mm, "end": v(-109.14, -45.78) * mm});
            skLineSegment(sketch, "E2340", {"start": v(-109.14, -45.78) * mm, "end": v(-108.92, -46.87) * mm});
            skLineSegment(sketch, "E2341", {"start": v(-108.92, -46.87) * mm, "end": v(-109.1, -47.05) * mm});
            skLineSegment(sketch, "E2342", {"start": v(-109.1, -47.05) * mm, "end": v(-109.27, -47.24) * mm});
            skLineSegment(sketch, "E2343", {"start": v(-109.27, -47.24) * mm, "end": v(-109.45, -47.43) * mm});
            skLineSegment(sketch, "E2344", {"start": v(-109.45, -47.43) * mm, "end": v(-109.62, -47.63) * mm});
            skLineSegment(sketch, "E2345", {"start": v(-109.62, -47.63) * mm, "end": v(-109.8, -47.82) * mm});
            skLineSegment(sketch, "E2346", {"start": v(-109.8, -47.82) * mm, "end": v(-109.98, -48.02) * mm});
            skLineSegment(sketch, "E2347", {"start": v(-109.98, -48.02) * mm, "end": v(-110.16, -48.23) * mm});
            skLineSegment(sketch, "E2348", {"start": v(-110.16, -48.23) * mm, "end": v(-110.34, -48.43) * mm});
            skLineSegment(sketch, "E2349", {"start": v(-110.34, -48.43) * mm, "end": v(-110.52, -48.64) * mm});
            skLineSegment(sketch, "E2350", {"start": v(-110.52, -48.64) * mm, "end": v(-110.7, -48.86) * mm});
            skLineSegment(sketch, "E2351", {"start": v(-110.7, -48.86) * mm, "end": v(-110.9, -49.08) * mm});
            skLineSegment(sketch, "E2352", {"start": v(-110.9, -49.08) * mm, "end": v(-111.08, -49.3) * mm});
            skLineSegment(sketch, "E2353", {"start": v(-111.08, -49.3) * mm, "end": v(-111.26, -49.52) * mm});
            skLineSegment(sketch, "E2354", {"start": v(-111.26, -49.52) * mm, "end": v(-111.45, -49.75) * mm});
            skLineSegment(sketch, "E2355", {"start": v(-111.45, -49.75) * mm, "end": v(-111.64, -49.98) * mm});
            skLineSegment(sketch, "E2356", {"start": v(-111.64, -49.98) * mm, "end": v(-111.82, -50.22) * mm});
            skLineSegment(sketch, "E2357", {"start": v(-111.82, -50.22) * mm, "end": v(-112.01, -50.46) * mm});
            skLineSegment(sketch, "E2358", {"start": v(-112.01, -50.46) * mm, "end": v(-112.2, -50.7) * mm});
            skLineSegment(sketch, "E2359", {"start": v(-112.2, -50.7) * mm, "end": v(-112.4, -50.95) * mm});
            skLineSegment(sketch, "E2360", {"start": v(-112.4, -50.95) * mm, "end": v(-112.58, -51.2) * mm});
            skLineSegment(sketch, "E2361", {"start": v(-112.58, -51.2) * mm, "end": v(-112.78, -51.45) * mm});
            skLineSegment(sketch, "E2362", {"start": v(-112.78, -51.45) * mm, "end": v(-112.97, -51.7) * mm});
            skLineSegment(sketch, "E2363", {"start": v(-112.97, -51.7) * mm, "end": v(-113.16, -51.97) * mm});
            skLineSegment(sketch, "E2364", {"start": v(-113.16, -51.97) * mm, "end": v(-113.35, -52.23) * mm});
            skLineSegment(sketch, "E2365", {"start": v(-113.35, -52.23) * mm, "end": v(-113.55, -52.5) * mm});
            skLineSegment(sketch, "E2366", {"start": v(-113.55, -52.5) * mm, "end": v(-113.74, -52.77) * mm});
            skLineSegment(sketch, "E2367", {"start": v(-113.74, -52.77) * mm, "end": v(-113.94, -53.05) * mm});
            skLineSegment(sketch, "E2368", {"start": v(-113.94, -53.05) * mm, "end": v(-114.13, -53.33) * mm});
            skLineSegment(sketch, "E2369", {"start": v(-114.13, -53.33) * mm, "end": v(-114.33, -53.61) * mm});
            skLineSegment(sketch, "E2370", {"start": v(-114.33, -53.61) * mm, "end": v(-114.52, -53.9) * mm});
            skLineSegment(sketch, "E2371", {"start": v(-114.52, -53.9) * mm, "end": v(-114.46, -54.06) * mm});
            skLineSegment(sketch, "E2372", {"start": v(-114.46, -54.06) * mm, "end": v(-113.82, -55.36) * mm});
            skLineSegment(sketch, "E2373", {"start": v(-113.82, -55.36) * mm, "end": v(-113.73, -55.52) * mm});
            skLineSegment(sketch, "E2374", {"start": v(-113.73, -55.52) * mm, "end": v(-113.38, -55.54) * mm});
            skLineSegment(sketch, "E2375", {"start": v(-113.38, -55.54) * mm, "end": v(-113.04, -55.56) * mm});
            skLineSegment(sketch, "E2376", {"start": v(-113.04, -55.56) * mm, "end": v(-112.7, -55.57) * mm});
            skLineSegment(sketch, "E2377", {"start": v(-112.7, -55.57) * mm, "end": v(-112.36, -55.59) * mm});
            skLineSegment(sketch, "E2378", {"start": v(-112.36, -55.59) * mm, "end": v(-112.03, -55.6) * mm});
            skLineSegment(sketch, "E2379", {"start": v(-112.03, -55.6) * mm, "end": v(-111.7, -55.62) * mm});
            skLineSegment(sketch, "E2380", {"start": v(-111.7, -55.62) * mm, "end": v(-111.37, -55.63) * mm});
            skLineSegment(sketch, "E2381", {"start": v(-111.37, -55.63) * mm, "end": v(-111.05, -55.63) * mm});
            skLineSegment(sketch, "E2382", {"start": v(-111.05, -55.63) * mm, "end": v(-110.73, -55.64) * mm});
            skLineSegment(sketch, "E2383", {"start": v(-110.73, -55.64) * mm, "end": v(-110.4, -55.64) * mm});
            skLineSegment(sketch, "E2384", {"start": v(-110.4, -55.64) * mm, "end": v(-110.1, -55.65) * mm});
            skLineSegment(sketch, "E2385", {"start": v(-110.1, -55.65) * mm, "end": v(-109.78, -55.65) * mm});
            skLineSegment(sketch, "E2386", {"start": v(-109.78, -55.65) * mm, "end": v(-109.48, -55.65) * mm});
            skLineSegment(sketch, "E2387", {"start": v(-109.48, -55.65) * mm, "end": v(-109.17, -55.64) * mm});
            skLineSegment(sketch, "E2388", {"start": v(-109.17, -55.64) * mm, "end": v(-108.87, -55.64) * mm});
            skLineSegment(sketch, "E2389", {"start": v(-108.87, -55.64) * mm, "end": v(-108.57, -55.63) * mm});
            skLineSegment(sketch, "E2390", {"start": v(-108.57, -55.63) * mm, "end": v(-108.28, -55.63) * mm});
            skLineSegment(sketch, "E2391", {"start": v(-108.28, -55.63) * mm, "end": v(-107.99, -55.62) * mm});
            skLineSegment(sketch, "E2392", {"start": v(-107.99, -55.62) * mm, "end": v(-107.7, -55.6) * mm});
            skLineSegment(sketch, "E2393", {"start": v(-107.7, -55.6) * mm, "end": v(-107.41, -55.6) * mm});
            skLineSegment(sketch, "E2394", {"start": v(-107.41, -55.6) * mm, "end": v(-107.13, -55.58) * mm});
            skLineSegment(sketch, "E2395", {"start": v(-107.13, -55.58) * mm, "end": v(-106.85, -55.57) * mm});
            skLineSegment(sketch, "E2396", {"start": v(-106.85, -55.57) * mm, "end": v(-106.58, -55.55) * mm});
            skLineSegment(sketch, "E2397", {"start": v(-106.58, -55.55) * mm, "end": v(-106.3, -55.54) * mm});
            skLineSegment(sketch, "E2398", {"start": v(-106.3, -55.54) * mm, "end": v(-106.04, -55.52) * mm});
            skLineSegment(sketch, "E2399", {"start": v(-106.04, -55.52) * mm, "end": v(-105.77, -55.5) * mm});
            skLineSegment(sketch, "E2400", {"start": v(-105.77, -55.5) * mm, "end": v(-105.51, -55.48) * mm});
            skLineSegment(sketch, "E2401", {"start": v(-105.51, -55.48) * mm, "end": v(-105.25, -55.46) * mm});
            skLineSegment(sketch, "E2402", {"start": v(-105.25, -55.46) * mm, "end": v(-105, -55.43) * mm});
            skLineSegment(sketch, "E2403", {"start": v(-105, -55.43) * mm, "end": v(-104.75, -55.4) * mm});
            skLineSegment(sketch, "E2404", {"start": v(-104.75, -55.4) * mm, "end": v(-104.02, -56.25) * mm});
            skLineSegment(sketch, "E2405", {"start": v(-104.02, -56.25) * mm, "end": v(-103.7, -57.32) * mm});
            skLineSegment(sketch, "E2406", {"start": v(-103.7, -57.32) * mm, "end": v(-103.85, -57.52) * mm});
            skLineSegment(sketch, "E2407", {"start": v(-103.85, -57.52) * mm, "end": v(-104, -57.72) * mm});
            skLineSegment(sketch, "E2408", {"start": v(-104, -57.72) * mm, "end": v(-104.16, -57.93) * mm});
            skLineSegment(sketch, "E2409", {"start": v(-104.16, -57.93) * mm, "end": v(-104.32, -58.14) * mm});
            skLineSegment(sketch, "E2410", {"start": v(-104.32, -58.14) * mm, "end": v(-104.48, -58.35) * mm});
            skLineSegment(sketch, "E2411", {"start": v(-104.48, -58.35) * mm, "end": v(-104.63, -58.57) * mm});
            skLineSegment(sketch, "E2412", {"start": v(-104.63, -58.57) * mm, "end": v(-104.8, -58.79) * mm});
            skLineSegment(sketch, "E2413", {"start": v(-104.8, -58.79) * mm, "end": v(-104.95, -59.01) * mm});
            skLineSegment(sketch, "E2414", {"start": v(-104.95, -59.01) * mm, "end": v(-105.12, -59.24) * mm});
            skLineSegment(sketch, "E2415", {"start": v(-105.12, -59.24) * mm, "end": v(-105.28, -59.47) * mm});
            skLineSegment(sketch, "E2416", {"start": v(-105.28, -59.47) * mm, "end": v(-105.44, -59.7) * mm});
            skLineSegment(sketch, "E2417", {"start": v(-105.44, -59.7) * mm, "end": v(-105.6, -59.94) * mm});
            skLineSegment(sketch, "E2418", {"start": v(-105.6, -59.94) * mm, "end": v(-105.76, -60.19) * mm});
            skLineSegment(sketch, "E2419", {"start": v(-105.76, -60.19) * mm, "end": v(-105.93, -60.43) * mm});
            skLineSegment(sketch, "E2420", {"start": v(-105.93, -60.43) * mm, "end": v(-106.1, -60.68) * mm});
            skLineSegment(sketch, "E2421", {"start": v(-106.1, -60.68) * mm, "end": v(-106.25, -60.93) * mm});
            skLineSegment(sketch, "E2422", {"start": v(-106.25, -60.93) * mm, "end": v(-106.42, -61.19) * mm});
            skLineSegment(sketch, "E2423", {"start": v(-106.42, -61.19) * mm, "end": v(-106.58, -61.45) * mm});
            skLineSegment(sketch, "E2424", {"start": v(-106.58, -61.45) * mm, "end": v(-106.75, -61.71) * mm});
            skLineSegment(sketch, "E2425", {"start": v(-106.75, -61.71) * mm, "end": v(-106.92, -61.98) * mm});
            skLineSegment(sketch, "E2426", {"start": v(-106.92, -61.98) * mm, "end": v(-107.08, -62.25) * mm});
            skLineSegment(sketch, "E2427", {"start": v(-107.08, -62.25) * mm, "end": v(-107.25, -62.52) * mm});
            skLineSegment(sketch, "E2428", {"start": v(-107.25, -62.52) * mm, "end": v(-107.41, -62.8) * mm});
            skLineSegment(sketch, "E2429", {"start": v(-107.41, -62.8) * mm, "end": v(-107.58, -63.09) * mm});
            skLineSegment(sketch, "E2430", {"start": v(-107.58, -63.09) * mm, "end": v(-107.75, -63.37) * mm});
            skLineSegment(sketch, "E2431", {"start": v(-107.75, -63.37) * mm, "end": v(-107.91, -63.66) * mm});
            skLineSegment(sketch, "E2432", {"start": v(-107.91, -63.66) * mm, "end": v(-108.08, -63.95) * mm});
            skLineSegment(sketch, "E2433", {"start": v(-108.08, -63.95) * mm, "end": v(-108.25, -64.25) * mm});
            skLineSegment(sketch, "E2434", {"start": v(-108.25, -64.25) * mm, "end": v(-108.41, -64.55) * mm});
            skLineSegment(sketch, "E2435", {"start": v(-108.41, -64.55) * mm, "end": v(-108.58, -64.86) * mm});
            skLineSegment(sketch, "E2436", {"start": v(-108.58, -64.86) * mm, "end": v(-108.5, -65.01) * mm});
            skLineSegment(sketch, "E2437", {"start": v(-108.5, -65.01) * mm, "end": v(-107.74, -66.25) * mm});
            skLineSegment(sketch, "E2438", {"start": v(-107.74, -66.25) * mm, "end": v(-107.63, -66.39) * mm});
            skLineSegment(sketch, "E2439", {"start": v(-107.63, -66.39) * mm, "end": v(-107.29, -66.38) * mm});
            skLineSegment(sketch, "E2440", {"start": v(-107.29, -66.38) * mm, "end": v(-106.94, -66.36) * mm});
            skLineSegment(sketch, "E2441", {"start": v(-106.94, -66.36) * mm, "end": v(-106.6, -66.35) * mm});
            skLineSegment(sketch, "E2442", {"start": v(-106.6, -66.35) * mm, "end": v(-106.27, -66.33) * mm});
            skLineSegment(sketch, "E2443", {"start": v(-106.27, -66.33) * mm, "end": v(-105.93, -66.31) * mm});
            skLineSegment(sketch, "E2444", {"start": v(-105.93, -66.31) * mm, "end": v(-105.6, -66.3) * mm});
            skLineSegment(sketch, "E2445", {"start": v(-105.6, -66.3) * mm, "end": v(-105.28, -66.27) * mm});
            skLineSegment(sketch, "E2446", {"start": v(-105.28, -66.27) * mm, "end": v(-104.95, -66.24) * mm});
            skLineSegment(sketch, "E2447", {"start": v(-104.95, -66.24) * mm, "end": v(-104.63, -66.22) * mm});
            skLineSegment(sketch, "E2448", {"start": v(-104.63, -66.22) * mm, "end": v(-104.32, -66.2) * mm});
            skLineSegment(sketch, "E2449", {"start": v(-104.32, -66.2) * mm, "end": v(-104, -66.16) * mm});
            skLineSegment(sketch, "E2450", {"start": v(-104, -66.16) * mm, "end": v(-103.7, -66.13) * mm});
            skLineSegment(sketch, "E2451", {"start": v(-103.7, -66.13) * mm, "end": v(-103.39, -66.1) * mm});
            skLineSegment(sketch, "E2452", {"start": v(-103.39, -66.1) * mm, "end": v(-103.08, -66.07) * mm});
            skLineSegment(sketch, "E2453", {"start": v(-103.08, -66.07) * mm, "end": v(-102.78, -66.04) * mm});
            skLineSegment(sketch, "E2454", {"start": v(-102.78, -66.04) * mm, "end": v(-102.49, -66) * mm});
            skLineSegment(sketch, "E2455", {"start": v(-102.49, -66) * mm, "end": v(-102.2, -65.97) * mm});
            skLineSegment(sketch, "E2456", {"start": v(-102.2, -65.97) * mm, "end": v(-101.9, -65.93) * mm});
            skLineSegment(sketch, "E2457", {"start": v(-101.9, -65.93) * mm, "end": v(-101.62, -65.9) * mm});
            skLineSegment(sketch, "E2458", {"start": v(-101.62, -65.9) * mm, "end": v(-101.34, -65.85) * mm});
            skLineSegment(sketch, "E2459", {"start": v(-101.34, -65.85) * mm, "end": v(-101.06, -65.81) * mm});
            skLineSegment(sketch, "E2460", {"start": v(-101.06, -65.81) * mm, "end": v(-100.78, -65.77) * mm});
            skLineSegment(sketch, "E2461", {"start": v(-100.78, -65.77) * mm, "end": v(-100.51, -65.73) * mm});
            skLineSegment(sketch, "E2462", {"start": v(-100.51, -65.73) * mm, "end": v(-100.24, -65.68) * mm});
            skLineSegment(sketch, "E2463", {"start": v(-100.24, -65.68) * mm, "end": v(-99.98, -65.64) * mm});
            skLineSegment(sketch, "E2464", {"start": v(-99.98, -65.64) * mm, "end": v(-99.72, -65.6) * mm});
            skLineSegment(sketch, "E2465", {"start": v(-99.72, -65.6) * mm, "end": v(-99.46, -65.55) * mm});
            skLineSegment(sketch, "E2466", {"start": v(-99.46, -65.55) * mm, "end": v(-99.2, -65.5) * mm});
            skLineSegment(sketch, "E2467", {"start": v(-99.2, -65.5) * mm, "end": v(-98.95, -65.45) * mm});
            skLineSegment(sketch, "E2468", {"start": v(-98.95, -65.45) * mm, "end": v(-98.7, -65.4) * mm});
            skLineSegment(sketch, "E2469", {"start": v(-98.7, -65.4) * mm, "end": v(-97.9, -66.17) * mm});
            skLineSegment(sketch, "E2470", {"start": v(-97.9, -66.17) * mm, "end": v(-97.47, -67.2) * mm});
            skLineSegment(sketch, "E2471", {"start": v(-97.47, -67.2) * mm, "end": v(-97.6, -67.41) * mm});
            skLineSegment(sketch, "E2472", {"start": v(-97.6, -67.41) * mm, "end": v(-97.74, -67.63) * mm});
            skLineSegment(sketch, "E2473", {"start": v(-97.74, -67.63) * mm, "end": v(-97.87, -67.85) * mm});
            skLineSegment(sketch, "E2474", {"start": v(-97.87, -67.85) * mm, "end": v(-98, -68.08) * mm});
            skLineSegment(sketch, "E2475", {"start": v(-98, -68.08) * mm, "end": v(-98.15, -68.3) * mm});
            skLineSegment(sketch, "E2476", {"start": v(-98.15, -68.3) * mm, "end": v(-98.28, -68.54) * mm});
            skLineSegment(sketch, "E2477", {"start": v(-98.28, -68.54) * mm, "end": v(-98.42, -68.77) * mm});
            skLineSegment(sketch, "E2478", {"start": v(-98.42, -68.77) * mm, "end": v(-98.56, -69) * mm});
            skLineSegment(sketch, "E2479", {"start": v(-98.56, -69) * mm, "end": v(-98.7, -69.25) * mm});
            skLineSegment(sketch, "E2480", {"start": v(-98.7, -69.25) * mm, "end": v(-98.83, -69.5) * mm});
            skLineSegment(sketch, "E2481", {"start": v(-98.83, -69.5) * mm, "end": v(-98.97, -69.75) * mm});
            skLineSegment(sketch, "E2482", {"start": v(-98.97, -69.75) * mm, "end": v(-99.1, -70) * mm});
            skLineSegment(sketch, "E2483", {"start": v(-99.1, -70) * mm, "end": v(-99.25, -70.26) * mm});
            skLineSegment(sketch, "E2484", {"start": v(-99.25, -70.26) * mm, "end": v(-99.39, -70.52) * mm});
            skLineSegment(sketch, "E2485", {"start": v(-99.39, -70.52) * mm, "end": v(-99.52, -70.78) * mm});
            skLineSegment(sketch, "E2486", {"start": v(-99.52, -70.78) * mm, "end": v(-99.66, -71.05) * mm});
            skLineSegment(sketch, "E2487", {"start": v(-99.66, -71.05) * mm, "end": v(-99.8, -71.32) * mm});
            skLineSegment(sketch, "E2488", {"start": v(-99.8, -71.32) * mm, "end": v(-99.94, -71.6) * mm});
            skLineSegment(sketch, "E2489", {"start": v(-99.94, -71.6) * mm, "end": v(-100.08, -71.87) * mm});
            skLineSegment(sketch, "E2490", {"start": v(-100.08, -71.87) * mm, "end": v(-100.22, -72.16) * mm});
            skLineSegment(sketch, "E2491", {"start": v(-100.22, -72.16) * mm, "end": v(-100.36, -72.44) * mm});
            skLineSegment(sketch, "E2492", {"start": v(-100.36, -72.44) * mm, "end": v(-100.5, -72.73) * mm});
            skLineSegment(sketch, "E2493", {"start": v(-100.5, -72.73) * mm, "end": v(-100.63, -73.02) * mm});
            skLineSegment(sketch, "E2494", {"start": v(-100.63, -73.02) * mm, "end": v(-100.77, -73.32) * mm});
            skLineSegment(sketch, "E2495", {"start": v(-100.77, -73.32) * mm, "end": v(-100.9, -73.62) * mm});
            skLineSegment(sketch, "E2496", {"start": v(-100.9, -73.62) * mm, "end": v(-101.05, -73.93) * mm});
            skLineSegment(sketch, "E2497", {"start": v(-101.05, -73.93) * mm, "end": v(-101.18, -74.23) * mm});
            skLineSegment(sketch, "E2498", {"start": v(-101.18, -74.23) * mm, "end": v(-101.32, -74.55) * mm});
            skLineSegment(sketch, "E2499", {"start": v(-101.32, -74.55) * mm, "end": v(-101.46, -74.86) * mm});
            skLineSegment(sketch, "E2500", {"start": v(-101.46, -74.86) * mm, "end": v(-101.6, -75.18) * mm});
            skLineSegment(sketch, "E2501", {"start": v(-101.6, -75.18) * mm, "end": v(-101.5, -75.33) * mm});
            skLineSegment(sketch, "E2502", {"start": v(-101.5, -75.33) * mm, "end": v(-100.62, -76.48) * mm});
            skLineSegment(sketch, "E2503", {"start": v(-100.62, -76.48) * mm, "end": v(-100.5, -76.61) * mm});
            skLineSegment(sketch, "E2504", {"start": v(-100.5, -76.61) * mm, "end": v(-100.16, -76.57) * mm});
            skLineSegment(sketch, "E2505", {"start": v(-100.16, -76.57) * mm, "end": v(-99.81, -76.52) * mm});
            skLineSegment(sketch, "E2506", {"start": v(-99.81, -76.52) * mm, "end": v(-99.48, -76.47) * mm});
            skLineSegment(sketch, "E2507", {"start": v(-99.48, -76.47) * mm, "end": v(-99.14, -76.42) * mm});
            skLineSegment(sketch, "E2508", {"start": v(-99.14, -76.42) * mm, "end": v(-98.81, -76.37) * mm});
            skLineSegment(sketch, "E2509", {"start": v(-98.81, -76.37) * mm, "end": v(-98.49, -76.32) * mm});
            skLineSegment(sketch, "E2510", {"start": v(-98.49, -76.32) * mm, "end": v(-98.16, -76.26) * mm});
            skLineSegment(sketch, "E2511", {"start": v(-98.16, -76.26) * mm, "end": v(-97.85, -76.2) * mm});
            skLineSegment(sketch, "E2512", {"start": v(-97.85, -76.2) * mm, "end": v(-97.53, -76.15) * mm});
            skLineSegment(sketch, "E2513", {"start": v(-97.53, -76.15) * mm, "end": v(-97.22, -76.1) * mm});
            skLineSegment(sketch, "E2514", {"start": v(-97.22, -76.1) * mm, "end": v(-96.9, -76.03) * mm});
            skLineSegment(sketch, "E2515", {"start": v(-96.9, -76.03) * mm, "end": v(-96.6, -75.97) * mm});
            skLineSegment(sketch, "E2516", {"start": v(-96.6, -75.97) * mm, "end": v(-96.3, -75.91) * mm});
            skLineSegment(sketch, "E2517", {"start": v(-96.3, -75.91) * mm, "end": v(-96, -75.85) * mm});
            skLineSegment(sketch, "E2518", {"start": v(-96, -75.85) * mm, "end": v(-95.7, -75.79) * mm});
            skLineSegment(sketch, "E2519", {"start": v(-95.7, -75.79) * mm, "end": v(-95.42, -75.73) * mm});
            skLineSegment(sketch, "E2520", {"start": v(-95.42, -75.73) * mm, "end": v(-95.13, -75.66) * mm});
            skLineSegment(sketch, "E2521", {"start": v(-95.13, -75.66) * mm, "end": v(-94.84, -75.6) * mm});
            skLineSegment(sketch, "E2522", {"start": v(-94.84, -75.6) * mm, "end": v(-94.56, -75.53) * mm});
            skLineSegment(sketch, "E2523", {"start": v(-94.56, -75.53) * mm, "end": v(-94.29, -75.46) * mm});
            skLineSegment(sketch, "E2524", {"start": v(-94.29, -75.46) * mm, "end": v(-94.01, -75.4) * mm});
            skLineSegment(sketch, "E2525", {"start": v(-94.01, -75.4) * mm, "end": v(-93.74, -75.33) * mm});
            skLineSegment(sketch, "E2526", {"start": v(-93.74, -75.33) * mm, "end": v(-93.48, -75.26) * mm});
            skLineSegment(sketch, "E2527", {"start": v(-93.48, -75.26) * mm, "end": v(-93.21, -75.19) * mm});
            skLineSegment(sketch, "E2528", {"start": v(-93.21, -75.19) * mm, "end": v(-92.95, -75.12) * mm});
            skLineSegment(sketch, "E2529", {"start": v(-92.95, -75.12) * mm, "end": v(-92.7, -75.05) * mm});
            skLineSegment(sketch, "E2530", {"start": v(-92.7, -75.05) * mm, "end": v(-92.45, -74.97) * mm});
            skLineSegment(sketch, "E2531", {"start": v(-92.45, -74.97) * mm, "end": v(-92.2, -74.9) * mm});
            skLineSegment(sketch, "E2532", {"start": v(-92.2, -74.9) * mm, "end": v(-91.95, -74.83) * mm});
            skLineSegment(sketch, "E2533", {"start": v(-91.95, -74.83) * mm, "end": v(-91.7, -74.76) * mm});
            skLineSegment(sketch, "E2534", {"start": v(-91.7, -74.76) * mm, "end": v(-90.83, -75.44) * mm});
            skLineSegment(sketch, "E2535", {"start": v(-90.83, -75.44) * mm, "end": v(-90.3, -76.42) * mm});
            skLineSegment(sketch, "E2536", {"start": v(-90.3, -76.42) * mm, "end": v(-90.42, -76.65) * mm});
            skLineSegment(sketch, "E2537", {"start": v(-90.42, -76.65) * mm, "end": v(-90.53, -76.88) * mm});
            skLineSegment(sketch, "E2538", {"start": v(-90.53, -76.88) * mm, "end": v(-90.64, -77.11) * mm});
            skLineSegment(sketch, "E2539", {"start": v(-90.64, -77.11) * mm, "end": v(-90.76, -77.35) * mm});
            skLineSegment(sketch, "E2540", {"start": v(-90.76, -77.35) * mm, "end": v(-90.87, -77.59) * mm});
            skLineSegment(sketch, "E2541", {"start": v(-90.87, -77.59) * mm, "end": v(-90.98, -77.83) * mm});
            skLineSegment(sketch, "E2542", {"start": v(-90.98, -77.83) * mm, "end": v(-91.1, -78.08) * mm});
            skLineSegment(sketch, "E2543", {"start": v(-91.1, -78.08) * mm, "end": v(-91.2, -78.33) * mm});
            skLineSegment(sketch, "E2544", {"start": v(-91.2, -78.33) * mm, "end": v(-91.32, -78.59) * mm});
            skLineSegment(sketch, "E2545", {"start": v(-91.32, -78.59) * mm, "end": v(-91.44, -78.84) * mm});
            skLineSegment(sketch, "E2546", {"start": v(-91.44, -78.84) * mm, "end": v(-91.55, -79.1) * mm});
            skLineSegment(sketch, "E2547", {"start": v(-91.55, -79.1) * mm, "end": v(-91.66, -79.37) * mm});
            skLineSegment(sketch, "E2548", {"start": v(-91.66, -79.37) * mm, "end": v(-91.77, -79.64) * mm});
            skLineSegment(sketch, "E2549", {"start": v(-91.77, -79.64) * mm, "end": v(-91.89, -79.91) * mm});
            skLineSegment(sketch, "E2550", {"start": v(-91.89, -79.91) * mm, "end": v(-92, -80.19) * mm});
            skLineSegment(sketch, "E2551", {"start": v(-92, -80.19) * mm, "end": v(-92.11, -80.47) * mm});
            skLineSegment(sketch, "E2552", {"start": v(-92.11, -80.47) * mm, "end": v(-92.22, -80.75) * mm});
            skLineSegment(sketch, "E2553", {"start": v(-92.22, -80.75) * mm, "end": v(-92.33, -81.04) * mm});
            skLineSegment(sketch, "E2554", {"start": v(-92.33, -81.04) * mm, "end": v(-92.44, -81.33) * mm});
            skLineSegment(sketch, "E2555", {"start": v(-92.44, -81.33) * mm, "end": v(-92.55, -81.63) * mm});
            skLineSegment(sketch, "E2556", {"start": v(-92.55, -81.63) * mm, "end": v(-92.66, -81.92) * mm});
            skLineSegment(sketch, "E2557", {"start": v(-92.66, -81.92) * mm, "end": v(-92.77, -82.23) * mm});
            skLineSegment(sketch, "E2558", {"start": v(-92.77, -82.23) * mm, "end": v(-92.88, -82.53) * mm});
            skLineSegment(sketch, "E2559", {"start": v(-92.88, -82.53) * mm, "end": v(-92.99, -82.84) * mm});
            skLineSegment(sketch, "E2560", {"start": v(-92.99, -82.84) * mm, "end": v(-93.1, -83.15) * mm});
            skLineSegment(sketch, "E2561", {"start": v(-93.1, -83.15) * mm, "end": v(-93.2, -83.47) * mm});
            skLineSegment(sketch, "E2562", {"start": v(-93.2, -83.47) * mm, "end": v(-93.31, -83.79) * mm});
            skLineSegment(sketch, "E2563", {"start": v(-93.31, -83.79) * mm, "end": v(-93.42, -84.11) * mm});
            skLineSegment(sketch, "E2564", {"start": v(-93.42, -84.11) * mm, "end": v(-93.52, -84.44) * mm});
            skLineSegment(sketch, "E2565", {"start": v(-93.52, -84.44) * mm, "end": v(-93.62, -84.77) * mm});
            skLineSegment(sketch, "E2566", {"start": v(-93.62, -84.77) * mm, "end": v(-93.51, -84.91) * mm});
            skLineSegment(sketch, "E2567", {"start": v(-93.51, -84.91) * mm, "end": v(-92.53, -85.97) * mm});
            skLineSegment(sketch, "E2568", {"start": v(-92.53, -85.97) * mm, "end": v(-92.4, -86.1) * mm});
            skLineSegment(sketch, "E2569", {"start": v(-92.4, -86.1) * mm, "end": v(-92.06, -86.01) * mm});
            skLineSegment(sketch, "E2570", {"start": v(-92.06, -86.01) * mm, "end": v(-91.73, -85.93) * mm});
            skLineSegment(sketch, "E2571", {"start": v(-91.73, -85.93) * mm, "end": v(-91.4, -85.85) * mm});
            skLineSegment(sketch, "E2572", {"start": v(-91.4, -85.85) * mm, "end": v(-91.07, -85.77) * mm});
            skLineSegment(sketch, "E2573", {"start": v(-91.07, -85.77) * mm, "end": v(-90.74, -85.68) * mm});
            skLineSegment(sketch, "E2574", {"start": v(-90.74, -85.68) * mm, "end": v(-90.42, -85.6) * mm});
            skLineSegment(sketch, "E2575", {"start": v(-90.42, -85.6) * mm, "end": v(-90.1, -85.51) * mm});
            skLineSegment(sketch, "E2576", {"start": v(-90.1, -85.51) * mm, "end": v(-89.8, -85.43) * mm});
            skLineSegment(sketch, "E2577", {"start": v(-89.8, -85.43) * mm, "end": v(-89.49, -85.34) * mm});
            skLineSegment(sketch, "E2578", {"start": v(-89.49, -85.34) * mm, "end": v(-89.18, -85.25) * mm});
            skLineSegment(sketch, "E2579", {"start": v(-89.18, -85.25) * mm, "end": v(-88.88, -85.16) * mm});
            skLineSegment(sketch, "E2580", {"start": v(-88.88, -85.16) * mm, "end": v(-88.58, -85.07) * mm});
            skLineSegment(sketch, "E2581", {"start": v(-88.58, -85.07) * mm, "end": v(-88.29, -84.98) * mm});
            skLineSegment(sketch, "E2582", {"start": v(-88.29, -84.98) * mm, "end": v(-88, -84.9) * mm});
            skLineSegment(sketch, "E2583", {"start": v(-88, -84.9) * mm, "end": v(-87.7, -84.8) * mm});
            skLineSegment(sketch, "E2584", {"start": v(-87.7, -84.8) * mm, "end": v(-87.43, -84.7) * mm});
            skLineSegment(sketch, "E2585", {"start": v(-87.43, -84.7) * mm, "end": v(-87.15, -84.62) * mm});
            skLineSegment(sketch, "E2586", {"start": v(-87.15, -84.62) * mm, "end": v(-86.87, -84.52) * mm});
            skLineSegment(sketch, "E2587", {"start": v(-86.87, -84.52) * mm, "end": v(-86.6, -84.43) * mm});
            skLineSegment(sketch, "E2588", {"start": v(-86.6, -84.43) * mm, "end": v(-86.33, -84.34) * mm});
            skLineSegment(sketch, "E2589", {"start": v(-86.33, -84.34) * mm, "end": v(-86.06, -84.24) * mm});
            skLineSegment(sketch, "E2590", {"start": v(-86.06, -84.24) * mm, "end": v(-85.8, -84.15) * mm});
            skLineSegment(sketch, "E2591", {"start": v(-85.8, -84.15) * mm, "end": v(-85.54, -84.05) * mm});
            skLineSegment(sketch, "E2592", {"start": v(-85.54, -84.05) * mm, "end": v(-85.29, -83.96) * mm});
            skLineSegment(sketch, "E2593", {"start": v(-85.29, -83.96) * mm, "end": v(-85.03, -83.86) * mm});
            skLineSegment(sketch, "E2594", {"start": v(-85.03, -83.86) * mm, "end": v(-84.79, -83.76) * mm});
            skLineSegment(sketch, "E2595", {"start": v(-84.79, -83.76) * mm, "end": v(-84.54, -83.67) * mm});
            skLineSegment(sketch, "E2596", {"start": v(-84.54, -83.67) * mm, "end": v(-84.3, -83.57) * mm});
            skLineSegment(sketch, "E2597", {"start": v(-84.3, -83.57) * mm, "end": v(-84.07, -83.48) * mm});
            skLineSegment(sketch, "E2598", {"start": v(-84.07, -83.48) * mm, "end": v(-83.83, -83.38) * mm});
            skLineSegment(sketch, "E2599", {"start": v(-83.83, -83.38) * mm, "end": v(-82.89, -83.97) * mm});
            skLineSegment(sketch, "E2600", {"start": v(-82.89, -83.97) * mm, "end": v(-82.27, -84.9) * mm});
            skLineSegment(sketch, "E2601", {"start": v(-82.27, -84.9) * mm, "end": v(-82.36, -85.14) * mm});
            skLineSegment(sketch, "E2602", {"start": v(-82.36, -85.14) * mm, "end": v(-82.45, -85.38) * mm});
            skLineSegment(sketch, "E2603", {"start": v(-82.45, -85.38) * mm, "end": v(-82.54, -85.62) * mm});
            skLineSegment(sketch, "E2604", {"start": v(-82.54, -85.62) * mm, "end": v(-82.63, -85.87) * mm});
            skLineSegment(sketch, "E2605", {"start": v(-82.63, -85.87) * mm, "end": v(-82.72, -86.12) * mm});
            skLineSegment(sketch, "E2606", {"start": v(-82.72, -86.12) * mm, "end": v(-82.8, -86.37) * mm});
            skLineSegment(sketch, "E2607", {"start": v(-82.8, -86.37) * mm, "end": v(-82.9, -86.63) * mm});
            skLineSegment(sketch, "E2608", {"start": v(-82.9, -86.63) * mm, "end": v(-82.98, -86.89) * mm});
            skLineSegment(sketch, "E2609", {"start": v(-82.98, -86.89) * mm, "end": v(-83.07, -87.15) * mm});
            skLineSegment(sketch, "E2610", {"start": v(-83.07, -87.15) * mm, "end": v(-83.16, -87.42) * mm});
            skLineSegment(sketch, "E2611", {"start": v(-83.16, -87.42) * mm, "end": v(-83.25, -87.7) * mm});
            skLineSegment(sketch, "E2612", {"start": v(-83.25, -87.7) * mm, "end": v(-83.33, -87.97) * mm});
            skLineSegment(sketch, "E2613", {"start": v(-83.33, -87.97) * mm, "end": v(-83.42, -88.25) * mm});
            skLineSegment(sketch, "E2614", {"start": v(-83.42, -88.25) * mm, "end": v(-83.5, -88.53) * mm});
            skLineSegment(sketch, "E2615", {"start": v(-83.5, -88.53) * mm, "end": v(-83.59, -88.82) * mm});
            skLineSegment(sketch, "E2616", {"start": v(-83.59, -88.82) * mm, "end": v(-83.67, -89.1) * mm});
            skLineSegment(sketch, "E2617", {"start": v(-83.67, -89.1) * mm, "end": v(-83.75, -89.4) * mm});
            skLineSegment(sketch, "E2618", {"start": v(-83.75, -89.4) * mm, "end": v(-83.84, -89.7) * mm});
            skLineSegment(sketch, "E2619", {"start": v(-83.84, -89.7) * mm, "end": v(-83.92, -90) * mm});
            skLineSegment(sketch, "E2620", {"start": v(-83.92, -90) * mm, "end": v(-84, -90.3) * mm});
            skLineSegment(sketch, "E2621", {"start": v(-84, -90.3) * mm, "end": v(-84.08, -90.6) * mm});
            skLineSegment(sketch, "E2622", {"start": v(-84.08, -90.6) * mm, "end": v(-84.16, -90.92) * mm});
            skLineSegment(sketch, "E2623", {"start": v(-84.16, -90.92) * mm, "end": v(-84.24, -91.23) * mm});
            skLineSegment(sketch, "E2624", {"start": v(-84.24, -91.23) * mm, "end": v(-84.31, -91.55) * mm});
            skLineSegment(sketch, "E2625", {"start": v(-84.31, -91.55) * mm, "end": v(-84.4, -91.87) * mm});
            skLineSegment(sketch, "E2626", {"start": v(-84.4, -91.87) * mm, "end": v(-84.47, -92.2) * mm});
            skLineSegment(sketch, "E2627", {"start": v(-84.47, -92.2) * mm, "end": v(-84.54, -92.53) * mm});
            skLineSegment(sketch, "E2628", {"start": v(-84.54, -92.53) * mm, "end": v(-84.61, -92.86) * mm});
            skLineSegment(sketch, "E2629", {"start": v(-84.61, -92.86) * mm, "end": v(-84.69, -93.2) * mm});
            skLineSegment(sketch, "E2630", {"start": v(-84.69, -93.2) * mm, "end": v(-84.76, -93.54) * mm});
            skLineSegment(sketch, "E2631", {"start": v(-84.76, -93.54) * mm, "end": v(-84.63, -93.66) * mm});
            skLineSegment(sketch, "E2632", {"start": v(-84.63, -93.66) * mm, "end": v(-83.55, -94.62) * mm});
            skLineSegment(sketch, "E2633", {"start": v(-83.55, -94.62) * mm, "end": v(-83.4, -94.73) * mm});
            skLineSegment(sketch, "E2634", {"start": v(-83.4, -94.73) * mm, "end": v(-83.08, -94.62) * mm});
            skLineSegment(sketch, "E2635", {"start": v(-83.08, -94.62) * mm, "end": v(-82.75, -94.5) * mm});
            skLineSegment(sketch, "E2636", {"start": v(-82.75, -94.5) * mm, "end": v(-82.43, -94.39) * mm});
            skLineSegment(sketch, "E2637", {"start": v(-82.43, -94.39) * mm, "end": v(-82.11, -94.27) * mm});
            skLineSegment(sketch, "E2638", {"start": v(-82.11, -94.27) * mm, "end": v(-81.8, -94.16) * mm});
            skLineSegment(sketch, "E2639", {"start": v(-81.8, -94.16) * mm, "end": v(-81.5, -94.04) * mm});
            skLineSegment(sketch, "E2640", {"start": v(-81.5, -94.04) * mm, "end": v(-81.18, -93.93) * mm});
            skLineSegment(sketch, "E2641", {"start": v(-81.18, -93.93) * mm, "end": v(-80.88, -93.81) * mm});
            skLineSegment(sketch, "E2642", {"start": v(-80.88, -93.81) * mm, "end": v(-80.58, -93.7) * mm});
            skLineSegment(sketch, "E2643", {"start": v(-80.58, -93.7) * mm, "end": v(-80.29, -93.58) * mm});
            skLineSegment(sketch, "E2644", {"start": v(-80.29, -93.58) * mm, "end": v(-80, -93.46) * mm});
            skLineSegment(sketch, "E2645", {"start": v(-80, -93.46) * mm, "end": v(-79.7, -93.34) * mm});
            skLineSegment(sketch, "E2646", {"start": v(-79.7, -93.34) * mm, "end": v(-79.42, -93.22) * mm});
            skLineSegment(sketch, "E2647", {"start": v(-79.42, -93.22) * mm, "end": v(-79.14, -93.1) * mm});
            skLineSegment(sketch, "E2648", {"start": v(-79.14, -93.1) * mm, "end": v(-78.87, -92.98) * mm});
            skLineSegment(sketch, "E2649", {"start": v(-78.87, -92.98) * mm, "end": v(-78.6, -92.86) * mm});
            skLineSegment(sketch, "E2650", {"start": v(-78.6, -92.86) * mm, "end": v(-78.32, -92.74) * mm});
            skLineSegment(sketch, "E2651", {"start": v(-78.32, -92.74) * mm, "end": v(-78.06, -92.62) * mm});
            skLineSegment(sketch, "E2652", {"start": v(-78.06, -92.62) * mm, "end": v(-77.8, -92.5) * mm});
            skLineSegment(sketch, "E2653", {"start": v(-77.8, -92.5) * mm, "end": v(-77.54, -92.38) * mm});
            skLineSegment(sketch, "E2654", {"start": v(-77.54, -92.38) * mm, "end": v(-77.28, -92.27) * mm});
            skLineSegment(sketch, "E2655", {"start": v(-77.28, -92.27) * mm, "end": v(-77.03, -92.15) * mm});
            skLineSegment(sketch, "E2656", {"start": v(-77.03, -92.15) * mm, "end": v(-76.78, -92.03) * mm});
            skLineSegment(sketch, "E2657", {"start": v(-76.78, -92.03) * mm, "end": v(-76.54, -91.9) * mm});
            skLineSegment(sketch, "E2658", {"start": v(-76.54, -91.9) * mm, "end": v(-76.3, -91.79) * mm});
            skLineSegment(sketch, "E2659", {"start": v(-76.3, -91.79) * mm, "end": v(-76.06, -91.67) * mm});
            skLineSegment(sketch, "E2660", {"start": v(-76.06, -91.67) * mm, "end": v(-75.83, -91.55) * mm});
            skLineSegment(sketch, "E2661", {"start": v(-75.83, -91.55) * mm, "end": v(-75.6, -91.43) * mm});
            skLineSegment(sketch, "E2662", {"start": v(-75.6, -91.43) * mm, "end": v(-75.37, -91.31) * mm});
            skLineSegment(sketch, "E2663", {"start": v(-75.37, -91.31) * mm, "end": v(-75.15, -91.2) * mm});
            skLineSegment(sketch, "E2664", {"start": v(-75.15, -91.2) * mm, "end": v(-74.15, -91.69) * mm});
            skLineSegment(sketch, "E2665", {"start": v(-74.15, -91.69) * mm, "end": v(-73.45, -92.55) * mm});
            skLineSegment(sketch, "E2666", {"start": v(-73.45, -92.55) * mm, "end": v(-73.51, -92.8) * mm});
            skLineSegment(sketch, "E2667", {"start": v(-73.51, -92.8) * mm, "end": v(-73.58, -93.04) * mm});
            skLineSegment(sketch, "E2668", {"start": v(-73.58, -93.04) * mm, "end": v(-73.64, -93.3) * mm});
            skLineSegment(sketch, "E2669", {"start": v(-73.64, -93.3) * mm, "end": v(-73.7, -93.55) * mm});
            skLineSegment(sketch, "E2670", {"start": v(-73.7, -93.55) * mm, "end": v(-73.77, -93.8) * mm});
            skLineSegment(sketch, "E2671", {"start": v(-73.77, -93.8) * mm, "end": v(-73.83, -94.07) * mm});
            skLineSegment(sketch, "E2672", {"start": v(-73.83, -94.07) * mm, "end": v(-73.9, -94.33) * mm});
            skLineSegment(sketch, "E2673", {"start": v(-73.9, -94.33) * mm, "end": v(-73.96, -94.6) * mm});
            skLineSegment(sketch, "E2674", {"start": v(-73.96, -94.6) * mm, "end": v(-74.02, -94.87) * mm});
            skLineSegment(sketch, "E2675", {"start": v(-74.02, -94.87) * mm, "end": v(-74.08, -95.15) * mm});
            skLineSegment(sketch, "E2676", {"start": v(-74.08, -95.15) * mm, "end": v(-74.14, -95.43) * mm});
            skLineSegment(sketch, "E2677", {"start": v(-74.14, -95.43) * mm, "end": v(-74.2, -95.7) * mm});
            skLineSegment(sketch, "E2678", {"start": v(-74.2, -95.7) * mm, "end": v(-74.26, -96) * mm});
            skLineSegment(sketch, "E2679", {"start": v(-74.26, -96) * mm, "end": v(-74.31, -96.28) * mm});
            skLineSegment(sketch, "E2680", {"start": v(-74.31, -96.28) * mm, "end": v(-74.37, -96.58) * mm});
            skLineSegment(sketch, "E2681", {"start": v(-74.37, -96.58) * mm, "end": v(-74.43, -96.87) * mm});
            skLineSegment(sketch, "E2682", {"start": v(-74.43, -96.87) * mm, "end": v(-74.48, -97.17) * mm});
            skLineSegment(sketch, "E2683", {"start": v(-74.48, -97.17) * mm, "end": v(-74.53, -97.47) * mm});
            skLineSegment(sketch, "E2684", {"start": v(-74.53, -97.47) * mm, "end": v(-74.58, -97.78) * mm});
            skLineSegment(sketch, "E2685", {"start": v(-74.58, -97.78) * mm, "end": v(-74.64, -98.1) * mm});
            skLineSegment(sketch, "E2686", {"start": v(-74.64, -98.1) * mm, "end": v(-74.69, -98.4) * mm});
            skLineSegment(sketch, "E2687", {"start": v(-74.69, -98.4) * mm, "end": v(-74.73, -98.72) * mm});
            skLineSegment(sketch, "E2688", {"start": v(-74.73, -98.72) * mm, "end": v(-74.78, -99.04) * mm});
            skLineSegment(sketch, "E2689", {"start": v(-74.78, -99.04) * mm, "end": v(-74.83, -99.37) * mm});
            skLineSegment(sketch, "E2690", {"start": v(-74.83, -99.37) * mm, "end": v(-74.87, -99.7) * mm});
            skLineSegment(sketch, "E2691", {"start": v(-74.87, -99.7) * mm, "end": v(-74.91, -100.03) * mm});
            skLineSegment(sketch, "E2692", {"start": v(-74.91, -100.03) * mm, "end": v(-74.96, -100.36) * mm});
            skLineSegment(sketch, "E2693", {"start": v(-74.96, -100.36) * mm, "end": v(-75, -100.7) * mm});
            skLineSegment(sketch, "E2694", {"start": v(-75, -100.7) * mm, "end": v(-75.03, -101.04) * mm});
            skLineSegment(sketch, "E2695", {"start": v(-75.03, -101.04) * mm, "end": v(-75.07, -101.39) * mm});
            skLineSegment(sketch, "E2696", {"start": v(-75.07, -101.39) * mm, "end": v(-74.94, -101.5) * mm});
            skLineSegment(sketch, "E2697", {"start": v(-74.94, -101.5) * mm, "end": v(-73.76, -102.35) * mm});
            skLineSegment(sketch, "E2698", {"start": v(-73.76, -102.35) * mm, "end": v(-73.61, -102.44) * mm});
            skLineSegment(sketch, "E2699", {"start": v(-73.61, -102.44) * mm, "end": v(-73.3, -102.3) * mm});
            skLineSegment(sketch, "E2700", {"start": v(-73.3, -102.3) * mm, "end": v(-72.98, -102.15) * mm});
            skLineSegment(sketch, "E2701", {"start": v(-72.98, -102.15) * mm, "end": v(-72.67, -102) * mm});
            skLineSegment(sketch, "E2702", {"start": v(-72.67, -102) * mm, "end": v(-72.37, -101.86) * mm});
            skLineSegment(sketch, "E2703", {"start": v(-72.37, -101.86) * mm, "end": v(-72.07, -101.72) * mm});
            skLineSegment(sketch, "E2704", {"start": v(-72.07, -101.72) * mm, "end": v(-71.77, -101.57) * mm});
            skLineSegment(sketch, "E2705", {"start": v(-71.77, -101.57) * mm, "end": v(-71.48, -101.43) * mm});
            skLineSegment(sketch, "E2706", {"start": v(-71.48, -101.43) * mm, "end": v(-71.19, -101.28) * mm});
            skLineSegment(sketch, "E2707", {"start": v(-71.19, -101.28) * mm, "end": v(-70.9, -101.14) * mm});
            skLineSegment(sketch, "E2708", {"start": v(-70.9, -101.14) * mm, "end": v(-70.62, -100.99) * mm});
            skLineSegment(sketch, "E2709", {"start": v(-70.62, -100.99) * mm, "end": v(-70.34, -100.84) * mm});
            skLineSegment(sketch, "E2710", {"start": v(-70.34, -100.84) * mm, "end": v(-70.07, -100.7) * mm});
            skLineSegment(sketch, "E2711", {"start": v(-70.07, -100.7) * mm, "end": v(-69.8, -100.55) * mm});
            skLineSegment(sketch, "E2712", {"start": v(-69.8, -100.55) * mm, "end": v(-69.53, -100.4) * mm});
            skLineSegment(sketch, "E2713", {"start": v(-69.53, -100.4) * mm, "end": v(-69.27, -100.26) * mm});
            skLineSegment(sketch, "E2714", {"start": v(-69.27, -100.26) * mm, "end": v(-69, -100.11) * mm});
            skLineSegment(sketch, "E2715", {"start": v(-69, -100.11) * mm, "end": v(-68.75, -99.97) * mm});
            skLineSegment(sketch, "E2716", {"start": v(-68.75, -99.97) * mm, "end": v(-68.5, -99.82) * mm});
            skLineSegment(sketch, "E2717", {"start": v(-68.5, -99.82) * mm, "end": v(-68.25, -99.68) * mm});
            skLineSegment(sketch, "E2718", {"start": v(-68.25, -99.68) * mm, "end": v(-68, -99.53) * mm});
            skLineSegment(sketch, "E2719", {"start": v(-68, -99.53) * mm, "end": v(-67.76, -99.4) * mm});
            skLineSegment(sketch, "E2720", {"start": v(-67.76, -99.4) * mm, "end": v(-67.52, -99.25) * mm});
            skLineSegment(sketch, "E2721", {"start": v(-67.52, -99.25) * mm, "end": v(-67.28, -99.1) * mm});
            skLineSegment(sketch, "E2722", {"start": v(-67.28, -99.1) * mm, "end": v(-67.05, -98.96) * mm});
            skLineSegment(sketch, "E2723", {"start": v(-67.05, -98.96) * mm, "end": v(-66.83, -98.82) * mm});
            skLineSegment(sketch, "E2724", {"start": v(-66.83, -98.82) * mm, "end": v(-66.6, -98.68) * mm});
            skLineSegment(sketch, "E2725", {"start": v(-66.6, -98.68) * mm, "end": v(-66.38, -98.53) * mm});
            skLineSegment(sketch, "E2726", {"start": v(-66.38, -98.53) * mm, "end": v(-66.16, -98.4) * mm});
            skLineSegment(sketch, "E2727", {"start": v(-66.16, -98.4) * mm, "end": v(-65.95, -98.25) * mm});
            skLineSegment(sketch, "E2728", {"start": v(-65.95, -98.25) * mm, "end": v(-65.74, -98.11) * mm});
            skLineSegment(sketch, "E2729", {"start": v(-65.74, -98.11) * mm, "end": v(-64.7, -98.5) * mm});
            skLineSegment(sketch, "E2730", {"start": v(-64.7, -98.5) * mm, "end": v(-63.91, -99.3) * mm});
            skLineSegment(sketch, "E2731", {"start": v(-63.91, -99.3) * mm, "end": v(-63.95, -99.55) * mm});
            skLineSegment(sketch, "E2732", {"start": v(-63.95, -99.55) * mm, "end": v(-64, -99.8) * mm});
            skLineSegment(sketch, "E2733", {"start": v(-64, -99.8) * mm, "end": v(-64.03, -100.06) * mm});
            skLineSegment(sketch, "E2734", {"start": v(-64.03, -100.06) * mm, "end": v(-64.07, -100.32) * mm});
            skLineSegment(sketch, "E2735", {"start": v(-64.07, -100.32) * mm, "end": v(-64.11, -100.58) * mm});
            skLineSegment(sketch, "E2736", {"start": v(-64.11, -100.58) * mm, "end": v(-64.15, -100.85) * mm});
            skLineSegment(sketch, "E2737", {"start": v(-64.15, -100.85) * mm, "end": v(-64.19, -101.12) * mm});
            skLineSegment(sketch, "E2738", {"start": v(-64.19, -101.12) * mm, "end": v(-64.22, -101.39) * mm});
            skLineSegment(sketch, "E2739", {"start": v(-64.22, -101.39) * mm, "end": v(-64.26, -101.66) * mm});
            skLineSegment(sketch, "E2740", {"start": v(-64.26, -101.66) * mm, "end": v(-64.29, -101.94) * mm});
            skLineSegment(sketch, "E2741", {"start": v(-64.29, -101.94) * mm, "end": v(-64.32, -102.23) * mm});
            skLineSegment(sketch, "E2742", {"start": v(-64.32, -102.23) * mm, "end": v(-64.35, -102.51) * mm});
            skLineSegment(sketch, "E2743", {"start": v(-64.35, -102.51) * mm, "end": v(-64.38, -102.8) * mm});
            skLineSegment(sketch, "E2744", {"start": v(-64.38, -102.8) * mm, "end": v(-64.41, -103.1) * mm});
            skLineSegment(sketch, "E2745", {"start": v(-64.41, -103.1) * mm, "end": v(-64.44, -103.4) * mm});
            skLineSegment(sketch, "E2746", {"start": v(-64.44, -103.4) * mm, "end": v(-64.46, -103.7) * mm});
            skLineSegment(sketch, "E2747", {"start": v(-64.46, -103.7) * mm, "end": v(-64.49, -104) * mm});
            skLineSegment(sketch, "E2748", {"start": v(-64.49, -104) * mm, "end": v(-64.51, -104.3) * mm});
            skLineSegment(sketch, "E2749", {"start": v(-64.51, -104.3) * mm, "end": v(-64.53, -104.62) * mm});
            skLineSegment(sketch, "E2750", {"start": v(-64.53, -104.62) * mm, "end": v(-64.55, -104.93) * mm});
            skLineSegment(sketch, "E2751", {"start": v(-64.55, -104.93) * mm, "end": v(-64.57, -105.25) * mm});
            skLineSegment(sketch, "E2752", {"start": v(-64.57, -105.25) * mm, "end": v(-64.59, -105.57) * mm});
            skLineSegment(sketch, "E2753", {"start": v(-64.59, -105.57) * mm, "end": v(-64.6, -105.9) * mm});
            skLineSegment(sketch, "E2754", {"start": v(-64.6, -105.9) * mm, "end": v(-64.62, -106.22) * mm});
            skLineSegment(sketch, "E2755", {"start": v(-64.62, -106.22) * mm, "end": v(-64.63, -106.55) * mm});
            skLineSegment(sketch, "E2756", {"start": v(-64.63, -106.55) * mm, "end": v(-64.64, -106.88) * mm});
            skLineSegment(sketch, "E2757", {"start": v(-64.64, -106.88) * mm, "end": v(-64.65, -107.22) * mm});
            skLineSegment(sketch, "E2758", {"start": v(-64.65, -107.22) * mm, "end": v(-64.66, -107.56) * mm});
            skLineSegment(sketch, "E2759", {"start": v(-64.66, -107.56) * mm, "end": v(-64.66, -107.9) * mm});
            skLineSegment(sketch, "E2760", {"start": v(-64.66, -107.9) * mm, "end": v(-64.66, -108.25) * mm});
            skLineSegment(sketch, "E2761", {"start": v(-64.66, -108.25) * mm, "end": v(-64.52, -108.35) * mm});
            skLineSegment(sketch, "E2762", {"start": v(-64.52, -108.35) * mm, "end": v(-63.27, -109.08) * mm});
            skLineSegment(sketch, "E2763", {"start": v(-63.27, -109.08) * mm, "end": v(-63.1, -109.16) * mm});
            skLineSegment(sketch, "E2764", {"start": v(-63.1, -109.16) * mm, "end": v(-62.8, -108.98) * mm});
            skLineSegment(sketch, "E2765", {"start": v(-62.8, -108.98) * mm, "end": v(-62.51, -108.8) * mm});
            skLineSegment(sketch, "E2766", {"start": v(-62.51, -108.8) * mm, "end": v(-62.22, -108.64) * mm});
            skLineSegment(sketch, "E2767", {"start": v(-62.22, -108.64) * mm, "end": v(-61.93, -108.46) * mm});
            skLineSegment(sketch, "E2768", {"start": v(-61.93, -108.46) * mm, "end": v(-61.64, -108.29) * mm});
            skLineSegment(sketch, "E2769", {"start": v(-61.64, -108.29) * mm, "end": v(-61.36, -108.11) * mm});
            skLineSegment(sketch, "E2770", {"start": v(-61.36, -108.11) * mm, "end": v(-61.08, -107.94) * mm});
            skLineSegment(sketch, "E2771", {"start": v(-61.08, -107.94) * mm, "end": v(-60.81, -107.77) * mm});
            skLineSegment(sketch, "E2772", {"start": v(-60.81, -107.77) * mm, "end": v(-60.54, -107.6) * mm});
            skLineSegment(sketch, "E2773", {"start": v(-60.54, -107.6) * mm, "end": v(-60.27, -107.42) * mm});
            skLineSegment(sketch, "E2774", {"start": v(-60.27, -107.42) * mm, "end": v(-60.01, -107.25) * mm});
            skLineSegment(sketch, "E2775", {"start": v(-60.01, -107.25) * mm, "end": v(-59.75, -107.08) * mm});
            skLineSegment(sketch, "E2776", {"start": v(-59.75, -107.08) * mm, "end": v(-59.5, -106.9) * mm});
            skLineSegment(sketch, "E2777", {"start": v(-59.5, -106.9) * mm, "end": v(-59.24, -106.73) * mm});
            skLineSegment(sketch, "E2778", {"start": v(-59.24, -106.73) * mm, "end": v(-59, -106.56) * mm});
            skLineSegment(sketch, "E2779", {"start": v(-59, -106.56) * mm, "end": v(-58.75, -106.4) * mm});
            skLineSegment(sketch, "E2780", {"start": v(-58.75, -106.4) * mm, "end": v(-58.51, -106.22) * mm});
            skLineSegment(sketch, "E2781", {"start": v(-58.51, -106.22) * mm, "end": v(-58.27, -106.05) * mm});
            skLineSegment(sketch, "E2782", {"start": v(-58.27, -106.05) * mm, "end": v(-58.04, -105.88) * mm});
            skLineSegment(sketch, "E2783", {"start": v(-58.04, -105.88) * mm, "end": v(-57.8, -105.72) * mm});
            skLineSegment(sketch, "E2784", {"start": v(-57.8, -105.72) * mm, "end": v(-57.58, -105.55) * mm});
            skLineSegment(sketch, "E2785", {"start": v(-57.58, -105.55) * mm, "end": v(-57.36, -105.38) * mm});
            skLineSegment(sketch, "E2786", {"start": v(-57.36, -105.38) * mm, "end": v(-57.14, -105.22) * mm});
            skLineSegment(sketch, "E2787", {"start": v(-57.14, -105.22) * mm, "end": v(-56.92, -105.05) * mm});
            skLineSegment(sketch, "E2788", {"start": v(-56.92, -105.05) * mm, "end": v(-56.7, -104.89) * mm});
            skLineSegment(sketch, "E2789", {"start": v(-56.7, -104.89) * mm, "end": v(-56.5, -104.72) * mm});
            skLineSegment(sketch, "E2790", {"start": v(-56.5, -104.72) * mm, "end": v(-56.3, -104.56) * mm});
            skLineSegment(sketch, "E2791", {"start": v(-56.3, -104.56) * mm, "end": v(-56.1, -104.4) * mm});
            skLineSegment(sketch, "E2792", {"start": v(-56.1, -104.4) * mm, "end": v(-55.9, -104.24) * mm});
            skLineSegment(sketch, "E2793", {"start": v(-55.9, -104.24) * mm, "end": v(-55.7, -104.08) * mm});
            skLineSegment(sketch, "E2794", {"start": v(-55.7, -104.08) * mm, "end": v(-54.62, -104.37) * mm});
            skLineSegment(sketch, "E2795", {"start": v(-54.62, -104.37) * mm, "end": v(-53.76, -105.08) * mm});
            skLineSegment(sketch, "E2796", {"start": v(-53.76, -105.08) * mm, "end": v(-53.78, -105.33) * mm});
            skLineSegment(sketch, "E2797", {"start": v(-53.78, -105.33) * mm, "end": v(-53.8, -105.59) * mm});
            skLineSegment(sketch, "E2798", {"start": v(-53.8, -105.59) * mm, "end": v(-53.81, -105.85) * mm});
            skLineSegment(sketch, "E2799", {"start": v(-53.81, -105.85) * mm, "end": v(-53.82, -106.1) * mm});
            skLineSegment(sketch, "E2800", {"start": v(-53.82, -106.1) * mm, "end": v(-53.84, -106.37) * mm});
            skLineSegment(sketch, "E2801", {"start": v(-53.84, -106.37) * mm, "end": v(-53.85, -106.64) * mm});
            skLineSegment(sketch, "E2802", {"start": v(-53.85, -106.64) * mm, "end": v(-53.86, -106.91) * mm});
            skLineSegment(sketch, "E2803", {"start": v(-53.86, -106.91) * mm, "end": v(-53.87, -107.19) * mm});
            skLineSegment(sketch, "E2804", {"start": v(-53.87, -107.19) * mm, "end": v(-53.87, -107.47) * mm});
            skLineSegment(sketch, "E2805", {"start": v(-53.87, -107.47) * mm, "end": v(-53.88, -107.75) * mm});
            skLineSegment(sketch, "E2806", {"start": v(-53.88, -107.75) * mm, "end": v(-53.88, -108.03) * mm});
            skLineSegment(sketch, "E2807", {"start": v(-53.88, -108.03) * mm, "end": v(-53.89, -108.32) * mm});
            skLineSegment(sketch, "E2808", {"start": v(-53.89, -108.32) * mm, "end": v(-53.89, -108.61) * mm});
            skLineSegment(sketch, "E2809", {"start": v(-53.89, -108.61) * mm, "end": v(-53.89, -108.9) * mm});
            skLineSegment(sketch, "E2810", {"start": v(-53.89, -108.9) * mm, "end": v(-53.88, -109.2) * mm});
            skLineSegment(sketch, "E2811", {"start": v(-53.88, -109.2) * mm, "end": v(-53.88, -109.5) * mm});
            skLineSegment(sketch, "E2812", {"start": v(-53.88, -109.5) * mm, "end": v(-53.88, -109.81) * mm});
            skLineSegment(sketch, "E2813", {"start": v(-53.88, -109.81) * mm, "end": v(-53.87, -110.12) * mm});
            skLineSegment(sketch, "E2814", {"start": v(-53.87, -110.12) * mm, "end": v(-53.86, -110.43) * mm});
            skLineSegment(sketch, "E2815", {"start": v(-53.86, -110.43) * mm, "end": v(-53.85, -110.75) * mm});
            skLineSegment(sketch, "E2816", {"start": v(-53.85, -110.75) * mm, "end": v(-53.84, -111.06) * mm});
            skLineSegment(sketch, "E2817", {"start": v(-53.84, -111.06) * mm, "end": v(-53.82, -111.38) * mm});
            skLineSegment(sketch, "E2818", {"start": v(-53.82, -111.38) * mm, "end": v(-53.8, -111.7) * mm});
            skLineSegment(sketch, "E2819", {"start": v(-53.8, -111.7) * mm, "end": v(-53.79, -112.04) * mm});
            skLineSegment(sketch, "E2820", {"start": v(-53.79, -112.04) * mm, "end": v(-53.77, -112.37) * mm});
            skLineSegment(sketch, "E2821", {"start": v(-53.77, -112.37) * mm, "end": v(-53.74, -112.7) * mm});
            skLineSegment(sketch, "E2822", {"start": v(-53.74, -112.7) * mm, "end": v(-53.72, -113.04) * mm});
            skLineSegment(sketch, "E2823", {"start": v(-53.72, -113.04) * mm, "end": v(-53.7, -113.38) * mm});
            skLineSegment(sketch, "E2824", {"start": v(-53.7, -113.38) * mm, "end": v(-53.66, -113.72) * mm});
            skLineSegment(sketch, "E2825", {"start": v(-53.66, -113.72) * mm, "end": v(-53.63, -114.06) * mm});
            skLineSegment(sketch, "E2826", {"start": v(-53.63, -114.06) * mm, "end": v(-53.48, -114.15) * mm});
            skLineSegment(sketch, "E2827", {"start": v(-53.48, -114.15) * mm, "end": v(-52.16, -114.75) * mm});
            skLineSegment(sketch, "E2828", {"start": v(-52.16, -114.75) * mm, "end": v(-52, -114.81) * mm});
            skLineSegment(sketch, "E2829", {"start": v(-52, -114.81) * mm, "end": v(-51.71, -114.61) * mm});
            skLineSegment(sketch, "E2830", {"start": v(-51.71, -114.61) * mm, "end": v(-51.44, -114.4) * mm});
            skLineSegment(sketch, "E2831", {"start": v(-51.44, -114.4) * mm, "end": v(-51.16, -114.2) * mm});
            skLineSegment(sketch, "E2832", {"start": v(-51.16, -114.2) * mm, "end": v(-50.9, -114) * mm});
            skLineSegment(sketch, "E2833", {"start": v(-50.9, -114) * mm, "end": v(-50.62, -113.8) * mm});
            skLineSegment(sketch, "E2834", {"start": v(-50.62, -113.8) * mm, "end": v(-50.36, -113.6) * mm});
            skLineSegment(sketch, "E2835", {"start": v(-50.36, -113.6) * mm, "end": v(-50.1, -113.4) * mm});
            skLineSegment(sketch, "E2836", {"start": v(-50.1, -113.4) * mm, "end": v(-49.85, -113.2) * mm});
            skLineSegment(sketch, "E2837", {"start": v(-49.85, -113.2) * mm, "end": v(-49.6, -113) * mm});
            skLineSegment(sketch, "E2838", {"start": v(-49.6, -113) * mm, "end": v(-49.35, -112.8) * mm});
            skLineSegment(sketch, "E2839", {"start": v(-49.35, -112.8) * mm, "end": v(-49.1, -112.6) * mm});
            skLineSegment(sketch, "E2840", {"start": v(-49.1, -112.6) * mm, "end": v(-48.86, -112.41) * mm});
            skLineSegment(sketch, "E2841", {"start": v(-48.86, -112.41) * mm, "end": v(-48.62, -112.22) * mm});
            skLineSegment(sketch, "E2842", {"start": v(-48.62, -112.22) * mm, "end": v(-48.39, -112.02) * mm});
            skLineSegment(sketch, "E2843", {"start": v(-48.39, -112.02) * mm, "end": v(-48.16, -111.83) * mm});
            skLineSegment(sketch, "E2844", {"start": v(-48.16, -111.83) * mm, "end": v(-47.93, -111.63) * mm});
            skLineSegment(sketch, "E2845", {"start": v(-47.93, -111.63) * mm, "end": v(-47.7, -111.44) * mm});
            skLineSegment(sketch, "E2846", {"start": v(-47.7, -111.44) * mm, "end": v(-47.49, -111.25) * mm});
            skLineSegment(sketch, "E2847", {"start": v(-47.49, -111.25) * mm, "end": v(-47.27, -111.06) * mm});
            skLineSegment(sketch, "E2848", {"start": v(-47.27, -111.06) * mm, "end": v(-47.06, -110.87) * mm});
            skLineSegment(sketch, "E2849", {"start": v(-47.06, -110.87) * mm, "end": v(-46.85, -110.68) * mm});
            skLineSegment(sketch, "E2850", {"start": v(-46.85, -110.68) * mm, "end": v(-46.64, -110.5) * mm});
            skLineSegment(sketch, "E2851", {"start": v(-46.64, -110.5) * mm, "end": v(-46.44, -110.3) * mm});
            skLineSegment(sketch, "E2852", {"start": v(-46.44, -110.3) * mm, "end": v(-46.24, -110.12) * mm});
            skLineSegment(sketch, "E2853", {"start": v(-46.24, -110.12) * mm, "end": v(-46.05, -109.93) * mm});
            skLineSegment(sketch, "E2854", {"start": v(-46.05, -109.93) * mm, "end": v(-45.85, -109.75) * mm});
            skLineSegment(sketch, "E2855", {"start": v(-45.85, -109.75) * mm, "end": v(-45.67, -109.57) * mm});
            skLineSegment(sketch, "E2856", {"start": v(-45.67, -109.57) * mm, "end": v(-45.48, -109.39) * mm});
            skLineSegment(sketch, "E2857", {"start": v(-45.48, -109.39) * mm, "end": v(-45.3, -109.2) * mm});
            skLineSegment(sketch, "E2858", {"start": v(-45.3, -109.2) * mm, "end": v(-45.12, -109.03) * mm});
            skLineSegment(sketch, "E2859", {"start": v(-45.12, -109.03) * mm, "end": v(-44.02, -109.22) * mm});
            skLineSegment(sketch, "E2860", {"start": v(-44.02, -109.22) * mm, "end": v(-43.1, -109.84) * mm});
            skLineSegment(sketch, "E2861", {"start": v(-43.1, -109.84) * mm, "end": v(-43.09, -110.1) * mm});
            skLineSegment(sketch, "E2862", {"start": v(-43.09, -110.1) * mm, "end": v(-43.08, -110.35) * mm});
            skLineSegment(sketch, "E2863", {"start": v(-43.08, -110.35) * mm, "end": v(-43.07, -110.6) * mm});
            skLineSegment(sketch, "E2864", {"start": v(-43.07, -110.6) * mm, "end": v(-43.06, -110.87) * mm});
            skLineSegment(sketch, "E2865", {"start": v(-43.06, -110.87) * mm, "end": v(-43.04, -111.13) * mm});
            skLineSegment(sketch, "E2866", {"start": v(-43.04, -111.13) * mm, "end": v(-43.03, -111.4) * mm});
            skLineSegment(sketch, "E2867", {"start": v(-43.03, -111.4) * mm, "end": v(-43.01, -111.67) * mm});
            skLineSegment(sketch, "E2868", {"start": v(-43.01, -111.67) * mm, "end": v(-43, -111.95) * mm});
            skLineSegment(sketch, "E2869", {"start": v(-43, -111.95) * mm, "end": v(-42.97, -112.23) * mm});
            skLineSegment(sketch, "E2870", {"start": v(-42.97, -112.23) * mm, "end": v(-42.95, -112.5) * mm});
            skLineSegment(sketch, "E2871", {"start": v(-42.95, -112.5) * mm, "end": v(-42.93, -112.8) * mm});
            skLineSegment(sketch, "E2872", {"start": v(-42.93, -112.8) * mm, "end": v(-42.9, -113.08) * mm});
            skLineSegment(sketch, "E2873", {"start": v(-42.9, -113.08) * mm, "end": v(-42.87, -113.37) * mm});
            skLineSegment(sketch, "E2874", {"start": v(-42.87, -113.37) * mm, "end": v(-42.84, -113.66) * mm});
            skLineSegment(sketch, "E2875", {"start": v(-42.84, -113.66) * mm, "end": v(-42.81, -113.96) * mm});
            skLineSegment(sketch, "E2876", {"start": v(-42.81, -113.96) * mm, "end": v(-42.78, -114.26) * mm});
            skLineSegment(sketch, "E2877", {"start": v(-42.78, -114.26) * mm, "end": v(-42.74, -114.56) * mm});
            skLineSegment(sketch, "E2878", {"start": v(-42.74, -114.56) * mm, "end": v(-42.7, -114.87) * mm});
            skLineSegment(sketch, "E2879", {"start": v(-42.7, -114.87) * mm, "end": v(-42.67, -115.18) * mm});
            skLineSegment(sketch, "E2880", {"start": v(-42.67, -115.18) * mm, "end": v(-42.63, -115.49) * mm});
            skLineSegment(sketch, "E2881", {"start": v(-42.63, -115.49) * mm, "end": v(-42.58, -115.8) * mm});
            skLineSegment(sketch, "E2882", {"start": v(-42.58, -115.8) * mm, "end": v(-42.54, -116.12) * mm});
            skLineSegment(sketch, "E2883", {"start": v(-42.54, -116.12) * mm, "end": v(-42.49, -116.44) * mm});
            skLineSegment(sketch, "E2884", {"start": v(-42.49, -116.44) * mm, "end": v(-42.44, -116.76) * mm});
            skLineSegment(sketch, "E2885", {"start": v(-42.44, -116.76) * mm, "end": v(-42.39, -117.09) * mm});
            skLineSegment(sketch, "E2886", {"start": v(-42.39, -117.09) * mm, "end": v(-42.33, -117.42) * mm});
            skLineSegment(sketch, "E2887", {"start": v(-42.33, -117.42) * mm, "end": v(-42.27, -117.75) * mm});
            skLineSegment(sketch, "E2888", {"start": v(-42.27, -117.75) * mm, "end": v(-42.21, -118.09) * mm});
            skLineSegment(sketch, "E2889", {"start": v(-42.21, -118.09) * mm, "end": v(-42.15, -118.43) * mm});
            skLineSegment(sketch, "E2890", {"start": v(-42.15, -118.43) * mm, "end": v(-42.09, -118.77) * mm});
            skLineSegment(sketch, "E2891", {"start": v(-42.09, -118.77) * mm, "end": v(-41.92, -118.84) * mm});
            skLineSegment(sketch, "E2892", {"start": v(-41.92, -118.84) * mm, "end": v(-40.55, -119.3) * mm});
            skLineSegment(sketch, "E2893", {"start": v(-40.55, -119.3) * mm, "end": v(-40.38, -119.35) * mm});
            skLineSegment(sketch, "E2894", {"start": v(-40.38, -119.35) * mm, "end": v(-40.12, -119.12) * mm});
            skLineSegment(sketch, "E2895", {"start": v(-40.12, -119.12) * mm, "end": v(-39.87, -118.9) * mm});
            skLineSegment(sketch, "E2896", {"start": v(-39.87, -118.9) * mm, "end": v(-39.61, -118.67) * mm});
            skLineSegment(sketch, "E2897", {"start": v(-39.61, -118.67) * mm, "end": v(-39.36, -118.44) * mm});
            skLineSegment(sketch, "E2898", {"start": v(-39.36, -118.44) * mm, "end": v(-39.12, -118.21) * mm});
            skLineSegment(sketch, "E2899", {"start": v(-39.12, -118.21) * mm, "end": v(-38.88, -117.99) * mm});
            skLineSegment(sketch, "E2900", {"start": v(-38.88, -117.99) * mm, "end": v(-38.64, -117.76) * mm});
            skLineSegment(sketch, "E2901", {"start": v(-38.64, -117.76) * mm, "end": v(-38.4, -117.54) * mm});
            skLineSegment(sketch, "E2902", {"start": v(-38.4, -117.54) * mm, "end": v(-38.17, -117.32) * mm});
            skLineSegment(sketch, "E2903", {"start": v(-38.17, -117.32) * mm, "end": v(-37.94, -117.1) * mm});
            skLineSegment(sketch, "E2904", {"start": v(-37.94, -117.1) * mm, "end": v(-37.72, -116.87) * mm});
            skLineSegment(sketch, "E2905", {"start": v(-37.72, -116.87) * mm, "end": v(-37.5, -116.65) * mm});
            skLineSegment(sketch, "E2906", {"start": v(-37.5, -116.65) * mm, "end": v(-37.28, -116.44) * mm});
            skLineSegment(sketch, "E2907", {"start": v(-37.28, -116.44) * mm, "end": v(-37.07, -116.22) * mm});
            skLineSegment(sketch, "E2908", {"start": v(-37.07, -116.22) * mm, "end": v(-36.86, -116) * mm});
            skLineSegment(sketch, "E2909", {"start": v(-36.86, -116) * mm, "end": v(-36.65, -115.79) * mm});
            skLineSegment(sketch, "E2910", {"start": v(-36.65, -115.79) * mm, "end": v(-36.45, -115.57) * mm});
            skLineSegment(sketch, "E2911", {"start": v(-36.45, -115.57) * mm, "end": v(-36.25, -115.36) * mm});
            skLineSegment(sketch, "E2912", {"start": v(-36.25, -115.36) * mm, "end": v(-36.05, -115.15) * mm});
            skLineSegment(sketch, "E2913", {"start": v(-36.05, -115.15) * mm, "end": v(-35.86, -114.94) * mm});
            skLineSegment(sketch, "E2914", {"start": v(-35.86, -114.94) * mm, "end": v(-35.67, -114.73) * mm});
            skLineSegment(sketch, "E2915", {"start": v(-35.67, -114.73) * mm, "end": v(-35.48, -114.53) * mm});
            skLineSegment(sketch, "E2916", {"start": v(-35.48, -114.53) * mm, "end": v(-35.3, -114.32) * mm});
            skLineSegment(sketch, "E2917", {"start": v(-35.3, -114.32) * mm, "end": v(-35.12, -114.12) * mm});
            skLineSegment(sketch, "E2918", {"start": v(-35.12, -114.12) * mm, "end": v(-34.94, -113.91) * mm});
            skLineSegment(sketch, "E2919", {"start": v(-34.94, -113.91) * mm, "end": v(-34.77, -113.71) * mm});
            skLineSegment(sketch, "E2920", {"start": v(-34.77, -113.71) * mm, "end": v(-34.6, -113.51) * mm});
            skLineSegment(sketch, "E2921", {"start": v(-34.6, -113.51) * mm, "end": v(-34.43, -113.31) * mm});
            skLineSegment(sketch, "E2922", {"start": v(-34.43, -113.31) * mm, "end": v(-34.27, -113.12) * mm});
            skLineSegment(sketch, "E2923", {"start": v(-34.27, -113.12) * mm, "end": v(-34.1, -112.92) * mm});
            skLineSegment(sketch, "E2924", {"start": v(-34.1, -112.92) * mm, "end": v(-33, -113) * mm});
            skLineSegment(sketch, "E2925", {"start": v(-33, -113) * mm, "end": v(-32.01, -113.53) * mm});
            skLineSegment(sketch, "E2926", {"start": v(-32.01, -113.53) * mm, "end": v(-31.98, -113.78) * mm});
            skLineSegment(sketch, "E2927", {"start": v(-31.98, -113.78) * mm, "end": v(-31.95, -114.03) * mm});
            skLineSegment(sketch, "E2928", {"start": v(-31.95, -114.03) * mm, "end": v(-31.91, -114.29) * mm});
            skLineSegment(sketch, "E2929", {"start": v(-31.91, -114.29) * mm, "end": v(-31.87, -114.55) * mm});
            skLineSegment(sketch, "E2930", {"start": v(-31.87, -114.55) * mm, "end": v(-31.83, -114.81) * mm});
            skLineSegment(sketch, "E2931", {"start": v(-31.83, -114.81) * mm, "end": v(-31.8, -115.08) * mm});
            skLineSegment(sketch, "E2932", {"start": v(-31.8, -115.08) * mm, "end": v(-31.75, -115.35) * mm});
            skLineSegment(sketch, "E2933", {"start": v(-31.75, -115.35) * mm, "end": v(-31.7, -115.62) * mm});
            skLineSegment(sketch, "E2934", {"start": v(-31.7, -115.62) * mm, "end": v(-31.66, -115.9) * mm});
            skLineSegment(sketch, "E2935", {"start": v(-31.66, -115.9) * mm, "end": v(-31.6, -116.17) * mm});
            skLineSegment(sketch, "E2936", {"start": v(-31.6, -116.17) * mm, "end": v(-31.56, -116.45) * mm});
            skLineSegment(sketch, "E2937", {"start": v(-31.56, -116.45) * mm, "end": v(-31.5, -116.73) * mm});
            skLineSegment(sketch, "E2938", {"start": v(-31.5, -116.73) * mm, "end": v(-31.45, -117.02) * mm});
            skLineSegment(sketch, "E2939", {"start": v(-31.45, -117.02) * mm, "end": v(-31.39, -117.3) * mm});
            skLineSegment(sketch, "E2940", {"start": v(-31.39, -117.3) * mm, "end": v(-31.33, -117.6) * mm});
            skLineSegment(sketch, "E2941", {"start": v(-31.33, -117.6) * mm, "end": v(-31.27, -117.9) * mm});
            skLineSegment(sketch, "E2942", {"start": v(-31.27, -117.9) * mm, "end": v(-31.2, -118.2) * mm});
            skLineSegment(sketch, "E2943", {"start": v(-31.2, -118.2) * mm, "end": v(-31.13, -118.5) * mm});
            skLineSegment(sketch, "E2944", {"start": v(-31.13, -118.5) * mm, "end": v(-31.06, -118.8) * mm});
            skLineSegment(sketch, "E2945", {"start": v(-31.06, -118.8) * mm, "end": v(-31, -119.1) * mm});
            skLineSegment(sketch, "E2946", {"start": v(-31, -119.1) * mm, "end": v(-30.92, -119.41) * mm});
            skLineSegment(sketch, "E2947", {"start": v(-30.92, -119.41) * mm, "end": v(-30.84, -119.72) * mm});
            skLineSegment(sketch, "E2948", {"start": v(-30.84, -119.72) * mm, "end": v(-30.76, -120.04) * mm});
            skLineSegment(sketch, "E2949", {"start": v(-30.76, -120.04) * mm, "end": v(-30.68, -120.36) * mm});
            skLineSegment(sketch, "E2950", {"start": v(-30.68, -120.36) * mm, "end": v(-30.6, -120.68) * mm});
            skLineSegment(sketch, "E2951", {"start": v(-30.6, -120.68) * mm, "end": v(-30.5, -121) * mm});
            skLineSegment(sketch, "E2952", {"start": v(-30.5, -121) * mm, "end": v(-30.42, -121.32) * mm});
            skLineSegment(sketch, "E2953", {"start": v(-30.42, -121.32) * mm, "end": v(-30.33, -121.65) * mm});
            skLineSegment(sketch, "E2954", {"start": v(-30.33, -121.65) * mm, "end": v(-30.23, -121.98) * mm});
            skLineSegment(sketch, "E2955", {"start": v(-30.23, -121.98) * mm, "end": v(-30.13, -122.31) * mm});
            skLineSegment(sketch, "E2956", {"start": v(-30.13, -122.31) * mm, "end": v(-29.97, -122.37) * mm});
            skLineSegment(sketch, "E2957", {"start": v(-29.97, -122.37) * mm, "end": v(-28.56, -122.7) * mm});
            skLineSegment(sketch, "E2958", {"start": v(-28.56, -122.7) * mm, "end": v(-28.38, -122.73) * mm});
            skLineSegment(sketch, "E2959", {"start": v(-28.38, -122.73) * mm, "end": v(-28.14, -122.48) * mm});
            skLineSegment(sketch, "E2960", {"start": v(-28.14, -122.48) * mm, "end": v(-27.91, -122.22) * mm});
            skLineSegment(sketch, "E2961", {"start": v(-27.91, -122.22) * mm, "end": v(-27.68, -121.97) * mm});
            skLineSegment(sketch, "E2962", {"start": v(-27.68, -121.97) * mm, "end": v(-27.46, -121.72) * mm});
            skLineSegment(sketch, "E2963", {"start": v(-27.46, -121.72) * mm, "end": v(-27.23, -121.47) * mm});
            skLineSegment(sketch, "E2964", {"start": v(-27.23, -121.47) * mm, "end": v(-27.01, -121.22) * mm});
            skLineSegment(sketch, "E2965", {"start": v(-27.01, -121.22) * mm, "end": v(-26.8, -120.98) * mm});
            skLineSegment(sketch, "E2966", {"start": v(-26.8, -120.98) * mm, "end": v(-26.59, -120.73) * mm});
            skLineSegment(sketch, "E2967", {"start": v(-26.59, -120.73) * mm, "end": v(-26.38, -120.49) * mm});
            skLineSegment(sketch, "E2968", {"start": v(-26.38, -120.49) * mm, "end": v(-26.17, -120.24) * mm});
            skLineSegment(sketch, "E2969", {"start": v(-26.17, -120.24) * mm, "end": v(-25.97, -120) * mm});
            skLineSegment(sketch, "E2970", {"start": v(-25.97, -120) * mm, "end": v(-25.78, -119.76) * mm});
            skLineSegment(sketch, "E2971", {"start": v(-25.78, -119.76) * mm, "end": v(-25.58, -119.52) * mm});
            skLineSegment(sketch, "E2972", {"start": v(-25.58, -119.52) * mm, "end": v(-25.39, -119.29) * mm});
            skLineSegment(sketch, "E2973", {"start": v(-25.39, -119.29) * mm, "end": v(-25.2, -119.05) * mm});
            skLineSegment(sketch, "E2974", {"start": v(-25.2, -119.05) * mm, "end": v(-25.02, -118.82) * mm});
            skLineSegment(sketch, "E2975", {"start": v(-25.02, -118.82) * mm, "end": v(-24.83, -118.58) * mm});
            skLineSegment(sketch, "E2976", {"start": v(-24.83, -118.58) * mm, "end": v(-24.66, -118.35) * mm});
            skLineSegment(sketch, "E2977", {"start": v(-24.66, -118.35) * mm, "end": v(-24.48, -118.12) * mm});
            skLineSegment(sketch, "E2978", {"start": v(-24.48, -118.12) * mm, "end": v(-24.3, -117.9) * mm});
            skLineSegment(sketch, "E2979", {"start": v(-24.3, -117.9) * mm, "end": v(-24.14, -117.67) * mm});
            skLineSegment(sketch, "E2980", {"start": v(-24.14, -117.67) * mm, "end": v(-23.98, -117.45) * mm});
            skLineSegment(sketch, "E2981", {"start": v(-23.98, -117.45) * mm, "end": v(-23.81, -117.22) * mm});
            skLineSegment(sketch, "E2982", {"start": v(-23.81, -117.22) * mm, "end": v(-23.65, -117) * mm});
            skLineSegment(sketch, "E2983", {"start": v(-23.65, -117) * mm, "end": v(-23.5, -116.78) * mm});
            skLineSegment(sketch, "E2984", {"start": v(-23.5, -116.78) * mm, "end": v(-23.35, -116.57) * mm});
            skLineSegment(sketch, "E2985", {"start": v(-23.35, -116.57) * mm, "end": v(-23.2, -116.35) * mm});
            skLineSegment(sketch, "E2986", {"start": v(-23.2, -116.35) * mm, "end": v(-23.05, -116.14) * mm});
            skLineSegment(sketch, "E2987", {"start": v(-23.05, -116.14) * mm, "end": v(-22.9, -115.93) * mm});
            skLineSegment(sketch, "E2988", {"start": v(-22.9, -115.93) * mm, "end": v(-22.76, -115.72) * mm});
            skLineSegment(sketch, "E2989", {"start": v(-22.76, -115.72) * mm, "end": v(-21.65, -115.68) * mm});
            skLineSegment(sketch, "E2990", {"start": v(-21.65, -115.68) * mm, "end": v(-20.62, -116.12) * mm});
            skLineSegment(sketch, "E2991", {"start": v(-20.62, -116.12) * mm, "end": v(-20.57, -116.36) * mm});
            skLineSegment(sketch, "E2992", {"start": v(-20.57, -116.36) * mm, "end": v(-20.5, -116.61) * mm});
            skLineSegment(sketch, "E2993", {"start": v(-20.5, -116.61) * mm, "end": v(-20.45, -116.86) * mm});
            skLineSegment(sketch, "E2994", {"start": v(-20.45, -116.86) * mm, "end": v(-20.38, -117.12) * mm});
            skLineSegment(sketch, "E2995", {"start": v(-20.38, -117.12) * mm, "end": v(-20.32, -117.37) * mm});
            skLineSegment(sketch, "E2996", {"start": v(-20.32, -117.37) * mm, "end": v(-20.25, -117.63) * mm});
            skLineSegment(sketch, "E2997", {"start": v(-20.25, -117.63) * mm, "end": v(-20.18, -117.9) * mm});
            skLineSegment(sketch, "E2998", {"start": v(-20.18, -117.9) * mm, "end": v(-20.11, -118.16) * mm});
            skLineSegment(sketch, "E2999", {"start": v(-20.11, -118.16) * mm, "end": v(-20.04, -118.43) * mm});
            skLineSegment(sketch, "E3000", {"start": v(-20.04, -118.43) * mm, "end": v(-19.96, -118.7) * mm});
            skLineSegment(sketch, "E3001", {"start": v(-19.96, -118.7) * mm, "end": v(-19.88, -118.98) * mm});
            skLineSegment(sketch, "E3002", {"start": v(-19.88, -118.98) * mm, "end": v(-19.8, -119.25) * mm});
            skLineSegment(sketch, "E3003", {"start": v(-19.8, -119.25) * mm, "end": v(-19.72, -119.53) * mm});
            skLineSegment(sketch, "E3004", {"start": v(-19.72, -119.53) * mm, "end": v(-19.63, -119.81) * mm});
            skLineSegment(sketch, "E3005", {"start": v(-19.63, -119.81) * mm, "end": v(-19.54, -120.1) * mm});
            skLineSegment(sketch, "E3006", {"start": v(-19.54, -120.1) * mm, "end": v(-19.45, -120.39) * mm});
            skLineSegment(sketch, "E3007", {"start": v(-19.45, -120.39) * mm, "end": v(-19.36, -120.68) * mm});
            skLineSegment(sketch, "E3008", {"start": v(-19.36, -120.68) * mm, "end": v(-19.26, -120.97) * mm});
            skLineSegment(sketch, "E3009", {"start": v(-19.26, -120.97) * mm, "end": v(-19.16, -121.26) * mm});
            skLineSegment(sketch, "E3010", {"start": v(-19.16, -121.26) * mm, "end": v(-19.06, -121.56) * mm});
            skLineSegment(sketch, "E3011", {"start": v(-19.06, -121.56) * mm, "end": v(-18.96, -121.86) * mm});
            skLineSegment(sketch, "E3012", {"start": v(-18.96, -121.86) * mm, "end": v(-18.85, -122.16) * mm});
            skLineSegment(sketch, "E3013", {"start": v(-18.85, -122.16) * mm, "end": v(-18.74, -122.47) * mm});
            skLineSegment(sketch, "E3014", {"start": v(-18.74, -122.47) * mm, "end": v(-18.63, -122.78) * mm});
            skLineSegment(sketch, "E3015", {"start": v(-18.63, -122.78) * mm, "end": v(-18.51, -123.09) * mm});
            skLineSegment(sketch, "E3016", {"start": v(-18.51, -123.09) * mm, "end": v(-18.4, -123.4) * mm});
            skLineSegment(sketch, "E3017", {"start": v(-18.4, -123.4) * mm, "end": v(-18.27, -123.72) * mm});
            skLineSegment(sketch, "E3018", {"start": v(-18.27, -123.72) * mm, "end": v(-18.15, -124.03) * mm});
            skLineSegment(sketch, "E3019", {"start": v(-18.15, -124.03) * mm, "end": v(-18.02, -124.35) * mm});
            skLineSegment(sketch, "E3020", {"start": v(-18.02, -124.35) * mm, "end": v(-17.9, -124.67) * mm});
            skLineSegment(sketch, "E3021", {"start": v(-17.9, -124.67) * mm, "end": v(-17.72, -124.71) * mm});
            skLineSegment(sketch, "E3022", {"start": v(-17.72, -124.71) * mm, "end": v(-16.28, -124.9) * mm});
            skLineSegment(sketch, "E3023", {"start": v(-16.28, -124.9) * mm, "end": v(-16.1, -124.91) * mm});
            skLineSegment(sketch, "E3024", {"start": v(-16.1, -124.91) * mm, "end": v(-15.9, -124.64) * mm});
            skLineSegment(sketch, "E3025", {"start": v(-15.9, -124.64) * mm, "end": v(-15.69, -124.36) * mm});
            skLineSegment(sketch, "E3026", {"start": v(-15.69, -124.36) * mm, "end": v(-15.49, -124.1) * mm});
            skLineSegment(sketch, "E3027", {"start": v(-15.49, -124.1) * mm, "end": v(-15.28, -123.82) * mm});
            skLineSegment(sketch, "E3028", {"start": v(-15.28, -123.82) * mm, "end": v(-15.09, -123.55) * mm});
            skLineSegment(sketch, "E3029", {"start": v(-15.09, -123.55) * mm, "end": v(-14.9, -123.28) * mm});
            skLineSegment(sketch, "E3030", {"start": v(-14.9, -123.28) * mm, "end": v(-14.7, -123.02) * mm});
            skLineSegment(sketch, "E3031", {"start": v(-14.7, -123.02) * mm, "end": v(-14.52, -122.75) * mm});
            skLineSegment(sketch, "E3032", {"start": v(-14.52, -122.75) * mm, "end": v(-14.33, -122.49) * mm});
            skLineSegment(sketch, "E3033", {"start": v(-14.33, -122.49) * mm, "end": v(-14.15, -122.23) * mm});
            skLineSegment(sketch, "E3034", {"start": v(-14.15, -122.23) * mm, "end": v(-13.98, -121.96) * mm});
            skLineSegment(sketch, "E3035", {"start": v(-13.98, -121.96) * mm, "end": v(-13.8, -121.7) * mm});
            skLineSegment(sketch, "E3036", {"start": v(-13.8, -121.7) * mm, "end": v(-13.63, -121.45) * mm});
            skLineSegment(sketch, "E3037", {"start": v(-13.63, -121.45) * mm, "end": v(-13.47, -121.2) * mm});
            skLineSegment(sketch, "E3038", {"start": v(-13.47, -121.2) * mm, "end": v(-13.3, -120.94) * mm});
            skLineSegment(sketch, "E3039", {"start": v(-13.3, -120.94) * mm, "end": v(-13.14, -120.7) * mm});
            skLineSegment(sketch, "E3040", {"start": v(-13.14, -120.7) * mm, "end": v(-12.98, -120.44) * mm});
            skLineSegment(sketch, "E3041", {"start": v(-12.98, -120.44) * mm, "end": v(-12.83, -120.2) * mm});
            skLineSegment(sketch, "E3042", {"start": v(-12.83, -120.2) * mm, "end": v(-12.68, -119.95) * mm});
            skLineSegment(sketch, "E3043", {"start": v(-12.68, -119.95) * mm, "end": v(-12.53, -119.7) * mm});
            skLineSegment(sketch, "E3044", {"start": v(-12.53, -119.7) * mm, "end": v(-12.38, -119.46) * mm});
            skLineSegment(sketch, "E3045", {"start": v(-12.38, -119.46) * mm, "end": v(-12.24, -119.23) * mm});
            skLineSegment(sketch, "E3046", {"start": v(-12.24, -119.23) * mm, "end": v(-12.1, -118.99) * mm});
            skLineSegment(sketch, "E3047", {"start": v(-12.1, -118.99) * mm, "end": v(-11.96, -118.75) * mm});
            skLineSegment(sketch, "E3048", {"start": v(-11.96, -118.75) * mm, "end": v(-11.83, -118.52) * mm});
            skLineSegment(sketch, "E3049", {"start": v(-11.83, -118.52) * mm, "end": v(-11.7, -118.29) * mm});
            skLineSegment(sketch, "E3050", {"start": v(-11.7, -118.29) * mm, "end": v(-11.57, -118.06) * mm});
            skLineSegment(sketch, "E3051", {"start": v(-11.57, -118.06) * mm, "end": v(-11.45, -117.83) * mm});
            skLineSegment(sketch, "E3052", {"start": v(-11.45, -117.83) * mm, "end": v(-11.32, -117.6) * mm});
            skLineSegment(sketch, "E3053", {"start": v(-11.32, -117.6) * mm, "end": v(-11.2, -117.39) * mm});
            skLineSegment(sketch, "E3054", {"start": v(-11.2, -117.39) * mm, "end": v(-10.1, -117.24) * mm});
            skLineSegment(sketch, "E3055", {"start": v(-10.1, -117.24) * mm, "end": v(-9.03, -117.57) * mm});
            skLineSegment(sketch, "E3056", {"start": v(-9.03, -117.57) * mm, "end": v(-8.95, -117.81) * mm});
            skLineSegment(sketch, "E3057", {"start": v(-8.95, -117.81) * mm, "end": v(-8.87, -118.05) * mm});
            skLineSegment(sketch, "E3058", {"start": v(-8.87, -118.05) * mm, "end": v(-8.79, -118.3) * mm});
            skLineSegment(sketch, "E3059", {"start": v(-8.79, -118.3) * mm, "end": v(-8.7, -118.54) * mm});
            skLineSegment(sketch, "E3060", {"start": v(-8.7, -118.54) * mm, "end": v(-8.6, -118.8) * mm});
            skLineSegment(sketch, "E3061", {"start": v(-8.6, -118.8) * mm, "end": v(-8.52, -119.05) * mm});
            skLineSegment(sketch, "E3062", {"start": v(-8.52, -119.05) * mm, "end": v(-8.42, -119.3) * mm});
            skLineSegment(sketch, "E3063", {"start": v(-8.42, -119.3) * mm, "end": v(-8.32, -119.56) * mm});
            skLineSegment(sketch, "E3064", {"start": v(-8.32, -119.56) * mm, "end": v(-8.22, -119.82) * mm});
            skLineSegment(sketch, "E3065", {"start": v(-8.22, -119.82) * mm, "end": v(-8.12, -120.08) * mm});
            skLineSegment(sketch, "E3066", {"start": v(-8.12, -120.08) * mm, "end": v(-8.02, -120.35) * mm});
            skLineSegment(sketch, "E3067", {"start": v(-8.02, -120.35) * mm, "end": v(-7.9, -120.62) * mm});
            skLineSegment(sketch, "E3068", {"start": v(-7.9, -120.62) * mm, "end": v(-7.8, -120.88) * mm});
            skLineSegment(sketch, "E3069", {"start": v(-7.8, -120.88) * mm, "end": v(-7.68, -121.16) * mm});
            skLineSegment(sketch, "E3070", {"start": v(-7.68, -121.16) * mm, "end": v(-7.57, -121.43) * mm});
            skLineSegment(sketch, "E3071", {"start": v(-7.57, -121.43) * mm, "end": v(-7.45, -121.7) * mm});
            skLineSegment(sketch, "E3072", {"start": v(-7.45, -121.7) * mm, "end": v(-7.33, -121.99) * mm});
            skLineSegment(sketch, "E3073", {"start": v(-7.33, -121.99) * mm, "end": v(-7.2, -122.27) * mm});
            skLineSegment(sketch, "E3074", {"start": v(-7.2, -122.27) * mm, "end": v(-7.08, -122.55) * mm});
            skLineSegment(sketch, "E3075", {"start": v(-7.08, -122.55) * mm, "end": v(-6.95, -122.84) * mm});
            skLineSegment(sketch, "E3076", {"start": v(-6.95, -122.84) * mm, "end": v(-6.81, -123.13) * mm});
            skLineSegment(sketch, "E3077", {"start": v(-6.81, -123.13) * mm, "end": v(-6.68, -123.42) * mm});
            skLineSegment(sketch, "E3078", {"start": v(-6.68, -123.42) * mm, "end": v(-6.54, -123.71) * mm});
            skLineSegment(sketch, "E3079", {"start": v(-6.54, -123.71) * mm, "end": v(-6.4, -124) * mm});
            skLineSegment(sketch, "E3080", {"start": v(-6.4, -124) * mm, "end": v(-6.25, -124.3) * mm});
            skLineSegment(sketch, "E3081", {"start": v(-6.25, -124.3) * mm, "end": v(-6.1, -124.6) * mm});
            skLineSegment(sketch, "E3082", {"start": v(-6.1, -124.6) * mm, "end": v(-5.95, -124.9) * mm});
            skLineSegment(sketch, "E3083", {"start": v(-5.95, -124.9) * mm, "end": v(-5.8, -125.2) * mm});
            skLineSegment(sketch, "E3084", {"start": v(-5.8, -125.2) * mm, "end": v(-5.64, -125.51) * mm});
            skLineSegment(sketch, "E3085", {"start": v(-5.64, -125.51) * mm, "end": v(-5.48, -125.82) * mm});
            skLineSegment(sketch, "E3086", {"start": v(-5.48, -125.82) * mm, "end": v(-5.3, -125.84) * mm});
            skLineSegment(sketch, "E3087", {"start": v(-5.3, -125.84) * mm, "end": v(-3.85, -125.9) * mm});
            skLineSegment(sketch, "E3088", {"start": v(-3.85, -125.9) * mm, "end": v(-3.68, -125.89) * mm});
            skLineSegment(sketch, "E3089", {"start": v(-3.68, -125.89) * mm, "end": v(-3.5, -125.6) * mm});
            skLineSegment(sketch, "E3090", {"start": v(-3.5, -125.6) * mm, "end": v(-3.31, -125.3) * mm});
            skLineSegment(sketch, "E3091", {"start": v(-3.31, -125.3) * mm, "end": v(-3.14, -125) * mm});
            skLineSegment(sketch, "E3092", {"start": v(-3.14, -125) * mm, "end": v(-2.97, -124.72) * mm});
            skLineSegment(sketch, "E3093", {"start": v(-2.97, -124.72) * mm, "end": v(-2.8, -124.43) * mm});
            skLineSegment(sketch, "E3094", {"start": v(-2.8, -124.43) * mm, "end": v(-2.63, -124.14) * mm});
            skLineSegment(sketch, "E3095", {"start": v(-2.63, -124.14) * mm, "end": v(-2.47, -123.86) * mm});
            skLineSegment(sketch, "E3096", {"start": v(-2.47, -123.86) * mm, "end": v(-2.3, -123.58) * mm});
            skLineSegment(sketch, "E3097", {"start": v(-2.3, -123.58) * mm, "end": v(-2.15, -123.3) * mm});
            skLineSegment(sketch, "E3098", {"start": v(-2.15, -123.3) * mm, "end": v(-2, -123.02) * mm});
            skLineSegment(sketch, "E3099", {"start": v(-2, -123.02) * mm, "end": v(-1.85, -122.74) * mm});
            skLineSegment(sketch, "E3100", {"start": v(-1.85, -122.74) * mm, "end": v(-1.7, -122.47) * mm});
            skLineSegment(sketch, "E3101", {"start": v(-1.7, -122.47) * mm, "end": v(-1.55, -122.2) * mm});
            skLineSegment(sketch, "E3102", {"start": v(-1.55, -122.2) * mm, "end": v(-1.41, -121.93) * mm});
            skLineSegment(sketch, "E3103", {"start": v(-1.41, -121.93) * mm, "end": v(-1.27, -121.66) * mm});
            skLineSegment(sketch, "E3104", {"start": v(-1.27, -121.66) * mm, "end": v(-1.14, -121.4) * mm});
            skLineSegment(sketch, "E3105", {"start": v(-1.14, -121.4) * mm, "end": v(-1, -121.13) * mm});
            skLineSegment(sketch, "E3106", {"start": v(-1, -121.13) * mm, "end": v(-0.88, -120.87) * mm});
            skLineSegment(sketch, "E3107", {"start": v(-0.88, -120.87) * mm, "end": v(-0.75, -120.6) * mm});
            skLineSegment(sketch, "E3108", {"start": v(-0.75, -120.6) * mm, "end": v(-0.63, -120.35) * mm});
            skLineSegment(sketch, "E3109", {"start": v(-0.63, -120.35) * mm, "end": v(-0.5, -120.1) * mm});
            skLineSegment(sketch, "E3110", {"start": v(-0.5, -120.1) * mm, "end": v(-0.39, -119.85) * mm});
            skLineSegment(sketch, "E3111", {"start": v(-0.39, -119.85) * mm, "end": v(-0.27, -119.6) * mm});
            skLineSegment(sketch, "E3112", {"start": v(-0.27, -119.6) * mm, "end": v(-0.16, -119.35) * mm});
            skLineSegment(sketch, "E3113", {"start": v(-0.16, -119.35) * mm, "end": v(-0.05, -119.1) * mm});
            skLineSegment(sketch, "E3114", {"start": v(-0.05, -119.1) * mm, "end": v(0.06, -118.86) * mm});
            skLineSegment(sketch, "E3115", {"start": v(0.06, -118.86) * mm, "end": v(0.17, -118.62) * mm});
            skLineSegment(sketch, "E3116", {"start": v(0.17, -118.62) * mm, "end": v(0.27, -118.38) * mm});
            skLineSegment(sketch, "E3117", {"start": v(0.27, -118.38) * mm, "end": v(0.37, -118.15) * mm});
            skLineSegment(sketch, "E3118", {"start": v(0.37, -118.15) * mm, "end": v(0.46, -117.91) * mm});
            skLineSegment(sketch, "E3119", {"start": v(0.46, -117.91) * mm, "end": v(1.55, -117.66) * mm});
            skLineSegment(sketch, "E3120", {"start": v(1.55, -117.66) * mm, "end": v(2.64, -117.89) * mm});
            skLineSegment(sketch, "E3121", {"start": v(2.64, -117.89) * mm, "end": v(2.75, -118.12) * mm});
            skLineSegment(sketch, "E3122", {"start": v(2.75, -118.12) * mm, "end": v(2.85, -118.35) * mm});
            skLineSegment(sketch, "E3123", {"start": v(2.85, -118.35) * mm, "end": v(2.96, -118.58) * mm});
            skLineSegment(sketch, "E3124", {"start": v(2.96, -118.58) * mm, "end": v(3.07, -118.82) * mm});
            skLineSegment(sketch, "E3125", {"start": v(3.07, -118.82) * mm, "end": v(3.19, -119.06) * mm});
            skLineSegment(sketch, "E3126", {"start": v(3.19, -119.06) * mm, "end": v(3.3, -119.3) * mm});
            skLineSegment(sketch, "E3127", {"start": v(3.3, -119.3) * mm, "end": v(3.42, -119.55) * mm});
            skLineSegment(sketch, "E3128", {"start": v(3.42, -119.55) * mm, "end": v(3.54, -119.8) * mm});
            skLineSegment(sketch, "E3129", {"start": v(3.54, -119.8) * mm, "end": v(3.67, -120.04) * mm});
            skLineSegment(sketch, "E3130", {"start": v(3.67, -120.04) * mm, "end": v(3.8, -120.3) * mm});
            skLineSegment(sketch, "E3131", {"start": v(3.8, -120.3) * mm, "end": v(3.93, -120.55) * mm});
            skLineSegment(sketch, "E3132", {"start": v(3.93, -120.55) * mm, "end": v(4.06, -120.8) * mm});
            skLineSegment(sketch, "E3133", {"start": v(4.06, -120.8) * mm, "end": v(4.2, -121.06) * mm});
            skLineSegment(sketch, "E3134", {"start": v(4.2, -121.06) * mm, "end": v(4.34, -121.32) * mm});
            skLineSegment(sketch, "E3135", {"start": v(4.34, -121.32) * mm, "end": v(4.48, -121.58) * mm});
            skLineSegment(sketch, "E3136", {"start": v(4.48, -121.58) * mm, "end": v(4.62, -121.85) * mm});
            skLineSegment(sketch, "E3137", {"start": v(4.62, -121.85) * mm, "end": v(4.77, -122.11) * mm});
            skLineSegment(sketch, "E3138", {"start": v(4.77, -122.11) * mm, "end": v(4.92, -122.38) * mm});
            skLineSegment(sketch, "E3139", {"start": v(4.92, -122.38) * mm, "end": v(5.08, -122.65) * mm});
            skLineSegment(sketch, "E3140", {"start": v(5.08, -122.65) * mm, "end": v(5.24, -122.92) * mm});
            skLineSegment(sketch, "E3141", {"start": v(5.24, -122.92) * mm, "end": v(5.4, -123.2) * mm});
            skLineSegment(sketch, "E3142", {"start": v(5.4, -123.2) * mm, "end": v(5.56, -123.47) * mm});
            skLineSegment(sketch, "E3143", {"start": v(5.56, -123.47) * mm, "end": v(5.73, -123.75) * mm});
            skLineSegment(sketch, "E3144", {"start": v(5.73, -123.75) * mm, "end": v(5.9, -124.03) * mm});
            skLineSegment(sketch, "E3145", {"start": v(5.9, -124.03) * mm, "end": v(6.07, -124.31) * mm});
            skLineSegment(sketch, "E3146", {"start": v(6.07, -124.31) * mm, "end": v(6.25, -124.6) * mm});
            skLineSegment(sketch, "E3147", {"start": v(6.25, -124.6) * mm, "end": v(6.43, -124.88) * mm});
            skLineSegment(sketch, "E3148", {"start": v(6.43, -124.88) * mm, "end": v(6.61, -125.17) * mm});
            skLineSegment(sketch, "E3149", {"start": v(6.61, -125.17) * mm, "end": v(6.8, -125.46) * mm});
            skLineSegment(sketch, "E3150", {"start": v(6.8, -125.46) * mm, "end": v(7, -125.75) * mm});
            skLineSegment(sketch, "E3151", {"start": v(7, -125.75) * mm, "end": v(7.17, -125.75) * mm});
            skLineSegment(sketch, "E3152", {"start": v(7.17, -125.75) * mm, "end": v(8.61, -125.66) * mm});
            skLineSegment(sketch, "E3153", {"start": v(8.61, -125.66) * mm, "end": v(8.79, -125.64) * mm});
            skLineSegment(sketch, "E3154", {"start": v(8.79, -125.64) * mm, "end": v(8.94, -125.32) * mm});
            skLineSegment(sketch, "E3155", {"start": v(8.94, -125.32) * mm, "end": v(9.1, -125.01) * mm});
            skLineSegment(sketch, "E3156", {"start": v(9.1, -125.01) * mm, "end": v(9.24, -124.7) * mm});
            skLineSegment(sketch, "E3157", {"start": v(9.24, -124.7) * mm, "end": v(9.38, -124.4) * mm});
            skLineSegment(sketch, "E3158", {"start": v(9.38, -124.4) * mm, "end": v(9.52, -124.1) * mm});
            skLineSegment(sketch, "E3159", {"start": v(9.52, -124.1) * mm, "end": v(9.66, -123.8) * mm});
            skLineSegment(sketch, "E3160", {"start": v(9.66, -123.8) * mm, "end": v(9.8, -123.5) * mm});
            skLineSegment(sketch, "E3161", {"start": v(9.8, -123.5) * mm, "end": v(9.92, -123.2) * mm});
            skLineSegment(sketch, "E3162", {"start": v(9.92, -123.2) * mm, "end": v(10.05, -122.9) * mm});
            skLineSegment(sketch, "E3163", {"start": v(10.05, -122.9) * mm, "end": v(10.18, -122.62) * mm});
            skLineSegment(sketch, "E3164", {"start": v(10.18, -122.62) * mm, "end": v(10.3, -122.33) * mm});
            skLineSegment(sketch, "E3165", {"start": v(10.3, -122.33) * mm, "end": v(10.42, -122.04) * mm});
            skLineSegment(sketch, "E3166", {"start": v(10.42, -122.04) * mm, "end": v(10.54, -121.75) * mm});
            skLineSegment(sketch, "E3167", {"start": v(10.54, -121.75) * mm, "end": v(10.65, -121.47) * mm});
            skLineSegment(sketch, "E3168", {"start": v(10.65, -121.47) * mm, "end": v(10.76, -121.2) * mm});
            skLineSegment(sketch, "E3169", {"start": v(10.76, -121.2) * mm, "end": v(10.87, -120.92) * mm});
            skLineSegment(sketch, "E3170", {"start": v(10.87, -120.92) * mm, "end": v(10.98, -120.64) * mm});
            skLineSegment(sketch, "E3171", {"start": v(10.98, -120.64) * mm, "end": v(11.08, -120.37) * mm});
            skLineSegment(sketch, "E3172", {"start": v(11.08, -120.37) * mm, "end": v(11.18, -120.1) * mm});
            skLineSegment(sketch, "E3173", {"start": v(11.18, -120.1) * mm, "end": v(11.28, -119.83) * mm});
            skLineSegment(sketch, "E3174", {"start": v(11.28, -119.83) * mm, "end": v(11.38, -119.56) * mm});
            skLineSegment(sketch, "E3175", {"start": v(11.38, -119.56) * mm, "end": v(11.47, -119.3) * mm});
            skLineSegment(sketch, "E3176", {"start": v(11.47, -119.3) * mm, "end": v(11.56, -119.04) * mm});
            skLineSegment(sketch, "E3177", {"start": v(11.56, -119.04) * mm, "end": v(11.65, -118.78) * mm});
            skLineSegment(sketch, "E3178", {"start": v(11.65, -118.78) * mm, "end": v(11.74, -118.53) * mm});
            skLineSegment(sketch, "E3179", {"start": v(11.74, -118.53) * mm, "end": v(11.82, -118.28) * mm});
            skLineSegment(sketch, "E3180", {"start": v(11.82, -118.28) * mm, "end": v(11.9, -118.03) * mm});
            skLineSegment(sketch, "E3181", {"start": v(11.9, -118.03) * mm, "end": v(11.98, -117.78) * mm});
            skLineSegment(sketch, "E3182", {"start": v(11.98, -117.78) * mm, "end": v(12.05, -117.54) * mm});
            skLineSegment(sketch, "E3183", {"start": v(12.05, -117.54) * mm, "end": v(12.13, -117.3) * mm});
            skLineSegment(sketch, "E3184", {"start": v(12.13, -117.3) * mm, "end": v(13.18, -116.94) * mm});
            skLineSegment(sketch, "E3185", {"start": v(13.18, -116.94) * mm, "end": v(14.3, -117.05) * mm});
            skLineSegment(sketch, "E3186", {"start": v(14.3, -117.05) * mm, "end": v(14.42, -117.27) * mm});
            skLineSegment(sketch, "E3187", {"start": v(14.42, -117.27) * mm, "end": v(14.55, -117.5) * mm});
            skLineSegment(sketch, "E3188", {"start": v(14.55, -117.5) * mm, "end": v(14.68, -117.72) * mm});
            skLineSegment(sketch, "E3189", {"start": v(14.68, -117.72) * mm, "end": v(14.81, -117.94) * mm});
            skLineSegment(sketch, "E3190", {"start": v(14.81, -117.94) * mm, "end": v(14.95, -118.17) * mm});
            skLineSegment(sketch, "E3191", {"start": v(14.95, -118.17) * mm, "end": v(15.09, -118.4) * mm});
            skLineSegment(sketch, "E3192", {"start": v(15.09, -118.4) * mm, "end": v(15.23, -118.63) * mm});
            skLineSegment(sketch, "E3193", {"start": v(15.23, -118.63) * mm, "end": v(15.38, -118.86) * mm});
            skLineSegment(sketch, "E3194", {"start": v(15.38, -118.86) * mm, "end": v(15.53, -119.1) * mm});
            skLineSegment(sketch, "E3195", {"start": v(15.53, -119.1) * mm, "end": v(15.68, -119.34) * mm});
            skLineSegment(sketch, "E3196", {"start": v(15.68, -119.34) * mm, "end": v(15.83, -119.58) * mm});
            skLineSegment(sketch, "E3197", {"start": v(15.83, -119.58) * mm, "end": v(16, -119.82) * mm});
            skLineSegment(sketch, "E3198", {"start": v(16, -119.82) * mm, "end": v(16.15, -120.06) * mm});
            skLineSegment(sketch, "E3199", {"start": v(16.15, -120.06) * mm, "end": v(16.32, -120.3) * mm});
            skLineSegment(sketch, "E3200", {"start": v(16.32, -120.3) * mm, "end": v(16.48, -120.55) * mm});
            skLineSegment(sketch, "E3201", {"start": v(16.48, -120.55) * mm, "end": v(16.65, -120.8) * mm});
            skLineSegment(sketch, "E3202", {"start": v(16.65, -120.8) * mm, "end": v(16.83, -121.05) * mm});
            skLineSegment(sketch, "E3203", {"start": v(16.83, -121.05) * mm, "end": v(17, -121.3) * mm});
            skLineSegment(sketch, "E3204", {"start": v(17, -121.3) * mm, "end": v(17.19, -121.56) * mm});
            skLineSegment(sketch, "E3205", {"start": v(17.19, -121.56) * mm, "end": v(17.37, -121.81) * mm});
            skLineSegment(sketch, "E3206", {"start": v(17.37, -121.81) * mm, "end": v(17.56, -122.07) * mm});
            skLineSegment(sketch, "E3207", {"start": v(17.56, -122.07) * mm, "end": v(17.75, -122.33) * mm});
            skLineSegment(sketch, "E3208", {"start": v(17.75, -122.33) * mm, "end": v(17.94, -122.59) * mm});
            skLineSegment(sketch, "E3209", {"start": v(17.94, -122.59) * mm, "end": v(18.14, -122.85) * mm});
            skLineSegment(sketch, "E3210", {"start": v(18.14, -122.85) * mm, "end": v(18.34, -123.11) * mm});
            skLineSegment(sketch, "E3211", {"start": v(18.34, -123.11) * mm, "end": v(18.54, -123.38) * mm});
            skLineSegment(sketch, "E3212", {"start": v(18.54, -123.38) * mm, "end": v(18.75, -123.64) * mm});
            skLineSegment(sketch, "E3213", {"start": v(18.75, -123.64) * mm, "end": v(18.96, -123.91) * mm});
            skLineSegment(sketch, "E3214", {"start": v(18.96, -123.91) * mm, "end": v(19.17, -124.18) * mm});
            skLineSegment(sketch, "E3215", {"start": v(19.17, -124.18) * mm, "end": v(19.4, -124.45) * mm});
            skLineSegment(sketch, "E3216", {"start": v(19.4, -124.45) * mm, "end": v(19.57, -124.44) * mm});
            skLineSegment(sketch, "E3217", {"start": v(19.57, -124.44) * mm, "end": v(21, -124.2) * mm});
            skLineSegment(sketch, "E3218", {"start": v(21, -124.2) * mm, "end": v(21.17, -124.16) * mm});
            skLineSegment(sketch, "E3219", {"start": v(21.17, -124.16) * mm, "end": v(21.3, -123.84) * mm});
            skLineSegment(sketch, "E3220", {"start": v(21.3, -123.84) * mm, "end": v(21.4, -123.52) * mm});
            skLineSegment(sketch, "E3221", {"start": v(21.4, -123.52) * mm, "end": v(21.52, -123.2) * mm});
            skLineSegment(sketch, "E3222", {"start": v(21.52, -123.2) * mm, "end": v(21.64, -122.88) * mm});
            skLineSegment(sketch, "E3223", {"start": v(21.64, -122.88) * mm, "end": v(21.75, -122.56) * mm});
            skLineSegment(sketch, "E3224", {"start": v(21.75, -122.56) * mm, "end": v(21.85, -122.25) * mm});
            skLineSegment(sketch, "E3225", {"start": v(21.85, -122.25) * mm, "end": v(21.96, -121.94) * mm});
            skLineSegment(sketch, "E3226", {"start": v(21.96, -121.94) * mm, "end": v(22.06, -121.63) * mm});
            skLineSegment(sketch, "E3227", {"start": v(22.06, -121.63) * mm, "end": v(22.16, -121.33) * mm});
            skLineSegment(sketch, "E3228", {"start": v(22.16, -121.33) * mm, "end": v(22.26, -121.02) * mm});
            skLineSegment(sketch, "E3229", {"start": v(22.26, -121.02) * mm, "end": v(22.35, -120.72) * mm});
            skLineSegment(sketch, "E3230", {"start": v(22.35, -120.72) * mm, "end": v(22.44, -120.43) * mm});
            skLineSegment(sketch, "E3231", {"start": v(22.44, -120.43) * mm, "end": v(22.53, -120.13) * mm});
            skLineSegment(sketch, "E3232", {"start": v(22.53, -120.13) * mm, "end": v(22.62, -119.84) * mm});
            skLineSegment(sketch, "E3233", {"start": v(22.62, -119.84) * mm, "end": v(22.7, -119.55) * mm});
            skLineSegment(sketch, "E3234", {"start": v(22.7, -119.55) * mm, "end": v(22.78, -119.26) * mm});
            skLineSegment(sketch, "E3235", {"start": v(22.78, -119.26) * mm, "end": v(22.86, -118.98) * mm});
            skLineSegment(sketch, "E3236", {"start": v(22.86, -118.98) * mm, "end": v(22.94, -118.7) * mm});
            skLineSegment(sketch, "E3237", {"start": v(22.94, -118.7) * mm, "end": v(23, -118.42) * mm});
            skLineSegment(sketch, "E3238", {"start": v(23, -118.42) * mm, "end": v(23.08, -118.14) * mm});
            skLineSegment(sketch, "E3239", {"start": v(23.08, -118.14) * mm, "end": v(23.15, -117.87) * mm});
            skLineSegment(sketch, "E3240", {"start": v(23.15, -117.87) * mm, "end": v(23.22, -117.6) * mm});
            skLineSegment(sketch, "E3241", {"start": v(23.22, -117.6) * mm, "end": v(23.28, -117.33) * mm});
            skLineSegment(sketch, "E3242", {"start": v(23.28, -117.33) * mm, "end": v(23.34, -117.06) * mm});
            skLineSegment(sketch, "E3243", {"start": v(23.34, -117.06) * mm, "end": v(23.4, -116.8) * mm});
            skLineSegment(sketch, "E3244", {"start": v(23.4, -116.8) * mm, "end": v(23.46, -116.54) * mm});
            skLineSegment(sketch, "E3245", {"start": v(23.46, -116.54) * mm, "end": v(23.52, -116.29) * mm});
            skLineSegment(sketch, "E3246", {"start": v(23.52, -116.29) * mm, "end": v(23.57, -116.03) * mm});
            skLineSegment(sketch, "E3247", {"start": v(23.57, -116.03) * mm, "end": v(23.62, -115.78) * mm});
            skLineSegment(sketch, "E3248", {"start": v(23.62, -115.78) * mm, "end": v(23.68, -115.54) * mm});
            skLineSegment(sketch, "E3249", {"start": v(23.68, -115.54) * mm, "end": v(24.7, -115.08) * mm});
            skLineSegment(sketch, "E3250", {"start": v(24.7, -115.08) * mm, "end": v(25.8, -115.08) * mm});
            skLineSegment(sketch, "E3251", {"start": v(25.8, -115.08) * mm, "end": v(25.95, -115.29) * mm});
            skLineSegment(sketch, "E3252", {"start": v(25.95, -115.29) * mm, "end": v(26.1, -115.5) * mm});
            skLineSegment(sketch, "E3253", {"start": v(26.1, -115.5) * mm, "end": v(26.26, -115.7) * mm});
            skLineSegment(sketch, "E3254", {"start": v(26.26, -115.7) * mm, "end": v(26.41, -115.92) * mm});
            skLineSegment(sketch, "E3255", {"start": v(26.41, -115.92) * mm, "end": v(26.57, -116.13) * mm});
            skLineSegment(sketch, "E3256", {"start": v(26.57, -116.13) * mm, "end": v(26.73, -116.35) * mm});
            skLineSegment(sketch, "E3257", {"start": v(26.73, -116.35) * mm, "end": v(26.9, -116.56) * mm});
            skLineSegment(sketch, "E3258", {"start": v(26.9, -116.56) * mm, "end": v(27.06, -116.78) * mm});
            skLineSegment(sketch, "E3259", {"start": v(27.06, -116.78) * mm, "end": v(27.23, -117) * mm});
            skLineSegment(sketch, "E3260", {"start": v(27.23, -117) * mm, "end": v(27.4, -117.22) * mm});
            skLineSegment(sketch, "E3261", {"start": v(27.4, -117.22) * mm, "end": v(27.59, -117.44) * mm});
            skLineSegment(sketch, "E3262", {"start": v(27.59, -117.44) * mm, "end": v(27.77, -117.67) * mm});
            skLineSegment(sketch, "E3263", {"start": v(27.77, -117.67) * mm, "end": v(27.95, -117.9) * mm});
            skLineSegment(sketch, "E3264", {"start": v(27.95, -117.9) * mm, "end": v(28.14, -118.12) * mm});
            skLineSegment(sketch, "E3265", {"start": v(28.14, -118.12) * mm, "end": v(28.33, -118.35) * mm});
            skLineSegment(sketch, "E3266", {"start": v(28.33, -118.35) * mm, "end": v(28.52, -118.58) * mm});
            skLineSegment(sketch, "E3267", {"start": v(28.52, -118.58) * mm, "end": v(28.72, -118.81) * mm});
            skLineSegment(sketch, "E3268", {"start": v(28.72, -118.81) * mm, "end": v(28.92, -119.05) * mm});
            skLineSegment(sketch, "E3269", {"start": v(28.92, -119.05) * mm, "end": v(29.13, -119.28) * mm});
            skLineSegment(sketch, "E3270", {"start": v(29.13, -119.28) * mm, "end": v(29.33, -119.52) * mm});
            skLineSegment(sketch, "E3271", {"start": v(29.33, -119.52) * mm, "end": v(29.54, -119.76) * mm});
            skLineSegment(sketch, "E3272", {"start": v(29.54, -119.76) * mm, "end": v(29.76, -120) * mm});
            skLineSegment(sketch, "E3273", {"start": v(29.76, -120) * mm, "end": v(29.98, -120.23) * mm});
            skLineSegment(sketch, "E3274", {"start": v(29.98, -120.23) * mm, "end": v(30.2, -120.48) * mm});
            skLineSegment(sketch, "E3275", {"start": v(30.2, -120.48) * mm, "end": v(30.42, -120.72) * mm});
            skLineSegment(sketch, "E3276", {"start": v(30.42, -120.72) * mm, "end": v(30.65, -120.96) * mm});
            skLineSegment(sketch, "E3277", {"start": v(30.65, -120.96) * mm, "end": v(30.89, -121.2) * mm});
            skLineSegment(sketch, "E3278", {"start": v(30.89, -121.2) * mm, "end": v(31.12, -121.45) * mm});
            skLineSegment(sketch, "E3279", {"start": v(31.12, -121.45) * mm, "end": v(31.36, -121.7) * mm});
            skLineSegment(sketch, "E3280", {"start": v(31.36, -121.7) * mm, "end": v(31.6, -121.95) * mm});
            skLineSegment(sketch, "E3281", {"start": v(31.6, -121.95) * mm, "end": v(31.78, -121.91) * mm});
            skLineSegment(sketch, "E3282", {"start": v(31.78, -121.91) * mm, "end": v(33.18, -121.54) * mm});
            skLineSegment(sketch, "E3283", {"start": v(33.18, -121.54) * mm, "end": v(33.35, -121.49) * mm});
            skLineSegment(sketch, "E3284", {"start": v(33.35, -121.49) * mm, "end": v(33.43, -121.15) * mm});
            skLineSegment(sketch, "E3285", {"start": v(33.43, -121.15) * mm, "end": v(33.52, -120.82) * mm});
            skLineSegment(sketch, "E3286", {"start": v(33.52, -120.82) * mm, "end": v(33.6, -120.49) * mm});
            skLineSegment(sketch, "E3287", {"start": v(33.6, -120.49) * mm, "end": v(33.69, -120.16) * mm});
            skLineSegment(sketch, "E3288", {"start": v(33.69, -120.16) * mm, "end": v(33.76, -119.84) * mm});
            skLineSegment(sketch, "E3289", {"start": v(33.76, -119.84) * mm, "end": v(33.84, -119.51) * mm});
            skLineSegment(sketch, "E3290", {"start": v(33.84, -119.51) * mm, "end": v(33.91, -119.2) * mm});
            skLineSegment(sketch, "E3291", {"start": v(33.91, -119.2) * mm, "end": v(33.98, -118.88) * mm});
            skLineSegment(sketch, "E3292", {"start": v(33.98, -118.88) * mm, "end": v(34.05, -118.56) * mm});
            skLineSegment(sketch, "E3293", {"start": v(34.05, -118.56) * mm, "end": v(34.12, -118.25) * mm});
            skLineSegment(sketch, "E3294", {"start": v(34.12, -118.25) * mm, "end": v(34.18, -117.95) * mm});
            skLineSegment(sketch, "E3295", {"start": v(34.18, -117.95) * mm, "end": v(34.24, -117.64) * mm});
            skLineSegment(sketch, "E3296", {"start": v(34.24, -117.64) * mm, "end": v(34.3, -117.34) * mm});
            skLineSegment(sketch, "E3297", {"start": v(34.3, -117.34) * mm, "end": v(34.36, -117.04) * mm});
            skLineSegment(sketch, "E3298", {"start": v(34.36, -117.04) * mm, "end": v(34.42, -116.74) * mm});
            skLineSegment(sketch, "E3299", {"start": v(34.42, -116.74) * mm, "end": v(34.47, -116.45) * mm});
            skLineSegment(sketch, "E3300", {"start": v(34.47, -116.45) * mm, "end": v(34.52, -116.16) * mm});
            skLineSegment(sketch, "E3301", {"start": v(34.52, -116.16) * mm, "end": v(34.57, -115.87) * mm});
            skLineSegment(sketch, "E3302", {"start": v(34.57, -115.87) * mm, "end": v(34.61, -115.59) * mm});
            skLineSegment(sketch, "E3303", {"start": v(34.61, -115.59) * mm, "end": v(34.66, -115.3) * mm});
            skLineSegment(sketch, "E3304", {"start": v(34.66, -115.3) * mm, "end": v(34.7, -115.03) * mm});
            skLineSegment(sketch, "E3305", {"start": v(34.7, -115.03) * mm, "end": v(34.74, -114.75) * mm});
            skLineSegment(sketch, "E3306", {"start": v(34.74, -114.75) * mm, "end": v(34.78, -114.48) * mm});
            skLineSegment(sketch, "E3307", {"start": v(34.78, -114.48) * mm, "end": v(34.82, -114.2) * mm});
            skLineSegment(sketch, "E3308", {"start": v(34.82, -114.2) * mm, "end": v(34.85, -113.94) * mm});
            skLineSegment(sketch, "E3309", {"start": v(34.85, -113.94) * mm, "end": v(34.88, -113.68) * mm});
            skLineSegment(sketch, "E3310", {"start": v(34.88, -113.68) * mm, "end": v(34.91, -113.42) * mm});
            skLineSegment(sketch, "E3311", {"start": v(34.91, -113.42) * mm, "end": v(34.94, -113.16) * mm});
            skLineSegment(sketch, "E3312", {"start": v(34.94, -113.16) * mm, "end": v(34.97, -112.9) * mm});
            skLineSegment(sketch, "E3313", {"start": v(34.97, -112.9) * mm, "end": v(35, -112.65) * mm});
            skLineSegment(sketch, "E3314", {"start": v(35, -112.65) * mm, "end": v(35.96, -112.1) * mm});
            skLineSegment(sketch, "E3315", {"start": v(35.96, -112.1) * mm, "end": v(37.07, -112) * mm});
            skLineSegment(sketch, "E3316", {"start": v(37.07, -112) * mm, "end": v(37.24, -112.19) * mm});
            skLineSegment(sketch, "E3317", {"start": v(37.24, -112.19) * mm, "end": v(37.4, -112.38) * mm});
            skLineSegment(sketch, "E3318", {"start": v(37.4, -112.38) * mm, "end": v(37.58, -112.57) * mm});
            skLineSegment(sketch, "E3319", {"start": v(37.58, -112.57) * mm, "end": v(37.75, -112.77) * mm});
            skLineSegment(sketch, "E3320", {"start": v(37.75, -112.77) * mm, "end": v(37.93, -112.96) * mm});
            skLineSegment(sketch, "E3321", {"start": v(37.93, -112.96) * mm, "end": v(38.11, -113.16) * mm});
            skLineSegment(sketch, "E3322", {"start": v(38.11, -113.16) * mm, "end": v(38.3, -113.36) * mm});
            skLineSegment(sketch, "E3323", {"start": v(38.3, -113.36) * mm, "end": v(38.49, -113.56) * mm});
            skLineSegment(sketch, "E3324", {"start": v(38.49, -113.56) * mm, "end": v(38.68, -113.76) * mm});
            skLineSegment(sketch, "E3325", {"start": v(38.68, -113.76) * mm, "end": v(38.87, -113.97) * mm});
            skLineSegment(sketch, "E3326", {"start": v(38.87, -113.97) * mm, "end": v(39.07, -114.17) * mm});
            skLineSegment(sketch, "E3327", {"start": v(39.07, -114.17) * mm, "end": v(39.27, -114.38) * mm});
            skLineSegment(sketch, "E3328", {"start": v(39.27, -114.38) * mm, "end": v(39.48, -114.58) * mm});
            skLineSegment(sketch, "E3329", {"start": v(39.48, -114.58) * mm, "end": v(39.7, -114.8) * mm});
            skLineSegment(sketch, "E3330", {"start": v(39.7, -114.8) * mm, "end": v(39.9, -115) * mm});
            skLineSegment(sketch, "E3331", {"start": v(39.9, -115) * mm, "end": v(40.12, -115.21) * mm});
            skLineSegment(sketch, "E3332", {"start": v(40.12, -115.21) * mm, "end": v(40.34, -115.42) * mm});
            skLineSegment(sketch, "E3333", {"start": v(40.34, -115.42) * mm, "end": v(40.56, -115.63) * mm});
            skLineSegment(sketch, "E3334", {"start": v(40.56, -115.63) * mm, "end": v(40.79, -115.85) * mm});
            skLineSegment(sketch, "E3335", {"start": v(40.79, -115.85) * mm, "end": v(41.01, -116.06) * mm});
            skLineSegment(sketch, "E3336", {"start": v(41.01, -116.06) * mm, "end": v(41.25, -116.28) * mm});
            skLineSegment(sketch, "E3337", {"start": v(41.25, -116.28) * mm, "end": v(41.49, -116.5) * mm});
            skLineSegment(sketch, "E3338", {"start": v(41.49, -116.5) * mm, "end": v(41.73, -116.71) * mm});
            skLineSegment(sketch, "E3339", {"start": v(41.73, -116.71) * mm, "end": v(41.97, -116.93) * mm});
            skLineSegment(sketch, "E3340", {"start": v(41.97, -116.93) * mm, "end": v(42.22, -117.15) * mm});
            skLineSegment(sketch, "E3341", {"start": v(42.22, -117.15) * mm, "end": v(42.47, -117.37) * mm});
            skLineSegment(sketch, "E3342", {"start": v(42.47, -117.37) * mm, "end": v(42.73, -117.6) * mm});
            skLineSegment(sketch, "E3343", {"start": v(42.73, -117.6) * mm, "end": v(42.98, -117.81) * mm});
            skLineSegment(sketch, "E3344", {"start": v(42.98, -117.81) * mm, "end": v(43.25, -118.03) * mm});
            skLineSegment(sketch, "E3345", {"start": v(43.25, -118.03) * mm, "end": v(43.51, -118.26) * mm});
            skLineSegment(sketch, "E3346", {"start": v(43.51, -118.26) * mm, "end": v(43.68, -118.2) * mm});
            skLineSegment(sketch, "E3347", {"start": v(43.68, -118.2) * mm, "end": v(45.04, -117.7) * mm});
            skLineSegment(sketch, "E3348", {"start": v(45.04, -117.7) * mm, "end": v(45.2, -117.63) * mm});
            skLineSegment(sketch, "E3349", {"start": v(45.2, -117.63) * mm, "end": v(45.26, -117.28) * mm});
            skLineSegment(sketch, "E3350", {"start": v(45.26, -117.28) * mm, "end": v(45.3, -116.95) * mm});
            skLineSegment(sketch, "E3351", {"start": v(45.3, -116.95) * mm, "end": v(45.36, -116.6) * mm});
            skLineSegment(sketch, "E3352", {"start": v(45.36, -116.6) * mm, "end": v(45.4, -116.27) * mm});
            skLineSegment(sketch, "E3353", {"start": v(45.4, -116.27) * mm, "end": v(45.46, -115.94) * mm});
            skLineSegment(sketch, "E3354", {"start": v(45.46, -115.94) * mm, "end": v(45.5, -115.62) * mm});
            skLineSegment(sketch, "E3355", {"start": v(45.5, -115.62) * mm, "end": v(45.54, -115.3) * mm});
            skLineSegment(sketch, "E3356", {"start": v(45.54, -115.3) * mm, "end": v(45.58, -114.97) * mm});
            skLineSegment(sketch, "E3357", {"start": v(45.58, -114.97) * mm, "end": v(45.62, -114.65) * mm});
            skLineSegment(sketch, "E3358", {"start": v(45.62, -114.65) * mm, "end": v(45.65, -114.33) * mm});
            skLineSegment(sketch, "E3359", {"start": v(45.65, -114.33) * mm, "end": v(45.69, -114.02) * mm});
            skLineSegment(sketch, "E3360", {"start": v(45.69, -114.02) * mm, "end": v(45.72, -113.71) * mm});
            skLineSegment(sketch, "E3361", {"start": v(45.72, -113.71) * mm, "end": v(45.75, -113.4) * mm});
            skLineSegment(sketch, "E3362", {"start": v(45.75, -113.4) * mm, "end": v(45.78, -113.1) * mm});
            skLineSegment(sketch, "E3363", {"start": v(45.78, -113.1) * mm, "end": v(45.8, -112.8) * mm});
            skLineSegment(sketch, "E3364", {"start": v(45.8, -112.8) * mm, "end": v(45.83, -112.5) * mm});
            skLineSegment(sketch, "E3365", {"start": v(45.83, -112.5) * mm, "end": v(45.85, -112.21) * mm});
            skLineSegment(sketch, "E3366", {"start": v(45.85, -112.21) * mm, "end": v(45.87, -111.92) * mm});
            skLineSegment(sketch, "E3367", {"start": v(45.87, -111.92) * mm, "end": v(45.89, -111.63) * mm});
            skLineSegment(sketch, "E3368", {"start": v(45.89, -111.63) * mm, "end": v(45.9, -111.35) * mm});
            skLineSegment(sketch, "E3369", {"start": v(45.9, -111.35) * mm, "end": v(45.92, -111.07) * mm});
            skLineSegment(sketch, "E3370", {"start": v(45.92, -111.07) * mm, "end": v(45.93, -110.79) * mm});
            skLineSegment(sketch, "E3371", {"start": v(45.93, -110.79) * mm, "end": v(45.94, -110.51) * mm});
            skLineSegment(sketch, "E3372", {"start": v(45.94, -110.51) * mm, "end": v(45.95, -110.24) * mm});
            skLineSegment(sketch, "E3373", {"start": v(45.95, -110.24) * mm, "end": v(45.96, -109.97) * mm});
            skLineSegment(sketch, "E3374", {"start": v(45.96, -109.97) * mm, "end": v(45.96, -109.7) * mm});
            skLineSegment(sketch, "E3375", {"start": v(45.96, -109.7) * mm, "end": v(45.97, -109.44) * mm});
            skLineSegment(sketch, "E3376", {"start": v(45.97, -109.44) * mm, "end": v(45.97, -109.19) * mm});
            skLineSegment(sketch, "E3377", {"start": v(45.97, -109.19) * mm, "end": v(45.98, -108.93) * mm});
            skLineSegment(sketch, "E3378", {"start": v(45.98, -108.93) * mm, "end": v(45.98, -108.68) * mm});
            skLineSegment(sketch, "E3379", {"start": v(45.98, -108.68) * mm, "end": v(46.88, -108.03) * mm});
            skLineSegment(sketch, "E3380", {"start": v(46.88, -108.03) * mm, "end": v(47.98, -107.82) * mm});
            skLineSegment(sketch, "E3381", {"start": v(47.98, -107.82) * mm, "end": v(48.16, -108) * mm});
            skLineSegment(sketch, "E3382", {"start": v(48.16, -108) * mm, "end": v(48.35, -108.16) * mm});
            skLineSegment(sketch, "E3383", {"start": v(48.35, -108.16) * mm, "end": v(48.54, -108.34) * mm});
            skLineSegment(sketch, "E3384", {"start": v(48.54, -108.34) * mm, "end": v(48.73, -108.52) * mm});
            skLineSegment(sketch, "E3385", {"start": v(48.73, -108.52) * mm, "end": v(48.93, -108.7) * mm});
            skLineSegment(sketch, "E3386", {"start": v(48.93, -108.7) * mm, "end": v(49.13, -108.87) * mm});
            skLineSegment(sketch, "E3387", {"start": v(49.13, -108.87) * mm, "end": v(49.33, -109.05) * mm});
            skLineSegment(sketch, "E3388", {"start": v(49.33, -109.05) * mm, "end": v(49.54, -109.24) * mm});
            skLineSegment(sketch, "E3389", {"start": v(49.54, -109.24) * mm, "end": v(49.75, -109.42) * mm});
            skLineSegment(sketch, "E3390", {"start": v(49.75, -109.42) * mm, "end": v(49.97, -109.6) * mm});
            skLineSegment(sketch, "E3391", {"start": v(49.97, -109.6) * mm, "end": v(50.18, -109.78) * mm});
            skLineSegment(sketch, "E3392", {"start": v(50.18, -109.78) * mm, "end": v(50.4, -109.97) * mm});
            skLineSegment(sketch, "E3393", {"start": v(50.4, -109.97) * mm, "end": v(50.63, -110.16) * mm});
            skLineSegment(sketch, "E3394", {"start": v(50.63, -110.16) * mm, "end": v(50.86, -110.34) * mm});
            skLineSegment(sketch, "E3395", {"start": v(50.86, -110.34) * mm, "end": v(51.09, -110.53) * mm});
            skLineSegment(sketch, "E3396", {"start": v(51.09, -110.53) * mm, "end": v(51.33, -110.72) * mm});
            skLineSegment(sketch, "E3397", {"start": v(51.33, -110.72) * mm, "end": v(51.56, -110.9) * mm});
            skLineSegment(sketch, "E3398", {"start": v(51.56, -110.9) * mm, "end": v(51.8, -111.1) * mm});
            skLineSegment(sketch, "E3399", {"start": v(51.8, -111.1) * mm, "end": v(52.05, -111.29) * mm});
            skLineSegment(sketch, "E3400", {"start": v(52.05, -111.29) * mm, "end": v(52.3, -111.48) * mm});
            skLineSegment(sketch, "E3401", {"start": v(52.3, -111.48) * mm, "end": v(52.56, -111.67) * mm});
            skLineSegment(sketch, "E3402", {"start": v(52.56, -111.67) * mm, "end": v(52.81, -111.86) * mm});
            skLineSegment(sketch, "E3403", {"start": v(52.81, -111.86) * mm, "end": v(53.07, -112.06) * mm});
            skLineSegment(sketch, "E3404", {"start": v(53.07, -112.06) * mm, "end": v(53.34, -112.25) * mm});
            skLineSegment(sketch, "E3405", {"start": v(53.34, -112.25) * mm, "end": v(53.6, -112.44) * mm});
            skLineSegment(sketch, "E3406", {"start": v(53.6, -112.44) * mm, "end": v(53.88, -112.64) * mm});
            skLineSegment(sketch, "E3407", {"start": v(53.88, -112.64) * mm, "end": v(54.15, -112.83) * mm});
            skLineSegment(sketch, "E3408", {"start": v(54.15, -112.83) * mm, "end": v(54.43, -113.03) * mm});
            skLineSegment(sketch, "E3409", {"start": v(54.43, -113.03) * mm, "end": v(54.72, -113.22) * mm});
            skLineSegment(sketch, "E3410", {"start": v(54.72, -113.22) * mm, "end": v(55, -113.42) * mm});
            skLineSegment(sketch, "E3411", {"start": v(55, -113.42) * mm, "end": v(55.17, -113.35) * mm});
            skLineSegment(sketch, "E3412", {"start": v(55.17, -113.35) * mm, "end": v(56.47, -112.71) * mm});
            skLineSegment(sketch, "E3413", {"start": v(56.47, -112.71) * mm, "end": v(56.62, -112.63) * mm});
            skLineSegment(sketch, "E3414", {"start": v(56.62, -112.63) * mm, "end": v(56.64, -112.28) * mm});
            skLineSegment(sketch, "E3415", {"start": v(56.64, -112.28) * mm, "end": v(56.66, -111.94) * mm});
            skLineSegment(sketch, "E3416", {"start": v(56.66, -111.94) * mm, "end": v(56.68, -111.6) * mm});
            skLineSegment(sketch, "E3417", {"start": v(56.68, -111.6) * mm, "end": v(56.7, -111.26) * mm});
            skLineSegment(sketch, "E3418", {"start": v(56.7, -111.26) * mm, "end": v(56.71, -110.92) * mm});
            skLineSegment(sketch, "E3419", {"start": v(56.71, -110.92) * mm, "end": v(56.72, -110.6) * mm});
            skLineSegment(sketch, "E3420", {"start": v(56.72, -110.6) * mm, "end": v(56.73, -110.27) * mm});
            skLineSegment(sketch, "E3421", {"start": v(56.73, -110.27) * mm, "end": v(56.74, -109.94) * mm});
            skLineSegment(sketch, "E3422", {"start": v(56.74, -109.94) * mm, "end": v(56.75, -109.62) * mm});
            skLineSegment(sketch, "E3423", {"start": v(56.75, -109.62) * mm, "end": v(56.75, -109.3) * mm});
            skLineSegment(sketch, "E3424", {"start": v(56.75, -109.3) * mm, "end": v(56.75, -108.99) * mm});
            skLineSegment(sketch, "E3425", {"start": v(56.75, -108.99) * mm, "end": v(56.75, -108.68) * mm});
            skLineSegment(sketch, "E3426", {"start": v(56.75, -108.68) * mm, "end": v(56.75, -108.37) * mm});
            skLineSegment(sketch, "E3427", {"start": v(56.75, -108.37) * mm, "end": v(56.75, -108.07) * mm});
            skLineSegment(sketch, "E3428", {"start": v(56.75, -108.07) * mm, "end": v(56.75, -107.76) * mm});
            skLineSegment(sketch, "E3429", {"start": v(56.75, -107.76) * mm, "end": v(56.74, -107.47) * mm});
            skLineSegment(sketch, "E3430", {"start": v(56.74, -107.47) * mm, "end": v(56.73, -107.17) * mm});
            skLineSegment(sketch, "E3431", {"start": v(56.73, -107.17) * mm, "end": v(56.72, -106.88) * mm});
            skLineSegment(sketch, "E3432", {"start": v(56.72, -106.88) * mm, "end": v(56.71, -106.6) * mm});
            skLineSegment(sketch, "E3433", {"start": v(56.71, -106.6) * mm, "end": v(56.7, -106.3) * mm});
            skLineSegment(sketch, "E3434", {"start": v(56.7, -106.3) * mm, "end": v(56.7, -106.03) * mm});
            skLineSegment(sketch, "E3435", {"start": v(56.7, -106.03) * mm, "end": v(56.68, -105.75) * mm});
            skLineSegment(sketch, "E3436", {"start": v(56.68, -105.75) * mm, "end": v(56.66, -105.47) * mm});
            skLineSegment(sketch, "E3437", {"start": v(56.66, -105.47) * mm, "end": v(56.64, -105.2) * mm});
            skLineSegment(sketch, "E3438", {"start": v(56.64, -105.2) * mm, "end": v(56.62, -104.93) * mm});
            skLineSegment(sketch, "E3439", {"start": v(56.62, -104.93) * mm, "end": v(56.6, -104.67) * mm});
            skLineSegment(sketch, "E3440", {"start": v(56.6, -104.67) * mm, "end": v(56.58, -104.4) * mm});
            skLineSegment(sketch, "E3441", {"start": v(56.58, -104.4) * mm, "end": v(56.56, -104.15) * mm});
            skLineSegment(sketch, "E3442", {"start": v(56.56, -104.15) * mm, "end": v(56.54, -103.9) * mm});
            skLineSegment(sketch, "E3443", {"start": v(56.54, -103.9) * mm, "end": v(56.52, -103.64) * mm});
            skLineSegment(sketch, "E3444", {"start": v(56.52, -103.64) * mm, "end": v(57.36, -102.9) * mm});
            skLineSegment(sketch, "E3445", {"start": v(57.36, -102.9) * mm, "end": v(58.42, -102.59) * mm});
            skLineSegment(sketch, "E3446", {"start": v(58.42, -102.59) * mm, "end": v(58.62, -102.74) * mm});
            skLineSegment(sketch, "E3447", {"start": v(58.62, -102.74) * mm, "end": v(58.83, -102.9) * mm});
            skLineSegment(sketch, "E3448", {"start": v(58.83, -102.9) * mm, "end": v(59.03, -103.06) * mm});
            skLineSegment(sketch, "E3449", {"start": v(59.03, -103.06) * mm, "end": v(59.24, -103.21) * mm});
            skLineSegment(sketch, "E3450", {"start": v(59.24, -103.21) * mm, "end": v(59.46, -103.37) * mm});
            skLineSegment(sketch, "E3451", {"start": v(59.46, -103.37) * mm, "end": v(59.67, -103.53) * mm});
            skLineSegment(sketch, "E3452", {"start": v(59.67, -103.53) * mm, "end": v(59.9, -103.69) * mm});
            skLineSegment(sketch, "E3453", {"start": v(59.9, -103.69) * mm, "end": v(60.12, -103.85) * mm});
            skLineSegment(sketch, "E3454", {"start": v(60.12, -103.85) * mm, "end": v(60.34, -104) * mm});
            skLineSegment(sketch, "E3455", {"start": v(60.34, -104) * mm, "end": v(60.58, -104.17) * mm});
            skLineSegment(sketch, "E3456", {"start": v(60.58, -104.17) * mm, "end": v(60.81, -104.33) * mm});
            skLineSegment(sketch, "E3457", {"start": v(60.81, -104.33) * mm, "end": v(61.05, -104.5) * mm});
            skLineSegment(sketch, "E3458", {"start": v(61.05, -104.5) * mm, "end": v(61.3, -104.66) * mm});
            skLineSegment(sketch, "E3459", {"start": v(61.3, -104.66) * mm, "end": v(61.54, -104.82) * mm});
            skLineSegment(sketch, "E3460", {"start": v(61.54, -104.82) * mm, "end": v(61.79, -104.98) * mm});
            skLineSegment(sketch, "E3461", {"start": v(61.79, -104.98) * mm, "end": v(62.04, -105.15) * mm});
            skLineSegment(sketch, "E3462", {"start": v(62.04, -105.15) * mm, "end": v(62.3, -105.31) * mm});
            skLineSegment(sketch, "E3463", {"start": v(62.3, -105.31) * mm, "end": v(62.56, -105.48) * mm});
            skLineSegment(sketch, "E3464", {"start": v(62.56, -105.48) * mm, "end": v(62.82, -105.64) * mm});
            skLineSegment(sketch, "E3465", {"start": v(62.82, -105.64) * mm, "end": v(63.09, -105.81) * mm});
            skLineSegment(sketch, "E3466", {"start": v(63.09, -105.81) * mm, "end": v(63.36, -105.98) * mm});
            skLineSegment(sketch, "E3467", {"start": v(63.36, -105.98) * mm, "end": v(63.63, -106.14) * mm});
            skLineSegment(sketch, "E3468", {"start": v(63.63, -106.14) * mm, "end": v(63.9, -106.3) * mm});
            skLineSegment(sketch, "E3469", {"start": v(63.9, -106.3) * mm, "end": v(64.2, -106.47) * mm});
            skLineSegment(sketch, "E3470", {"start": v(64.2, -106.47) * mm, "end": v(64.48, -106.64) * mm});
            skLineSegment(sketch, "E3471", {"start": v(64.48, -106.64) * mm, "end": v(64.77, -106.8) * mm});
            skLineSegment(sketch, "E3472", {"start": v(64.77, -106.8) * mm, "end": v(65.06, -106.97) * mm});
            skLineSegment(sketch, "E3473", {"start": v(65.06, -106.97) * mm, "end": v(65.36, -107.14) * mm});
            skLineSegment(sketch, "E3474", {"start": v(65.36, -107.14) * mm, "end": v(65.66, -107.3) * mm});
            skLineSegment(sketch, "E3475", {"start": v(65.66, -107.3) * mm, "end": v(65.96, -107.47) * mm});
            skLineSegment(sketch, "E3476", {"start": v(65.96, -107.47) * mm, "end": v(66.12, -107.4) * mm});
            skLineSegment(sketch, "E3477", {"start": v(66.12, -107.4) * mm, "end": v(67.35, -106.63) * mm});
            skLineSegment(sketch, "E3478", {"start": v(67.35, -106.63) * mm, "end": v(67.5, -106.53) * mm});
            skLineSegment(sketch, "E3479", {"start": v(67.5, -106.53) * mm, "end": v(67.48, -106.18) * mm});
            skLineSegment(sketch, "E3480", {"start": v(67.48, -106.18) * mm, "end": v(67.47, -105.84) * mm});
            skLineSegment(sketch, "E3481", {"start": v(67.47, -105.84) * mm, "end": v(67.45, -105.5) * mm});
            skLineSegment(sketch, "E3482", {"start": v(67.45, -105.5) * mm, "end": v(67.44, -105.16) * mm});
            skLineSegment(sketch, "E3483", {"start": v(67.44, -105.16) * mm, "end": v(67.42, -104.83) * mm});
            skLineSegment(sketch, "E3484", {"start": v(67.42, -104.83) * mm, "end": v(67.4, -104.5) * mm});
            skLineSegment(sketch, "E3485", {"start": v(67.4, -104.5) * mm, "end": v(67.38, -104.17) * mm});
            skLineSegment(sketch, "E3486", {"start": v(67.38, -104.17) * mm, "end": v(67.35, -103.85) * mm});
            skLineSegment(sketch, "E3487", {"start": v(67.35, -103.85) * mm, "end": v(67.32, -103.53) * mm});
            skLineSegment(sketch, "E3488", {"start": v(67.32, -103.53) * mm, "end": v(67.3, -103.2) * mm});
            skLineSegment(sketch, "E3489", {"start": v(67.3, -103.2) * mm, "end": v(67.27, -102.9) * mm});
            skLineSegment(sketch, "E3490", {"start": v(67.27, -102.9) * mm, "end": v(67.24, -102.59) * mm});
            skLineSegment(sketch, "E3491", {"start": v(67.24, -102.59) * mm, "end": v(67.2, -102.28) * mm});
            skLineSegment(sketch, "E3492", {"start": v(67.2, -102.28) * mm, "end": v(67.18, -101.98) * mm});
            skLineSegment(sketch, "E3493", {"start": v(67.18, -101.98) * mm, "end": v(67.14, -101.68) * mm});
            skLineSegment(sketch, "E3494", {"start": v(67.14, -101.68) * mm, "end": v(67.1, -101.38) * mm});
            skLineSegment(sketch, "E3495", {"start": v(67.1, -101.38) * mm, "end": v(67.07, -101.09) * mm});
            skLineSegment(sketch, "E3496", {"start": v(67.07, -101.09) * mm, "end": v(67.04, -100.8) * mm});
            skLineSegment(sketch, "E3497", {"start": v(67.04, -100.8) * mm, "end": v(67, -100.51) * mm});
            skLineSegment(sketch, "E3498", {"start": v(67, -100.51) * mm, "end": v(66.96, -100.23) * mm});
            skLineSegment(sketch, "E3499", {"start": v(66.96, -100.23) * mm, "end": v(66.92, -99.95) * mm});
            skLineSegment(sketch, "E3500", {"start": v(66.92, -99.95) * mm, "end": v(66.88, -99.68) * mm});
            skLineSegment(sketch, "E3501", {"start": v(66.88, -99.68) * mm, "end": v(66.83, -99.4) * mm});
            skLineSegment(sketch, "E3502", {"start": v(66.83, -99.4) * mm, "end": v(66.79, -99.14) * mm});
            skLineSegment(sketch, "E3503", {"start": v(66.79, -99.14) * mm, "end": v(66.75, -98.87) * mm});
            skLineSegment(sketch, "E3504", {"start": v(66.75, -98.87) * mm, "end": v(66.7, -98.61) * mm});
            skLineSegment(sketch, "E3505", {"start": v(66.7, -98.61) * mm, "end": v(66.65, -98.35) * mm});
            skLineSegment(sketch, "E3506", {"start": v(66.65, -98.35) * mm, "end": v(66.6, -98.1) * mm});
            skLineSegment(sketch, "E3507", {"start": v(66.6, -98.1) * mm, "end": v(66.56, -97.85) * mm});
            skLineSegment(sketch, "E3508", {"start": v(66.56, -97.85) * mm, "end": v(66.51, -97.6) * mm});
            skLineSegment(sketch, "E3509", {"start": v(66.51, -97.6) * mm, "end": v(67.27, -96.79) * mm});
            skLineSegment(sketch, "E3510", {"start": v(67.27, -96.79) * mm, "end": v(68.3, -96.36) * mm});
            skLineSegment(sketch, "E3511", {"start": v(68.3, -96.36) * mm, "end": v(68.52, -96.5) * mm});
            skLineSegment(sketch, "E3512", {"start": v(68.52, -96.5) * mm, "end": v(68.74, -96.63) * mm});
            skLineSegment(sketch, "E3513", {"start": v(68.74, -96.63) * mm, "end": v(68.96, -96.77) * mm});
            skLineSegment(sketch, "E3514", {"start": v(68.96, -96.77) * mm, "end": v(69.18, -96.9) * mm});
            skLineSegment(sketch, "E3515", {"start": v(69.18, -96.9) * mm, "end": v(69.41, -97.04) * mm});
            skLineSegment(sketch, "E3516", {"start": v(69.41, -97.04) * mm, "end": v(69.64, -97.18) * mm});
            skLineSegment(sketch, "E3517", {"start": v(69.64, -97.18) * mm, "end": v(69.88, -97.31) * mm});
            skLineSegment(sketch, "E3518", {"start": v(69.88, -97.31) * mm, "end": v(70.12, -97.45) * mm});
            skLineSegment(sketch, "E3519", {"start": v(70.12, -97.45) * mm, "end": v(70.36, -97.59) * mm});
            skLineSegment(sketch, "E3520", {"start": v(70.36, -97.59) * mm, "end": v(70.6, -97.73) * mm});
            skLineSegment(sketch, "E3521", {"start": v(70.6, -97.73) * mm, "end": v(70.85, -97.86) * mm});
            skLineSegment(sketch, "E3522", {"start": v(70.85, -97.86) * mm, "end": v(71.1, -98) * mm});
            skLineSegment(sketch, "E3523", {"start": v(71.1, -98) * mm, "end": v(71.36, -98.14) * mm});
            skLineSegment(sketch, "E3524", {"start": v(71.36, -98.14) * mm, "end": v(71.62, -98.28) * mm});
            skLineSegment(sketch, "E3525", {"start": v(71.62, -98.28) * mm, "end": v(71.89, -98.42) * mm});
            skLineSegment(sketch, "E3526", {"start": v(71.89, -98.42) * mm, "end": v(72.16, -98.56) * mm});
            skLineSegment(sketch, "E3527", {"start": v(72.16, -98.56) * mm, "end": v(72.43, -98.7) * mm});
            skLineSegment(sketch, "E3528", {"start": v(72.43, -98.7) * mm, "end": v(72.7, -98.83) * mm});
            skLineSegment(sketch, "E3529", {"start": v(72.7, -98.83) * mm, "end": v(72.98, -98.97) * mm});
            skLineSegment(sketch, "E3530", {"start": v(72.98, -98.97) * mm, "end": v(73.26, -99.11) * mm});
            skLineSegment(sketch, "E3531", {"start": v(73.26, -99.11) * mm, "end": v(73.55, -99.25) * mm});
            skLineSegment(sketch, "E3532", {"start": v(73.55, -99.25) * mm, "end": v(73.84, -99.39) * mm});
            skLineSegment(sketch, "E3533", {"start": v(73.84, -99.39) * mm, "end": v(74.13, -99.53) * mm});
            skLineSegment(sketch, "E3534", {"start": v(74.13, -99.53) * mm, "end": v(74.43, -99.66) * mm});
            skLineSegment(sketch, "E3535", {"start": v(74.43, -99.66) * mm, "end": v(74.73, -99.8) * mm});
            skLineSegment(sketch, "E3536", {"start": v(74.73, -99.8) * mm, "end": v(75.03, -99.94) * mm});
            skLineSegment(sketch, "E3537", {"start": v(75.03, -99.94) * mm, "end": v(75.34, -100.08) * mm});
            skLineSegment(sketch, "E3538", {"start": v(75.34, -100.08) * mm, "end": v(75.65, -100.21) * mm});
            skLineSegment(sketch, "E3539", {"start": v(75.65, -100.21) * mm, "end": v(75.97, -100.35) * mm});
            skLineSegment(sketch, "E3540", {"start": v(75.97, -100.35) * mm, "end": v(76.29, -100.49) * mm});
            skLineSegment(sketch, "E3541", {"start": v(76.29, -100.49) * mm, "end": v(76.44, -100.39) * mm});
            skLineSegment(sketch, "E3542", {"start": v(76.44, -100.39) * mm, "end": v(77.59, -99.51) * mm});
            skLineSegment(sketch, "E3543", {"start": v(77.59, -99.51) * mm, "end": v(77.72, -99.4) * mm});
            skLineSegment(sketch, "E3544", {"start": v(77.72, -99.4) * mm, "end": v(77.68, -99.05) * mm});
            skLineSegment(sketch, "E3545", {"start": v(77.68, -99.05) * mm, "end": v(77.63, -98.7) * mm});
            skLineSegment(sketch, "E3546", {"start": v(77.63, -98.7) * mm, "end": v(77.58, -98.37) * mm});
            skLineSegment(sketch, "E3547", {"start": v(77.58, -98.37) * mm, "end": v(77.53, -98.04) * mm});
            skLineSegment(sketch, "E3548", {"start": v(77.53, -98.04) * mm, "end": v(77.48, -97.7) * mm});
            skLineSegment(sketch, "E3549", {"start": v(77.48, -97.7) * mm, "end": v(77.42, -97.38) * mm});
            skLineSegment(sketch, "E3550", {"start": v(77.42, -97.38) * mm, "end": v(77.37, -97.06) * mm});
            skLineSegment(sketch, "E3551", {"start": v(77.37, -97.06) * mm, "end": v(77.31, -96.74) * mm});
            skLineSegment(sketch, "E3552", {"start": v(77.31, -96.74) * mm, "end": v(77.26, -96.42) * mm});
            skLineSegment(sketch, "E3553", {"start": v(77.26, -96.42) * mm, "end": v(77.2, -96.11) * mm});
            skLineSegment(sketch, "E3554", {"start": v(77.2, -96.11) * mm, "end": v(77.14, -95.8) * mm});
            skLineSegment(sketch, "E3555", {"start": v(77.14, -95.8) * mm, "end": v(77.08, -95.5) * mm});
            skLineSegment(sketch, "E3556", {"start": v(77.08, -95.5) * mm, "end": v(77.02, -95.2) * mm});
            skLineSegment(sketch, "E3557", {"start": v(77.02, -95.2) * mm, "end": v(76.96, -94.9) * mm});
            skLineSegment(sketch, "E3558", {"start": v(76.96, -94.9) * mm, "end": v(76.9, -94.6) * mm});
            skLineSegment(sketch, "E3559", {"start": v(76.9, -94.6) * mm, "end": v(76.83, -94.3) * mm});
            skLineSegment(sketch, "E3560", {"start": v(76.83, -94.3) * mm, "end": v(76.77, -94.02) * mm});
            skLineSegment(sketch, "E3561", {"start": v(76.77, -94.02) * mm, "end": v(76.7, -93.74) * mm});
            skLineSegment(sketch, "E3562", {"start": v(76.7, -93.74) * mm, "end": v(76.64, -93.46) * mm});
            skLineSegment(sketch, "E3563", {"start": v(76.64, -93.46) * mm, "end": v(76.57, -93.18) * mm});
            skLineSegment(sketch, "E3564", {"start": v(76.57, -93.18) * mm, "end": v(76.5, -92.9) * mm});
            skLineSegment(sketch, "E3565", {"start": v(76.5, -92.9) * mm, "end": v(76.43, -92.64) * mm});
            skLineSegment(sketch, "E3566", {"start": v(76.43, -92.64) * mm, "end": v(76.36, -92.37) * mm});
            skLineSegment(sketch, "E3567", {"start": v(76.36, -92.37) * mm, "end": v(76.3, -92.1) * mm});
            skLineSegment(sketch, "E3568", {"start": v(76.3, -92.1) * mm, "end": v(76.22, -91.85) * mm});
            skLineSegment(sketch, "E3569", {"start": v(76.22, -91.85) * mm, "end": v(76.15, -91.6) * mm});
            skLineSegment(sketch, "E3570", {"start": v(76.15, -91.6) * mm, "end": v(76.08, -91.34) * mm});
            skLineSegment(sketch, "E3571", {"start": v(76.08, -91.34) * mm, "end": v(76, -91.1) * mm});
            skLineSegment(sketch, "E3572", {"start": v(76, -91.1) * mm, "end": v(75.94, -90.85) * mm});
            skLineSegment(sketch, "E3573", {"start": v(75.94, -90.85) * mm, "end": v(75.86, -90.6) * mm});
            skLineSegment(sketch, "E3574", {"start": v(75.86, -90.6) * mm, "end": v(76.55, -89.72) * mm});
            skLineSegment(sketch, "E3575", {"start": v(76.55, -89.72) * mm, "end": v(77.53, -89.2) * mm});
            skLineSegment(sketch, "E3576", {"start": v(77.53, -89.2) * mm, "end": v(77.76, -89.31) * mm});
            skLineSegment(sketch, "E3577", {"start": v(77.76, -89.31) * mm, "end": v(77.99, -89.42) * mm});
            skLineSegment(sketch, "E3578", {"start": v(77.99, -89.42) * mm, "end": v(78.22, -89.54) * mm});
            skLineSegment(sketch, "E3579", {"start": v(78.22, -89.54) * mm, "end": v(78.46, -89.65) * mm});
            skLineSegment(sketch, "E3580", {"start": v(78.46, -89.65) * mm, "end": v(78.7, -89.76) * mm});
            skLineSegment(sketch, "E3581", {"start": v(78.7, -89.76) * mm, "end": v(78.94, -89.88) * mm});
            skLineSegment(sketch, "E3582", {"start": v(78.94, -89.88) * mm, "end": v(79.19, -90) * mm});
            skLineSegment(sketch, "E3583", {"start": v(79.19, -90) * mm, "end": v(79.44, -90.1) * mm});
            skLineSegment(sketch, "E3584", {"start": v(79.44, -90.1) * mm, "end": v(79.7, -90.22) * mm});
            skLineSegment(sketch, "E3585", {"start": v(79.7, -90.22) * mm, "end": v(79.95, -90.33) * mm});
            skLineSegment(sketch, "E3586", {"start": v(79.95, -90.33) * mm, "end": v(80.21, -90.44) * mm});
            skLineSegment(sketch, "E3587", {"start": v(80.21, -90.44) * mm, "end": v(80.48, -90.56) * mm});
            skLineSegment(sketch, "E3588", {"start": v(80.48, -90.56) * mm, "end": v(80.75, -90.67) * mm});
            skLineSegment(sketch, "E3589", {"start": v(80.75, -90.67) * mm, "end": v(81.02, -90.78) * mm});
            skLineSegment(sketch, "E3590", {"start": v(81.02, -90.78) * mm, "end": v(81.3, -90.9) * mm});
            skLineSegment(sketch, "E3591", {"start": v(81.3, -90.9) * mm, "end": v(81.58, -91) * mm});
            skLineSegment(sketch, "E3592", {"start": v(81.58, -91) * mm, "end": v(81.86, -91.12) * mm});
            skLineSegment(sketch, "E3593", {"start": v(81.86, -91.12) * mm, "end": v(82.15, -91.23) * mm});
            skLineSegment(sketch, "E3594", {"start": v(82.15, -91.23) * mm, "end": v(82.44, -91.34) * mm});
            skLineSegment(sketch, "E3595", {"start": v(82.44, -91.34) * mm, "end": v(82.73, -91.45) * mm});
            skLineSegment(sketch, "E3596", {"start": v(82.73, -91.45) * mm, "end": v(83.03, -91.56) * mm});
            skLineSegment(sketch, "E3597", {"start": v(83.03, -91.56) * mm, "end": v(83.33, -91.67) * mm});
            skLineSegment(sketch, "E3598", {"start": v(83.33, -91.67) * mm, "end": v(83.64, -91.78) * mm});
            skLineSegment(sketch, "E3599", {"start": v(83.64, -91.78) * mm, "end": v(83.95, -91.88) * mm});
            skLineSegment(sketch, "E3600", {"start": v(83.95, -91.88) * mm, "end": v(84.26, -92) * mm});
            skLineSegment(sketch, "E3601", {"start": v(84.26, -92) * mm, "end": v(84.58, -92.1) * mm});
            skLineSegment(sketch, "E3602", {"start": v(84.58, -92.1) * mm, "end": v(84.9, -92.2) * mm});
            skLineSegment(sketch, "E3603", {"start": v(84.9, -92.2) * mm, "end": v(85.22, -92.31) * mm});
            skLineSegment(sketch, "E3604", {"start": v(85.22, -92.31) * mm, "end": v(85.55, -92.42) * mm});
            skLineSegment(sketch, "E3605", {"start": v(85.55, -92.42) * mm, "end": v(85.88, -92.52) * mm});
            skLineSegment(sketch, "E3606", {"start": v(85.88, -92.52) * mm, "end": v(86.02, -92.4) * mm});
            skLineSegment(sketch, "E3607", {"start": v(86.02, -92.4) * mm, "end": v(87.08, -91.42) * mm});
            skLineSegment(sketch, "E3608", {"start": v(87.08, -91.42) * mm, "end": v(87.2, -91.3) * mm});
            skLineSegment(sketch, "E3609", {"start": v(87.2, -91.3) * mm, "end": v(87.12, -90.95) * mm});
            skLineSegment(sketch, "E3610", {"start": v(87.12, -90.95) * mm, "end": v(87.04, -90.62) * mm});
            skLineSegment(sketch, "E3611", {"start": v(87.04, -90.62) * mm, "end": v(86.95, -90.29) * mm});
            skLineSegment(sketch, "E3612", {"start": v(86.95, -90.29) * mm, "end": v(86.87, -89.96) * mm});
            skLineSegment(sketch, "E3613", {"start": v(86.87, -89.96) * mm, "end": v(86.79, -89.64) * mm});
            skLineSegment(sketch, "E3614", {"start": v(86.79, -89.64) * mm, "end": v(86.7, -89.32) * mm});
            skLineSegment(sketch, "E3615", {"start": v(86.7, -89.32) * mm, "end": v(86.62, -89) * mm});
            skLineSegment(sketch, "E3616", {"start": v(86.62, -89) * mm, "end": v(86.53, -88.7) * mm});
            skLineSegment(sketch, "E3617", {"start": v(86.53, -88.7) * mm, "end": v(86.44, -88.38) * mm});
            skLineSegment(sketch, "E3618", {"start": v(86.44, -88.38) * mm, "end": v(86.36, -88.08) * mm});
            skLineSegment(sketch, "E3619", {"start": v(86.36, -88.08) * mm, "end": v(86.27, -87.77) * mm});
            skLineSegment(sketch, "E3620", {"start": v(86.27, -87.77) * mm, "end": v(86.18, -87.48) * mm});
            skLineSegment(sketch, "E3621", {"start": v(86.18, -87.48) * mm, "end": v(86.09, -87.18) * mm});
            skLineSegment(sketch, "E3622", {"start": v(86.09, -87.18) * mm, "end": v(86, -86.9) * mm});
            skLineSegment(sketch, "E3623", {"start": v(86, -86.9) * mm, "end": v(85.9, -86.6) * mm});
            skLineSegment(sketch, "E3624", {"start": v(85.9, -86.6) * mm, "end": v(85.81, -86.32) * mm});
            skLineSegment(sketch, "E3625", {"start": v(85.81, -86.32) * mm, "end": v(85.72, -86.04) * mm});
            skLineSegment(sketch, "E3626", {"start": v(85.72, -86.04) * mm, "end": v(85.63, -85.76) * mm});
            skLineSegment(sketch, "E3627", {"start": v(85.63, -85.76) * mm, "end": v(85.54, -85.5) * mm});
            skLineSegment(sketch, "E3628", {"start": v(85.54, -85.5) * mm, "end": v(85.44, -85.22) * mm});
            skLineSegment(sketch, "E3629", {"start": v(85.44, -85.22) * mm, "end": v(85.35, -84.96) * mm});
            skLineSegment(sketch, "E3630", {"start": v(85.35, -84.96) * mm, "end": v(85.25, -84.7) * mm});
            skLineSegment(sketch, "E3631", {"start": v(85.25, -84.7) * mm, "end": v(85.16, -84.44) * mm});
            skLineSegment(sketch, "E3632", {"start": v(85.16, -84.44) * mm, "end": v(85.06, -84.18) * mm});
            skLineSegment(sketch, "E3633", {"start": v(85.06, -84.18) * mm, "end": v(84.97, -83.93) * mm});
            skLineSegment(sketch, "E3634", {"start": v(84.97, -83.93) * mm, "end": v(84.87, -83.68) * mm});
            skLineSegment(sketch, "E3635", {"start": v(84.87, -83.68) * mm, "end": v(84.78, -83.44) * mm});
            skLineSegment(sketch, "E3636", {"start": v(84.78, -83.44) * mm, "end": v(84.68, -83.2) * mm});
            skLineSegment(sketch, "E3637", {"start": v(84.68, -83.2) * mm, "end": v(84.58, -82.96) * mm});
            skLineSegment(sketch, "E3638", {"start": v(84.58, -82.96) * mm, "end": v(84.49, -82.73) * mm});
            skLineSegment(sketch, "E3639", {"start": v(84.49, -82.73) * mm, "end": v(85.08, -81.78) * mm});
            skLineSegment(sketch, "E3640", {"start": v(85.08, -81.78) * mm, "end": v(86, -81.17) * mm});
            skLineSegment(sketch, "E3641", {"start": v(86, -81.17) * mm, "end": v(86.24, -81.25) * mm});
            skLineSegment(sketch, "E3642", {"start": v(86.24, -81.25) * mm, "end": v(86.48, -81.34) * mm});
            skLineSegment(sketch, "E3643", {"start": v(86.48, -81.34) * mm, "end": v(86.73, -81.43) * mm});
            skLineSegment(sketch, "E3644", {"start": v(86.73, -81.43) * mm, "end": v(86.97, -81.52) * mm});
            skLineSegment(sketch, "E3645", {"start": v(86.97, -81.52) * mm, "end": v(87.22, -81.61) * mm});
            skLineSegment(sketch, "E3646", {"start": v(87.22, -81.61) * mm, "end": v(87.48, -81.7) * mm});
            skLineSegment(sketch, "E3647", {"start": v(87.48, -81.7) * mm, "end": v(87.74, -81.79) * mm});
            skLineSegment(sketch, "E3648", {"start": v(87.74, -81.79) * mm, "end": v(88, -81.88) * mm});
            skLineSegment(sketch, "E3649", {"start": v(88, -81.88) * mm, "end": v(88.26, -81.97) * mm});
            skLineSegment(sketch, "E3650", {"start": v(88.26, -81.97) * mm, "end": v(88.53, -82.05) * mm});
            skLineSegment(sketch, "E3651", {"start": v(88.53, -82.05) * mm, "end": v(88.8, -82.14) * mm});
            skLineSegment(sketch, "E3652", {"start": v(88.8, -82.14) * mm, "end": v(89.08, -82.23) * mm});
            skLineSegment(sketch, "E3653", {"start": v(89.08, -82.23) * mm, "end": v(89.35, -82.31) * mm});
            skLineSegment(sketch, "E3654", {"start": v(89.35, -82.31) * mm, "end": v(89.64, -82.4) * mm});
            skLineSegment(sketch, "E3655", {"start": v(89.64, -82.4) * mm, "end": v(89.92, -82.48) * mm});
            skLineSegment(sketch, "E3656", {"start": v(89.92, -82.48) * mm, "end": v(90.21, -82.56) * mm});
            skLineSegment(sketch, "E3657", {"start": v(90.21, -82.56) * mm, "end": v(90.5, -82.65) * mm});
            skLineSegment(sketch, "E3658", {"start": v(90.5, -82.65) * mm, "end": v(90.8, -82.73) * mm});
            skLineSegment(sketch, "E3659", {"start": v(90.8, -82.73) * mm, "end": v(91.1, -82.81) * mm});
            skLineSegment(sketch, "E3660", {"start": v(91.1, -82.81) * mm, "end": v(91.4, -82.9) * mm});
            skLineSegment(sketch, "E3661", {"start": v(91.4, -82.9) * mm, "end": v(91.71, -82.97) * mm});
            skLineSegment(sketch, "E3662", {"start": v(91.71, -82.97) * mm, "end": v(92.02, -83.05) * mm});
            skLineSegment(sketch, "E3663", {"start": v(92.02, -83.05) * mm, "end": v(92.34, -83.13) * mm});
            skLineSegment(sketch, "E3664", {"start": v(92.34, -83.13) * mm, "end": v(92.66, -83.2) * mm});
            skLineSegment(sketch, "E3665", {"start": v(92.66, -83.2) * mm, "end": v(92.98, -83.28) * mm});
            skLineSegment(sketch, "E3666", {"start": v(92.98, -83.28) * mm, "end": v(93.3, -83.36) * mm});
            skLineSegment(sketch, "E3667", {"start": v(93.3, -83.36) * mm, "end": v(93.63, -83.43) * mm});
            skLineSegment(sketch, "E3668", {"start": v(93.63, -83.43) * mm, "end": v(93.97, -83.5) * mm});
            skLineSegment(sketch, "E3669", {"start": v(93.97, -83.5) * mm, "end": v(94.3, -83.58) * mm});
            skLineSegment(sketch, "E3670", {"start": v(94.3, -83.58) * mm, "end": v(94.64, -83.65) * mm});
            skLineSegment(sketch, "E3671", {"start": v(94.64, -83.65) * mm, "end": v(94.77, -83.53) * mm});
            skLineSegment(sketch, "E3672", {"start": v(94.77, -83.53) * mm, "end": v(95.73, -82.44) * mm});
            skLineSegment(sketch, "E3673", {"start": v(95.73, -82.44) * mm, "end": v(95.83, -82.3) * mm});
            skLineSegment(sketch, "E3674", {"start": v(95.83, -82.3) * mm, "end": v(95.72, -81.97) * mm});
            skLineSegment(sketch, "E3675", {"start": v(95.72, -81.97) * mm, "end": v(95.6, -81.65) * mm});
            skLineSegment(sketch, "E3676", {"start": v(95.6, -81.65) * mm, "end": v(95.5, -81.33) * mm});
            skLineSegment(sketch, "E3677", {"start": v(95.5, -81.33) * mm, "end": v(95.38, -81) * mm});
            skLineSegment(sketch, "E3678", {"start": v(95.38, -81) * mm, "end": v(95.27, -80.7) * mm});
            skLineSegment(sketch, "E3679", {"start": v(95.27, -80.7) * mm, "end": v(95.15, -80.38) * mm});
            skLineSegment(sketch, "E3680", {"start": v(95.15, -80.38) * mm, "end": v(95.03, -80.08) * mm});
            skLineSegment(sketch, "E3681", {"start": v(95.03, -80.08) * mm, "end": v(94.92, -79.78) * mm});
            skLineSegment(sketch, "E3682", {"start": v(94.92, -79.78) * mm, "end": v(94.8, -79.48) * mm});
            skLineSegment(sketch, "E3683", {"start": v(94.8, -79.48) * mm, "end": v(94.68, -79.18) * mm});
            skLineSegment(sketch, "E3684", {"start": v(94.68, -79.18) * mm, "end": v(94.56, -78.9) * mm});
            skLineSegment(sketch, "E3685", {"start": v(94.56, -78.9) * mm, "end": v(94.45, -78.6) * mm});
            skLineSegment(sketch, "E3686", {"start": v(94.45, -78.6) * mm, "end": v(94.33, -78.32) * mm});
            skLineSegment(sketch, "E3687", {"start": v(94.33, -78.32) * mm, "end": v(94.2, -78.04) * mm});
            skLineSegment(sketch, "E3688", {"start": v(94.2, -78.04) * mm, "end": v(94.1, -77.76) * mm});
            skLineSegment(sketch, "E3689", {"start": v(94.1, -77.76) * mm, "end": v(93.97, -77.49) * mm});
            skLineSegment(sketch, "E3690", {"start": v(93.97, -77.49) * mm, "end": v(93.85, -77.22) * mm});
            skLineSegment(sketch, "E3691", {"start": v(93.85, -77.22) * mm, "end": v(93.73, -76.95) * mm});
            skLineSegment(sketch, "E3692", {"start": v(93.73, -76.95) * mm, "end": v(93.61, -76.7) * mm});
            skLineSegment(sketch, "E3693", {"start": v(93.61, -76.7) * mm, "end": v(93.5, -76.43) * mm});
            skLineSegment(sketch, "E3694", {"start": v(93.5, -76.43) * mm, "end": v(93.37, -76.18) * mm});
            skLineSegment(sketch, "E3695", {"start": v(93.37, -76.18) * mm, "end": v(93.25, -75.92) * mm});
            skLineSegment(sketch, "E3696", {"start": v(93.25, -75.92) * mm, "end": v(93.13, -75.68) * mm});
            skLineSegment(sketch, "E3697", {"start": v(93.13, -75.68) * mm, "end": v(93.01, -75.43) * mm});
            skLineSegment(sketch, "E3698", {"start": v(93.01, -75.43) * mm, "end": v(92.9, -75.2) * mm});
            skLineSegment(sketch, "E3699", {"start": v(92.9, -75.2) * mm, "end": v(92.77, -74.95) * mm});
            skLineSegment(sketch, "E3700", {"start": v(92.77, -74.95) * mm, "end": v(92.66, -74.72) * mm});
            skLineSegment(sketch, "E3701", {"start": v(92.66, -74.72) * mm, "end": v(92.54, -74.5) * mm});
            skLineSegment(sketch, "E3702", {"start": v(92.54, -74.5) * mm, "end": v(92.42, -74.26) * mm});
            skLineSegment(sketch, "E3703", {"start": v(92.42, -74.26) * mm, "end": v(92.3, -74.04) * mm});
            skLineSegment(sketch, "E3704", {"start": v(92.3, -74.04) * mm, "end": v(92.8, -73.04) * mm});
            skLineSegment(sketch, "E3705", {"start": v(92.8, -73.04) * mm, "end": v(93.66, -72.34) * mm});
            skLineSegment(sketch, "E3706", {"start": v(93.66, -72.34) * mm, "end": v(93.9, -72.4) * mm});
            skLineSegment(sketch, "E3707", {"start": v(93.9, -72.4) * mm, "end": v(94.15, -72.47) * mm});
            skLineSegment(sketch, "E3708", {"start": v(94.15, -72.47) * mm, "end": v(94.4, -72.54) * mm});
            skLineSegment(sketch, "E3709", {"start": v(94.4, -72.54) * mm, "end": v(94.66, -72.6) * mm});
            skLineSegment(sketch, "E3710", {"start": v(94.66, -72.6) * mm, "end": v(94.91, -72.66) * mm});
            skLineSegment(sketch, "E3711", {"start": v(94.91, -72.66) * mm, "end": v(95.17, -72.73) * mm});
            skLineSegment(sketch, "E3712", {"start": v(95.17, -72.73) * mm, "end": v(95.44, -72.8) * mm});
            skLineSegment(sketch, "E3713", {"start": v(95.44, -72.8) * mm, "end": v(95.7, -72.85) * mm});
            skLineSegment(sketch, "E3714", {"start": v(95.7, -72.85) * mm, "end": v(95.98, -72.91) * mm});
            skLineSegment(sketch, "E3715", {"start": v(95.98, -72.91) * mm, "end": v(96.25, -72.98) * mm});
            skLineSegment(sketch, "E3716", {"start": v(96.25, -72.98) * mm, "end": v(96.53, -73.03) * mm});
            skLineSegment(sketch, "E3717", {"start": v(96.53, -73.03) * mm, "end": v(96.81, -73.1) * mm});
            skLineSegment(sketch, "E3718", {"start": v(96.81, -73.1) * mm, "end": v(97.1, -73.15) * mm});
            skLineSegment(sketch, "E3719", {"start": v(97.1, -73.15) * mm, "end": v(97.4, -73.2) * mm});
            skLineSegment(sketch, "E3720", {"start": v(97.4, -73.2) * mm, "end": v(97.68, -73.26) * mm});
            skLineSegment(sketch, "E3721", {"start": v(97.68, -73.26) * mm, "end": v(97.98, -73.32) * mm});
            skLineSegment(sketch, "E3722", {"start": v(97.98, -73.32) * mm, "end": v(98.28, -73.37) * mm});
            skLineSegment(sketch, "E3723", {"start": v(98.28, -73.37) * mm, "end": v(98.58, -73.43) * mm});
            skLineSegment(sketch, "E3724", {"start": v(98.58, -73.43) * mm, "end": v(98.89, -73.48) * mm});
            skLineSegment(sketch, "E3725", {"start": v(98.89, -73.48) * mm, "end": v(99.2, -73.53) * mm});
            skLineSegment(sketch, "E3726", {"start": v(99.2, -73.53) * mm, "end": v(99.51, -73.58) * mm});
            skLineSegment(sketch, "E3727", {"start": v(99.51, -73.58) * mm, "end": v(99.83, -73.63) * mm});
            skLineSegment(sketch, "E3728", {"start": v(99.83, -73.63) * mm, "end": v(100.15, -73.67) * mm});
            skLineSegment(sketch, "E3729", {"start": v(100.15, -73.67) * mm, "end": v(100.47, -73.72) * mm});
            skLineSegment(sketch, "E3730", {"start": v(100.47, -73.72) * mm, "end": v(100.8, -73.76) * mm});
            skLineSegment(sketch, "E3731", {"start": v(100.8, -73.76) * mm, "end": v(101.13, -73.8) * mm});
            skLineSegment(sketch, "E3732", {"start": v(101.13, -73.8) * mm, "end": v(101.47, -73.85) * mm});
            skLineSegment(sketch, "E3733", {"start": v(101.47, -73.85) * mm, "end": v(101.8, -73.89) * mm});
            skLineSegment(sketch, "E3734", {"start": v(101.8, -73.89) * mm, "end": v(102.15, -73.93) * mm});
            skLineSegment(sketch, "E3735", {"start": v(102.15, -73.93) * mm, "end": v(102.5, -73.97) * mm});
            skLineSegment(sketch, "E3736", {"start": v(102.5, -73.97) * mm, "end": v(102.6, -73.83) * mm});
            skLineSegment(sketch, "E3737", {"start": v(102.6, -73.83) * mm, "end": v(103.46, -72.66) * mm});
            skLineSegment(sketch, "E3738", {"start": v(103.46, -72.66) * mm, "end": v(103.55, -72.5) * mm});
            skLineSegment(sketch, "E3739", {"start": v(103.55, -72.5) * mm, "end": v(103.4, -72.19) * mm});
            skLineSegment(sketch, "E3740", {"start": v(103.4, -72.19) * mm, "end": v(103.26, -71.88) * mm});
            skLineSegment(sketch, "E3741", {"start": v(103.26, -71.88) * mm, "end": v(103.12, -71.57) * mm});
            skLineSegment(sketch, "E3742", {"start": v(103.12, -71.57) * mm, "end": v(102.97, -71.26) * mm});
            skLineSegment(sketch, "E3743", {"start": v(102.97, -71.26) * mm, "end": v(102.82, -70.96) * mm});
            skLineSegment(sketch, "E3744", {"start": v(102.82, -70.96) * mm, "end": v(102.68, -70.67) * mm});
            skLineSegment(sketch, "E3745", {"start": v(102.68, -70.67) * mm, "end": v(102.53, -70.37) * mm});
            skLineSegment(sketch, "E3746", {"start": v(102.53, -70.37) * mm, "end": v(102.39, -70.08) * mm});
            skLineSegment(sketch, "E3747", {"start": v(102.39, -70.08) * mm, "end": v(102.24, -69.8) * mm});
            skLineSegment(sketch, "E3748", {"start": v(102.24, -69.8) * mm, "end": v(102.1, -69.51) * mm});
            skLineSegment(sketch, "E3749", {"start": v(102.1, -69.51) * mm, "end": v(101.95, -69.24) * mm});
            skLineSegment(sketch, "E3750", {"start": v(101.95, -69.24) * mm, "end": v(101.8, -68.96) * mm});
            skLineSegment(sketch, "E3751", {"start": v(101.8, -68.96) * mm, "end": v(101.66, -68.7) * mm});
            skLineSegment(sketch, "E3752", {"start": v(101.66, -68.7) * mm, "end": v(101.51, -68.42) * mm});
            skLineSegment(sketch, "E3753", {"start": v(101.51, -68.42) * mm, "end": v(101.37, -68.16) * mm});
            skLineSegment(sketch, "E3754", {"start": v(101.37, -68.16) * mm, "end": v(101.22, -67.9) * mm});
            skLineSegment(sketch, "E3755", {"start": v(101.22, -67.9) * mm, "end": v(101.07, -67.64) * mm});
            skLineSegment(sketch, "E3756", {"start": v(101.07, -67.64) * mm, "end": v(100.93, -67.39) * mm});
            skLineSegment(sketch, "E3757", {"start": v(100.93, -67.39) * mm, "end": v(100.78, -67.14) * mm});
            skLineSegment(sketch, "E3758", {"start": v(100.78, -67.14) * mm, "end": v(100.64, -66.9) * mm});
            skLineSegment(sketch, "E3759", {"start": v(100.64, -66.9) * mm, "end": v(100.5, -66.65) * mm});
            skLineSegment(sketch, "E3760", {"start": v(100.5, -66.65) * mm, "end": v(100.35, -66.41) * mm});
            skLineSegment(sketch, "E3761", {"start": v(100.35, -66.41) * mm, "end": v(100.2, -66.18) * mm});
            skLineSegment(sketch, "E3762", {"start": v(100.2, -66.18) * mm, "end": v(100.07, -65.95) * mm});
            skLineSegment(sketch, "E3763", {"start": v(100.07, -65.95) * mm, "end": v(99.92, -65.72) * mm});
            skLineSegment(sketch, "E3764", {"start": v(99.92, -65.72) * mm, "end": v(99.78, -65.5) * mm});
            skLineSegment(sketch, "E3765", {"start": v(99.78, -65.5) * mm, "end": v(99.64, -65.27) * mm});
            skLineSegment(sketch, "E3766", {"start": v(99.64, -65.27) * mm, "end": v(99.5, -65.06) * mm});
            skLineSegment(sketch, "E3767", {"start": v(99.5, -65.06) * mm, "end": v(99.36, -64.84) * mm});
            skLineSegment(sketch, "E3768", {"start": v(99.36, -64.84) * mm, "end": v(99.22, -64.63) * mm});
            skLineSegment(sketch, "E3769", {"start": v(99.22, -64.63) * mm, "end": v(99.62, -63.6) * mm});
            skLineSegment(sketch, "E3770", {"start": v(99.62, -63.6) * mm, "end": v(100.4, -62.8) * mm});
            skLineSegment(sketch, "E3771", {"start": v(100.4, -62.8) * mm, "end": v(100.66, -62.85) * mm});
            skLineSegment(sketch, "E3772", {"start": v(100.66, -62.85) * mm, "end": v(100.9, -62.89) * mm});
            skLineSegment(sketch, "E3773", {"start": v(100.9, -62.89) * mm, "end": v(101.16, -62.93) * mm});
            skLineSegment(sketch, "E3774", {"start": v(101.16, -62.93) * mm, "end": v(101.42, -62.97) * mm});
            skLineSegment(sketch, "E3775", {"start": v(101.42, -62.97) * mm, "end": v(101.69, -63) * mm});
            skLineSegment(sketch, "E3776", {"start": v(101.69, -63) * mm, "end": v(101.95, -63.04) * mm});
            skLineSegment(sketch, "E3777", {"start": v(101.95, -63.04) * mm, "end": v(102.22, -63.08) * mm});
            skLineSegment(sketch, "E3778", {"start": v(102.22, -63.08) * mm, "end": v(102.5, -63.12) * mm});
            skLineSegment(sketch, "E3779", {"start": v(102.5, -63.12) * mm, "end": v(102.77, -63.15) * mm});
            skLineSegment(sketch, "E3780", {"start": v(102.77, -63.15) * mm, "end": v(103.05, -63.18) * mm});
            skLineSegment(sketch, "E3781", {"start": v(103.05, -63.18) * mm, "end": v(103.33, -63.22) * mm});
            skLineSegment(sketch, "E3782", {"start": v(103.33, -63.22) * mm, "end": v(103.62, -63.25) * mm});
            skLineSegment(sketch, "E3783", {"start": v(103.62, -63.25) * mm, "end": v(103.91, -63.28) * mm});
            skLineSegment(sketch, "E3784", {"start": v(103.91, -63.28) * mm, "end": v(104.2, -63.3) * mm});
            skLineSegment(sketch, "E3785", {"start": v(104.2, -63.3) * mm, "end": v(104.5, -63.33) * mm});
            skLineSegment(sketch, "E3786", {"start": v(104.5, -63.33) * mm, "end": v(104.8, -63.36) * mm});
            skLineSegment(sketch, "E3787", {"start": v(104.8, -63.36) * mm, "end": v(105.1, -63.38) * mm});
            skLineSegment(sketch, "E3788", {"start": v(105.1, -63.38) * mm, "end": v(105.41, -63.4) * mm});
            skLineSegment(sketch, "E3789", {"start": v(105.41, -63.4) * mm, "end": v(105.72, -63.43) * mm});
            skLineSegment(sketch, "E3790", {"start": v(105.72, -63.43) * mm, "end": v(106.04, -63.45) * mm});
            skLineSegment(sketch, "E3791", {"start": v(106.04, -63.45) * mm, "end": v(106.35, -63.47) * mm});
            skLineSegment(sketch, "E3792", {"start": v(106.35, -63.47) * mm, "end": v(106.67, -63.48) * mm});
            skLineSegment(sketch, "E3793", {"start": v(106.67, -63.48) * mm, "end": v(107, -63.5) * mm});
            skLineSegment(sketch, "E3794", {"start": v(107, -63.5) * mm, "end": v(107.33, -63.51) * mm});
            skLineSegment(sketch, "E3795", {"start": v(107.33, -63.51) * mm, "end": v(107.66, -63.52) * mm});
            skLineSegment(sketch, "E3796", {"start": v(107.66, -63.52) * mm, "end": v(108, -63.53) * mm});
            skLineSegment(sketch, "E3797", {"start": v(108, -63.53) * mm, "end": v(108.33, -63.54) * mm});
            skLineSegment(sketch, "E3798", {"start": v(108.33, -63.54) * mm, "end": v(108.67, -63.55) * mm});
            skLineSegment(sketch, "E3799", {"start": v(108.67, -63.55) * mm, "end": v(109.01, -63.56) * mm});
            skLineSegment(sketch, "E3800", {"start": v(109.01, -63.56) * mm, "end": v(109.36, -63.56) * mm});
            skLineSegment(sketch, "E3801", {"start": v(109.36, -63.56) * mm, "end": v(109.46, -63.41) * mm});
            skLineSegment(sketch, "E3802", {"start": v(109.46, -63.41) * mm, "end": v(110.19, -62.16) * mm});
            skLineSegment(sketch, "E3803", {"start": v(110.19, -62.16) * mm, "end": v(110.26, -62) * mm});
            skLineSegment(sketch, "E3804", {"start": v(110.26, -62) * mm, "end": v(110.1, -61.7) * mm});
            skLineSegment(sketch, "E3805", {"start": v(110.1, -61.7) * mm, "end": v(109.92, -61.4) * mm});
            skLineSegment(sketch, "E3806", {"start": v(109.92, -61.4) * mm, "end": v(109.74, -61.11) * mm});
            skLineSegment(sketch, "E3807", {"start": v(109.74, -61.11) * mm, "end": v(109.57, -60.82) * mm});
            skLineSegment(sketch, "E3808", {"start": v(109.57, -60.82) * mm, "end": v(109.4, -60.54) * mm});
            skLineSegment(sketch, "E3809", {"start": v(109.4, -60.54) * mm, "end": v(109.22, -60.26) * mm});
            skLineSegment(sketch, "E3810", {"start": v(109.22, -60.26) * mm, "end": v(109.05, -59.98) * mm});
            skLineSegment(sketch, "E3811", {"start": v(109.05, -59.98) * mm, "end": v(108.87, -59.7) * mm});
            skLineSegment(sketch, "E3812", {"start": v(108.87, -59.7) * mm, "end": v(108.7, -59.43) * mm});
            skLineSegment(sketch, "E3813", {"start": v(108.7, -59.43) * mm, "end": v(108.53, -59.17) * mm});
            skLineSegment(sketch, "E3814", {"start": v(108.53, -59.17) * mm, "end": v(108.35, -58.9) * mm});
            skLineSegment(sketch, "E3815", {"start": v(108.35, -58.9) * mm, "end": v(108.18, -58.65) * mm});
            skLineSegment(sketch, "E3816", {"start": v(108.18, -58.65) * mm, "end": v(108, -58.39) * mm});
            skLineSegment(sketch, "E3817", {"start": v(108, -58.39) * mm, "end": v(107.84, -58.14) * mm});
            skLineSegment(sketch, "E3818", {"start": v(107.84, -58.14) * mm, "end": v(107.67, -57.89) * mm});
            skLineSegment(sketch, "E3819", {"start": v(107.67, -57.89) * mm, "end": v(107.5, -57.64) * mm});
            skLineSegment(sketch, "E3820", {"start": v(107.5, -57.64) * mm, "end": v(107.33, -57.4) * mm});
            skLineSegment(sketch, "E3821", {"start": v(107.33, -57.4) * mm, "end": v(107.16, -57.17) * mm});
            skLineSegment(sketch, "E3822", {"start": v(107.16, -57.17) * mm, "end": v(107, -56.93) * mm});
            skLineSegment(sketch, "E3823", {"start": v(107, -56.93) * mm, "end": v(106.82, -56.7) * mm});
            skLineSegment(sketch, "E3824", {"start": v(106.82, -56.7) * mm, "end": v(106.65, -56.48) * mm});
            skLineSegment(sketch, "E3825", {"start": v(106.65, -56.48) * mm, "end": v(106.49, -56.25) * mm});
            skLineSegment(sketch, "E3826", {"start": v(106.49, -56.25) * mm, "end": v(106.32, -56.03) * mm});
            skLineSegment(sketch, "E3827", {"start": v(106.32, -56.03) * mm, "end": v(106.16, -55.82) * mm});
            skLineSegment(sketch, "E3828", {"start": v(106.16, -55.82) * mm, "end": v(106, -55.6) * mm});
            skLineSegment(sketch, "E3829", {"start": v(106, -55.6) * mm, "end": v(105.83, -55.4) * mm});
            skLineSegment(sketch, "E3830", {"start": v(105.83, -55.4) * mm, "end": v(105.67, -55.19) * mm});
            skLineSegment(sketch, "E3831", {"start": v(105.67, -55.19) * mm, "end": v(105.5, -54.99) * mm});
            skLineSegment(sketch, "E3832", {"start": v(105.5, -54.99) * mm, "end": v(105.35, -54.79) * mm});
            skLineSegment(sketch, "E3833", {"start": v(105.35, -54.79) * mm, "end": v(105.19, -54.6) * mm});
            skLineSegment(sketch, "E3834", {"start": v(105.19, -54.6) * mm, "end": v(105.48, -53.51) * mm});
            skLineSegment(sketch, "E3835", {"start": v(105.48, -53.51) * mm, "end": v(106.19, -52.66) * mm});
            skLineSegment(sketch, "E3836", {"start": v(106.19, -52.66) * mm, "end": v(106.44, -52.67) * mm});
            skLineSegment(sketch, "E3837", {"start": v(106.44, -52.67) * mm, "end": v(106.7, -52.69) * mm});
            skLineSegment(sketch, "E3838", {"start": v(106.7, -52.69) * mm, "end": v(106.95, -52.7) * mm});
            skLineSegment(sketch, "E3839", {"start": v(106.95, -52.7) * mm, "end": v(107.21, -52.72) * mm});
            skLineSegment(sketch, "E3840", {"start": v(107.21, -52.72) * mm, "end": v(107.48, -52.73) * mm});
            skLineSegment(sketch, "E3841", {"start": v(107.48, -52.73) * mm, "end": v(107.75, -52.74) * mm});
            skLineSegment(sketch, "E3842", {"start": v(107.75, -52.74) * mm, "end": v(108.02, -52.75) * mm});
            skLineSegment(sketch, "E3843", {"start": v(108.02, -52.75) * mm, "end": v(108.3, -52.76) * mm});
            skLineSegment(sketch, "E3844", {"start": v(108.3, -52.76) * mm, "end": v(108.57, -52.77) * mm});
            skLineSegment(sketch, "E3845", {"start": v(108.57, -52.77) * mm, "end": v(108.86, -52.77) * mm});
            skLineSegment(sketch, "E3846", {"start": v(108.86, -52.77) * mm, "end": v(109.14, -52.78) * mm});
            skLineSegment(sketch, "E3847", {"start": v(109.14, -52.78) * mm, "end": v(109.43, -52.78) * mm});
            skLineSegment(sketch, "E3848", {"start": v(109.43, -52.78) * mm, "end": v(109.72, -52.78) * mm});
            skLineSegment(sketch, "E3849", {"start": v(109.72, -52.78) * mm, "end": v(110.02, -52.78) * mm});
            skLineSegment(sketch, "E3850", {"start": v(110.02, -52.78) * mm, "end": v(110.32, -52.78) * mm});
            skLineSegment(sketch, "E3851", {"start": v(110.32, -52.78) * mm, "end": v(110.62, -52.78) * mm});
            skLineSegment(sketch, "E3852", {"start": v(110.62, -52.78) * mm, "end": v(110.92, -52.77) * mm});
            skLineSegment(sketch, "E3853", {"start": v(110.92, -52.77) * mm, "end": v(111.23, -52.76) * mm});
            skLineSegment(sketch, "E3854", {"start": v(111.23, -52.76) * mm, "end": v(111.54, -52.75) * mm});
            skLineSegment(sketch, "E3855", {"start": v(111.54, -52.75) * mm, "end": v(111.85, -52.74) * mm});
            skLineSegment(sketch, "E3856", {"start": v(111.85, -52.74) * mm, "end": v(112.17, -52.73) * mm});
            skLineSegment(sketch, "E3857", {"start": v(112.17, -52.73) * mm, "end": v(112.5, -52.72) * mm});
            skLineSegment(sketch, "E3858", {"start": v(112.5, -52.72) * mm, "end": v(112.82, -52.7) * mm});
            skLineSegment(sketch, "E3859", {"start": v(112.82, -52.7) * mm, "end": v(113.14, -52.68) * mm});
            skLineSegment(sketch, "E3860", {"start": v(113.14, -52.68) * mm, "end": v(113.47, -52.66) * mm});
            skLineSegment(sketch, "E3861", {"start": v(113.47, -52.66) * mm, "end": v(113.8, -52.64) * mm});
            skLineSegment(sketch, "E3862", {"start": v(113.8, -52.64) * mm, "end": v(114.14, -52.61) * mm});
            skLineSegment(sketch, "E3863", {"start": v(114.14, -52.61) * mm, "end": v(114.48, -52.59) * mm});
            skLineSegment(sketch, "E3864", {"start": v(114.48, -52.59) * mm, "end": v(114.82, -52.56) * mm});
            skLineSegment(sketch, "E3865", {"start": v(114.82, -52.56) * mm, "end": v(115.17, -52.53) * mm});
            skLineSegment(sketch, "E3866", {"start": v(115.17, -52.53) * mm, "end": v(115.26, -52.37) * mm});
            skLineSegment(sketch, "E3867", {"start": v(115.26, -52.37) * mm, "end": v(115.86, -51.06) * mm});
            skLineSegment(sketch, "E3868", {"start": v(115.86, -51.06) * mm, "end": v(115.92, -50.89) * mm});
            skLineSegment(sketch, "E3869", {"start": v(115.92, -50.89) * mm, "end": v(115.72, -50.6) * mm});
            skLineSegment(sketch, "E3870", {"start": v(115.72, -50.6) * mm, "end": v(115.52, -50.33) * mm});
            skLineSegment(sketch, "E3871", {"start": v(115.52, -50.33) * mm, "end": v(115.31, -50.06) * mm});
            skLineSegment(sketch, "E3872", {"start": v(115.31, -50.06) * mm, "end": v(115.11, -49.79) * mm});
            skLineSegment(sketch, "E3873", {"start": v(115.11, -49.79) * mm, "end": v(114.9, -49.52) * mm});
            skLineSegment(sketch, "E3874", {"start": v(114.9, -49.52) * mm, "end": v(114.7, -49.26) * mm});
            skLineSegment(sketch, "E3875", {"start": v(114.7, -49.26) * mm, "end": v(114.5, -49) * mm});
            skLineSegment(sketch, "E3876", {"start": v(114.5, -49) * mm, "end": v(114.3, -48.74) * mm});
            skLineSegment(sketch, "E3877", {"start": v(114.3, -48.74) * mm, "end": v(114.11, -48.49) * mm});
            skLineSegment(sketch, "E3878", {"start": v(114.11, -48.49) * mm, "end": v(113.91, -48.24) * mm});
            skLineSegment(sketch, "E3879", {"start": v(113.91, -48.24) * mm, "end": v(113.71, -48) * mm});
            skLineSegment(sketch, "E3880", {"start": v(113.71, -48) * mm, "end": v(113.52, -47.75) * mm});
            skLineSegment(sketch, "E3881", {"start": v(113.52, -47.75) * mm, "end": v(113.32, -47.52) * mm});
            skLineSegment(sketch, "E3882", {"start": v(113.32, -47.52) * mm, "end": v(113.13, -47.28) * mm});
            skLineSegment(sketch, "E3883", {"start": v(113.13, -47.28) * mm, "end": v(112.93, -47.05) * mm});
            skLineSegment(sketch, "E3884", {"start": v(112.93, -47.05) * mm, "end": v(112.74, -46.83) * mm});
            skLineSegment(sketch, "E3885", {"start": v(112.74, -46.83) * mm, "end": v(112.54, -46.6) * mm});
            skLineSegment(sketch, "E3886", {"start": v(112.54, -46.6) * mm, "end": v(112.35, -46.38) * mm});
            skLineSegment(sketch, "E3887", {"start": v(112.35, -46.38) * mm, "end": v(112.16, -46.17) * mm});
            skLineSegment(sketch, "E3888", {"start": v(112.16, -46.17) * mm, "end": v(111.97, -45.95) * mm});
            skLineSegment(sketch, "E3889", {"start": v(111.97, -45.95) * mm, "end": v(111.78, -45.74) * mm});
            skLineSegment(sketch, "E3890", {"start": v(111.78, -45.74) * mm, "end": v(111.6, -45.54) * mm});
            skLineSegment(sketch, "E3891", {"start": v(111.6, -45.54) * mm, "end": v(111.41, -45.34) * mm});
            skLineSegment(sketch, "E3892", {"start": v(111.41, -45.34) * mm, "end": v(111.22, -45.14) * mm});
            skLineSegment(sketch, "E3893", {"start": v(111.22, -45.14) * mm, "end": v(111.04, -44.94) * mm});
            skLineSegment(sketch, "E3894", {"start": v(111.04, -44.94) * mm, "end": v(110.86, -44.75) * mm});
            skLineSegment(sketch, "E3895", {"start": v(110.86, -44.75) * mm, "end": v(110.68, -44.56) * mm});
            skLineSegment(sketch, "E3896", {"start": v(110.68, -44.56) * mm, "end": v(110.5, -44.37) * mm});
            skLineSegment(sketch, "E3897", {"start": v(110.5, -44.37) * mm, "end": v(110.32, -44.2) * mm});
            skLineSegment(sketch, "E3898", {"start": v(110.32, -44.2) * mm, "end": v(110.14, -44.01) * mm});
            skLineSegment(sketch, "E3899", {"start": v(110.14, -44.01) * mm, "end": v(110.32, -42.91) * mm});
            skLineSegment(sketch, "E3900", {"start": v(110.32, -42.91) * mm, "end": v(110.95, -41.99) * mm});
            skLineSegment(sketch, "E3901", {"start": v(110.95, -41.99) * mm, "end": v(111.2, -41.98) * mm});
            skLineSegment(sketch, "E3902", {"start": v(111.2, -41.98) * mm, "end": v(111.46, -41.97) * mm});
            skLineSegment(sketch, "E3903", {"start": v(111.46, -41.97) * mm, "end": v(111.71, -41.96) * mm});
            skLineSegment(sketch, "E3904", {"start": v(111.71, -41.96) * mm, "end": v(111.97, -41.95) * mm});
            skLineSegment(sketch, "E3905", {"start": v(111.97, -41.95) * mm, "end": v(112.24, -41.94) * mm});
            skLineSegment(sketch, "E3906", {"start": v(112.24, -41.94) * mm, "end": v(112.5, -41.92) * mm});
            skLineSegment(sketch, "E3907", {"start": v(112.5, -41.92) * mm, "end": v(112.78, -41.9) * mm});
            skLineSegment(sketch, "E3908", {"start": v(112.78, -41.9) * mm, "end": v(113.05, -41.89) * mm});
            skLineSegment(sketch, "E3909", {"start": v(113.05, -41.89) * mm, "end": v(113.33, -41.87) * mm});
            skLineSegment(sketch, "E3910", {"start": v(113.33, -41.87) * mm, "end": v(113.61, -41.84) * mm});
            skLineSegment(sketch, "E3911", {"start": v(113.61, -41.84) * mm, "end": v(113.9, -41.82) * mm});
            skLineSegment(sketch, "E3912", {"start": v(113.9, -41.82) * mm, "end": v(114.18, -41.8) * mm});
            skLineSegment(sketch, "E3913", {"start": v(114.18, -41.8) * mm, "end": v(114.48, -41.77) * mm});
            skLineSegment(sketch, "E3914", {"start": v(114.48, -41.77) * mm, "end": v(114.77, -41.74) * mm});
            skLineSegment(sketch, "E3915", {"start": v(114.77, -41.74) * mm, "end": v(115.06, -41.7) * mm});
            skLineSegment(sketch, "E3916", {"start": v(115.06, -41.7) * mm, "end": v(115.36, -41.67) * mm});
            skLineSegment(sketch, "E3917", {"start": v(115.36, -41.67) * mm, "end": v(115.67, -41.64) * mm});
            skLineSegment(sketch, "E3918", {"start": v(115.67, -41.64) * mm, "end": v(115.97, -41.6) * mm});
            skLineSegment(sketch, "E3919", {"start": v(115.97, -41.6) * mm, "end": v(116.28, -41.56) * mm});
            skLineSegment(sketch, "E3920", {"start": v(116.28, -41.56) * mm, "end": v(116.6, -41.52) * mm});
            skLineSegment(sketch, "E3921", {"start": v(116.6, -41.52) * mm, "end": v(116.9, -41.48) * mm});
            skLineSegment(sketch, "E3922", {"start": v(116.9, -41.48) * mm, "end": v(117.23, -41.43) * mm});
            skLineSegment(sketch, "E3923", {"start": v(117.23, -41.43) * mm, "end": v(117.55, -41.38) * mm});
            skLineSegment(sketch, "E3924", {"start": v(117.55, -41.38) * mm, "end": v(117.87, -41.33) * mm});
            skLineSegment(sketch, "E3925", {"start": v(117.87, -41.33) * mm, "end": v(118.2, -41.28) * mm});
            skLineSegment(sketch, "E3926", {"start": v(118.2, -41.28) * mm, "end": v(118.53, -41.22) * mm});
            skLineSegment(sketch, "E3927", {"start": v(118.53, -41.22) * mm, "end": v(118.86, -41.17) * mm});
            skLineSegment(sketch, "E3928", {"start": v(118.86, -41.17) * mm, "end": v(119.2, -41.1) * mm});
            skLineSegment(sketch, "E3929", {"start": v(119.2, -41.1) * mm, "end": v(119.53, -41.05) * mm});
            skLineSegment(sketch, "E3930", {"start": v(119.53, -41.05) * mm, "end": v(119.87, -40.98) * mm});
            skLineSegment(sketch, "E3931", {"start": v(119.87, -40.98) * mm, "end": v(119.94, -40.82) * mm});
            skLineSegment(sketch, "E3932", {"start": v(119.94, -40.82) * mm, "end": v(120.41, -39.45) * mm});
            skLineSegment(sketch, "E3933", {"start": v(120.41, -39.45) * mm, "end": v(120.46, -39.28) * mm});
            skLineSegment(sketch, "E3934", {"start": v(120.46, -39.28) * mm, "end": v(120.23, -39.02) * mm});
            skLineSegment(sketch, "E3935", {"start": v(120.23, -39.02) * mm, "end": v(120, -38.76) * mm});
            skLineSegment(sketch, "E3936", {"start": v(120, -38.76) * mm, "end": v(119.77, -38.5) * mm});
            skLineSegment(sketch, "E3937", {"start": v(119.77, -38.5) * mm, "end": v(119.54, -38.26) * mm});
            skLineSegment(sketch, "E3938", {"start": v(119.54, -38.26) * mm, "end": v(119.32, -38.01) * mm});
            skLineSegment(sketch, "E3939", {"start": v(119.32, -38.01) * mm, "end": v(119.1, -37.77) * mm});
            skLineSegment(sketch, "E3940", {"start": v(119.1, -37.77) * mm, "end": v(118.87, -37.53) * mm});
            skLineSegment(sketch, "E3941", {"start": v(118.87, -37.53) * mm, "end": v(118.64, -37.3) * mm});
            skLineSegment(sketch, "E3942", {"start": v(118.64, -37.3) * mm, "end": v(118.42, -37.07) * mm});
            skLineSegment(sketch, "E3943", {"start": v(118.42, -37.07) * mm, "end": v(118.2, -36.84) * mm});
            skLineSegment(sketch, "E3944", {"start": v(118.2, -36.84) * mm, "end": v(117.98, -36.61) * mm});
            skLineSegment(sketch, "E3945", {"start": v(117.98, -36.61) * mm, "end": v(117.76, -36.4) * mm});
            skLineSegment(sketch, "E3946", {"start": v(117.76, -36.4) * mm, "end": v(117.54, -36.17) * mm});
            skLineSegment(sketch, "E3947", {"start": v(117.54, -36.17) * mm, "end": v(117.32, -35.96) * mm});
            skLineSegment(sketch, "E3948", {"start": v(117.32, -35.96) * mm, "end": v(117.1, -35.75) * mm});
            skLineSegment(sketch, "E3949", {"start": v(117.1, -35.75) * mm, "end": v(116.9, -35.54) * mm});
            skLineSegment(sketch, "E3950", {"start": v(116.9, -35.54) * mm, "end": v(116.68, -35.34) * mm});
            skLineSegment(sketch, "E3951", {"start": v(116.68, -35.34) * mm, "end": v(116.47, -35.14) * mm});
            skLineSegment(sketch, "E3952", {"start": v(116.47, -35.14) * mm, "end": v(116.26, -34.94) * mm});
            skLineSegment(sketch, "E3953", {"start": v(116.26, -34.94) * mm, "end": v(116.05, -34.75) * mm});
            skLineSegment(sketch, "E3954", {"start": v(116.05, -34.75) * mm, "end": v(115.84, -34.56) * mm});
            skLineSegment(sketch, "E3955", {"start": v(115.84, -34.56) * mm, "end": v(115.63, -34.37) * mm});
            skLineSegment(sketch, "E3956", {"start": v(115.63, -34.37) * mm, "end": v(115.43, -34.2) * mm});
            skLineSegment(sketch, "E3957", {"start": v(115.43, -34.2) * mm, "end": v(115.22, -34.01) * mm});
            skLineSegment(sketch, "E3958", {"start": v(115.22, -34.01) * mm, "end": v(115.02, -33.83) * mm});
            skLineSegment(sketch, "E3959", {"start": v(115.02, -33.83) * mm, "end": v(114.82, -33.66) * mm});
            skLineSegment(sketch, "E3960", {"start": v(114.82, -33.66) * mm, "end": v(114.62, -33.5) * mm});
            skLineSegment(sketch, "E3961", {"start": v(114.62, -33.5) * mm, "end": v(114.42, -33.32) * mm});
            skLineSegment(sketch, "E3962", {"start": v(114.42, -33.32) * mm, "end": v(114.22, -33.16) * mm});
            skLineSegment(sketch, "E3963", {"start": v(114.22, -33.16) * mm, "end": v(114.03, -33) * mm});
            skLineSegment(sketch, "E3964", {"start": v(114.03, -33) * mm, "end": v(114.1, -31.89) * mm});
            skLineSegment(sketch, "E3965", {"start": v(114.1, -31.89) * mm, "end": v(114.64, -30.9) * mm});
            skLineSegment(sketch, "E3966", {"start": v(114.64, -30.9) * mm, "end": v(114.89, -30.87) * mm});
            skLineSegment(sketch, "E3967", {"start": v(114.89, -30.87) * mm, "end": v(115.14, -30.84) * mm});
            skLineSegment(sketch, "E3968", {"start": v(115.14, -30.84) * mm, "end": v(115.4, -30.8) * mm});
            skLineSegment(sketch, "E3969", {"start": v(115.4, -30.8) * mm, "end": v(115.66, -30.77) * mm});
            skLineSegment(sketch, "E3970", {"start": v(115.66, -30.77) * mm, "end": v(115.92, -30.73) * mm});
            skLineSegment(sketch, "E3971", {"start": v(115.92, -30.73) * mm, "end": v(116.18, -30.69) * mm});
            skLineSegment(sketch, "E3972", {"start": v(116.18, -30.69) * mm, "end": v(116.45, -30.64) * mm});
            skLineSegment(sketch, "E3973", {"start": v(116.45, -30.64) * mm, "end": v(116.72, -30.6) * mm});
            skLineSegment(sketch, "E3974", {"start": v(116.72, -30.6) * mm, "end": v(117, -30.55) * mm});
            skLineSegment(sketch, "E3975", {"start": v(117, -30.55) * mm, "end": v(117.28, -30.5) * mm});
            skLineSegment(sketch, "E3976", {"start": v(117.28, -30.5) * mm, "end": v(117.56, -30.45) * mm});
            skLineSegment(sketch, "E3977", {"start": v(117.56, -30.45) * mm, "end": v(117.84, -30.4) * mm});
            skLineSegment(sketch, "E3978", {"start": v(117.84, -30.4) * mm, "end": v(118.13, -30.34) * mm});
            skLineSegment(sketch, "E3979", {"start": v(118.13, -30.34) * mm, "end": v(118.42, -30.28) * mm});
            skLineSegment(sketch, "E3980", {"start": v(118.42, -30.28) * mm, "end": v(118.7, -30.22) * mm});
            skLineSegment(sketch, "E3981", {"start": v(118.7, -30.22) * mm, "end": v(119, -30.16) * mm});
            skLineSegment(sketch, "E3982", {"start": v(119, -30.16) * mm, "end": v(119.3, -30.1) * mm});
            skLineSegment(sketch, "E3983", {"start": v(119.3, -30.1) * mm, "end": v(119.6, -30.03) * mm});
            skLineSegment(sketch, "E3984", {"start": v(119.6, -30.03) * mm, "end": v(119.9, -29.96) * mm});
            skLineSegment(sketch, "E3985", {"start": v(119.9, -29.96) * mm, "end": v(120.2, -29.89) * mm});
            skLineSegment(sketch, "E3986", {"start": v(120.2, -29.89) * mm, "end": v(120.52, -29.81) * mm});
            skLineSegment(sketch, "E3987", {"start": v(120.52, -29.81) * mm, "end": v(120.83, -29.74) * mm});
            skLineSegment(sketch, "E3988", {"start": v(120.83, -29.74) * mm, "end": v(121.15, -29.66) * mm});
            skLineSegment(sketch, "E3989", {"start": v(121.15, -29.66) * mm, "end": v(121.46, -29.57) * mm});
            skLineSegment(sketch, "E3990", {"start": v(121.46, -29.57) * mm, "end": v(121.78, -29.49) * mm});
            skLineSegment(sketch, "E3991", {"start": v(121.78, -29.49) * mm, "end": v(122.1, -29.4) * mm});
            skLineSegment(sketch, "E3992", {"start": v(122.1, -29.4) * mm, "end": v(122.43, -29.31) * mm});
            skLineSegment(sketch, "E3993", {"start": v(122.43, -29.31) * mm, "end": v(122.76, -29.22) * mm});
            skLineSegment(sketch, "E3994", {"start": v(122.76, -29.22) * mm, "end": v(123.09, -29.13) * mm});
            skLineSegment(sketch, "E3995", {"start": v(123.09, -29.13) * mm, "end": v(123.42, -29.03) * mm});
            skLineSegment(sketch, "E3996", {"start": v(123.42, -29.03) * mm, "end": v(123.48, -28.86) * mm});
            skLineSegment(sketch, "E3997", {"start": v(123.48, -28.86) * mm, "end": v(123.8, -27.45) * mm});
            skLineSegment(sketch, "E3998", {"start": v(123.8, -27.45) * mm, "end": v(123.83, -27.28) * mm});
            skLineSegment(sketch, "E3999", {"start": v(123.83, -27.28) * mm, "end": v(123.58, -27.04) * mm});
            skLineSegment(sketch, "E4000", {"start": v(123.58, -27.04) * mm, "end": v(123.33, -26.8) * mm});
            skLineSegment(sketch, "E4001", {"start": v(123.33, -26.8) * mm, "end": v(123.08, -26.58) * mm});
            skLineSegment(sketch, "E4002", {"start": v(123.08, -26.58) * mm, "end": v(122.83, -26.35) * mm});
            skLineSegment(sketch, "E4003", {"start": v(122.83, -26.35) * mm, "end": v(122.58, -26.13) * mm});
            skLineSegment(sketch, "E4004", {"start": v(122.58, -26.13) * mm, "end": v(122.33, -25.9) * mm});
            skLineSegment(sketch, "E4005", {"start": v(122.33, -25.9) * mm, "end": v(122.08, -25.7) * mm});
            skLineSegment(sketch, "E4006", {"start": v(122.08, -25.7) * mm, "end": v(121.84, -25.48) * mm});
            skLineSegment(sketch, "E4007", {"start": v(121.84, -25.48) * mm, "end": v(121.6, -25.27) * mm});
            skLineSegment(sketch, "E4008", {"start": v(121.6, -25.27) * mm, "end": v(121.35, -25.07) * mm});
            skLineSegment(sketch, "E4009", {"start": v(121.35, -25.07) * mm, "end": v(121.1, -24.87) * mm});
            skLineSegment(sketch, "E4010", {"start": v(121.1, -24.87) * mm, "end": v(120.87, -24.67) * mm});
            skLineSegment(sketch, "E4011", {"start": v(120.87, -24.67) * mm, "end": v(120.63, -24.47) * mm});
            skLineSegment(sketch, "E4012", {"start": v(120.63, -24.47) * mm, "end": v(120.4, -24.28) * mm});
            skLineSegment(sketch, "E4013", {"start": v(120.4, -24.28) * mm, "end": v(120.16, -24.1) * mm});
            skLineSegment(sketch, "E4014", {"start": v(120.16, -24.1) * mm, "end": v(119.92, -23.9) * mm});
            skLineSegment(sketch, "E4015", {"start": v(119.92, -23.9) * mm, "end": v(119.7, -23.73) * mm});
            skLineSegment(sketch, "E4016", {"start": v(119.7, -23.73) * mm, "end": v(119.46, -23.55) * mm});
            skLineSegment(sketch, "E4017", {"start": v(119.46, -23.55) * mm, "end": v(119.23, -23.38) * mm});
            skLineSegment(sketch, "E4018", {"start": v(119.23, -23.38) * mm, "end": v(119, -23.2) * mm});
            skLineSegment(sketch, "E4019", {"start": v(119, -23.2) * mm, "end": v(118.78, -23.04) * mm});
            skLineSegment(sketch, "E4020", {"start": v(118.78, -23.04) * mm, "end": v(118.55, -22.87) * mm});
            skLineSegment(sketch, "E4021", {"start": v(118.55, -22.87) * mm, "end": v(118.33, -22.7) * mm});
            skLineSegment(sketch, "E4022", {"start": v(118.33, -22.7) * mm, "end": v(118.1, -22.55) * mm});
            skLineSegment(sketch, "E4023", {"start": v(118.1, -22.55) * mm, "end": v(117.9, -22.4) * mm});
            skLineSegment(sketch, "E4024", {"start": v(117.9, -22.4) * mm, "end": v(117.68, -22.24) * mm});
            skLineSegment(sketch, "E4025", {"start": v(117.68, -22.24) * mm, "end": v(117.46, -22.09) * mm});
            skLineSegment(sketch, "E4026", {"start": v(117.46, -22.09) * mm, "end": v(117.25, -21.94) * mm});
            skLineSegment(sketch, "E4027", {"start": v(117.25, -21.94) * mm, "end": v(117.03, -21.8) * mm});
            skLineSegment(sketch, "E4028", {"start": v(117.03, -21.8) * mm, "end": v(116.83, -21.66) * mm});
            skLineSegment(sketch, "E4029", {"start": v(116.83, -21.66) * mm, "end": v(116.8, -20.54) * mm});
            skLineSegment(sketch, "E4030", {"start": v(116.8, -20.54) * mm, "end": v(117.22, -19.52) * mm});
            skLineSegment(sketch, "E4031", {"start": v(117.22, -19.52) * mm, "end": v(117.47, -19.46) * mm});
            skLineSegment(sketch, "E4032", {"start": v(117.47, -19.46) * mm, "end": v(117.72, -19.4) * mm});
            skLineSegment(sketch, "E4033", {"start": v(117.72, -19.4) * mm, "end": v(117.97, -19.34) * mm});
            skLineSegment(sketch, "E4034", {"start": v(117.97, -19.34) * mm, "end": v(118.22, -19.28) * mm});
            skLineSegment(sketch, "E4035", {"start": v(118.22, -19.28) * mm, "end": v(118.48, -19.21) * mm});
            skLineSegment(sketch, "E4036", {"start": v(118.48, -19.21) * mm, "end": v(118.74, -19.15) * mm});
            skLineSegment(sketch, "E4037", {"start": v(118.74, -19.15) * mm, "end": v(119, -19.08) * mm});
            skLineSegment(sketch, "E4038", {"start": v(119, -19.08) * mm, "end": v(119.27, -19) * mm});
            skLineSegment(sketch, "E4039", {"start": v(119.27, -19) * mm, "end": v(119.54, -18.93) * mm});
            skLineSegment(sketch, "E4040", {"start": v(119.54, -18.93) * mm, "end": v(119.81, -18.85) * mm});
            skLineSegment(sketch, "E4041", {"start": v(119.81, -18.85) * mm, "end": v(120.08, -18.78) * mm});
            skLineSegment(sketch, "E4042", {"start": v(120.08, -18.78) * mm, "end": v(120.36, -18.7) * mm});
            skLineSegment(sketch, "E4043", {"start": v(120.36, -18.7) * mm, "end": v(120.64, -18.61) * mm});
            skLineSegment(sketch, "E4044", {"start": v(120.64, -18.61) * mm, "end": v(120.92, -18.53) * mm});
            skLineSegment(sketch, "E4045", {"start": v(120.92, -18.53) * mm, "end": v(121.2, -18.44) * mm});
            skLineSegment(sketch, "E4046", {"start": v(121.2, -18.44) * mm, "end": v(121.5, -18.35) * mm});
            skLineSegment(sketch, "E4047", {"start": v(121.5, -18.35) * mm, "end": v(121.78, -18.25) * mm});
            skLineSegment(sketch, "E4048", {"start": v(121.78, -18.25) * mm, "end": v(122.08, -18.16) * mm});
            skLineSegment(sketch, "E4049", {"start": v(122.08, -18.16) * mm, "end": v(122.37, -18.06) * mm});
            skLineSegment(sketch, "E4050", {"start": v(122.37, -18.06) * mm, "end": v(122.67, -17.95) * mm});
            skLineSegment(sketch, "E4051", {"start": v(122.67, -17.95) * mm, "end": v(122.97, -17.85) * mm});
            skLineSegment(sketch, "E4052", {"start": v(122.97, -17.85) * mm, "end": v(123.27, -17.74) * mm});
            skLineSegment(sketch, "E4053", {"start": v(123.27, -17.74) * mm, "end": v(123.58, -17.63) * mm});
            skLineSegment(sketch, "E4054", {"start": v(123.58, -17.63) * mm, "end": v(123.89, -17.52) * mm});
            skLineSegment(sketch, "E4055", {"start": v(123.89, -17.52) * mm, "end": v(124.2, -17.4) * mm});
            skLineSegment(sketch, "E4056", {"start": v(124.2, -17.4) * mm, "end": v(124.5, -17.29) * mm});
            skLineSegment(sketch, "E4057", {"start": v(124.5, -17.29) * mm, "end": v(124.82, -17.17) * mm});
            skLineSegment(sketch, "E4058", {"start": v(124.82, -17.17) * mm, "end": v(125.14, -17.04) * mm});
            skLineSegment(sketch, "E4059", {"start": v(125.14, -17.04) * mm, "end": v(125.46, -16.92) * mm});
            skLineSegment(sketch, "E4060", {"start": v(125.46, -16.92) * mm, "end": v(125.78, -16.79) * mm});
            skLineSegment(sketch, "E4061", {"start": v(125.78, -16.79) * mm, "end": v(125.82, -16.61) * mm});
            skLineSegment(sketch, "E4062", {"start": v(125.82, -16.61) * mm, "end": v(126.01, -15.18) * mm});
            skLineSegment(sketch, "E4063", {"start": v(126.01, -15.18) * mm, "end": v(126.02, -15) * mm});
            skLineSegment(sketch, "E4064", {"start": v(126.02, -15) * mm, "end": v(125.74, -14.8) * mm});
            skLineSegment(sketch, "E4065", {"start": v(125.74, -14.8) * mm, "end": v(125.47, -14.58) * mm});
            skLineSegment(sketch, "E4066", {"start": v(125.47, -14.58) * mm, "end": v(125.2, -14.38) * mm});
            skLineSegment(sketch, "E4067", {"start": v(125.2, -14.38) * mm, "end": v(124.93, -14.18) * mm});
            skLineSegment(sketch, "E4068", {"start": v(124.93, -14.18) * mm, "end": v(124.66, -13.98) * mm});
            skLineSegment(sketch, "E4069", {"start": v(124.66, -13.98) * mm, "end": v(124.39, -13.79) * mm});
            skLineSegment(sketch, "E4070", {"start": v(124.39, -13.79) * mm, "end": v(124.12, -13.6) * mm});
            skLineSegment(sketch, "E4071", {"start": v(124.12, -13.6) * mm, "end": v(123.86, -13.41) * mm});
            skLineSegment(sketch, "E4072", {"start": v(123.86, -13.41) * mm, "end": v(123.6, -13.23) * mm});
            skLineSegment(sketch, "E4073", {"start": v(123.6, -13.23) * mm, "end": v(123.33, -13.05) * mm});
            skLineSegment(sketch, "E4074", {"start": v(123.33, -13.05) * mm, "end": v(123.07, -12.87) * mm});
            skLineSegment(sketch, "E4075", {"start": v(123.07, -12.87) * mm, "end": v(122.81, -12.7) * mm});
            skLineSegment(sketch, "E4076", {"start": v(122.81, -12.7) * mm, "end": v(122.56, -12.53) * mm});
            skLineSegment(sketch, "E4077", {"start": v(122.56, -12.53) * mm, "end": v(122.3, -12.36) * mm});
            skLineSegment(sketch, "E4078", {"start": v(122.3, -12.36) * mm, "end": v(122.05, -12.2) * mm});
            skLineSegment(sketch, "E4079", {"start": v(122.05, -12.2) * mm, "end": v(121.8, -12.04) * mm});
            skLineSegment(sketch, "E4080", {"start": v(121.8, -12.04) * mm, "end": v(121.55, -11.88) * mm});
            skLineSegment(sketch, "E4081", {"start": v(121.55, -11.88) * mm, "end": v(121.3, -11.72) * mm});
            skLineSegment(sketch, "E4082", {"start": v(121.3, -11.72) * mm, "end": v(121.06, -11.57) * mm});
            skLineSegment(sketch, "E4083", {"start": v(121.06, -11.57) * mm, "end": v(120.81, -11.42) * mm});
            skLineSegment(sketch, "E4084", {"start": v(120.81, -11.42) * mm, "end": v(120.57, -11.28) * mm});
            skLineSegment(sketch, "E4085", {"start": v(120.57, -11.28) * mm, "end": v(120.33, -11.13) * mm});
            skLineSegment(sketch, "E4086", {"start": v(120.33, -11.13) * mm, "end": v(120.1, -11) * mm});
            skLineSegment(sketch, "E4087", {"start": v(120.1, -11) * mm, "end": v(119.86, -10.86) * mm});
            skLineSegment(sketch, "E4088", {"start": v(119.86, -10.86) * mm, "end": v(119.63, -10.72) * mm});
            skLineSegment(sketch, "E4089", {"start": v(119.63, -10.72) * mm, "end": v(119.4, -10.6) * mm});
            skLineSegment(sketch, "E4090", {"start": v(119.4, -10.6) * mm, "end": v(119.17, -10.47) * mm});
            skLineSegment(sketch, "E4091", {"start": v(119.17, -10.47) * mm, "end": v(118.94, -10.34) * mm});
            skLineSegment(sketch, "E4092", {"start": v(118.94, -10.34) * mm, "end": v(118.72, -10.22) * mm});
            skLineSegment(sketch, "E4093", {"start": v(118.72, -10.22) * mm, "end": v(118.5, -10.1) * mm});
            skLineSegment(sketch, "E4094", {"start": v(118.5, -10.1) * mm, "end": v(118.35, -9) * mm});
            skLineSegment(sketch, "E4095", {"start": v(118.35, -9) * mm, "end": v(118.68, -7.93) * mm});
            skLineSegment(sketch, "E4096", {"start": v(118.68, -7.93) * mm, "end": v(118.92, -7.85) * mm});
            skLineSegment(sketch, "E4097", {"start": v(118.92, -7.85) * mm, "end": v(119.16, -7.76) * mm});
            skLineSegment(sketch, "E4098", {"start": v(119.16, -7.76) * mm, "end": v(119.4, -7.68) * mm});
            skLineSegment(sketch, "E4099", {"start": v(119.4, -7.68) * mm, "end": v(119.65, -7.6) * mm});
            skLineSegment(sketch, "E4100", {"start": v(119.65, -7.6) * mm, "end": v(119.9, -7.5) * mm});
            skLineSegment(sketch, "E4101", {"start": v(119.9, -7.5) * mm, "end": v(120.16, -7.41) * mm});
            skLineSegment(sketch, "E4102", {"start": v(120.16, -7.41) * mm, "end": v(120.4, -7.31) * mm});
            skLineSegment(sketch, "E4103", {"start": v(120.4, -7.31) * mm, "end": v(120.67, -7.22) * mm});
            skLineSegment(sketch, "E4104", {"start": v(120.67, -7.22) * mm, "end": v(120.93, -7.12) * mm});
            skLineSegment(sketch, "E4105", {"start": v(120.93, -7.12) * mm, "end": v(121.19, -7.01) * mm});
            skLineSegment(sketch, "E4106", {"start": v(121.19, -7.01) * mm, "end": v(121.45, -6.9) * mm});
            skLineSegment(sketch, "E4107", {"start": v(121.45, -6.9) * mm, "end": v(121.72, -6.8) * mm});
            skLineSegment(sketch, "E4108", {"start": v(121.72, -6.8) * mm, "end": v(122, -6.7) * mm});
            skLineSegment(sketch, "E4109", {"start": v(122, -6.7) * mm, "end": v(122.26, -6.58) * mm});
            skLineSegment(sketch, "E4110", {"start": v(122.26, -6.58) * mm, "end": v(122.54, -6.46) * mm});
            skLineSegment(sketch, "E4111", {"start": v(122.54, -6.46) * mm, "end": v(122.81, -6.34) * mm});
            skLineSegment(sketch, "E4112", {"start": v(122.81, -6.34) * mm, "end": v(123.1, -6.22) * mm});
            skLineSegment(sketch, "E4113", {"start": v(123.1, -6.22) * mm, "end": v(123.38, -6.1) * mm});
            skLineSegment(sketch, "E4114", {"start": v(123.38, -6.1) * mm, "end": v(123.66, -5.97) * mm});
            skLineSegment(sketch, "E4115", {"start": v(123.66, -5.97) * mm, "end": v(123.95, -5.84) * mm});
            skLineSegment(sketch, "E4116", {"start": v(123.95, -5.84) * mm, "end": v(124.24, -5.7) * mm});
            skLineSegment(sketch, "E4117", {"start": v(124.24, -5.7) * mm, "end": v(124.53, -5.57) * mm});
            skLineSegment(sketch, "E4118", {"start": v(124.53, -5.57) * mm, "end": v(124.82, -5.43) * mm});
            skLineSegment(sketch, "E4119", {"start": v(124.82, -5.43) * mm, "end": v(125.12, -5.29) * mm});
            skLineSegment(sketch, "E4120", {"start": v(125.12, -5.29) * mm, "end": v(125.41, -5.14) * mm});
            skLineSegment(sketch, "E4121", {"start": v(125.41, -5.14) * mm, "end": v(125.71, -5) * mm});
            skLineSegment(sketch, "E4122", {"start": v(125.71, -5) * mm, "end": v(126.01, -4.84) * mm});
            skLineSegment(sketch, "E4123", {"start": v(126.01, -4.84) * mm, "end": v(126.32, -4.69) * mm});
            skLineSegment(sketch, "E4124", {"start": v(126.32, -4.69) * mm, "end": v(126.62, -4.53) * mm});
            skLineSegment(sketch, "E4125", {"start": v(126.62, -4.53) * mm, "end": v(126.93, -4.37) * mm});
            skLineSegment(sketch, "E4126", {"start": v(126.93, -4.37) * mm, "end": v(126.95, -4.2) * mm});
            skLineSegment(sketch, "E4127", {"start": v(126.95, -4.2) * mm, "end": v(127, -2.75) * mm});
            skLineSegment(sketch, "E4128", {"start": v(127, -2.75) * mm, "end": v(127, -2.57) * mm});
            skLineSegment(sketch, "E4129", {"start": v(127, -2.57) * mm, "end": v(126.7, -2.39) * mm});
            skLineSegment(sketch, "E4130", {"start": v(126.7, -2.39) * mm, "end": v(126.4, -2.2) * mm});
            skLineSegment(sketch, "E4131", {"start": v(126.4, -2.2) * mm, "end": v(126.11, -2.03) * mm});
            skLineSegment(sketch, "E4132", {"start": v(126.11, -2.03) * mm, "end": v(125.82, -1.86) * mm});
            skLineSegment(sketch, "E4133", {"start": v(125.82, -1.86) * mm, "end": v(125.54, -1.7) * mm});
            skLineSegment(sketch, "E4134", {"start": v(125.54, -1.7) * mm, "end": v(125.25, -1.52) * mm});
            skLineSegment(sketch, "E4135", {"start": v(125.25, -1.52) * mm, "end": v(124.96, -1.36) * mm});
            skLineSegment(sketch, "E4136", {"start": v(124.96, -1.36) * mm, "end": v(124.68, -1.2) * mm});
            skLineSegment(sketch, "E4137", {"start": v(124.68, -1.2) * mm, "end": v(124.4, -1.05) * mm});
            skLineSegment(sketch, "E4138", {"start": v(124.4, -1.05) * mm, "end": v(124.12, -0.9) * mm});
            skLineSegment(sketch, "E4139", {"start": v(124.12, -0.9) * mm, "end": v(123.85, -0.74) * mm});
            skLineSegment(sketch, "E4140", {"start": v(123.85, -0.74) * mm, "end": v(123.57, -0.6) * mm});
            skLineSegment(sketch, "E4141", {"start": v(123.57, -0.6) * mm, "end": v(123.3, -0.45) * mm});
            skLineSegment(sketch, "E4142", {"start": v(123.3, -0.45) * mm, "end": v(123.03, -0.3) * mm});
            skLineSegment(sketch, "E4143", {"start": v(123.03, -0.3) * mm, "end": v(122.77, -0.17) * mm});
            skLineSegment(sketch, "E4144", {"start": v(122.77, -0.17) * mm, "end": v(122.5, -0.03) * mm});
            skLineSegment(sketch, "E4145", {"start": v(122.5, -0.03) * mm, "end": v(122.24, 0.1) * mm});
            skLineSegment(sketch, "E4146", {"start": v(122.24, 0.1) * mm, "end": v(121.97, 0.23) * mm});
            skLineSegment(sketch, "E4147", {"start": v(121.97, 0.23) * mm, "end": v(121.72, 0.36) * mm});
            skLineSegment(sketch, "E4148", {"start": v(121.72, 0.36) * mm, "end": v(121.46, 0.48) * mm});
            skLineSegment(sketch, "E4149", {"start": v(121.46, 0.48) * mm, "end": v(121.2, 0.6) * mm});
            skLineSegment(sketch, "E4150", {"start": v(121.2, 0.6) * mm, "end": v(120.95, 0.72) * mm});
            skLineSegment(sketch, "E4151", {"start": v(120.95, 0.72) * mm, "end": v(120.7, 0.83) * mm});
            skLineSegment(sketch, "E4152", {"start": v(120.7, 0.83) * mm, "end": v(120.45, 0.95) * mm});
            skLineSegment(sketch, "E4153", {"start": v(120.45, 0.95) * mm, "end": v(120.21, 1.06) * mm});
            skLineSegment(sketch, "E4154", {"start": v(120.21, 1.06) * mm, "end": v(119.97, 1.17) * mm});
            skLineSegment(sketch, "E4155", {"start": v(119.97, 1.17) * mm, "end": v(119.73, 1.27) * mm});
            skLineSegment(sketch, "E4156", {"start": v(119.73, 1.27) * mm, "end": v(119.5, 1.37) * mm});
            skLineSegment(sketch, "E4157", {"start": v(119.5, 1.37) * mm, "end": v(119.25, 1.47) * mm});
            skLineSegment(sketch, "E4158", {"start": v(119.25, 1.47) * mm, "end": v(119.02, 1.57) * mm});
            skLineSegment(sketch, "E4159", {"start": v(119.02, 1.57) * mm, "end": v(118.77, 2.66) * mm});
            skLineSegment(sketch, "E4160", {"start": v(1.54, 1.1) * mm, "end": v(-1.54, 1.1) * mm});
            skLineSegment(sketch, "E4161", {"start": v(0, -0.43) * mm, "end": v(0, 2.65) * mm});
            skPoint(sketch, "E4162.middle", {"position": v(0, 2.65) * mm});
            skSolve(sketch);
        }
        {
            var Q0;
            Q0=makeQuery(id+"F0.imprint","IMPRINT",FACE,{"disambiguationData":[TD([[makeQuery(id+"F0.imprint","IMPRINT",EDGE,{"derivedFrom":sQuery(id+"F0.wireOp",EDGE,"E0")}),1.0]])]});
            extrude(context, id + "F1", {"entities" : qUnion([Q0]), "depth" : 25.4 * mm});
        }
    });
